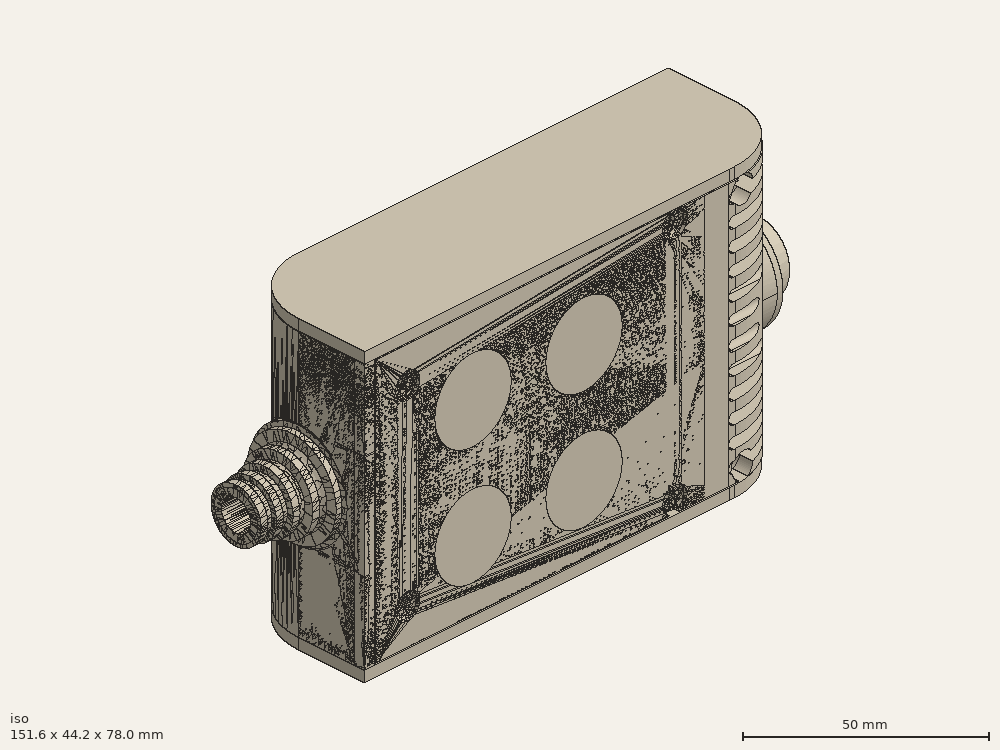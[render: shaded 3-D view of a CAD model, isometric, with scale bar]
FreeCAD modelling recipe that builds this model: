
FCSTD DOCUMENT  (FreeCAD 0.19R0.19.2)
Label: enclosure_175FCStd
License: All rights reserved
LicenseURL: http://en.wikipedia.org/wiki/All_rights_reserved
objects: Part::Revolution×152, Part::MultiFuse×146, Part::Feature×146, Sketcher::SketchObject×82, Part::Cut×70, Part::Cylinder×70, Part::Extrusion×67, Part::Fillet×58, Part::Box×36, App::MeasureDistance×4
note: 827 computed .brp shape members not serialized (recipe doc carries the construction recipe); baked Part::Feature solids carry a one-line shape summary decoded from their .brp

FEATURE [Sketcher::SketchObject] Sketch  label="topSketch"
  FullyConstrained = true
  sketch-geometry (20):
    g0: LineSegment StartX=5.21097e-06 StartY=3 StartZ=0 EndX=5.21097e-06 EndY=19 EndZ=0
    g1: ArcOfCircle CenterX=19 CenterY=19 CenterZ=0 NormalX=0 NormalY=0 NormalZ=1 AngleXU=0 Radius=19 StartAngle=1.5708 EndAngle=3.14159
    g2: ArcOfCircle CenterX=19 CenterY=19 CenterZ=0 NormalX=0 NormalY=0 NormalZ=1 AngleXU=0 Radius=16 StartAngle=1.5708 EndAngle=3.14159
    g3: LineSegment StartX=114 StartY=35 StartZ=0 EndX=19 EndY=35 EndZ=0
    g4: LineSegment StartX=5.21097e-06 StartY=3 StartZ=0 EndX=5.21097e-06 EndY=0 EndZ=0
    g5: LineSegment StartX=3 StartY=0 StartZ=0 EndX=5.21097e-06 EndY=0 EndZ=0
    g6: LineSegment StartX=3 StartY=19 StartZ=0 EndX=3 EndY=0 EndZ=0
    g7: LineSegment StartX=19 StartY=38 StartZ=0 EndX=124 EndY=38 EndZ=0
    g8: Circle CenterX=119 CenterY=35 CenterZ=0 NormalX=0 NormalY=0 NormalZ=1 AngleXU=0 Radius=1
    g9: Circle CenterX=121 CenterY=35 CenterZ=0 NormalX=0 NormalY=0 NormalZ=1 AngleXU=0 Radius=1
    g10: Circle CenterX=121 CenterY=33 CenterZ=0 NormalX=0 NormalY=0 NormalZ=1 AngleXU=0 Radius=1
    g11: BSplineCurve PolesCount=3 KnotsCount=2 Degree=2 IsPeriodic=0
    g12: GeomPoint X=119 Y=35 Z=0
    g13: GeomPoint X=121 Y=33 Z=0
    g14: LineSegment StartX=119 StartY=35 StartZ=0 EndX=114 EndY=35 EndZ=0
    g15: ArcOfCircle CenterX=105 CenterY=19 CenterZ=0 NormalX=0 NormalY=0 NormalZ=1 AngleXU=0 Radius=19 StartAngle=5.7297 EndAngle=6.28319
    g16: ArcOfCircle CenterX=105 CenterY=19 CenterZ=0 NormalX=0 NormalY=0 NormalZ=1 AngleXU=0 Radius=16 StartAngle=5.60905 EndAngle=6.28319
    g17: LineSegment StartX=121 StartY=33 StartZ=0 EndX=121 EndY=19 EndZ=0
    g18: LineSegment StartX=124 StartY=38 StartZ=0 EndX=124 EndY=19 EndZ=0
    g19: LineSegment StartX=117.5 StartY=9.01251 StartZ=0 EndX=121.163 EndY=9.0125 EndZ=0
  constraints (46):
    c: Vertical(g0)
    c: Block(g0)
    c: Coincident(g1,g0)
    c: Block(g1)
    c: Coincident(g2,g1)
    c: Block(g2)
    c: Coincident(g3,g2)
    c: Horizontal(g3)
    c: Tangent(g3,g2)
    c: Coincident(g4,g0)
    c: Distance(g4) = 3
    c: Vertical(g4)
    c: Coincident(g5,g4)
    c: Horizontal(g5)
    c: Coincident(g6,g2)
    c: Coincident(g6,g5)
    c: Vertical(g6)
    c: Horizontal(g7)
    c: Distance(g7) = 105
    c: Coincident(g7,g1)
    c: Block(g3)
    c: Weight(g8) = 1
    c: Equal(g8,g9)
    c: Equal(g8,g10)
    c: InternalAlignment(g8,g11)
    c: InternalAlignment(g9,g11)
    c: InternalAlignment(g10,g11)
    c: InternalAlignment(g12,g11)
    c: InternalAlignment(g13,g11)
    c: Block(g11)
    c: Coincident(g14,g11)
    c: Coincident(g14,g3)
    c: Horizontal(g14)
    c: Block(g15)
    c: Coincident(g16,g15)
    c: Block(g16)
    c: Coincident(g17,g11)
    c: Coincident(g17,g16)
    c: Vertical(g17)
    c: Distance(g17) = 14
    c: Coincident(g18,g7)
    c: Coincident(g18,g15)
    c: Vertical(g18)
    c: Distance(g18) = 19
    c: Coincident(g19,g16)
    c: Coincident(g19,g15)
FEATURE [Sketcher::SketchObject] Sketch001  label="bottomSketch"
  FullyConstrained = true
  sketch-geometry (32):
    g0: LineSegment StartX=3.3 StartY=-6.03275e-07 StartZ=0 EndX=98 EndY=-6.03275e-07 EndZ=0
    g1: ArcOfCircle CenterX=98 CenterY=19 CenterZ=0 NormalX=0 NormalY=0 NormalZ=1 AngleXU=0 Radius=19 StartAngle=4.71239 EndAngle=5.71103
    g2: LineSegment StartX=6.3 StartY=8 StartZ=0 EndX=3.3 EndY=8 EndZ=0
    g3: LineSegment StartX=3.3 StartY=8 StartZ=0 EndX=3.3 EndY=-6.03275e-07 EndZ=0
    g4: ArcOfCircle CenterX=8.3 CenterY=5 CenterZ=0 NormalX=0 NormalY=0 NormalZ=1 AngleXU=0 Radius=2 StartAngle=3.14159 EndAngle=4.71239
    g5: LineSegment StartX=6.3 StartY=8 StartZ=0 EndX=6.3 EndY=5 EndZ=0
    g6: ArcOfCircle CenterX=98 CenterY=19 CenterZ=0 NormalX=0 NormalY=0 NormalZ=1 AngleXU=0 Radius=12.7 StartAngle=4.71239 EndAngle=6.28319
    g7: LineSegment StartX=94.7 StartY=3 StartZ=0 EndX=8.3 EndY=3 EndZ=0
    g8-g12: Circle x5 (B-spline internal-alignment scaffolding for g13; pole/knot coordinates omitted)
    g13: BSplineCurve PolesCount=5 KnotsCount=3 Degree=3 IsPeriodic=0
    g14: GeomPoint X=98 Y=6.3 Z=0
    g15: GeomPoint X=96.3938 Y=4.71946 Z=0
    g16: GeomPoint X=94.7 Y=3 Z=0
    g17-g23: Circle x7 (B-spline internal-alignment scaffolding for g24; pole/knot coordinates omitted)
    g24: BSplineCurve PolesCount=7 KnotsCount=5 Degree=3 IsPeriodic=0
    g25-g29: GeomPoint x5 (B-spline internal-alignment scaffolding for g24; pole/knot coordinates omitted)
    g30: ArcOfCircle CenterX=98 CenterY=19 CenterZ=0 NormalX=0 NormalY=0 NormalZ=1 AngleXU=0 Radius=15.7 StartAngle=5.81226 EndAngle=6.28319
    g31: LineSegment StartX=110.7 StartY=19 StartZ=0 EndX=113.7 EndY=19 EndZ=0
  constraints (41):
    c: Horizontal(g0)
    c: Coincident(g1,g0)
    c: Block(g1)
    c: Horizontal(g2)
    c: Distance(g2) = 3
    c: Coincident(g3,g2)
    c: Vertical(g3)
    c: Coincident(g3,g0)
    c: Block(g4)
    c: Block(g2)
    c: Coincident(g5,g2)
    c: Coincident(g5,g4)
    c: Vertical(g5)
    c: Coincident(g6,g1)
    c: Block(g6)
    c: Coincident(g7,g4)
    c: Horizontal(g7)
    c: Block(g0)
    c: Block(g7)
    c: Block(g3)
    c: Coincident(g13,g6)
    c: Weight(g8) = 1
    c: Equal(g8, g9-g12) x4
    c: Coincident(g13,g7)
    c: InternalAlignment(g8-g12 -> g13) x5
    c: InternalAlignment(g14,g13)
    c: InternalAlignment(g15,g13)
    c: InternalAlignment(g16,g13)
    c: Block(g13)
    c: Weight(g17) = 1
    c: Equal(g17, g18-g23) x6
    c: Coincident(g24,g1)
    c: InternalAlignment(g17-g23 -> g24) x7
    c: InternalAlignment(g25-g29 -> g24) x5
    c: Block(g24)
    c: Coincident(g30,g24)
    c: Coincident(g31,g6)
    c: Coincident(g31,g30)
    c: Horizontal(g31)
    c: Block(g31)
    c: Block(g30)
FEATURE [Part::Extrusion] Extrude  label="top"
  Base = -> Sketch
  Dir = (0,0,1)
  DirMode = 2
  FaceMakerClass = Part::FaceMakerBullseye
  LengthFwd = 72
  LengthRev = 0
  Solid = true
  Symmetric = false
FEATURE [Part::Extrusion] Extrude001  label="bottom"
  Base = -> Sketch001
  Dir = (0,0,1)
  DirMode = 2
  FaceMakerClass = Part::FaceMakerBullseye
  LengthFwd = 71.4
  LengthRev = 0
  Placement = pos=(0,0,0.3) rot=(0,0,1;0rad)
  Solid = true
  Symmetric = false
FEATURE [Sketcher::SketchObject] Sketch002  label="topSketch001"
  FullyConstrained = true
  sketch-geometry (8):
    g0: ArcOfCircle CenterX=19 CenterY=19.0975 CenterZ=0 NormalX=0 NormalY=0 NormalZ=1 AngleXU=0 Radius=18.9025 StartAngle=1.5708 EndAngle=3.14674
    g1: LineSegment StartX=0.0977805 StartY=19.0003 StartZ=0 EndX=0.0977805 EndY=0.000251602 EndZ=0
    g2: LineSegment StartX=19 StartY=38 StartZ=0 EndX=124 EndY=38 EndZ=0
    g3: LineSegment StartX=0.0977805 StartY=0.000251602 StartZ=0 EndX=105.098 EndY=0.000251602 EndZ=0
    g4: LineSegment StartX=124 StartY=38 StartZ=0 EndX=125.616 EndY=38 EndZ=0
    g5: LineSegment StartX=105.098 StartY=0.000251602 StartZ=0 EndX=106.713 EndY=0.000251602 EndZ=0
    g6: ArcOfCircle CenterX=106.616 CenterY=19 CenterZ=0 NormalX=0 NormalY=0 NormalZ=1 AngleXU=0 Radius=19 StartAngle=4.71754 EndAngle=6.28319
    g7: LineSegment StartX=125.616 StartY=38 StartZ=0 EndX=125.616 EndY=19 EndZ=0
  constraints (21):
    c: Block(g0)
    c: Coincident(g1,g0)
    c: Vertical(g1)
    c: Horizontal(g2)
    c: Distance(g2) = 105
    c: Coincident(g2,g0)
    c: Distance(g1) = 19
    c: Coincident(g3,g1)
    c: Horizontal(g3)
    c: Distance(g3) = 105
    c: Coincident(g4,g2)
    c: Horizontal(g4)
    c: Distance(g4) = 1.61553
    c: Horizontal(g5)
    c: Equal(g4,g5) = 1.61553
    c: Coincident(g5,g3)
    c: Block(g6)
    c: Coincident(g6,g5)
    c: Coincident(g7,g4)
    c: Coincident(g7,g6)
    c: Vertical(g7)
FEATURE [Part::Extrusion] Extrude002  label="sideA"
  Base = -> Sketch002
  Dir = (0,0,1)
  DirMode = 2
  FaceMakerClass = Part::FaceMakerBullseye
  LengthFwd = 3
  LengthRev = 0
  Placement = pos=(0,0,-3) rot=(0,0,1;0rad)
  Solid = true
  Symmetric = false
FEATURE [Sketcher::SketchObject] Sketch003  label="topSketch002"
  FullyConstrained = true
  sketch-geometry (6):
    g0: LineSegment StartX=19 StartY=38 StartZ=0 EndX=117 EndY=38 EndZ=0
    g1: ArcOfCircle CenterX=19 CenterY=19 CenterZ=0 NormalX=0 NormalY=0 NormalZ=1 AngleXU=0 Radius=19 StartAngle=1.5708 EndAngle=3.14159
    g2: LineSegment StartX=117 StartY=38 StartZ=0 EndX=117 EndY=19 EndZ=0
    g3: LineSegment StartX=98 StartY=1.0161e-12 StartZ=0 EndX=5.22862e-06 EndY=1.0161e-12 EndZ=0
    g4: LineSegment StartX=5.22862e-06 StartY=19 StartZ=0 EndX=5.22862e-06 EndY=1.0161e-12 EndZ=0
    g5: ArcOfCircle CenterX=98 CenterY=19 CenterZ=0 NormalX=0 NormalY=0 NormalZ=1 AngleXU=0 Radius=19 StartAngle=4.71239 EndAngle=6.28319
  constraints (16):
    c: Horizontal(g0)
    c: Distance(g0) = 98
    c: Coincident(g1,g0)
    c: Block(g1)
    c: Coincident(g2,g0)
    c: Vertical(g2)
    c: Distance(g2) = 19
    c: Horizontal(g3)
    c: Coincident(g4,g1)
    c: Vertical(g4)
    c: Coincident(g3,g4)
    c: Block(g3)
    c: Coincident(g5,g2)
    c: Coincident(g5,g3)
    c: Block(g0)
    c: Block(g5)
FEATURE [Sketcher::SketchObject] Sketch004
  FullyConstrained = true
  MapMode = 3
  Placement = pos=(0,0,0) rot=(1,0,0;1.5708rad)
  Support = -> [Extrude]
  sketch-geometry (8):
    g0: Circle CenterX=80.351 CenterY=-67.6202 CenterZ=0 NormalX=0 NormalY=0 NormalZ=1 AngleXU=0 Radius=2
    g1: Circle CenterX=80.351 CenterY=-67.6202 CenterZ=0 NormalX=0 NormalY=0 NormalZ=1 AngleXU=0 Radius=3
    g2: Circle CenterX=80.351 CenterY=-4.92017 CenterZ=0 NormalX=0 NormalY=0 NormalZ=1 AngleXU=0 Radius=2
    g3: Circle CenterX=80.351 CenterY=-4.92017 CenterZ=0 NormalX=0 NormalY=0 NormalZ=1 AngleXU=0 Radius=3
    g4: Circle CenterX=23.851 CenterY=-4.92017 CenterZ=0 NormalX=0 NormalY=0 NormalZ=1 AngleXU=0 Radius=2
    g5: Circle CenterX=23.851 CenterY=-4.92017 CenterZ=0 NormalX=0 NormalY=0 NormalZ=1 AngleXU=0 Radius=3
    g6: Circle CenterX=23.851 CenterY=-67.6202 CenterZ=0 NormalX=0 NormalY=0 NormalZ=1 AngleXU=0 Radius=2
    g7: Circle CenterX=23.851 CenterY=-67.6202 CenterZ=0 NormalX=0 NormalY=0 NormalZ=1 AngleXU=0 Radius=3
  constraints (8):
    c: Block(g3)
    c: Block(g2)
    c: Block(g1)
    c: Block(g0)
    c: Block(g6)
    c: Block(g7)
    c: Block(g4)
    c: Block(g5)
FEATURE [Part::Extrusion] Extrude004
  Base = -> Sketch004
  Dir = (0,-1,2e-16)
  DirMode = 2
  FaceMakerClass = Part::FaceMakerBullseye
  LengthFwd = 6
  LengthRev = 0
  Placement = pos=(0,9,0) rot=(0,0,1;0rad)
  Solid = true
  Symmetric = false
FEATURE [Sketcher::SketchObject] Sketch005
  FullyConstrained = true
  MapMode = 3
  Placement = pos=(0,0,0) rot=(1,0,0;1.5708rad)
  Support = -> [Extrude]
  sketch-geometry (8):
    g0: Circle CenterX=80.351 CenterY=-67.6202 CenterZ=0 NormalX=0 NormalY=0 NormalZ=1 AngleXU=0 Radius=3
    g1: Circle CenterX=80.351 CenterY=-4.92017 CenterZ=0 NormalX=0 NormalY=0 NormalZ=1 AngleXU=0 Radius=3
    g2: Circle CenterX=23.851 CenterY=-4.92017 CenterZ=0 NormalX=0 NormalY=0 NormalZ=1 AngleXU=0 Radius=3
    g3: Circle CenterX=23.851 CenterY=-67.6202 CenterZ=0 NormalX=0 NormalY=0 NormalZ=1 AngleXU=0 Radius=3
    g4: Circle CenterX=23.851 CenterY=-67.6202 CenterZ=0 NormalX=0 NormalY=0 NormalZ=1 AngleXU=0 Radius=5
    g5: Circle CenterX=80.351 CenterY=-67.6202 CenterZ=0 NormalX=0 NormalY=0 NormalZ=1 AngleXU=0 Radius=5
    g6: Circle CenterX=23.851 CenterY=-4.92017 CenterZ=0 NormalX=0 NormalY=0 NormalZ=1 AngleXU=0 Radius=5
    g7: Circle CenterX=80.351 CenterY=-4.92017 CenterZ=0 NormalX=0 NormalY=0 NormalZ=1 AngleXU=0 Radius=5
  constraints (8):
    c: Block(g1)
    c: Block(g0)
    c: Block(g3)
    c: Block(g2)
    c: Block(g5)
    c: Block(g4)
    c: Block(g6)
    c: Block(g7)
FEATURE [Part::Extrusion] Extrude005
  Base = -> Sketch005
  Dir = (0,-1,2e-16)
  DirMode = 2
  FaceMakerClass = Part::FaceMakerBullseye
  LengthFwd = 2
  LengthRev = 0
  Solid = true
  Symmetric = false
FEATURE [Sketcher::SketchObject] Sketch006
  FullyConstrained = true
  MapMode = 3
  Placement = pos=(0,0,0) rot=(1,0,0;1.5708rad)
  sketch-geometry (8):
    g0: Circle CenterX=80.351 CenterY=-67.6202 CenterZ=0 NormalX=0 NormalY=0 NormalZ=1 AngleXU=0 Radius=3
    g1: Circle CenterX=80.351 CenterY=-4.92017 CenterZ=0 NormalX=0 NormalY=0 NormalZ=1 AngleXU=0 Radius=3
    g2: Circle CenterX=23.851 CenterY=-4.92017 CenterZ=0 NormalX=0 NormalY=0 NormalZ=1 AngleXU=0 Radius=3
    g3: Circle CenterX=23.851 CenterY=-67.6202 CenterZ=0 NormalX=0 NormalY=0 NormalZ=1 AngleXU=0 Radius=3
    g4: Circle CenterX=23.851 CenterY=-67.6202 CenterZ=0 NormalX=0 NormalY=0 NormalZ=1 AngleXU=0 Radius=5
    g5: Circle CenterX=80.351 CenterY=-67.6202 CenterZ=0 NormalX=0 NormalY=0 NormalZ=1 AngleXU=0 Radius=5
    g6: Circle CenterX=23.851 CenterY=-4.92017 CenterZ=0 NormalX=0 NormalY=0 NormalZ=1 AngleXU=0 Radius=5
    g7: Circle CenterX=80.351 CenterY=-4.92017 CenterZ=0 NormalX=0 NormalY=0 NormalZ=1 AngleXU=0 Radius=5
  constraints (8):
    c: Block(g1)
    c: Block(g0)
    c: Block(g3)
    c: Block(g2)
    c: Block(g5)
    c: Block(g4)
    c: Block(g6)
    c: Block(g7)
FEATURE [Part::Extrusion] Extrude007
  Base = -> Sketch006
  Dir = (0,-1,2e-16)
  DirMode = 2
  FaceMakerClass = Part::FaceMakerBullseye
  LengthFwd = 2
  LengthRev = 0
  Solid = true
  Symmetric = false
FEATURE [Part::Fillet] Fillet
  Base = -> Extrude007
  Edges = 4 edges r=1.99: [Edge6,Edge12,Edge18,Edge24]
FEATURE [Part::Cut] Cut
  Base = -> Extrude005
  Placement = pos=(0,5,0) rot=(0,0,1;0rad)
  Tool = -> Fillet
FEATURE [Part::MultiFuse] Fusion  label="pCBScrews"
  Placement = pos=(-2.5,0,72.3) rot=(0,0,1;0rad)
  Shapes = -> [Extrude004,Cut]
FEATURE [App::MeasureDistance] Distance  label="Distance: 0.69 mm"
  Distance = 0.685967
  P1 = (24.0138,2.9647,0.3)
  P2 = (23.8901,3,-0.373787)
FEATURE [App::MeasureDistance] Distance001  label="Distance: 0.53 mm"
  Distance = 0.533607
  P1 = (80.2939,3,72.2334)
  P2 = (80.281,2.99661,71.7)
FEATURE [Part::Fillet] Fillet001
  Base = -> Extrude001
  Edges = 1 edges r=2.4: [Edge17]
FEATURE [Part::Fillet] Fillet002  label="bottom001"
  Base = -> Fillet001
  Edges = 1 edges r=2.4: [Edge36]
FEATURE [Part::Fillet] Fillet003  label="top001"
  Base = -> Extrude
  Edges = 1 edges r=2: [Edge1]
FEATURE [Sketcher::SketchObject] Sketch007
  FullyConstrained = true
  sketch-geometry (16):
    g0: LineSegment StartX=4 StartY=0 StartZ=0 EndX=4 EndY=2.4 EndZ=0
    g1: LineSegment StartX=4 StartY=2.4 StartZ=0 EndX=7 EndY=2.4 EndZ=0
    g2: LineSegment StartX=4 StartY=0 StartZ=0 EndX=5.7 EndY=0 EndZ=0
    g3: LineSegment StartX=5.7 StartY=0 StartZ=0 EndX=5.7 EndY=-5.6 EndZ=0
    g4-g8: Circle x5 (B-spline internal-alignment scaffolding for g9; pole/knot coordinates omitted)
    g9: BSplineCurve PolesCount=5 KnotsCount=3 Degree=3 IsPeriodic=0
    g10: GeomPoint X=7 Y=2.4 Z=0
    g11: GeomPoint X=10.4582 Y=-1.55472 Z=0
    g12: GeomPoint X=14 Y=-5.6 Z=0
    g13: LineSegment StartX=14 StartY=-5.6 StartZ=0 EndX=14 EndY=-14.1 EndZ=0
    g14: LineSegment StartX=14 StartY=-14.1 StartZ=0 EndX=6.5 EndY=-14.1 EndZ=0
    g15: LineSegment StartX=5.7 StartY=-5.6 StartZ=0 EndX=6.5 EndY=-14.1 EndZ=0
  constraints (28):
    c: Distance(g0) = 2.4
    c: Vertical(g0)
    c: Block(g0)
    c: Coincident(g1,g0)
    c: Horizontal(g1)
    c: Distance(g1) = 3
    c: Coincident(g2,g0)
    c: Horizontal(g2)
    c: Distance(g2) = 1.7
    c: Coincident(g3,g2)
    c: Vertical(g3)
    c: Distance(g3) = 5.6
    c: Coincident(g9,g1)
    c: Weight(g4) = 1
    c: Equal(g4, g5-g8) x4
    c: InternalAlignment(g4-g8 -> g9) x5
    c: InternalAlignment(g10,g9)
    c: InternalAlignment(g11,g9)
    c: InternalAlignment(g12,g9)
    c: Block(g9)
    c: Coincident(g13,g9)
    c: Vertical(g13)
    c: Distance(g13) = 8.5
    c: Coincident(g14,g13)
    c: Horizontal(g14)
    c: Distance(g14) = 7.5
    c: Coincident(g15,g3)
    c: Coincident(g15,g14)
FEATURE [Part::Feature] Face
  shape: bbox 10 x 16.5 x 2e-07 mm, 1 faces, 0 solids (baked)
FEATURE [Part::Revolution] Revolve  label="plugHousing"
  Angle = 360
  Axis = (0,1,0)
  Base = (0,0,0)
  FaceMakerClass = Part::FaceMakerBullseye
  Placement = pos=(0,0,36.15) rot=(0,0,1;0rad)
  Solid = false
  Source = -> Face
  Symmetric = false
FEATURE [Part::Feature] Face001
  shape: bbox 10 x 16.5 x 2e-07 mm, 1 faces, 0 solids (baked)
FEATURE [Part::Revolution] Revolve001  label="plugHousing001"
  Angle = 360
  Axis = (0,1,0)
  Base = (0,0,0)
  FaceMakerClass = Part::FaceMakerBullseye
  Placement = pos=(0,0,36.15) rot=(0,0,1;0rad)
  Solid = false
  Source = -> Face001
  Symmetric = false
FEATURE [Part::MultiFuse] Fusion001  label="plugHousing002"
  Placement = pos=(0,0,0) rot=(0,0,1;1.5708rad)
  Shapes = -> [Revolve001,Revolve]
FEATURE [Part::Feature] Face002
  shape: bbox 10 x 16.5 x 2e-07 mm, 1 faces, 0 solids (baked)
FEATURE [Part::Revolution] Revolve003  label="plugHousing005"
  Angle = 360
  Axis = (0,1,0)
  Base = (0,0,0)
  FaceMakerClass = Part::FaceMakerBullseye
  Placement = pos=(0,0,36.15) rot=(0,0,1;0rad)
  Solid = false
  Source = -> Face002
  Symmetric = false
FEATURE [Part::Feature] Face003
  shape: bbox 10 x 16.5 x 2e-07 mm, 1 faces, 0 solids (baked)
FEATURE [Part::Revolution] Revolve002  label="plugHousing003"
  Angle = 360
  Axis = (0,1,0)
  Base = (0,0,0)
  FaceMakerClass = Part::FaceMakerBullseye
  Placement = pos=(0,0,36.15) rot=(0,0,1;0rad)
  Solid = false
  Source = -> Face003
  Symmetric = false
FEATURE [Part::MultiFuse] Fusion002  label="plugHousing004"
  Placement = pos=(0,0,0) rot=(0,0,1;1.5708rad)
  Shapes = -> [Revolve002,Revolve003]
FEATURE [Part::MultiFuse] Fusion003  label="plugHousing006"
  Placement = pos=(0,19,0) rot=(0,0,1;3.14159rad)
  Shapes = -> [Fusion002,Fusion001]
FEATURE [Part::Feature] Face004
  shape: bbox 10 x 16.5 x 2e-07 mm, 1 faces, 0 solids (baked)
FEATURE [Part::Revolution] Revolve006  label="plugHousing010"
  Angle = 360
  Axis = (0,1,0)
  Base = (0,0,0)
  FaceMakerClass = Part::FaceMakerBullseye
  Placement = pos=(0,0,36.15) rot=(0,0,1;0rad)
  Solid = false
  Source = -> Face004
  Symmetric = false
FEATURE [Part::Feature] Face005
  shape: bbox 10 x 16.5 x 2e-07 mm, 1 faces, 0 solids (baked)
FEATURE [Part::Revolution] Revolve007  label="plugHousing011"
  Angle = 360
  Axis = (0,1,0)
  Base = (0,0,0)
  FaceMakerClass = Part::FaceMakerBullseye
  Placement = pos=(0,0,36.15) rot=(0,0,1;0rad)
  Solid = false
  Source = -> Face005
  Symmetric = false
FEATURE [Part::Feature] Face006
  shape: bbox 10 x 16.5 x 2e-07 mm, 1 faces, 0 solids (baked)
FEATURE [Part::Revolution] Revolve004  label="plugHousing007"
  Angle = 360
  Axis = (0,1,0)
  Base = (0,0,0)
  FaceMakerClass = Part::FaceMakerBullseye
  Placement = pos=(0,0,36.15) rot=(0,0,1;0rad)
  Solid = false
  Source = -> Face006
  Symmetric = false
FEATURE [Part::MultiFuse] Fusion004  label="plugHousing009"
  Placement = pos=(0,0,0) rot=(0,0,1;1.5708rad)
  Shapes = -> [Revolve004,Revolve007]
FEATURE [Part::Feature] Face007
  shape: bbox 10 x 16.5 x 2e-07 mm, 1 faces, 0 solids (baked)
FEATURE [Part::Revolution] Revolve005  label="plugHousing008"
  Angle = 360
  Axis = (0,1,0)
  Base = (0,0,0)
  FaceMakerClass = Part::FaceMakerBullseye
  Placement = pos=(0,0,36.15) rot=(0,0,1;0rad)
  Solid = false
  Source = -> Face007
  Symmetric = false
FEATURE [Part::MultiFuse] Fusion005  label="plugHousing012"
  Placement = pos=(0,0,0) rot=(0,0,1;1.5708rad)
  Shapes = -> [Revolve006,Revolve005]
FEATURE [Part::MultiFuse] Fusion006  label="plugHousing013"
  Placement = pos=(0,19,0) rot=(0,0,1;3.14159rad)
  Shapes = -> [Fusion005,Fusion004]
FEATURE [Part::MultiFuse] Fusion007  label="plugHousing014"
  Placement = pos=(122.621,0,-0.15) rot=(0,0,1;0rad)
  Shapes = -> [Fusion003,Fusion006]
FEATURE [Part::Cylinder] Cylinder002
  Angle = 360
  AttacherType = Attacher::AttachEngine3D
  Height = 20
  Placement = pos=(0,0,36.15) rot=(0,0,1;0rad)
  Radius = 4
FEATURE [Part::Cylinder] Cylinder003
  Angle = 360
  AttacherType = Attacher::AttachEngine3D
  Height = 10
  Placement = pos=(0,0,36.15) rot=(0,0,1;0rad)
  Radius = 4
FEATURE [Part::MultiFuse] Fusion009  label="removeToCreateHoleForPlugHousing"
  Placement = pos=(70,19,36.15) rot=(0,1,0;1.5708rad)
  Shapes = -> [Cylinder002,Cylinder003]
FEATURE [Part::Cylinder] Cylinder004
  Angle = 360
  AttacherType = Attacher::AttachEngine3D
  Height = 20
  Placement = pos=(0,0,36.15) rot=(0,0,1;0rad)
  Radius = 4
FEATURE [Part::Cylinder] Cylinder005
  Angle = 360
  AttacherType = Attacher::AttachEngine3D
  Height = 10
  Placement = pos=(0,0,36.15) rot=(0,0,1;0rad)
  Radius = 4
FEATURE [Part::MultiFuse] Fusion010  label="removeToCreateHoleForPlugHousing001"
  Placement = pos=(70,19,36.15) rot=(0,1,0;1.5708rad)
  Shapes = -> [Cylinder004,Cylinder005]
FEATURE [Part::Cut] Cut001
  Base = -> Fillet003
  Tool = -> Fusion010
FEATURE [Part::Cut] Cut002  label="Bottom"
  Base = -> Fillet002
  Tool = -> Fusion009
FEATURE [Part::Feature] Face008
  shape: bbox 10 x 16.5 x 2e-07 mm, 1 faces, 0 solids (baked)
FEATURE [Part::Revolution] Revolve011  label="plugHousing021"
  Angle = 360
  Axis = (0,1,0)
  Base = (0,0,0)
  FaceMakerClass = Part::FaceMakerBullseye
  Placement = pos=(0,0,36.15) rot=(0,0,1;0rad)
  Solid = false
  Source = -> Face008
  Symmetric = false
FEATURE [Part::Feature] Face009
  shape: bbox 10 x 16.5 x 2e-07 mm, 1 faces, 0 solids (baked)
FEATURE [Part::Revolution] Revolve012  label="plugHousing022"
  Angle = 360
  Axis = (0,1,0)
  Base = (0,0,0)
  FaceMakerClass = Part::FaceMakerBullseye
  Placement = pos=(0,0,36.15) rot=(0,0,1;0rad)
  Solid = false
  Source = -> Face009
  Symmetric = false
FEATURE [Part::Feature] Face010 .. Face013  x4 (patterned run collapsed; names and placements below)
  shape: bbox 10 x 16.5 x 2e-07 mm, 1 faces, 0 solids (baked)
FEATURE [Part::Revolution] Revolve015  label="plugHousing027"
  Angle = 360
  Axis = (0,1,0)
  Base = (0,0,0)
  FaceMakerClass = Part::FaceMakerBullseye
  Placement = pos=(0,0,36.15) rot=(0,0,1;0rad)
  Solid = false
  Source = -> Face013
  Symmetric = false
FEATURE [Part::Feature] Face014
  shape: bbox 10 x 16.5 x 2e-07 mm, 1 faces, 0 solids (baked)
FEATURE [Part::Feature] Face015
  shape: bbox 10 x 16.5 x 2e-07 mm, 1 faces, 0 solids (baked)
FEATURE [Part::Feature] Face016
  shape: bbox 10 x 16.5 x 2e-07 mm, 1 faces, 0 solids (baked)
FEATURE [Part::Revolution] Revolve019  label="plugHousing033"
  Angle = 360
  Axis = (0,1,0)
  Base = (0,0,0)
  FaceMakerClass = Part::FaceMakerBullseye
  Placement = pos=(0,0,36.15) rot=(0,0,1;0rad)
  Solid = false
  Source = -> Face016
  Symmetric = false
FEATURE [Part::Feature] Face017
  shape: bbox 10 x 16.5 x 2e-07 mm, 1 faces, 0 solids (baked)
FEATURE [Part::Revolution] Revolve020  label="plugHousing034"
  Angle = 360
  Axis = (0,1,0)
  Base = (0,0,0)
  FaceMakerClass = Part::FaceMakerBullseye
  Placement = pos=(0,0,36.15) rot=(0,0,1;0rad)
  Solid = false
  Source = -> Face017
  Symmetric = false
FEATURE [Part::Feature] Face018
  shape: bbox 10 x 16.5 x 2e-07 mm, 1 faces, 0 solids (baked)
FEATURE [Part::Revolution] Revolve016  label="plugHousing030"
  Angle = 360
  Axis = (0,1,0)
  Base = (0,0,0)
  FaceMakerClass = Part::FaceMakerBullseye
  Placement = pos=(0,0,36.15) rot=(0,0,1;0rad)
  Solid = false
  Source = -> Face018
  Symmetric = false
FEATURE [Part::MultiFuse] Fusion020  label="plugHousing038"
  Placement = pos=(0,0,0) rot=(0,0,1;1.5708rad)
  Shapes = -> [Revolve016,Revolve020]
FEATURE [Part::Feature] Face019
  shape: bbox 10 x 16.5 x 2e-07 mm, 1 faces, 0 solids (baked)
FEATURE [Part::Feature] Face020
  shape: bbox 10 x 16.5 x 2e-07 mm, 1 faces, 0 solids (baked)
FEATURE [Part::Revolution] Revolve017  label="plugHousing031"
  Angle = 360
  Axis = (0,1,0)
  Base = (0,0,0)
  FaceMakerClass = Part::FaceMakerBullseye
  Placement = pos=(0,0,36.15) rot=(0,0,1;0rad)
  Solid = false
  Source = -> Face020
  Symmetric = false
FEATURE [Part::MultiFuse] Fusion021  label="plugHousing039"
  Placement = pos=(0,0,0) rot=(0,0,1;1.5708rad)
  Shapes = -> [Revolve019,Revolve017]
FEATURE [Part::MultiFuse] Fusion023  label="plugHousing041"
  Placement = pos=(0,19,0) rot=(0,0,1;3.14159rad)
  Shapes = -> [Fusion021,Fusion020]
FEATURE [Part::Revolution] Revolve022  label="plugHousing043"
  Angle = 360
  Axis = (0,1,0)
  Base = (0,0,0)
  FaceMakerClass = Part::FaceMakerBullseye
  Placement = pos=(0,0,36.15) rot=(0,0,1;0rad)
  Solid = false
  Source = -> Face019
  Symmetric = false
FEATURE [Part::Feature] Face021
  shape: bbox 10 x 16.5 x 2e-07 mm, 1 faces, 0 solids (baked)
FEATURE [Part::Revolution] Revolve023  label="plugHousing044"
  Angle = 360
  Axis = (0,1,0)
  Base = (0,0,0)
  FaceMakerClass = Part::FaceMakerBullseye
  Placement = pos=(0,0,36.15) rot=(0,0,1;0rad)
  Solid = false
  Source = -> Face021
  Symmetric = false
FEATURE [Part::Feature] Face022
  shape: bbox 10 x 16.5 x 2e-07 mm, 1 faces, 0 solids (baked)
FEATURE [Part::Revolution] Revolve018  label="plugHousing032"
  Angle = 360
  Axis = (0,1,0)
  Base = (0,0,0)
  FaceMakerClass = Part::FaceMakerBullseye
  Placement = pos=(0,0,36.15) rot=(0,0,1;0rad)
  Solid = false
  Source = -> Face022
  Symmetric = false
FEATURE [Part::MultiFuse] Fusion022  label="plugHousing040"
  Placement = pos=(0,0,0) rot=(0,0,1;1.5708rad)
  Shapes = -> [Revolve018,Revolve023]
FEATURE [Part::Feature] Face023
  shape: bbox 10 x 16.5 x 2e-07 mm, 1 faces, 0 solids (baked)
FEATURE [Part::Revolution] Revolve021  label="plugHousing035"
  Angle = 360
  Axis = (0,1,0)
  Base = (0,0,0)
  FaceMakerClass = Part::FaceMakerBullseye
  Placement = pos=(0,0,36.15) rot=(0,0,1;0rad)
  Solid = false
  Source = -> Face023
  Symmetric = false
FEATURE [Part::MultiFuse] Fusion018  label="plugHousing036"
  Placement = pos=(0,0,0) rot=(0,0,1;1.5708rad)
  Shapes = -> [Revolve022,Revolve021]
FEATURE [Part::MultiFuse] Fusion019  label="plugHousing037"
  Placement = pos=(0,19,0) rot=(0,0,1;3.14159rad)
  Shapes = -> [Fusion018,Fusion022]
FEATURE [Part::MultiFuse] Fusion024  label="plugHousing042"
  Placement = pos=(122.621,0,-0.15) rot=(0,0,1;0rad)
  Shapes = -> [Fusion023,Fusion019]
FEATURE [Part::Cylinder] Cylinder006
  Angle = 360
  AttacherType = Attacher::AttachEngine3D
  Height = 20
  Placement = pos=(0,0,36.15) rot=(0,0,1;0rad)
  Radius = 14.3
FEATURE [Part::Cylinder] Cylinder007
  Angle = 360
  AttacherType = Attacher::AttachEngine3D
  Height = 10
  Placement = pos=(0,0,36.15) rot=(0,0,1;0rad)
  Radius = 4
FEATURE [Part::MultiFuse] Fusion026  label="removeToCreteHoleForPlugHousing"
  Placement = pos=(70,19,36) rot=(0,1,0;1.5708rad)
  Shapes = -> [Cylinder006,Cylinder007]
FEATURE [Part::Box] Box001  label="Cube001"
  AttacherType = Attacher::AttachEngine3D
  Height = 28
  Length = 3
  Placement = pos=(110.7,19,22) rot=(0,0,1;0rad)
  Width = 15.7
FEATURE [Part::Cut] Cut003  label="top002"
  Base = -> Cut001
  Tool = -> Fusion007
FEATURE [Part::Revolution] Revolve008  label="plugHousing015"
  Angle = 360
  Axis = (0,1,0)
  Base = (0,0,0)
  FaceMakerClass = Part::FaceMakerBullseye
  Placement = pos=(0,0,36.15) rot=(0,0,1;0rad)
  Solid = false
  Source = -> Face010
  Symmetric = false
FEATURE [Part::MultiFuse] Fusion013  label="plugHousing020"
  Placement = pos=(0,0,0) rot=(0,0,1;1.5708rad)
  Shapes = -> [Revolve008,Revolve012]
FEATURE [Part::Cut] Cut004  label="top003"
  Base = -> Cut003
  Placement = pos=(1,0,0) rot=(0,0,1;0rad)
  Tool = -> Fusion026
FEATURE [Part::Cylinder] Cylinder008
  Angle = 360
  AttacherType = Attacher::AttachEngine3D
  Height = 20
  Placement = pos=(0,0,36.15) rot=(0,0,1;0rad)
  Radius = 10.3
FEATURE [Part::Cylinder] Cylinder009
  Angle = 360
  AttacherType = Attacher::AttachEngine3D
  Height = 10
  Placement = pos=(0,0,36.15) rot=(0,0,1;0rad)
  Radius = 4
FEATURE [Part::MultiFuse] Fusion027  label="removeToCreteHoleForPlugHousing001"
  Placement = pos=(70,19,36) rot=(0,1,0;1.5708rad)
  Shapes = -> [Cylinder008,Cylinder009]
FEATURE [Part::Cut] Cut005  label="plugHousingTab"
  Base = -> Box001
  Tool = -> Fusion027
FEATURE [Part::MultiFuse] Fusion028  label="plugHousing045"
  Shapes = -> [Fusion024,Cut005]
FEATURE [Part::Box] Box002  label="Cube002"
  AttacherType = Attacher::AttachEngine3D
  Height = 28.8
  Length = 3
  Placement = pos=(107.3,28,21.6) rot=(0,0,1;0rad)
  Width = 7
FEATURE [Part::Box] Box003  label="Cube003"
  AttacherType = Attacher::AttachEngine3D
  Height = 3
  Length = 6.4
  Placement = pos=(107.3,28,18.6) rot=(0,0,1;0rad)
  Width = 7
FEATURE [Part::Box] Box004  label="Cube004"
  AttacherType = Attacher::AttachEngine3D
  Height = 3
  Length = 6.4
  Placement = pos=(107.3,28,50.4) rot=(0,0,1;0rad)
  Width = 7
FEATURE [Part::MultiFuse] Fusion029  label="plugHousingBracketHolder"
  Shapes = -> [Box004,Box002,Box003]
FEATURE [Part::Cylinder] Cylinder010
  Angle = 360
  AttacherType = Attacher::AttachEngine3D
  Height = 20
  Placement = pos=(0,0,36.15) rot=(0,0,1;0rad)
  Radius = 14.3
FEATURE [Part::Cylinder] Cylinder011
  Angle = 360
  AttacherType = Attacher::AttachEngine3D
  Height = 10
  Placement = pos=(0,0,36.15) rot=(0,0,1;0rad)
  Radius = 4
FEATURE [Part::MultiFuse] Fusion030  label="removeToCreteHoleForPlugHousing002"
  Placement = pos=(70,19,36) rot=(0,1,0;1.5708rad)
  Shapes = -> [Cylinder010,Cylinder011]
FEATURE [Part::Cut] Cut006  label="plugHousingBracketHolder001"
  Base = -> Fusion029
  Tool = -> Fusion030
FEATURE [Part::Cylinder] Cylinder012
  Angle = 360
  AttacherType = Attacher::AttachEngine3D
  Height = 20
  Placement = pos=(0,0,36.15) rot=(0,0,1;0rad)
  Radius = 7
FEATURE [Part::Cylinder] Cylinder013
  Angle = 360
  AttacherType = Attacher::AttachEngine3D
  Height = 10
  Placement = pos=(0,0,36.15) rot=(0,0,1;0rad)
  Radius = 4
FEATURE [Part::MultiFuse] Fusion032  label="removeToCreteHoleForPlugHousing003"
  Placement = pos=(70,19,36) rot=(0,1,0;1.5708rad)
  Shapes = -> [Cylinder012,Cylinder013]
FEATURE [Part::Cut] Cut007  label="bottom002"
  Base = -> Cut002
  Tool = -> Fusion032
FEATURE [Sketcher::SketchObject] Sketch008
  FullyConstrained = true
  sketch-geometry (54):
    g0: LineSegment StartX=-4.2 StartY=0 StartZ=0 EndX=-6.2 EndY=0 EndZ=0
    g1: LineSegment StartX=-14 StartY=-18 StartZ=0 EndX=-14 EndY=-26.5 EndZ=0
    g2: LineSegment StartX=-4.2 StartY=0 StartZ=0 EndX=-4.2 EndY=-13.4877 EndZ=0
    g3: Circle CenterX=-4.2 CenterY=-13.4877 CenterZ=0 NormalX=0 NormalY=0 NormalZ=1 AngleXU=0 Radius=1
    g4: Circle CenterX=-4.2 CenterY=-26.5 CenterZ=0 NormalX=0 NormalY=0 NormalZ=1 AngleXU=0 Radius=1
    g5: Circle CenterX=-8.2 CenterY=-26.5 CenterZ=0 NormalX=0 NormalY=0 NormalZ=1 AngleXU=0 Radius=1
    g6: BSplineCurve PolesCount=3 KnotsCount=2 Degree=2 IsPeriodic=0
    g7: GeomPoint X=-4.2 Y=-13.4877 Z=0
    g8: GeomPoint X=-8.2 Y=-26.5 Z=0
    g9: LineSegment StartX=-14 StartY=-26.5 StartZ=0 EndX=-8.2 EndY=-26.5 EndZ=0
    g10: LineSegment StartX=-10.15 StartY=-12 StartZ=0 EndX=-10.15 EndY=-14 EndZ=0
    g11: LineSegment StartX=-12.8401 StartY=-16 StartZ=0 EndX=-10.1571 EndY=-16 EndZ=0
    g12: LineSegment StartX=-10.15 StartY=-14 StartZ=0 EndX=-8.70761 EndY=-14 EndZ=0
    g13: LineSegment StartX=-12.8401 StartY=-16 StartZ=0 EndX=-12.8401 EndY=-17.6958 EndZ=0
    g14: LineSegment StartX=-10.15 StartY=-12 StartZ=0 EndX=-7.79258 EndY=-12 EndZ=0
    g15: Circle CenterX=-6.2215 CenterY=-2 CenterZ=0 NormalX=0 NormalY=0 NormalZ=1 AngleXU=0 Radius=1
    g16: Circle CenterX=-6.22762 CenterY=-2.58724 CenterZ=0 NormalX=0 NormalY=0 NormalZ=1 AngleXU=0 Radius=1
    g17: Circle CenterX=-6.32538 CenterY=-4 CenterZ=0 NormalX=0 NormalY=0 NormalZ=1 AngleXU=0 Radius=1
    g18: BSplineCurve PolesCount=3 KnotsCount=2 Degree=2 IsPeriodic=0
    g19: GeomPoint X=-6.2215 Y=-2 Z=0
    g20: GeomPoint X=-6.32538 Y=-4 Z=0
    g21: Circle CenterX=-6.48644 CenterY=-5.99526 CenterZ=0 NormalX=0 NormalY=0 NormalZ=1 AngleXU=0 Radius=1
    g22: Circle CenterX=-6.58486 CenterY=-6.99526 CenterZ=0 NormalX=0 NormalY=0 NormalZ=1 AngleXU=0 Radius=1
    g23: Circle CenterX=-6.77343 CenterY=-8 CenterZ=0 NormalX=0 NormalY=0 NormalZ=1 AngleXU=0 Radius=1
    g24: BSplineCurve PolesCount=3 KnotsCount=2 Degree=2 IsPeriodic=0
    g25: GeomPoint X=-6.48644 Y=-5.99526 Z=0
    g26: GeomPoint X=-6.77343 Y=-8 Z=0
    g27: Circle CenterX=-7.19003 CenterY=-10 CenterZ=0 NormalX=0 NormalY=0 NormalZ=1 AngleXU=0 Radius=1
    g28: Circle CenterX=-7.44407 CenterY=-11.0915 CenterZ=0 NormalX=0 NormalY=0 NormalZ=1 AngleXU=0 Radius=1
    g29: Circle CenterX=-7.79258 CenterY=-12 CenterZ=0 NormalX=0 NormalY=0 NormalZ=1 AngleXU=0 Radius=1
    g30: BSplineCurve PolesCount=3 KnotsCount=2 Degree=2 IsPeriodic=0
    g31: GeomPoint X=-7.19003 Y=-10 Z=0
    g32: GeomPoint X=-7.79258 Y=-12 Z=0
    g33: Circle CenterX=-8.70761 CenterY=-14 CenterZ=0 NormalX=0 NormalY=0 NormalZ=1 AngleXU=0 Radius=1
    g34: Circle CenterX=-9.33087 CenterY=-15.1837 CenterZ=0 NormalX=0 NormalY=0 NormalZ=1 AngleXU=0 Radius=1
    g35: Circle CenterX=-10.1571 CenterY=-16 CenterZ=0 NormalX=0 NormalY=0 NormalZ=1 AngleXU=0 Radius=1
    g36: BSplineCurve PolesCount=3 KnotsCount=2 Degree=2 IsPeriodic=0
    g37: GeomPoint X=-8.70761 Y=-14 Z=0
    g38: GeomPoint X=-10.1571 Y=-16 Z=0
    g39: Circle CenterX=-12.8401 CenterY=-17.6958 CenterZ=0 NormalX=0 NormalY=0 NormalZ=1 AngleXU=0 Radius=1
    g40: Circle CenterX=-13.3521 CenterY=-17.9027 CenterZ=0 NormalX=0 NormalY=0 NormalZ=1 AngleXU=0 Radius=1
    g41: Circle CenterX=-14 CenterY=-18 CenterZ=0 NormalX=0 NormalY=0 NormalZ=1 AngleXU=0 Radius=1
    g42: BSplineCurve PolesCount=3 KnotsCount=2 Degree=2 IsPeriodic=0
    g43: GeomPoint X=-12.8401 Y=-17.6958 Z=0
    g44: GeomPoint X=-14 Y=-18 Z=0
    g45: LineSegment StartX=-6.2 StartY=0 StartZ=0 EndX=-7.2 EndY=0 EndZ=0
    g46: LineSegment StartX=-7.2 StartY=0 StartZ=0 EndX=-7.2 EndY=-2 EndZ=0
    g47: LineSegment StartX=-7.2 StartY=-2 StartZ=0 EndX=-6.2215 EndY=-2 EndZ=0
    g48: LineSegment StartX=-6.32538 StartY=-4 StartZ=0 EndX=-7.65538 EndY=-4 EndZ=0
    g49: LineSegment StartX=-7.65538 StartY=-4 StartZ=0 EndX=-7.65538 EndY=-5.99526 EndZ=0
    g50: LineSegment StartX=-7.65538 StartY=-5.99526 StartZ=0 EndX=-6.48644 EndY=-5.99526 EndZ=0
    g51: LineSegment StartX=-6.77343 StartY=-8 StartZ=0 EndX=-8.43343 EndY=-8 EndZ=0
    g52: LineSegment StartX=-8.43343 StartY=-8 StartZ=0 EndX=-8.43343 EndY=-10 EndZ=0
    g53: LineSegment StartX=-8.43343 StartY=-10 StartZ=0 EndX=-7.19003 EndY=-10 EndZ=0
  constraints (112):
    c: Horizontal(g0)
    c: Distance(g0) = 2
    c: Block(g0)
    c: Vertical(g1)
    c: Coincident(g2,g0)
    c: Vertical(g2)
    c: Block(g2)
    c: Coincident(g6,g2)
    c: Weight(g3) = 1
    c: Equal(g3,g4)
    c: Equal(g3,g5)
    c: InternalAlignment(g3,g6)
    c: InternalAlignment(g4,g6)
    c: InternalAlignment(g5,g6)
    c: InternalAlignment(g7,g6)
    c: InternalAlignment(g8,g6)
    c: Block(g6)
    c: Coincident(g9,g1)
    c: Coincident(g9,g6)
    c: Horizontal(g9)
    c: Vertical(g10)
    c: Block(g10)
    c: Horizontal(g11)
    c: Block(g11)
    c: Coincident(g12,g10)
    c: Horizontal(g12)
    c: Block(g12)
    c: Coincident(g13,g11)
    c: Vertical(g13)
    c: Block(g13)
    c: Coincident(g14,g10)
    c: Horizontal(g14)
    c: Block(g14)
    c: Block(g9)
    c: Block(g1)
    c: Weight(g15) = 1
    c: Equal(g15,g16)
    c: Equal(g15,g17)
    c: InternalAlignment(g15,g18)
    c: InternalAlignment(g16,g18)
    c: InternalAlignment(g17,g18)
    c: InternalAlignment(g19,g18)
    c: InternalAlignment(g20,g18)
    c: Weight(g21) = 1
    c: Equal(g21,g22)
    c: Equal(g21,g23)
    c: InternalAlignment(g21,g24)
    c: InternalAlignment(g22,g24)
    c: InternalAlignment(g23,g24)
    c: InternalAlignment(g25,g24)
    c: InternalAlignment(g26,g24)
    c: Weight(g27) = 1
    c: Equal(g27,g28)
    c: Equal(g27,g29)
    c: Coincident(g30,g14)
    c: InternalAlignment(g27,g30)
    c: InternalAlignment(g28,g30)
    c: InternalAlignment(g29,g30)
    c: InternalAlignment(g31,g30)
    c: InternalAlignment(g32,g30)
    c: Coincident(g36,g12)
    c: Weight(g33) = 1
    c: Equal(g33,g34)
    c: Equal(g33,g35)
    c: Coincident(g36,g11)
    c: InternalAlignment(g33,g36)
    c: InternalAlignment(g34,g36)
    c: InternalAlignment(g35,g36)
    c: InternalAlignment(g37,g36)
    c: InternalAlignment(g38,g36)
    c: Coincident(g42,g13)
    c: Weight(g39) = 1
    c: Equal(g39,g40)
    c: Equal(g39,g41)
    c: Coincident(g42,g1)
    c: InternalAlignment(g39,g42)
    c: InternalAlignment(g40,g42)
    c: InternalAlignment(g41,g42)
    c: InternalAlignment(g43,g42)
    c: InternalAlignment(g44,g42)
    c: Block(g18)
    c: Block(g24)
    c: Block(g30)
    c: Block(g36)
    c: Block(g42)
    c: Horizontal(g45)
    c: Coincident(g45,g0)
    c: Vertical(g46)
    c: Coincident(g46,g45)
    c: Coincident(g47,g46)
    c: Coincident(g47,g18)
    c: Horizontal(g47)
    c: Block(g46)
    c: Coincident(g48,g18)
    c: Horizontal(g48)
    c: Distance(g48) = 1.33
    c: Vertical(g49)
    c: Coincident(g49,g48)
    c: Coincident(g50,g49)
    c: Coincident(g50,g24)
    c: Horizontal(g50)
    c: Tangent(g50,g22)
    c: Horizontal(g51)
    c: Coincident(g51,g24)
    c: Block(g51)
    c: Vertical(g52)
    c: Block(g52)
    c: Coincident(g52,g51)
    c: Coincident(g53,g52)
    c: Coincident(g53,g30)
    c: Horizontal(g53)
    c: Distance(g1) = 8.5
FEATURE [Part::Feature] Face024
  shape: bbox 9.8 x 26.5 x 2e-07 mm, 1 faces, 0 solids (baked)
FEATURE [Part::Revolution] Revolve024
  Angle = 360
  Axis = (0,1,0)
  Base = (0,0,0)
  FaceMakerClass = Part::FaceMakerBullseye
  Placement = pos=(0,0,0) rot=(0,0,1;1.5708rad)
  Solid = false
  Source = -> Face024
  Symmetric = false
FEATURE [Part::Feature] Face025
  shape: bbox 9.8 x 26.5 x 2e-07 mm, 1 faces, 0 solids (baked)
FEATURE [Part::Revolution] Revolve025
  Angle = 360
  Axis = (0,1,0)
  Base = (0,0,0)
  FaceMakerClass = Part::FaceMakerBullseye
  Placement = pos=(0,0,0) rot=(0,0,1;1.5708rad)
  Solid = false
  Source = -> Face025
  Symmetric = false
FEATURE [Part::MultiFuse] Fusion033
  Placement = pos=(-18,19,36) rot=(0,0,1;0rad)
  Shapes = -> [Revolve025,Revolve024]
FEATURE [Part::Cylinder] Cylinder014
  Angle = 360
  AttacherType = Attacher::AttachEngine3D
  Height = 20
  Placement = pos=(0,0,36.15) rot=(0,0,1;0rad)
  Radius = 14.3
FEATURE [Part::Cylinder] Cylinder015
  Angle = 360
  AttacherType = Attacher::AttachEngine3D
  Height = 10
  Placement = pos=(0,0,36.15) rot=(0,0,1;0rad)
  Radius = 4
FEATURE [Part::MultiFuse] Fusion034  label="removeToCreteHoleForPlugHousing004"
  Placement = pos=(-42,19,36) rot=(0,1,0;1.5708rad)
  Shapes = -> [Cylinder014,Cylinder015]
FEATURE [Part::Cut] Cut008  label="top004"
  Base = -> Cut004
  Placement = pos=(-1,0,0) rot=(0,0,1;0rad)
  Tool = -> Fusion034
FEATURE [Part::Box] Box005  label="Cube005"
  AttacherType = Attacher::AttachEngine3D
  Height = 28
  Length = 3
  Placement = pos=(110.7,19,22) rot=(0,0,1;0rad)
  Width = 15.7
FEATURE [Part::Cylinder] Cylinder016
  Angle = 360
  AttacherType = Attacher::AttachEngine3D
  Height = 10
  Placement = pos=(0,0,36.15) rot=(0,0,1;0rad)
  Radius = 4
FEATURE [Part::Cylinder] Cylinder017
  Angle = 360
  AttacherType = Attacher::AttachEngine3D
  Height = 20
  Placement = pos=(0,0,36.15) rot=(0,0,1;0rad)
  Radius = 10.3
FEATURE [Part::MultiFuse] Fusion035  label="removeToCreteHoleForPlugHousing005"
  Placement = pos=(70,19,36) rot=(0,1,0;1.5708rad)
  Shapes = -> [Cylinder017,Cylinder016]
FEATURE [Part::Cut] Cut009  label="plugHousingTab001"
  Base = -> Box005
  Placement = pos=(-107.4,-14,0) rot=(0,0,1;0rad)
  Tool = -> Fusion035
FEATURE [Part::Box] Box006  label="Cube006"
  AttacherType = Attacher::AttachEngine3D
  Height = 28
  Length = 3
  Placement = pos=(110.7,19,22) rot=(0,0,1;0rad)
  Width = 15.7
FEATURE [Part::Cylinder] Cylinder018
  Angle = 360
  AttacherType = Attacher::AttachEngine3D
  Height = 10
  Placement = pos=(0,0,36.15) rot=(0,0,1;0rad)
  Radius = 4
FEATURE [Part::Cylinder] Cylinder019
  Angle = 360
  AttacherType = Attacher::AttachEngine3D
  Height = 20
  Placement = pos=(0,0,36.15) rot=(0,0,1;0rad)
  Radius = 10.3
FEATURE [Part::MultiFuse] Fusion036  label="removeToCreteHoleForPlugHousing006"
  Placement = pos=(70,19,36) rot=(0,1,0;1.5708rad)
  Shapes = -> [Cylinder019,Cylinder018]
FEATURE [Part::Cut] Cut010  label="plugHousingTab002"
  Base = -> Box006
  Placement = pos=(-107.4,-14,0) rot=(0,0,1;0rad)
  Tool = -> Fusion036
FEATURE [Part::MultiFuse] Fusion037
  Placement = pos=(9.6,23,0) rot=(0,0,1;3.14159rad)
  Shapes = -> [Cut009,Cut010]
FEATURE [Part::Box] Box  label="Cube"
  AttacherType = Attacher::AttachEngine3D
  Height = 10
  Length = 3
  Placement = pos=(3.3,4,12) rot=(0,0,1;0rad)
  Width = 10
FEATURE [Part::Fillet] Fillet004
  Base = -> Fusion028
  Edges = 1 edges r=2: [Edge25]
FEATURE [Part::Fillet] Fillet005  label="plugHousing046"
  Base = -> Fillet004
  Edges = 1 edges r=2: [Edge8]
FEATURE [Part::Fillet] Fillet006
  Base = -> Box
  Edges = 1 edges r=2: [Edge11]
FEATURE [Part::Box] Box007  label="Cube007"
  AttacherType = Attacher::AttachEngine3D
  Height = 10
  Length = 3
  Placement = pos=(3.3,4,50) rot=(0,0,1;0rad)
  Width = 10
FEATURE [Part::Fillet] Fillet007
  Base = -> Box007
  Edges = 1 edges r=2: [Edge12]
FEATURE [Part::Box] Box008  label="Cube008"
  AttacherType = Attacher::AttachEngine3D
  Height = 28
  Length = 4
  Placement = pos=(5,0,22) rot=(0,0,1;0rad)
  Width = 10
FEATURE [Part::Fillet] Fillet008
  Base = -> Box008
  Edges = 1 edges r=1: [Edge7]
FEATURE [Part::Fillet] Fillet009
  Base = -> Fillet008
  Edges = 1 edges r=2: [Edge5]
FEATURE [Part::Fillet] Fillet010
  Base = -> Fillet009
  Edges = 1 edges r=2: [Edge2]
FEATURE [Sketcher::SketchObject] Sketch009  label="topSketch003"
  FullyConstrained = true
  sketch-geometry (4):
    g0: LineSegment StartX=16.8446 StartY=31.512 StartZ=0 EndX=16.3251 EndY=34.4666 EndZ=0
    g1: ArcOfCircle CenterX=19 CenterY=19.2524 CenterZ=0 NormalX=0 NormalY=0 NormalZ=1 AngleXU=0 Radius=15.4476 StartAngle=1.74483 EndAngle=2.72717
    g2: ArcOfCircle CenterX=19 CenterY=19.2524 CenterZ=0 NormalX=0 NormalY=0 NormalZ=1 AngleXU=0 Radius=12.4476 StartAngle=1.74483 EndAngle=2.73189
    g3: LineSegment StartX=4.86004 StartY=25.4725 StartZ=0 EndX=7.58253 EndY=24.2107 EndZ=0
  constraints (7):
    c: Block(g0)
    c: Coincident(g1,g0)
    c: Coincident(g2,g0)
    c: Coincident(g3,g1)
    c: Coincident(g3,g2)
    c: Block(g1)
    c: Block(g2)
FEATURE [Part::Extrusion] Extrude008
  Base = -> Sketch009
  Dir = (0,0,1)
  DirMode = 2
  FaceMakerClass = Part::FaceMakerBullseye
  LengthFwd = 10
  LengthRev = 0
  Placement = pos=(0,0,31) rot=(0,0,1;0rad)
  Solid = true
  Symmetric = false
FEATURE [Part::Cylinder] Cylinder020
  Angle = 360
  AttacherType = Attacher::AttachEngine3D
  Height = 20
  Placement = pos=(0,0,36.15) rot=(0,0,1;0rad)
  Radius = 8.2
FEATURE [Part::Cylinder] Cylinder021
  Angle = 360
  AttacherType = Attacher::AttachEngine3D
  Height = 10
  Placement = pos=(0,0,36.15) rot=(0,0,1;0rad)
  Radius = 4
FEATURE [Part::MultiFuse] Fusion038  label="removeToCreteHoleForPlugHousing007"
  Placement = pos=(-42,19,36) rot=(0,1,0;1.5708rad)
  Shapes = -> [Cylinder020,Cylinder021]
FEATURE [Part::Cut] Cut011
  Base = -> Extrude008
  Tool = -> Fusion038
FEATURE [Part::Fillet] Fillet011
  Base = -> Cut011
  Edges = 1 edges r=2: [Edge1]
FEATURE [Part::Fillet] Fillet012
  Base = -> Fillet011
  Edges = 1 edges r=2.5: [Edge1]
FEATURE [Part::Fillet] Fillet013
  Base = -> Fillet012
  Edges = 1 edges r=2.5: [Edge2]
FEATURE [Part::Box] Box010  label="Cube010"
  AttacherType = Attacher::AttachEngine3D
  Height = 16
  Length = 8
  Placement = pos=(12.7,31.52,28) rot=(0,0,1;0rad)
  Width = 4
FEATURE [Sketcher::SketchObject] Sketch010  label="topSketch004"
  FullyConstrained = true
  sketch-geometry (4):
    g0: LineSegment StartX=16.8446 StartY=31.512 StartZ=0 EndX=16.3251 EndY=34.4666 EndZ=0
    g1: ArcOfCircle CenterX=19 CenterY=19.2524 CenterZ=0 NormalX=0 NormalY=0 NormalZ=1 AngleXU=0 Radius=15.4476 StartAngle=1.74483 EndAngle=2.72717
    g2: ArcOfCircle CenterX=19 CenterY=19.2524 CenterZ=0 NormalX=0 NormalY=0 NormalZ=1 AngleXU=0 Radius=12.4476 StartAngle=1.74483 EndAngle=2.73189
    g3: LineSegment StartX=4.86004 StartY=25.4725 StartZ=0 EndX=7.58253 EndY=24.2107 EndZ=0
  constraints (7):
    c: Block(g0)
    c: Coincident(g1,g0)
    c: Coincident(g2,g0)
    c: Coincident(g3,g1)
    c: Coincident(g3,g2)
    c: Block(g1)
    c: Block(g2)
FEATURE [Part::Cylinder] Cylinder022
  Angle = 360
  AttacherType = Attacher::AttachEngine3D
  Height = 10
  Placement = pos=(0,0,36.15) rot=(0,0,1;0rad)
  Radius = 4
FEATURE [Sketcher::SketchObject] Sketch011  label="topSketch005"
  FullyConstrained = true
  sketch-geometry (4):
    g0: LineSegment StartX=16.8446 StartY=31.512 StartZ=0 EndX=16.3251 EndY=34.4666 EndZ=0
    g1: ArcOfCircle CenterX=19 CenterY=19.2524 CenterZ=0 NormalX=0 NormalY=0 NormalZ=1 AngleXU=0 Radius=15.4476 StartAngle=1.74483 EndAngle=2.72717
    g2: ArcOfCircle CenterX=19 CenterY=19.2524 CenterZ=0 NormalX=0 NormalY=0 NormalZ=1 AngleXU=0 Radius=12.4476 StartAngle=1.74483 EndAngle=2.73189
    g3: LineSegment StartX=4.86004 StartY=25.4725 StartZ=0 EndX=7.58253 EndY=24.2107 EndZ=0
  constraints (7):
    c: Block(g0)
    c: Coincident(g1,g0)
    c: Coincident(g2,g0)
    c: Coincident(g3,g1)
    c: Coincident(g3,g2)
    c: Block(g1)
    c: Block(g2)
FEATURE [Part::Extrusion] Extrude010
  Base = -> Sketch011
  Dir = (0,0,1)
  DirMode = 2
  FaceMakerClass = Part::FaceMakerBullseye
  LengthFwd = 10.6
  LengthRev = 0
  Placement = pos=(0,0,31) rot=(0,0,1;0rad)
  Solid = true
  Symmetric = false
FEATURE [Part::Cylinder] Cylinder023
  Angle = 360
  AttacherType = Attacher::AttachEngine3D
  Height = 20
  Placement = pos=(0,0,36.15) rot=(0,0,1;0rad)
  Radius = 8.2
FEATURE [Part::MultiFuse] Fusion039  label="removeToCreteHoleForPlugHousing008"
  Placement = pos=(-42,19,36) rot=(0,1,0;1.5708rad)
  Shapes = -> [Cylinder023,Cylinder022]
FEATURE [Part::Cut] Cut012
  Base = -> Extrude010
  Placement = pos=(0,0,-0.3) rot=(0,0,1;0rad)
  Tool = -> Fusion039
FEATURE [Part::Cut] Cut013
  Base = -> Box010
  Tool = -> Cut012
FEATURE [Part::Fillet] Fillet014
  Base = -> Cut013
  Edges = 1 edges r=0.7: [Edge13]
FEATURE [Part::Fillet] Fillet015
  Base = -> Fillet014
  Edges = 1 edges r=0.7: [Edge13]
FEATURE [Part::Fillet] Fillet016
  Base = -> Fillet015
  Edges = 1 edges r=0.7: [Edge16]
FEATURE [Part::Fillet] Fillet017
  Base = -> Fillet016
  Edges = 1 edges r=0.7: [Edge11]
FEATURE [Part::Fillet] Fillet018
  Base = -> Fillet017
  Edges = 1 edges r=0.7: [Edge10]
FEATURE [Part::Fillet] Fillet019
  Base = -> Fillet018
  Edges = 1 edges r=1.2: [Edge5]
FEATURE [Part::Fillet] Fillet020
  Base = -> Fillet019
  Edges = 1 edges r=1.2: [Edge12]
FEATURE [Part::Fillet] Fillet021
  Base = -> Fillet020
  Edges = 1 edges r=2: [Edge1]
  Placement = pos=(0.3,0,0) rot=(0,0,1;0rad)
FEATURE [Part::MultiFuse] Fusion040  label="top005"
  Shapes = -> [Cut008,Fillet021]
FEATURE [Part::MultiFuse] Fusion041  label="wireHolder"
  Shapes = -> [Fusion033,Fillet013]
FEATURE [Part::MultiFuse] Fusion042
  Shapes = -> [Fillet007,Fusion041]
FEATURE [Part::MultiFuse] Fusion043  label="wireHolder001"
  Shapes = -> [Fusion042,Fillet010]
FEATURE [Part::MultiFuse] Fusion044  label="wireHolder002"
  Shapes = -> [Fillet006,Fusion037,Fusion043]
FEATURE [Part::Feature] Face026
  shape: bbox 11 x 6 x 2e-07 mm, 1 faces, 0 solids (baked)
FEATURE [Part::Revolution] Revolve026
  Angle = 360
  Axis = (0,1,0)
  Base = (0,0,0)
  FaceMakerClass = Part::FaceMakerBullseye
  Placement = pos=(30.3,-1,19.7) rot=(0,0,1;0rad)
  Solid = false
  Source = -> Face026
  Symmetric = false
FEATURE [Sketcher::SketchObject] Sketch013  label="topSketch006"
  FullyConstrained = true
  sketch-geometry (13):
    g0: LineSegment StartX=117 StartY=19 StartZ=0 EndX=117 EndY=38 EndZ=0
    g1: ArcOfCircle CenterX=98 CenterY=19 CenterZ=0 NormalX=0 NormalY=0 NormalZ=1 AngleXU=0 Radius=19 StartAngle=5.7297 EndAngle=6.28319
    g2: LineSegment StartX=0 StartY=3 StartZ=0 EndX=0 EndY=19 EndZ=0
    g3: LineSegment StartX=19 StartY=38 StartZ=0 EndX=117 EndY=38 EndZ=0
    g4: ArcOfCircle CenterX=19 CenterY=19 CenterZ=0 NormalX=0 NormalY=0 NormalZ=1 AngleXU=0 Radius=19 StartAngle=1.5708 EndAngle=3.14159
    g5: ArcOfCircle CenterX=19 CenterY=19 CenterZ=0 NormalX=0 NormalY=0 NormalZ=1 AngleXU=0 Radius=16 StartAngle=1.5708 EndAngle=3.14159
    g6: ArcOfCircle CenterX=98 CenterY=19 CenterZ=0 NormalX=0 NormalY=0 NormalZ=1 AngleXU=0 Radius=16 StartAngle=5.60905 EndAngle=6.28319
    g7: LineSegment StartX=114 StartY=19 StartZ=0 EndX=114 EndY=35 EndZ=0
    g8: LineSegment StartX=110.5 StartY=9.01251 StartZ=0 EndX=114.163 EndY=9.01251 EndZ=0
    g9: LineSegment StartX=114 StartY=35 StartZ=0 EndX=19 EndY=35 EndZ=0
    g10: LineSegment StartX=0 StartY=3 StartZ=0 EndX=0 EndY=0 EndZ=0
    g11: LineSegment StartX=3 StartY=0 StartZ=0 EndX=0 EndY=0 EndZ=0
    g12: LineSegment StartX=3 StartY=19 StartZ=0 EndX=3 EndY=0 EndZ=0
  constraints (33):
    c: Vertical(g0)
    c: Distance(g0) = 19
    c: Block(g0)
    c: Coincident(g1,g0)
    c: Block(g1)
    c: Vertical(g2)
    c: Block(g2)
    c: Coincident(g3,g0)
    c: Horizontal(g3)
    c: Distance(g3) = 98
    c: Coincident(g4,g3)
    c: Coincident(g4,g2)
    c: Block(g4)
    c: Coincident(g5,g4)
    c: Coincident(g6,g1)
    c: Block(g6)
    c: Block(g5)
    c: Coincident(g7,g6)
    c: Vertical(g7)
    c: Coincident(g8,g6)
    c: Coincident(g8,g1)
    c: Coincident(g9,g7)
    c: Coincident(g9,g5)
    c: Horizontal(g9)
    c: Tangent(g9,g5)
    c: Coincident(g10,g2)
    c: Distance(g10) = 3
    c: Vertical(g10)
    c: Coincident(g11,g10)
    c: Horizontal(g11)
    c: Coincident(g12,g5)
    c: Coincident(g12,g11)
    c: Vertical(g12)
FEATURE [Part::Extrusion] Extrude011  label="top006"
  Base = -> Sketch013
  Dir = (0,0,1)
  DirMode = 2
  FaceMakerClass = Part::FaceMakerBullseye
  LengthFwd = 72
  LengthRev = 0
  Solid = true
  Symmetric = false
FEATURE [Sketcher::SketchObject] Sketch014
  FullyConstrained = true
  MapMode = 3
  Placement = pos=(0,0,0) rot=(1,0,0;1.5708rad)
  Support = -> [Extrude011]
  sketch-geometry (8):
    g0: Circle CenterX=80.351 CenterY=-67.6202 CenterZ=0 NormalX=0 NormalY=0 NormalZ=1 AngleXU=0 Radius=2
    g1: Circle CenterX=80.351 CenterY=-67.6202 CenterZ=0 NormalX=0 NormalY=0 NormalZ=1 AngleXU=0 Radius=3
    g2: Circle CenterX=80.351 CenterY=-4.92017 CenterZ=0 NormalX=0 NormalY=0 NormalZ=1 AngleXU=0 Radius=2
    g3: Circle CenterX=80.351 CenterY=-4.92017 CenterZ=0 NormalX=0 NormalY=0 NormalZ=1 AngleXU=0 Radius=3
    g4: Circle CenterX=23.851 CenterY=-4.92017 CenterZ=0 NormalX=0 NormalY=0 NormalZ=1 AngleXU=0 Radius=2
    g5: Circle CenterX=23.851 CenterY=-4.92017 CenterZ=0 NormalX=0 NormalY=0 NormalZ=1 AngleXU=0 Radius=3
    g6: Circle CenterX=23.851 CenterY=-67.6202 CenterZ=0 NormalX=0 NormalY=0 NormalZ=1 AngleXU=0 Radius=2
    g7: Circle CenterX=23.851 CenterY=-67.6202 CenterZ=0 NormalX=0 NormalY=0 NormalZ=1 AngleXU=0 Radius=3
  constraints (8):
    c: Block(g3)
    c: Block(g2)
    c: Block(g1)
    c: Block(g0)
    c: Block(g6)
    c: Block(g7)
    c: Block(g4)
    c: Block(g5)
FEATURE [Part::Feature] Face027
  shape: bbox 11 x 6 x 2e-07 mm, 1 faces, 0 solids (baked)
FEATURE [Part::Revolution] Revolve027
  Angle = 360
  Axis = (0,1,0)
  Base = (0,0,0)
  FaceMakerClass = Part::FaceMakerBullseye
  Placement = pos=(30.3,-1,51.7) rot=(0,0,1;0rad)
  Solid = false
  Source = -> Face027
  Symmetric = false
FEATURE [Part::Feature] Face028
  shape: bbox 11 x 6 x 2e-07 mm, 1 faces, 0 solids (baked)
FEATURE [Part::Revolution] Revolve028
  Angle = 360
  Axis = (0,1,0)
  Base = (0,0,0)
  FaceMakerClass = Part::FaceMakerBullseye
  Placement = pos=(62.3,-1,19.7) rot=(0,0,1;0rad)
  Solid = false
  Source = -> Face028
  Symmetric = false
FEATURE [Part::Feature] Face029
  shape: bbox 11 x 6 x 2e-07 mm, 1 faces, 0 solids (baked)
FEATURE [Part::Revolution] Revolve029
  Angle = 360
  Axis = (0,1,0)
  Base = (0,0,0)
  FaceMakerClass = Part::FaceMakerBullseye
  Placement = pos=(62.3,-1,51.7) rot=(0,0,1;0rad)
  Solid = false
  Source = -> Face029
  Symmetric = false
FEATURE [Part::Feature] Wire
  shape: bbox 11 x 5.2 x 2e-07 mm, 0 faces, 0 solids (baked)
FEATURE [Part::Revolution] Revolve030
  Angle = 360
  Axis = (0,1,0)
  Base = (0,0,0)
  FaceMakerClass = Part::FaceMakerBullseye
  Placement = pos=(30.3,38,19.7) rot=(0,0,1;0rad)
  Solid = true
  Source = -> Wire
  Symmetric = false
FEATURE [Part::Feature] Wire001
  shape: bbox 11 x 5.2 x 2e-07 mm, 0 faces, 0 solids (baked)
FEATURE [Part::Revolution] Revolve031
  Angle = 360
  Axis = (0,1,0)
  Base = (0,0,0)
  FaceMakerClass = Part::FaceMakerBullseye
  Placement = pos=(30.3,38,51.7) rot=(0,0,1;0rad)
  Solid = true
  Source = -> Wire001
  Symmetric = false
FEATURE [Part::Feature] Wire002
  shape: bbox 11 x 5.2 x 2e-07 mm, 0 faces, 0 solids (baked)
FEATURE [Part::Revolution] Revolve032
  Angle = 360
  Axis = (0,1,0)
  Base = (0,0,0)
  FaceMakerClass = Part::FaceMakerBullseye
  Placement = pos=(62.3,38,51.7) rot=(0,0,1;0rad)
  Solid = true
  Source = -> Wire002
  Symmetric = false
FEATURE [Part::Feature] Wire003
  shape: bbox 11 x 5.2 x 2e-07 mm, 0 faces, 0 solids (baked)
FEATURE [Part::Revolution] Revolve033
  Angle = 360
  Axis = (0,1,0)
  Base = (0,0,0)
  FaceMakerClass = Part::FaceMakerBullseye
  Placement = pos=(62.3,38,19.7) rot=(0,0,1;0rad)
  Solid = true
  Source = -> Wire003
  Symmetric = false
FEATURE [Part::MultiFuse] Fusion045  label="altRandScrewHousing"
  Shapes = -> [Revolve029,Revolve027,Revolve028,Revolve026]
FEATURE [Part::MultiFuse] Fusion046  label="fanScrewHousing"
  Shapes = -> [Revolve033,Revolve032,Revolve031,Revolve030]
FEATURE [Sketcher::SketchObject] Sketch015
  FullyConstrained = true
  sketch-geometry (17):
    g0: Circle CenterX=-3.5 CenterY=23.5 CenterZ=0 NormalX=0 NormalY=0 NormalZ=1 AngleXU=0 Radius=1
    g1: Circle CenterX=-1 CenterY=15.25 CenterZ=0 NormalX=0 NormalY=0 NormalZ=1 AngleXU=0 Radius=1
    g2: Circle CenterX=-3.5 CenterY=7 CenterZ=0 NormalX=0 NormalY=0 NormalZ=1 AngleXU=0 Radius=1
    g3: BSplineCurve PolesCount=3 KnotsCount=2 Degree=2 IsPeriodic=0
    g4: GeomPoint X=-3.5 Y=23.5 Z=0
    g5: GeomPoint X=-3.5 Y=7 Z=0
    g6: Circle CenterX=-4.8 CenterY=30.5 CenterZ=0 NormalX=0 NormalY=0 NormalZ=1 AngleXU=0 Radius=1
    g7: Circle CenterX=-3.5 CenterY=30.5 CenterZ=0 NormalX=0 NormalY=0 NormalZ=1 AngleXU=0 Radius=1
    g8: Circle CenterX=-3.5 CenterY=29.2 CenterZ=0 NormalX=0 NormalY=0 NormalZ=1 AngleXU=0 Radius=1
    g9: BSplineCurve PolesCount=3 KnotsCount=2 Degree=2 IsPeriodic=0
    g10: GeomPoint X=-4.8 Y=30.5 Z=0
    g11: GeomPoint X=-3.5 Y=29.2 Z=0
    g12: LineSegment StartX=-3.5 StartY=29.2 StartZ=0 EndX=-3.5 EndY=23.5 EndZ=0
    g13: LineSegment StartX=-4.8 StartY=30.5 StartZ=0 EndX=0 EndY=30.5 EndZ=0
    g14: LineSegment StartX=-3.5 StartY=0.3 StartZ=0 EndX=0 EndY=0.3 EndZ=0
    g15: LineSegment StartX=-3.5 StartY=0.3 StartZ=0 EndX=-3.5 EndY=7 EndZ=0
    g16: LineSegment StartX=0 StartY=0.3 StartZ=0 EndX=0 EndY=30.5 EndZ=0
  constraints (33):
    c: Weight(g0) = 1
    c: Equal(g0,g1)
    c: Equal(g0,g2)
    c: InternalAlignment(g0,g3)
    c: InternalAlignment(g1,g3)
    c: InternalAlignment(g2,g3)
    c: InternalAlignment(g4,g3)
    c: InternalAlignment(g5,g3)
    c: Block(g3)
    c: Weight(g6) = 1
    c: Equal(g6,g7)
    c: Equal(g6,g8)
    c: InternalAlignment(g6,g9)
    c: InternalAlignment(g7,g9)
    c: InternalAlignment(g8,g9)
    c: InternalAlignment(g10,g9)
    c: InternalAlignment(g11,g9)
    c: Block(g9)
    c: Coincident(g12,g9)
    c: Coincident(g12,g3)
    c: Vertical(g12)
    c: Coincident(g13,g9)
    c: Horizontal(g13)
    c: Distance(g13) = 4.8
    c: Horizontal(g14)
    c: Block(g14)
    c: Coincident(g15,g14)
    c: Coincident(g15,g3)
    c: Vertical(g15)
    c: Coincident(g16,g14)
    c: Coincident(g16,g13)
    c: Vertical(g16)
    c: Tangent(g16,g1)
FEATURE [Sketcher::SketchObject] Sketch016
  FullyConstrained = true
  sketch-geometry (16):
    g0: Circle CenterX=-3.5 CenterY=23.5 CenterZ=0 NormalX=0 NormalY=0 NormalZ=1 AngleXU=0 Radius=1
    g1: Circle CenterX=-1 CenterY=15.25 CenterZ=0 NormalX=0 NormalY=0 NormalZ=1 AngleXU=0 Radius=1
    g2: Circle CenterX=-3.5 CenterY=7 CenterZ=0 NormalX=0 NormalY=0 NormalZ=1 AngleXU=0 Radius=1
    g3: BSplineCurve PolesCount=3 KnotsCount=2 Degree=2 IsPeriodic=0
    g4: GeomPoint X=-3.5 Y=23.5 Z=0
    g5: GeomPoint X=-3.5 Y=7 Z=0
    g6: LineSegment StartX=-3.5 StartY=28.2 StartZ=0 EndX=-3.5 EndY=23.5 EndZ=0
    g7: LineSegment StartX=0 StartY=29.5 StartZ=0 EndX=0 EndY=30 EndZ=0
    g8: LineSegment StartX=-3.5 StartY=28.2 StartZ=0 EndX=-3.5 EndY=30 EndZ=0
    g9: LineSegment StartX=0 StartY=30 StartZ=0 EndX=0 EndY=30.5 EndZ=0
    g10: LineSegment StartX=0 StartY=30.5 StartZ=0 EndX=-3.5 EndY=30.5 EndZ=0
    g11: LineSegment StartX=-3.5 StartY=30.5 StartZ=0 EndX=-3.5 EndY=30 EndZ=0
    g12: LineSegment StartX=0 StartY=29.5 StartZ=0 EndX=0 EndY=5 EndZ=0
    g13: LineSegment StartX=-3.5 StartY=0.3 StartZ=0 EndX=-3.5 EndY=7 EndZ=0
    g14: LineSegment StartX=-3.5 StartY=0.3 StartZ=0 EndX=0 EndY=0.3 EndZ=0
    g15: LineSegment StartX=0 StartY=5 StartZ=0 EndX=0 EndY=0.3 EndZ=0
  constraints (39):
    c: Weight(g0) = 1
    c: Equal(g0,g1)
    c: Equal(g0,g2)
    c: InternalAlignment(g0,g3)
    c: InternalAlignment(g1,g3)
    c: InternalAlignment(g2,g3)
    c: InternalAlignment(g4,g3)
    c: InternalAlignment(g5,g3)
    c: Block(g3)
    c: Coincident(g6,g3)
    c: Vertical(g6)
    c: Vertical(g7)
    c: Distance(g7) = 0.5
    c: Coincident(g8,g6)
    c: Vertical(g8)
    c: Block(g6)
    c: Block(g7)
    c: Vertical(g9)
    c: Equal(g7,g9) = 0.5
    c: Block(g9)
    c: Coincident(g9,g7)
    c: Horizontal(g10)
    c: Coincident(g10,g9)
    c: Coincident(g11,g10)
    c: Coincident(g11,g8)
    c: Vertical(g11)
    c: Block(g11)
    c: Coincident(g12,g7)
    c: Vertical(g12)
    c: Coincident(g13,g3)
    c: Vertical(g13)
    c: Distance(g13) = 6.7
    c: Coincident(g14,g13)
    c: Horizontal(g14)
    c: Block(g14)
    c: Coincident(g15,g12)
    c: Coincident(g15,g14)
    c: Vertical(g15)
    c: Block(g15)
FEATURE [Sketcher::SketchObject] Sketch017
  FullyConstrained = true
  sketch-geometry (11):
    g0: LineSegment StartX=-3.5 StartY=1e-16 StartZ=0 EndX=-1.6 EndY=1e-16 EndZ=0
    g1: LineSegment StartX=-1.6 StartY=1e-16 StartZ=0 EndX=-1.6 EndY=1.5 EndZ=0
    g2: LineSegment StartX=-3.5 StartY=1.5 StartZ=0 EndX=-1.6 EndY=1.5 EndZ=0
    g3: LineSegment StartX=-3.5 StartY=1e-16 StartZ=0 EndX=-4.8 EndY=1e-16 EndZ=0
    g4: Circle CenterX=-3.5 CenterY=1.3 CenterZ=0 NormalX=0 NormalY=0 NormalZ=1 AngleXU=0 Radius=1
    g5: Circle CenterX=-3.5 CenterY=1e-16 CenterZ=0 NormalX=0 NormalY=0 NormalZ=1 AngleXU=0 Radius=1
    g6: Circle CenterX=-4.8 CenterY=1e-16 CenterZ=0 NormalX=0 NormalY=0 NormalZ=1 AngleXU=0 Radius=1
    g7: BSplineCurve PolesCount=3 KnotsCount=2 Degree=2 IsPeriodic=0
    g8: GeomPoint X=-3.5 Y=1.3 Z=0
    g9: GeomPoint X=-4.8 Y=1e-16 Z=0
    g10: LineSegment StartX=-3.5 StartY=1.3 StartZ=0 EndX=-3.5 EndY=1.5 EndZ=0
  constraints (24):
    c: Horizontal(g0)
    c: Distance(g0) = 1.9
    c: Block(g0)
    c: Coincident(g1,g0)
    c: Vertical(g1)
    c: Coincident(g2,g1)
    c: Horizontal(g2)
    c: Coincident(g3,g0)
    c: Horizontal(g3)
    c: Distance(g3) = 1.3
    c: Weight(g4) = 1
    c: Equal(g4,g5)
    c: Coincident(g5,g0)
    c: Equal(g4,g6)
    c: Coincident(g7,g3)
    c: InternalAlignment(g4,g7)
    c: InternalAlignment(g5,g7)
    c: InternalAlignment(g6,g7)
    c: InternalAlignment(g8,g7)
    c: InternalAlignment(g9,g7)
    c: Coincident(g10,g7)
    c: Coincident(g10,g2)
    c: Vertical(g10)
    c: Block(g10)
FEATURE [Part::Feature] Face035
  shape: bbox 3.2 x 1.5 x 2e-07 mm, 1 faces, 0 solids (baked)
FEATURE [Part::Revolution] Revolve039  label="backCaseScrewRetainer"
  Angle = 360
  Axis = (0,1,0)
  Base = (0,0,0)
  FaceMakerClass = Part::FaceMakerBullseye
  Placement = pos=(12.5,3,62) rot=(0,0,1;0rad)
  Solid = false
  Source = -> Face035
  Symmetric = false
FEATURE [Part::Feature] Face036
  shape: bbox 3.2 x 1.5 x 2e-07 mm, 1 faces, 0 solids (baked)
FEATURE [Part::Feature] Face039
  shape: bbox 4.8 x 30.2 x 2e-07 mm, 1 faces, 0 solids (baked)
FEATURE [Part::Revolution] Revolve043  label="frontCaseScrewPost002"
  Angle = 360
  Axis = (0,1,0)
  Base = (0,0,0)
  FaceMakerClass = Part::FaceMakerBullseye
  Placement = pos=(89.5,4.5,3.5) rot=(0,0,1;0rad)
  Solid = false
  Source = -> Face039
  Symmetric = false
FEATURE [Part::Feature] Face042
  shape: bbox 4.8 x 30.2 x 2e-07 mm, 1 faces, 0 solids (baked)
FEATURE [Part::Revolution] Revolve046  label="frontCaseScrewPost003"
  Angle = 360
  Axis = (0,1,0)
  Base = (0,0,0)
  FaceMakerClass = Part::FaceMakerBullseye
  Placement = pos=(89.5,4.5,68.5) rot=(0,0,1;0rad)
  Solid = false
  Source = -> Face042
  Symmetric = false
FEATURE [Part::Feature] Face043
  shape: bbox 3.2 x 1.5 x 2e-07 mm, 1 faces, 0 solids (baked)
FEATURE [Part::Revolution] Revolve047  label="frontCaseScrewRetainer002"
  Angle = 360
  Axis = (0,1,0)
  Base = (0,0,0)
  FaceMakerClass = Part::FaceMakerBullseye
  Placement = pos=(89.5,3,68.5) rot=(0,0,1;0rad)
  Solid = false
  Source = -> Face043
  Symmetric = false
FEATURE [Part::Feature] Face044
  shape: bbox 3.2 x 1.5 x 2e-07 mm, 1 faces, 0 solids (baked)
FEATURE [Part::Revolution] Revolve048  label="frontCaseScrewRetainer003"
  Angle = 360
  Axis = (0,1,0)
  Base = (0,0,0)
  FaceMakerClass = Part::FaceMakerBullseye
  Placement = pos=(89.5,3,3.5) rot=(0,0,1;0rad)
  Solid = false
  Source = -> Face044
  Symmetric = false
FEATURE [App::MeasureDistance] Distance002  label="Distance: 1.67 mm"
  Distance = 1.66921
  P1 = (99.2361,4.7524,71.7)
  P2 = (99.2347,6.42161,71.7)
FEATURE [Sketcher::SketchObject] Sketch018
  FullyConstrained = true
  sketch-geometry (7):
    g0: LineSegment StartX=0 StartY=0 StartZ=0 EndX=0 EndY=6 EndZ=0
    g1: Circle CenterX=0 CenterY=0 CenterZ=0 NormalX=0 NormalY=0 NormalZ=1 AngleXU=0 Radius=1
    g2: Circle CenterX=8 CenterY=6 CenterZ=0 NormalX=0 NormalY=0 NormalZ=1 AngleXU=0 Radius=1
    g3: BSplineCurve PolesCount=3 KnotsCount=2 Degree=2 IsPeriodic=0
    g4: GeomPoint X=0 Y=0 Z=0
    g5: GeomPoint X=8 Y=6 Z=0
    g6: LineSegment StartX=0 StartY=6 StartZ=0 EndX=8 EndY=6 EndZ=0
  constraints (14):
    c: Coincident(g0,g-1)
    c: Distance(g0) = 6
    c: Vertical(g0)
    c: Coincident(g3,g0)
    c: Weight(g1) = 1
    c: Equal(g1,g2)
    c: InternalAlignment(g1,g3)
    c: InternalAlignment(g2,g3)
    c: InternalAlignment(g4,g3)
    c: InternalAlignment(g5,g3)
    c: Block(g3)
    c: Coincident(g6,g0)
    c: Coincident(g6,g3)
    c: Horizontal(g6)
FEATURE [Part::Extrusion] Extrude012  label="caseScrewPillarBracket"
  Base = -> Sketch018
  Dir = (0,0,1)
  DirMode = 2
  FaceMakerClass = Part::FaceMakerBullseye
  LengthFwd = 2.4
  LengthRev = 0
  Placement = pos=(15.76,29,8.8) rot=(0,1,0;0rad)
  Solid = true
  Symmetric = false
FEATURE [Sketcher::SketchObject] Sketch019
  FullyConstrained = true
  sketch-geometry (7):
    g0: LineSegment StartX=0 StartY=0 StartZ=0 EndX=0 EndY=6 EndZ=0
    g1: Circle CenterX=0 CenterY=0 CenterZ=0 NormalX=0 NormalY=0 NormalZ=1 AngleXU=0 Radius=1
    g2: Circle CenterX=8 CenterY=6 CenterZ=0 NormalX=0 NormalY=0 NormalZ=1 AngleXU=0 Radius=1
    g3: BSplineCurve PolesCount=3 KnotsCount=2 Degree=2 IsPeriodic=0
    g4: GeomPoint X=0 Y=0 Z=0
    g5: GeomPoint X=8 Y=6 Z=0
    g6: LineSegment StartX=0 StartY=6 StartZ=0 EndX=8 EndY=6 EndZ=0
  constraints (14):
    c: Coincident(g0,g-1)
    c: Distance(g0) = 6
    c: Vertical(g0)
    c: Coincident(g3,g0)
    c: Weight(g1) = 1
    c: Equal(g1,g2)
    c: InternalAlignment(g1,g3)
    c: InternalAlignment(g2,g3)
    c: InternalAlignment(g4,g3)
    c: InternalAlignment(g5,g3)
    c: Block(g3)
    c: Coincident(g6,g0)
    c: Coincident(g6,g3)
    c: Horizontal(g6)
FEATURE [Part::Extrusion] Extrude013  label="caseScrewPillarBracket001"
  Base = -> Sketch019
  Dir = (0,0,1)
  DirMode = 2
  FaceMakerClass = Part::FaceMakerBullseye
  LengthFwd = 2.4
  LengthRev = 0
  Placement = pos=(15.76,29,60.8) rot=(0,0,1;0rad)
  Solid = true
  Symmetric = false
FEATURE [Sketcher::SketchObject] Sketch020
  FullyConstrained = true
  sketch-geometry (7):
    g0: LineSegment StartX=0 StartY=0 StartZ=0 EndX=0 EndY=6 EndZ=0
    g1: Circle CenterX=0 CenterY=0 CenterZ=0 NormalX=0 NormalY=0 NormalZ=1 AngleXU=0 Radius=1
    g2: Circle CenterX=8 CenterY=6 CenterZ=0 NormalX=0 NormalY=0 NormalZ=1 AngleXU=0 Radius=1
    g3: BSplineCurve PolesCount=3 KnotsCount=2 Degree=2 IsPeriodic=0
    g4: GeomPoint X=0 Y=0 Z=0
    g5: GeomPoint X=8 Y=6 Z=0
    g6: LineSegment StartX=0 StartY=6 StartZ=0 EndX=8 EndY=6 EndZ=0
  constraints (14):
    c: Coincident(g0,g-1)
    c: Distance(g0) = 6
    c: Vertical(g0)
    c: Coincident(g3,g0)
    c: Weight(g1) = 1
    c: Equal(g1,g2)
    c: InternalAlignment(g1,g3)
    c: InternalAlignment(g2,g3)
    c: InternalAlignment(g4,g3)
    c: InternalAlignment(g5,g3)
    c: Block(g3)
    c: Coincident(g6,g0)
    c: Coincident(g6,g3)
    c: Horizontal(g6)
FEATURE [Part::Extrusion] Extrude014  label="caseScrewPillarBracket002"
  Base = -> Sketch020
  Dir = (0,0,1)
  DirMode = 2
  FaceMakerClass = Part::FaceMakerBullseye
  LengthFwd = 2.4
  LengthRev = 0
  Placement = pos=(13.7,29,13.26) rot=(0,-1,0;1.5708rad)
  Solid = true
  Symmetric = false
FEATURE [Sketcher::SketchObject] Sketch021
  FullyConstrained = true
  sketch-geometry (7):
    g0: LineSegment StartX=0 StartY=0 StartZ=0 EndX=0 EndY=6 EndZ=0
    g1: Circle CenterX=0 CenterY=0 CenterZ=0 NormalX=0 NormalY=0 NormalZ=1 AngleXU=0 Radius=1
    g2: Circle CenterX=8 CenterY=6 CenterZ=0 NormalX=0 NormalY=0 NormalZ=1 AngleXU=0 Radius=1
    g3: BSplineCurve PolesCount=3 KnotsCount=2 Degree=2 IsPeriodic=0
    g4: GeomPoint X=0 Y=0 Z=0
    g5: GeomPoint X=8 Y=6 Z=0
    g6: LineSegment StartX=0 StartY=6 StartZ=0 EndX=8 EndY=6 EndZ=0
  constraints (14):
    c: Coincident(g0,g-1)
    c: Distance(g0) = 6
    c: Vertical(g0)
    c: Coincident(g3,g0)
    c: Weight(g1) = 1
    c: Equal(g1,g2)
    c: InternalAlignment(g1,g3)
    c: InternalAlignment(g2,g3)
    c: InternalAlignment(g4,g3)
    c: InternalAlignment(g5,g3)
    c: Block(g3)
    c: Coincident(g6,g0)
    c: Coincident(g6,g3)
    c: Horizontal(g6)
FEATURE [Part::Extrusion] Extrude015  label="caseScrewPillarBracket003"
  Base = -> Sketch021
  Dir = (0,0,1)
  DirMode = 2
  FaceMakerClass = Part::FaceMakerBullseye
  LengthFwd = 2.4
  LengthRev = 0
  Placement = pos=(11.3,29,58.74) rot=(0,1,0;1.5708rad)
  Solid = true
  Symmetric = false
FEATURE [Sketcher::SketchObject] Sketch022
  FullyConstrained = true
  sketch-geometry (7):
    g0: LineSegment StartX=0 StartY=0 StartZ=0 EndX=0 EndY=6 EndZ=0
    g1: Circle CenterX=0 CenterY=0 CenterZ=0 NormalX=0 NormalY=0 NormalZ=1 AngleXU=0 Radius=1
    g2: Circle CenterX=8 CenterY=6 CenterZ=0 NormalX=0 NormalY=0 NormalZ=1 AngleXU=0 Radius=1
    g3: BSplineCurve PolesCount=3 KnotsCount=2 Degree=2 IsPeriodic=0
    g4: GeomPoint X=0 Y=0 Z=0
    g5: GeomPoint X=8 Y=6 Z=0
    g6: LineSegment StartX=0 StartY=6 StartZ=0 EndX=8 EndY=6 EndZ=0
  constraints (14):
    c: Coincident(g0,g-1)
    c: Distance(g0) = 6
    c: Vertical(g0)
    c: Coincident(g3,g0)
    c: Weight(g1) = 1
    c: Equal(g1,g2)
    c: InternalAlignment(g1,g3)
    c: InternalAlignment(g2,g3)
    c: InternalAlignment(g4,g3)
    c: InternalAlignment(g5,g3)
    c: Block(g3)
    c: Coincident(g6,g0)
    c: Coincident(g6,g3)
    c: Horizontal(g6)
FEATURE [Part::Extrusion] Extrude016  label="caseScrewPillarBracket004"
  Base = -> Sketch022
  Dir = (0,0,1)
  DirMode = 2
  FaceMakerClass = Part::FaceMakerBullseye
  LengthFwd = 2.4
  LengthRev = 0
  Placement = pos=(88.3,29,65.23) rot=(0,1,0;1.5708rad)
  Solid = true
  Symmetric = false
FEATURE [Sketcher::SketchObject] Sketch023
  FullyConstrained = true
  sketch-geometry (7):
    g0: LineSegment StartX=0 StartY=0 StartZ=0 EndX=0 EndY=6 EndZ=0
    g1: Circle CenterX=0 CenterY=0 CenterZ=0 NormalX=0 NormalY=0 NormalZ=1 AngleXU=0 Radius=1
    g2: Circle CenterX=8 CenterY=6 CenterZ=0 NormalX=0 NormalY=0 NormalZ=1 AngleXU=0 Radius=1
    g3: BSplineCurve PolesCount=3 KnotsCount=2 Degree=2 IsPeriodic=0
    g4: GeomPoint X=0 Y=0 Z=0
    g5: GeomPoint X=8 Y=6 Z=0
    g6: LineSegment StartX=0 StartY=6 StartZ=0 EndX=8 EndY=6 EndZ=0
  constraints (14):
    c: Coincident(g0,g-1)
    c: Distance(g0) = 6
    c: Vertical(g0)
    c: Coincident(g3,g0)
    c: Weight(g1) = 1
    c: Equal(g1,g2)
    c: InternalAlignment(g1,g3)
    c: InternalAlignment(g2,g3)
    c: InternalAlignment(g4,g3)
    c: InternalAlignment(g5,g3)
    c: Block(g3)
    c: Coincident(g6,g0)
    c: Coincident(g6,g3)
    c: Horizontal(g6)
FEATURE [Part::Extrusion] Extrude017  label="caseScrewPillarBracket005"
  Base = -> Sketch023
  Dir = (0,0,1)
  DirMode = 2
  FaceMakerClass = Part::FaceMakerBullseye
  LengthFwd = 2.4
  LengthRev = 0
  Placement = pos=(90.7,29,6.77) rot=(0,-1,0;1.5708rad)
  Solid = true
  Symmetric = false
FEATURE [Sketcher::SketchObject] Sketch024
  FullyConstrained = true
  sketch-geometry (7):
    g0: LineSegment StartX=0 StartY=0 StartZ=0 EndX=0 EndY=6 EndZ=0
    g1: Circle CenterX=0 CenterY=0 CenterZ=0 NormalX=0 NormalY=0 NormalZ=1 AngleXU=0 Radius=1
    g2: Circle CenterX=8 CenterY=6 CenterZ=0 NormalX=0 NormalY=0 NormalZ=1 AngleXU=0 Radius=1
    g3: BSplineCurve PolesCount=3 KnotsCount=2 Degree=2 IsPeriodic=0
    g4: GeomPoint X=0 Y=0 Z=0
    g5: GeomPoint X=8 Y=6 Z=0
    g6: LineSegment StartX=0 StartY=6 StartZ=0 EndX=8 EndY=6 EndZ=0
  constraints (14):
    c: Coincident(g0,g-1)
    c: Distance(g0) = 6
    c: Vertical(g0)
    c: Coincident(g3,g0)
    c: Weight(g1) = 1
    c: Equal(g1,g2)
    c: InternalAlignment(g1,g3)
    c: InternalAlignment(g2,g3)
    c: InternalAlignment(g4,g3)
    c: InternalAlignment(g5,g3)
    c: Block(g3)
    c: Coincident(g6,g0)
    c: Coincident(g6,g3)
    c: Horizontal(g6)
FEATURE [Part::Extrusion] Extrude018  label="caseScrewPillarBracket006"
  Base = -> Sketch024
  Dir = (0,0,1)
  DirMode = 2
  FaceMakerClass = Part::FaceMakerBullseye
  LengthFwd = 2.4
  LengthRev = 0
  Placement = pos=(103.7,29,6.77) rot=(0,-1,0;1.5708rad)
  Solid = true
  Symmetric = false
FEATURE [Sketcher::SketchObject] Sketch025
  FullyConstrained = true
  sketch-geometry (7):
    g0: LineSegment StartX=0 StartY=0 StartZ=0 EndX=0 EndY=6 EndZ=0
    g1: Circle CenterX=0 CenterY=0 CenterZ=0 NormalX=0 NormalY=0 NormalZ=1 AngleXU=0 Radius=1
    g2: Circle CenterX=8 CenterY=6 CenterZ=0 NormalX=0 NormalY=0 NormalZ=1 AngleXU=0 Radius=1
    g3: BSplineCurve PolesCount=3 KnotsCount=2 Degree=2 IsPeriodic=0
    g4: GeomPoint X=0 Y=0 Z=0
    g5: GeomPoint X=8 Y=6 Z=0
    g6: LineSegment StartX=0 StartY=6 StartZ=0 EndX=8 EndY=6 EndZ=0
  constraints (14):
    c: Coincident(g0,g-1)
    c: Distance(g0) = 6
    c: Vertical(g0)
    c: Coincident(g3,g0)
    c: Weight(g1) = 1
    c: Equal(g1,g2)
    c: InternalAlignment(g1,g3)
    c: InternalAlignment(g2,g3)
    c: InternalAlignment(g4,g3)
    c: InternalAlignment(g5,g3)
    c: Block(g3)
    c: Coincident(g6,g0)
    c: Coincident(g6,g3)
    c: Horizontal(g6)
FEATURE [Part::Extrusion] Extrude019  label="caseScrewPillarBracket007"
  Base = -> Sketch025
  Dir = (0,0,1)
  DirMode = 2
  FaceMakerClass = Part::FaceMakerBullseye
  LengthFwd = 2.4
  LengthRev = 0
  Placement = pos=(101.3,29,65.23) rot=(0,1,0;1.5708rad)
  Solid = true
  Symmetric = false
FEATURE [Part::Box] Box011  label="frontCaseScrewPillarBracket"
  AttacherType = Attacher::AttachEngine3D
  Height = 2.4
  Length = 16
  Placement = pos=(87,28,2.3) rot=(0,0,1;0rad)
  Width = 7
FEATURE [Part::Box] Box012  label="frontCaseScrewPillarBracket001"
  AttacherType = Attacher::AttachEngine3D
  Height = 2.4
  Length = 16
  Placement = pos=(87,28,67.3) rot=(0,0,1;0rad)
  Width = 7
FEATURE [Sketcher::SketchObject] Sketch026
  FullyConstrained = true
  sketch-geometry (17):
    g0: Circle CenterX=-3.5 CenterY=23.5 CenterZ=0 NormalX=0 NormalY=0 NormalZ=1 AngleXU=0 Radius=1
    g1: Circle CenterX=-1 CenterY=15.25 CenterZ=0 NormalX=0 NormalY=0 NormalZ=1 AngleXU=0 Radius=1
    g2: Circle CenterX=-3.5 CenterY=7 CenterZ=0 NormalX=0 NormalY=0 NormalZ=1 AngleXU=0 Radius=1
    g3: BSplineCurve PolesCount=3 KnotsCount=2 Degree=2 IsPeriodic=0
    g4: GeomPoint X=-3.5 Y=23.5 Z=0
    g5: GeomPoint X=-3.5 Y=7 Z=0
    g6: Circle CenterX=-4.8 CenterY=30.5 CenterZ=0 NormalX=0 NormalY=0 NormalZ=1 AngleXU=0 Radius=1
    g7: Circle CenterX=-3.5 CenterY=30.5 CenterZ=0 NormalX=0 NormalY=0 NormalZ=1 AngleXU=0 Radius=1
    g8: Circle CenterX=-3.5 CenterY=29.2 CenterZ=0 NormalX=0 NormalY=0 NormalZ=1 AngleXU=0 Radius=1
    g9: BSplineCurve PolesCount=3 KnotsCount=2 Degree=2 IsPeriodic=0
    g10: GeomPoint X=-4.8 Y=30.5 Z=0
    g11: GeomPoint X=-3.5 Y=29.2 Z=0
    g12: LineSegment StartX=-3.5 StartY=29.2 StartZ=0 EndX=-3.5 EndY=23.5 EndZ=0
    g13: LineSegment StartX=-4.8 StartY=30.5 StartZ=0 EndX=0 EndY=30.5 EndZ=0
    g14: LineSegment StartX=-3.5 StartY=5 StartZ=0 EndX=-3.5 EndY=7 EndZ=0
    g15: LineSegment StartX=0 StartY=5 StartZ=0 EndX=0 EndY=30.5 EndZ=0
    g16: LineSegment StartX=-3.5 StartY=5 StartZ=0 EndX=0 EndY=5 EndZ=0
  constraints (33):
    c: Weight(g0) = 1
    c: Equal(g0,g1)
    c: Equal(g0,g2)
    c: InternalAlignment(g0,g3)
    c: InternalAlignment(g1,g3)
    c: InternalAlignment(g2,g3)
    c: InternalAlignment(g4,g3)
    c: InternalAlignment(g5,g3)
    c: Block(g3)
    c: Weight(g6) = 1
    c: Equal(g6,g7)
    c: Equal(g6,g8)
    c: InternalAlignment(g6,g9)
    c: InternalAlignment(g7,g9)
    c: InternalAlignment(g8,g9)
    c: InternalAlignment(g10,g9)
    c: InternalAlignment(g11,g9)
    c: Block(g9)
    c: Coincident(g12,g9)
    c: Coincident(g12,g3)
    c: Vertical(g12)
    c: Coincident(g13,g9)
    c: Horizontal(g13)
    c: Distance(g13) = 4.8
    c: Coincident(g14,g3)
    c: Vertical(g14)
    c: Coincident(g15,g13)
    c: Vertical(g15)
    c: Tangent(g15,g1)
    c: Distance(g14) = 2
    c: Coincident(g16,g14)
    c: Horizontal(g16)
    c: Coincident(g15,g16)
FEATURE [Part::Feature] Face050
  shape: bbox 4.8 x 25.5 x 2e-07 mm, 1 faces, 0 solids (baked)
FEATURE [Part::Revolution] Revolve054  label="moreFrontCaseScrewPost001"
  Angle = 360
  Axis = (0,1,0)
  Base = (0,0,0)
  FaceMakerClass = Part::FaceMakerBullseye
  Placement = pos=(102.5,4.5,3.5) rot=(0,0,1;0rad)
  Solid = false
  Source = -> Face050
  Symmetric = false
FEATURE [Part::Feature] Face051
  shape: bbox 4.8 x 25.5 x 2e-07 mm, 1 faces, 0 solids (baked)
FEATURE [Part::Revolution] Revolve055  label="moreFrontCaseScrewPost002"
  Angle = 360
  Axis = (0,1,0)
  Base = (0,0,0)
  FaceMakerClass = Part::FaceMakerBullseye
  Placement = pos=(102.5,4.5,68.5) rot=(0,0,1;0rad)
  Solid = false
  Source = -> Face051
  Symmetric = false
FEATURE [Sketcher::SketchObject] Sketch027
  FullyConstrained = true
  sketch-geometry (10):
    g0: LineSegment StartX=-1.6 StartY=4.7 StartZ=0 EndX=-1.6 EndY=1.7 EndZ=0
    g1: LineSegment StartX=-3.5 StartY=4.7 StartZ=0 EndX=-1.6 EndY=4.7 EndZ=0
    g2: LineSegment StartX=-1.6 StartY=1.7 StartZ=0 EndX=-1.6 EndY=1.5 EndZ=0
    g3: LineSegment StartX=-1.6 StartY=1.5 StartZ=0 EndX=-5.2 EndY=1.5 EndZ=0
    g4: Circle CenterX=-3.5 CenterY=4.7 CenterZ=0 NormalX=0 NormalY=0 NormalZ=1 AngleXU=0 Radius=1
    g5: Circle CenterX=-3.59627 CenterY=2.99743 CenterZ=0 NormalX=0 NormalY=0 NormalZ=1 AngleXU=0 Radius=1
    g6: Circle CenterX=-5.2 CenterY=1.5 CenterZ=0 NormalX=0 NormalY=0 NormalZ=1 AngleXU=0 Radius=1
    g7: BSplineCurve PolesCount=3 KnotsCount=2 Degree=2 IsPeriodic=0
    g8: GeomPoint X=-3.5 Y=4.7 Z=0
    g9: GeomPoint X=-5.2 Y=1.5 Z=0
  constraints (23):
    c: Vertical(g0)
    c: Distance(g0) = 3
    c: Coincident(g1,g0)
    c: Horizontal(g1)
    c: Block(g0)
    c: Block(g1)
    c: Coincident(g2,g0)
    c: Vertical(g2)
    c: Distance(g2) = 0.2
    c: Coincident(g3,g2)
    c: Horizontal(g3)
    c: Block(g3)
    c: Coincident(g7,g1)
    c: Weight(g4) = 1
    c: Equal(g4,g5)
    c: Equal(g4,g6)
    c: Coincident(g7,g3)
    c: InternalAlignment(g4,g7)
    c: InternalAlignment(g5,g7)
    c: InternalAlignment(g6,g7)
    c: InternalAlignment(g8,g7)
    c: InternalAlignment(g9,g7)
    c: Block(g7)
FEATURE [Sketcher::SketchObject] Sketch028
  FullyConstrained = true
  sketch-geometry (18):
    g0: LineSegment StartX=0 StartY=3e-16 StartZ=0 EndX=0 EndY=1.7 EndZ=0
    g1: LineSegment StartX=-3.5 StartY=0 StartZ=0 EndX=-3.5 EndY=0.9 EndZ=0
    g2: Circle CenterX=-2.7 CenterY=1.7 CenterZ=0 NormalX=0 NormalY=0 NormalZ=1 AngleXU=0 Radius=1
    g3: Circle CenterX=-3.5 CenterY=1.7 CenterZ=0 NormalX=0 NormalY=0 NormalZ=1 AngleXU=0 Radius=1
    g4: Circle CenterX=-3.5 CenterY=0.9 CenterZ=0 NormalX=0 NormalY=0 NormalZ=1 AngleXU=0 Radius=1
    g5: BSplineCurve PolesCount=3 KnotsCount=2 Degree=2 IsPeriodic=0
    g6: GeomPoint X=-2.7 Y=1.7 Z=0
    g7: GeomPoint X=-3.5 Y=0.9 Z=0
    g8: LineSegment StartX=-3.5 StartY=0 StartZ=0 EndX=-3.5 EndY=-7 EndZ=0
    g9: LineSegment StartX=0 StartY=3e-16 StartZ=0 EndX=0 EndY=-7 EndZ=0
    g10: LineSegment StartX=-3.5 StartY=-7 StartZ=0 EndX=0 EndY=-7 EndZ=0
    g11: LineSegment StartX=-2.7 StartY=1.7 StartZ=0 EndX=-1.6 EndY=1.7 EndZ=0
    g12: LineSegment StartX=0 StartY=1.7 StartZ=0 EndX=0 EndY=4.5 EndZ=0
    g13: LineSegment StartX=0 StartY=4.5 StartZ=0 EndX=0 EndY=10.8 EndZ=0
    g14: LineSegment StartX=0 StartY=10.8 StartZ=0 EndX=-2 EndY=10.8 EndZ=0
    g15: LineSegment StartX=-1.6 StartY=4.7 StartZ=0 EndX=-1.6 EndY=1.7 EndZ=0
    g16: LineSegment StartX=-1.6 StartY=4.7 StartZ=0 EndX=-2 EndY=4.7 EndZ=0
    g17: LineSegment StartX=-2 StartY=4.7 StartZ=0 EndX=-2 EndY=10.8 EndZ=0
  constraints (44):
    c: Vertical(g0)
    c: Vertical(g1)
    c: Distance(g1) = 0.9
    c: Block(g0)
    c: Distance(g0) = 1.7
    c: Weight(g2) = 1
    c: Equal(g2,g3)
    c: Equal(g2,g4)
    c: Coincident(g5,g1)
    c: InternalAlignment(g2,g5)
    c: InternalAlignment(g3,g5)
    c: InternalAlignment(g4,g5)
    c: InternalAlignment(g6,g5)
    c: InternalAlignment(g7,g5)
    c: Block(g5)
    c: Coincident(g8,g1)
    c: Vertical(g8)
    c: Distance(g8) = 7
    c: Vertical(g9)
    c: Equal(g8,g9) = 7
    c: Coincident(g9,g0)
    c: Coincident(g10,g8)
    c: Coincident(g10,g9)
    c: Horizontal(g10)
    c: Coincident(g11,g5)
    c: Horizontal(g11)
    c: Coincident(g12,g0)
    c: Vertical(g12)
    c: Distance(g12) = 2.8
    c: Coincident(g13,g12)
    c: Vertical(g13)
    c: Distance(g13) = 6.3
    c: Coincident(g14,g13)
    c: Horizontal(g14)
    c: Distance(g14) = 2
    c: Vertical(g15)
    c: Distance(g15) = 3
    c: Block(g11)
    c: Coincident(g15,g11)
    c: Coincident(g16,g15)
    c: Horizontal(g16)
    c: Coincident(g17,g16)
    c: Coincident(g17,g14)
    c: Vertical(g17)
FEATURE [Part::Revolution] Revolve040  label="backCaseScrewRetainer001"
  Angle = 360
  Axis = (0,1,0)
  Base = (0,0,0)
  FaceMakerClass = Part::FaceMakerBullseye
  Placement = pos=(12.5,3,10) rot=(0,0,1;0rad)
  Solid = false
  Source = -> Face036
  Symmetric = false
FEATURE [Part::Feature] Face055
  shape: bbox 3.5 x 30.2 x 2e-07 mm, 1 faces, 0 solids (baked)
FEATURE [Part::Revolution] Revolve059  label="backCaseScrewPost"
  Angle = 360
  Axis = (0,1,0)
  Base = (0,0,0)
  FaceMakerClass = Part::FaceMakerBullseye
  Placement = pos=(12.5,4.5,10) rot=(0,0,1;0rad)
  Solid = false
  Source = -> Face055
  Symmetric = false
FEATURE [Part::Feature] Face056
  shape: bbox 3.5 x 30.2 x 2e-07 mm, 1 faces, 0 solids (baked)
FEATURE [Part::Revolution] Revolve060  label="backCaseScrewPost001"
  Angle = 360
  Axis = (0,1,0)
  Base = (0,0,0)
  FaceMakerClass = Part::FaceMakerBullseye
  Placement = pos=(12.5,4.5,62) rot=(0,0,1;0rad)
  Solid = false
  Source = -> Face056
  Symmetric = false
FEATURE [Part::Feature] Face057
  shape: bbox 3.5 x 17.8 x 2e-07 mm, 1 faces, 0 solids (baked)
FEATURE [Part::Revolution] Revolve061  label="removeToCreateScrewAndThreadedInsertHole"
  Angle = 360
  Axis = (0,1,0)
  Base = (0,0,0)
  FaceMakerClass = Part::FaceMakerBullseye
  Placement = pos=(12.5,0,10) rot=(0,0,1;0rad)
  Solid = false
  Source = -> Face057
  Symmetric = false
FEATURE [Part::Feature] Face058
  shape: bbox 3.5 x 17.8 x 2e-07 mm, 1 faces, 0 solids (baked)
FEATURE [Part::Revolution] Revolve062  label="removeToCreateScrewAndThreadedInsertHole001"
  Angle = 360
  Axis = (0,1,0)
  Base = (0,0,0)
  FaceMakerClass = Part::FaceMakerBullseye
  Placement = pos=(12.5,0,62) rot=(0,0,1;0rad)
  Solid = false
  Source = -> Face058
  Symmetric = false
FEATURE [Part::Feature] Face059
  shape: bbox 3.5 x 17.8 x 2e-07 mm, 1 faces, 0 solids (baked)
FEATURE [Part::Revolution] Revolve063  label="removeToCreateScrewAndThreadedInsertHole002"
  Angle = 360
  Axis = (0,1,0)
  Base = (0,0,0)
  FaceMakerClass = Part::FaceMakerBullseye
  Placement = pos=(89.5,0,68.5) rot=(0,0,1;0rad)
  Solid = false
  Source = -> Face059
  Symmetric = false
FEATURE [Part::Feature] Face060
  shape: bbox 3.5 x 17.8 x 2e-07 mm, 1 faces, 0 solids (baked)
FEATURE [Part::Revolution] Revolve064  label="removeToCreateScrewAndThreadedInsertHole003"
  Angle = 360
  Axis = (0,1,0)
  Base = (0,0,0)
  FaceMakerClass = Part::FaceMakerBullseye
  Placement = pos=(89.5,0,3.5) rot=(0,0,1;0rad)
  Solid = false
  Source = -> Face060
  Symmetric = false
FEATURE [Part::Feature] Face061
  shape: bbox 3.5 x 17.8 x 2e-07 mm, 1 faces, 0 solids (baked)
FEATURE [Part::Revolution] Revolve065  label="removeToCreateScrewAndThreadedInsertHole004"
  Angle = 360
  Axis = (0,1,0)
  Base = (0,0,0)
  FaceMakerClass = Part::FaceMakerBullseye
  Placement = pos=(102.5,4.7,3.5) rot=(0,0,1;0rad)
  Solid = false
  Source = -> Face061
  Symmetric = false
FEATURE [Part::Feature] Face062
  shape: bbox 3.5 x 17.8 x 2e-07 mm, 1 faces, 0 solids (baked)
FEATURE [Part::Revolution] Revolve066  label="removeToCreateScrewAndThreadedInsertHole005"
  Angle = 360
  Axis = (0,1,0)
  Base = (0,0,0)
  FaceMakerClass = Part::FaceMakerBullseye
  Placement = pos=(102.5,4.7,68.5) rot=(0,0,1;0rad)
  Solid = false
  Source = -> Face062
  Symmetric = false
FEATURE [Part::MultiFuse] Fusion047  label="makeHoles"
  Shapes = -> [Revolve066,Revolve065,Revolve064,Revolve063,Revolve062,Revolve061]
FEATURE [Part::Feature] Face063
  shape: bbox 3.6 x 3.2 x 2e-07 mm, 1 faces, 0 solids (baked)
FEATURE [Part::Revolution] Revolve067  label="moreFrontCaseScrewRetainer002"
  Angle = 360
  Axis = (0,1,0)
  Base = (0,0,0)
  FaceMakerClass = Part::FaceMakerBullseye
  Placement = pos=(102.5,4.5,68.5) rot=(0,0,1;0rad)
  Solid = false
  Source = -> Face063
  Symmetric = false
FEATURE [Part::Feature] Face064
  shape: bbox 3.6 x 3.2 x 2e-07 mm, 1 faces, 0 solids (baked)
FEATURE [Part::Revolution] Revolve068  label="moreFrontCaseScrewRetainer003"
  Angle = 360
  Axis = (0,1,0)
  Base = (0,0,0)
  FaceMakerClass = Part::FaceMakerBullseye
  Placement = pos=(102.5,4.5,3.5) rot=(0,0,1;0rad)
  Solid = false
  Source = -> Face064
  Symmetric = false
FEATURE [Part::Feature] Face065
  shape: bbox 3.5 x 17.8 x 2e-07 mm, 1 faces, 0 solids (baked)
FEATURE [Part::Revolution] Revolve069  label="removeToCreateScrewAndThreadedInsertHole006"
  Angle = 360
  Axis = (0,1,0)
  Base = (0,0,0)
  FaceMakerClass = Part::FaceMakerBullseye
  Placement = pos=(12.5,0,10) rot=(0,0,1;0rad)
  Solid = false
  Source = -> Face065
  Symmetric = false
FEATURE [Part::Feature] Face066
  shape: bbox 3.5 x 17.8 x 2e-07 mm, 1 faces, 0 solids (baked)
FEATURE [Part::Revolution] Revolve070  label="removeToCreateScrewAndThreadedInsertHole007"
  Angle = 360
  Axis = (0,1,0)
  Base = (0,0,0)
  FaceMakerClass = Part::FaceMakerBullseye
  Placement = pos=(12.5,0,62) rot=(0,0,1;0rad)
  Solid = false
  Source = -> Face066
  Symmetric = false
FEATURE [Part::Feature] Face067
  shape: bbox 3.5 x 17.8 x 2e-07 mm, 1 faces, 0 solids (baked)
FEATURE [Part::Revolution] Revolve071  label="removeToCreateScrewAndThreadedInsertHole008"
  Angle = 360
  Axis = (0,1,0)
  Base = (0,0,0)
  FaceMakerClass = Part::FaceMakerBullseye
  Placement = pos=(89.5,0,68.5) rot=(0,0,1;0rad)
  Solid = false
  Source = -> Face067
  Symmetric = false
FEATURE [Part::Feature] Face068
  shape: bbox 3.5 x 17.8 x 2e-07 mm, 1 faces, 0 solids (baked)
FEATURE [Part::Revolution] Revolve072  label="removeToCreateScrewAndThreadedInsertHole009"
  Angle = 360
  Axis = (0,1,0)
  Base = (0,0,0)
  FaceMakerClass = Part::FaceMakerBullseye
  Placement = pos=(89.5,0,3.5) rot=(0,0,1;0rad)
  Solid = false
  Source = -> Face068
  Symmetric = false
FEATURE [Part::Feature] Face069
  shape: bbox 3.5 x 17.8 x 2e-07 mm, 1 faces, 0 solids (baked)
FEATURE [Part::Feature] Face070
  shape: bbox 3.5 x 17.8 x 2e-07 mm, 1 faces, 0 solids (baked)
FEATURE [Part::Revolution] Revolve073  label="removeToCreateScrewAndThreadedInsertHole010"
  Angle = 360
  Axis = (0,1,0)
  Base = (0,0,0)
  FaceMakerClass = Part::FaceMakerBullseye
  Placement = pos=(102.5,4.7,3.5) rot=(0,0,1;0rad)
  Solid = false
  Source = -> Face069
  Symmetric = false
FEATURE [Part::Revolution] Revolve074  label="removeToCreateScrewAndThreadedInsertHole011"
  Angle = 360
  Axis = (0,1,0)
  Base = (0,0,0)
  FaceMakerClass = Part::FaceMakerBullseye
  Placement = pos=(102.5,4.7,68.5) rot=(0,0,1;0rad)
  Solid = false
  Source = -> Face070
  Symmetric = false
FEATURE [Part::MultiFuse] Fusion048  label="makeHoles001"
  Shapes = -> [Revolve074,Revolve073,Revolve072,Revolve071,Revolve070,Revolve069]
FEATURE [Part::MultiFuse] Fusion049  label="caseScrewRetainers"
  Shapes = -> [Revolve067,Revolve068,Revolve048,Revolve047,Revolve039,Revolve040]
FEATURE [Part::Cut] Cut015  label="caseScrewRetainers001"
  Base = -> Fusion049
  Tool = -> Fusion048
FEATURE [Part::MultiFuse] Fusion050  label="casePillars"
  Shapes = -> [Revolve055,Revolve054,Revolve043,Revolve046,Revolve059,Revolve060]
FEATURE [Part::Feature] Face071 .. Face076  x6 (patterned run collapsed; names and placements below)
  shape: bbox 3.5 x 17.8 x 2e-07 mm, 1 faces, 0 solids (baked)
FEATURE [Part::Revolution] Revolve075  label="removeToCreateScrewAndThreadedInsertHole012"
  Angle = 360
  Axis = (0,1,0)
  Base = (0,0,0)
  FaceMakerClass = Part::FaceMakerBullseye
  Placement = pos=(12.5,0,10) rot=(0,0,1;0rad)
  Solid = false
  Source = -> Face071
  Symmetric = false
FEATURE [Part::Revolution] Revolve076  label="removeToCreateScrewAndThreadedInsertHole013"
  Angle = 360
  Axis = (0,1,0)
  Base = (0,0,0)
  FaceMakerClass = Part::FaceMakerBullseye
  Placement = pos=(12.5,0,62) rot=(0,0,1;0rad)
  Solid = false
  Source = -> Face072
  Symmetric = false
FEATURE [Part::Revolution] Revolve077  label="removeToCreateScrewAndThreadedInsertHole014"
  Angle = 360
  Axis = (0,1,0)
  Base = (0,0,0)
  FaceMakerClass = Part::FaceMakerBullseye
  Placement = pos=(89.5,0,68.5) rot=(0,0,1;0rad)
  Solid = false
  Source = -> Face073
  Symmetric = false
FEATURE [Part::Revolution] Revolve078  label="removeToCreateScrewAndThreadedInsertHole015"
  Angle = 360
  Axis = (0,1,0)
  Base = (0,0,0)
  FaceMakerClass = Part::FaceMakerBullseye
  Placement = pos=(89.5,0,3.5) rot=(0,0,1;0rad)
  Solid = false
  Source = -> Face074
  Symmetric = false
FEATURE [Part::Revolution] Revolve079  label="removeToCreateScrewAndThreadedInsertHole016"
  Angle = 360
  Axis = (0,1,0)
  Base = (0,0,0)
  FaceMakerClass = Part::FaceMakerBullseye
  Placement = pos=(102.5,4.7,3.5) rot=(0,0,1;0rad)
  Solid = false
  Source = -> Face075
  Symmetric = false
FEATURE [Part::Revolution] Revolve080  label="removeToCreateScrewAndThreadedInsertHole017"
  Angle = 360
  Axis = (0,1,0)
  Base = (0,0,0)
  FaceMakerClass = Part::FaceMakerBullseye
  Placement = pos=(102.5,4.7,68.5) rot=(0,0,1;0rad)
  Solid = false
  Source = -> Face076
  Symmetric = false
FEATURE [Part::MultiFuse] Fusion051  label="makeHoles002"
  Shapes = -> [Revolve080,Revolve079,Revolve078,Revolve077,Revolve076,Revolve075]
FEATURE [Part::Cut] Cut016  label="caesPillars"
  Base = -> Fusion050
  Tool = -> Fusion051
FEATURE [Part::Revolution] Revolve009  label="plugHousing016"
  Angle = 360
  Axis = (0,1,0)
  Base = (0,0,0)
  FaceMakerClass = Part::FaceMakerBullseye
  Placement = pos=(0,0,36.15) rot=(0,0,1;0rad)
  Solid = false
  Source = -> Face012
  Symmetric = false
FEATURE [Part::MultiFuse] Fusion014  label="plugHousing023"
  Placement = pos=(0,0,0) rot=(0,0,1;1.5708rad)
  Shapes = -> [Revolve011,Revolve009]
FEATURE [Part::Revolution] Revolve010  label="plugHousing017"
  Angle = 360
  Axis = (0,1,0)
  Base = (0,0,0)
  FaceMakerClass = Part::FaceMakerBullseye
  Placement = pos=(0,0,36.15) rot=(0,0,1;0rad)
  Solid = false
  Source = -> Face014
  Symmetric = false
FEATURE [Part::MultiFuse] Fusion015  label="plugHousing024"
  Placement = pos=(0,0,0) rot=(0,0,1;1.5708rad)
  Shapes = -> [Revolve010,Revolve015]
FEATURE [Part::Revolution] Revolve014  label="plugHousing026"
  Angle = 360
  Axis = (0,1,0)
  Base = (0,0,0)
  FaceMakerClass = Part::FaceMakerBullseye
  Placement = pos=(0,0,36.15) rot=(0,0,1;0rad)
  Solid = false
  Source = -> Face011
  Symmetric = false
FEATURE [Part::Revolution] Revolve013  label="plugHousing025"
  Angle = 360
  Axis = (0,1,0)
  Base = (0,0,0)
  FaceMakerClass = Part::FaceMakerBullseye
  Placement = pos=(0,0,36.15) rot=(0,0,1;0rad)
  Solid = false
  Source = -> Face015
  Symmetric = false
FEATURE [Part::MultiFuse] Fusion016  label="plugHousing028"
  Placement = pos=(0,19,0) rot=(0,0,1;3.14159rad)
  Shapes = -> [Fusion014,Fusion013]
FEATURE [Part::MultiFuse] Fusion011  label="plugHousing018"
  Placement = pos=(0,0,0) rot=(0,0,1;1.5708rad)
  Shapes = -> [Revolve014,Revolve013]
FEATURE [Part::MultiFuse] Fusion012  label="plugHousing019"
  Placement = pos=(0,19,0) rot=(0,0,1;3.14159rad)
  Shapes = -> [Fusion011,Fusion015]
FEATURE [Part::MultiFuse] Fusion017  label="plugHousing029"
  Placement = pos=(122.621,0,-0.15) rot=(0,0,1;0rad)
  Shapes = -> [Fusion016,Fusion012]
FEATURE [Part::MultiFuse] Fusion052  label="casePillarRetainers"
  Shapes = -> [Extrude012,Extrude013,Extrude014,Extrude015,Extrude016,Extrude017,Extrude018,Extrude019,Box011,Box012]
FEATURE [Part::Feature] Face077
  shape: bbox 3.5 x 17.8 x 2e-07 mm, 1 faces, 0 solids (baked)
FEATURE [Part::Revolution] Revolve081  label="removeToCreateScrewAndThreadedInsertHole018"
  Angle = 360
  Axis = (0,1,0)
  Base = (0,0,0)
  FaceMakerClass = Part::FaceMakerBullseye
  Placement = pos=(62.3,30.3,19.7) rot=(0,0,1;0rad)
  Solid = false
  Source = -> Face077
  Symmetric = false
FEATURE [Part::Feature] Face078
  shape: bbox 3.5 x 17.8 x 2e-07 mm, 1 faces, 0 solids (baked)
FEATURE [Part::Revolution] Revolve082  label="removeToCreateScrewAndThreadedInsertHole019"
  Angle = 360
  Axis = (0,1,0)
  Base = (0,0,0)
  FaceMakerClass = Part::FaceMakerBullseye
  Placement = pos=(62.3,30.3,51.7) rot=(0,0,1;0rad)
  Solid = false
  Source = -> Face078
  Symmetric = false
FEATURE [Part::Feature] Face079
  shape: bbox 3.5 x 17.8 x 2e-07 mm, 1 faces, 0 solids (baked)
FEATURE [Part::Revolution] Revolve083  label="removeToCreateScrewAndThreadedInsertHole020"
  Angle = 360
  Axis = (0,1,0)
  Base = (0,0,0)
  FaceMakerClass = Part::FaceMakerBullseye
  Placement = pos=(30.3,30.3,19.7) rot=(0,0,1;0rad)
  Solid = false
  Source = -> Face079
  Symmetric = false
FEATURE [Part::Feature] Face080
  shape: bbox 3.5 x 17.8 x 2e-07 mm, 1 faces, 0 solids (baked)
FEATURE [Part::Revolution] Revolve084  label="removeToCreateScrewAndThreadedInsertHole021"
  Angle = 360
  Axis = (0,1,0)
  Base = (0,0,0)
  FaceMakerClass = Part::FaceMakerBullseye
  Placement = pos=(30.3,30.3,51.7) rot=(0,0,1;0rad)
  Solid = false
  Source = -> Face080
  Symmetric = false
FEATURE [Part::MultiFuse] Fusion053  label="createThreadedInsertHolesForFan"
  Shapes = -> [Revolve081,Revolve082,Revolve083,Revolve084]
FEATURE [Part::Cut] Cut017  label="fanScrewHousing001"
  Base = -> Fusion046
  Tool = -> Fusion053
FEATURE [Part::Feature] Face081
  shape: bbox 3.5 x 17.8 x 2e-07 mm, 1 faces, 0 solids (baked)
FEATURE [Part::Revolution] Revolve085  label="removeToCreateScrewAndThreadedInsertHole022"
  Angle = 360
  Axis = (0,1,0)
  Base = (0,0,0)
  FaceMakerClass = Part::FaceMakerBullseye
  Placement = pos=(62.3,30.3,19.7) rot=(0,0,1;0rad)
  Solid = false
  Source = -> Face081
  Symmetric = false
FEATURE [Part::Feature] Face082
  shape: bbox 3.5 x 17.8 x 2e-07 mm, 1 faces, 0 solids (baked)
FEATURE [Part::Revolution] Revolve086  label="removeToCreateScrewAndThreadedInsertHole023"
  Angle = 360
  Axis = (0,1,0)
  Base = (0,0,0)
  FaceMakerClass = Part::FaceMakerBullseye
  Placement = pos=(62.3,30.3,51.7) rot=(0,0,1;0rad)
  Solid = false
  Source = -> Face082
  Symmetric = false
FEATURE [Part::Feature] Face083
  shape: bbox 3.5 x 17.8 x 2e-07 mm, 1 faces, 0 solids (baked)
FEATURE [Part::Revolution] Revolve087  label="removeToCreateScrewAndThreadedInsertHole024"
  Angle = 360
  Axis = (0,1,0)
  Base = (0,0,0)
  FaceMakerClass = Part::FaceMakerBullseye
  Placement = pos=(30.3,30.3,19.7) rot=(0,0,1;0rad)
  Solid = false
  Source = -> Face083
  Symmetric = false
FEATURE [Part::Feature] Face084
  shape: bbox 3.5 x 17.8 x 2e-07 mm, 1 faces, 0 solids (baked)
FEATURE [Part::Revolution] Revolve088  label="removeToCreateScrewAndThreadedInsertHole025"
  Angle = 360
  Axis = (0,1,0)
  Base = (0,0,0)
  FaceMakerClass = Part::FaceMakerBullseye
  Placement = pos=(30.3,30.3,51.7) rot=(0,0,1;0rad)
  Solid = false
  Source = -> Face084
  Symmetric = false
FEATURE [Part::MultiFuse] Fusion054  label="createThreadedInsertHolesForFan001"
  Shapes = -> [Revolve085,Revolve086,Revolve087,Revolve088]
FEATURE [Part::Cut] Cut018  label="top007"
  Base = -> Fusion040
  Tool = -> Fusion054
FEATURE [Sketcher::SketchObject] Sketch029
  FullyConstrained = false
  Placement = pos=(0,0,0) rot=(1,0,0;1.5708rad)
  sketch-geometry (24):
    g0: ArcOfCircle CenterX=-4 CenterY=-10.5 CenterZ=0 NormalX=0 NormalY=0 NormalZ=1 AngleXU=0 Radius=1.5 StartAngle=6e-16 EndAngle=3.14159
    g1: ArcOfCircle CenterX=-34.2 CenterY=-10.5 CenterZ=0 NormalX=0 NormalY=0 NormalZ=1 AngleXU=0 Radius=1.5 StartAngle=0 EndAngle=3.14159
    g2: ArcOfCircle CenterX=-34.2 CenterY=-27.7 CenterZ=0 NormalX=0 NormalY=0 NormalZ=1 AngleXU=0 Radius=1.5 StartAngle=3.14159 EndAngle=6.28319
    g3: ArcOfCircle CenterX=-4 CenterY=-27.7 CenterZ=0 NormalX=0 NormalY=0 NormalZ=1 AngleXU=0 Radius=1.5 StartAngle=3.1416 EndAngle=6.28319
    g4: ArcOfCircle CenterX=-10 CenterY=-4.3 CenterZ=0 NormalX=0 NormalY=0 NormalZ=1 AngleXU=0 Radius=1.5 StartAngle=2e-16 EndAngle=3.14159
    g5: ArcOfCircle CenterX=-16.1 CenterY=-1.8 CenterZ=0 NormalX=0 NormalY=0 NormalZ=1 AngleXU=0 Radius=1.5 StartAngle=5e-16 EndAngle=3.14159
    g6: ArcOfCircle CenterX=-22.1 CenterY=-1.8 CenterZ=0 NormalX=0 NormalY=0 NormalZ=1 AngleXU=0 Radius=1.5 StartAngle=5e-16 EndAngle=3.14159
    g7: ArcOfCircle CenterX=-28.2 CenterY=-4.3 CenterZ=0 NormalX=0 NormalY=0 NormalZ=1 AngleXU=0 Radius=1.5 StartAngle=2e-16 EndAngle=3.14159
    g8: ArcOfCircle CenterX=-10 CenterY=-33.9 CenterZ=0 NormalX=0 NormalY=0 NormalZ=1 AngleXU=0 Radius=1.5 StartAngle=3.14159 EndAngle=6.28319
    g9: ArcOfCircle CenterX=-16.1 CenterY=-36.4 CenterZ=0 NormalX=0 NormalY=0 NormalZ=1 AngleXU=0 Radius=1.5 StartAngle=3.14159 EndAngle=6.28319
    g10: ArcOfCircle CenterX=-22.1 CenterY=-36.4 CenterZ=0 NormalX=0 NormalY=0 NormalZ=1 AngleXU=0 Radius=1.5 StartAngle=3.14159 EndAngle=6.28319
    g11: ArcOfCircle CenterX=-28.2 CenterY=-33.9 CenterZ=0 NormalX=0 NormalY=0 NormalZ=1 AngleXU=0 Radius=1.5 StartAngle=3.14159 EndAngle=6.28319
    g12: LineSegment StartX=-35.7 StartY=-10.5 StartZ=0 EndX=-35.7 EndY=-27.7 EndZ=0
    g13: LineSegment StartX=-32.7 StartY=-10.5 StartZ=0 EndX=-32.7 EndY=-27.7 EndZ=0
    g14: LineSegment StartX=-29.7 StartY=-33.9 StartZ=0 EndX=-29.7 EndY=-4.3 EndZ=0
    g15: LineSegment StartX=-26.7 StartY=-33.9 StartZ=0 EndX=-26.7 EndY=-4.3 EndZ=0
    g16: LineSegment StartX=-2.5 StartY=-10.5 StartZ=0 EndX=-2.5 EndY=-27.7 EndZ=0
    g17: LineSegment StartX=-8.5 StartY=-4.3 StartZ=0 EndX=-8.5 EndY=-33.9 EndZ=0
    g18: LineSegment StartX=-5.5 StartY=-10.5 StartZ=0 EndX=-5.5 EndY=-27.7 EndZ=0
    g19: LineSegment StartX=-11.5 StartY=-4.3 StartZ=0 EndX=-11.5 EndY=-33.9 EndZ=0
    g20: LineSegment StartX=-14.6 StartY=-1.8 StartZ=0 EndX=-14.6 EndY=-36.4 EndZ=0
    g21: LineSegment StartX=-17.6 StartY=-1.8 StartZ=0 EndX=-17.6 EndY=-36.4 EndZ=0
    g22: LineSegment StartX=-20.6 StartY=-36.4 StartZ=0 EndX=-20.6 EndY=-1.8 EndZ=0
    g23: LineSegment StartX=-23.6 StartY=-1.8 StartZ=0 EndX=-23.6 EndY=-36.4 EndZ=0
  constraints (48):
    c: Block(g0)
    c: Block(g1)
    c: Block(g2)
    c: Block(g3)
    c: Block(g4)
    c: Block(g5)
    c: Block(g6)
    c: Block(g7)
    c: Block(g8)
    c: Block(g9)
    c: Block(g10)
    c: Block(g11)
    c: Coincident(g12,g1)
    c: Coincident(g12,g2)
    c: Vertical(g12)
    c: Coincident(g13,g1)
    c: Coincident(g13,g2)
    c: Vertical(g13)
    c: Coincident(g14,g11)
    c: Coincident(g14,g7)
    c: Vertical(g14)
    c: Coincident(g15,g11)
    c: Coincident(g15,g7)
    c: Vertical(g15)
    c: Coincident(g16,g0)
    c: Coincident(g16,g3)
    c: Vertical(g16)
    c: Coincident(g17,g4)
    c: Coincident(g17,g8)
    c: Vertical(g17)
    c: Coincident(g18,g0)
    c: Coincident(g18,g3)
    c: Vertical(g18)
    c: Coincident(g19,g4)
    c: Coincident(g19,g8)
    c: Vertical(g19)
    c: Coincident(g20,g5)
    c: Coincident(g20,g9)
    c: Vertical(g20)
    c: Coincident(g21,g5)
    c: Coincident(g21,g9)
    c: Vertical(g21)
    c: Coincident(g22,g10)
    c: Coincident(g22,g6)
    c: Vertical(g22)
    c: Coincident(g23,g6)
    c: Coincident(g23,g10)
    c: Vertical(g23)
FEATURE [Part::Extrusion] Extrude020  label="removeToCreateFanGrillHoles"
  Base = -> Sketch029
  Dir = (0,-1,6e-16)
  DirMode = 2
  FaceMakerClass = Part::FaceMakerBullseye
  LengthFwd = 10
  LengthRev = 0
  Placement = pos=(65.4,44,54.82) rot=(0,0,1;0rad)
  Solid = true
  Symmetric = false
FEATURE [Part::MultiFuse] Fusion055  label="top008"
  Shapes = -> [Cut017,Cut018]
FEATURE [Part::Cut] Cut019  label="top009"
  Base = -> Fusion055
  Tool = -> Extrude020
FEATURE [App::MeasureDistance] Distance003  label="Distance: 71.95 mm"
  Distance = 71.9513
  P1 = (117,38,72)
  P2 = (117,38,0.0487319)
FEATURE [Sketcher::SketchObject] Sketch030
  FullyConstrained = true
  Placement = pos=(117,19,0) rot=(0.57735,0.57735,0.57735;2.0944rad)
  sketch-geometry (48):
    g0: LineSegment StartX=-49.19 StartY=69.25 StartZ=0 EndX=-49.19 EndY=66.25 EndZ=0
    g1: LineSegment StartX=-49.19 StartY=63.5 StartZ=0 EndX=-49.19 EndY=60.5 EndZ=0
    g2: LineSegment StartX=-49.19 StartY=57.75 StartZ=0 EndX=-49.19 EndY=54.75 EndZ=0
    g3: LineSegment StartX=-49.19 StartY=52 StartZ=0 EndX=-49.19 EndY=49 EndZ=0
    g4: LineSegment StartX=-49.19 StartY=46.25 StartZ=0 EndX=-49.19 EndY=43.25 EndZ=0
    g5: LineSegment StartX=-49.19 StartY=40.5 StartZ=0 EndX=-49.19 EndY=37.5 EndZ=0
    g6: LineSegment StartX=-49.19 StartY=34.5 StartZ=0 EndX=-49.19 EndY=31.5 EndZ=0
    g7: LineSegment StartX=-49.19 StartY=28.75 StartZ=0 EndX=-49.19 EndY=25.75 EndZ=0
    g8: LineSegment StartX=-49.19 StartY=23 StartZ=0 EndX=-49.19 EndY=20 EndZ=0
    g9: LineSegment StartX=-49.19 StartY=17.25 StartZ=0 EndX=-49.19 EndY=14.25 EndZ=0
    g10: LineSegment StartX=-49.19 StartY=11.5 StartZ=0 EndX=-49.19 EndY=8.5 EndZ=0
    g11: LineSegment StartX=-49.19 StartY=5.75 StartZ=0 EndX=-49.19 EndY=2.75 EndZ=0
    g12: ArcOfCircle CenterX=-1.5 CenterY=67.75 CenterZ=0 NormalX=0 NormalY=0 NormalZ=1 AngleXU=0 Radius=1.5 StartAngle=4.71239 EndAngle=7.85398
    g13: ArcOfCircle CenterX=-1.5 CenterY=62 CenterZ=0 NormalX=0 NormalY=0 NormalZ=1 AngleXU=0 Radius=1.5 StartAngle=4.71239 EndAngle=7.85398
    g14: ArcOfCircle CenterX=-1.5 CenterY=56.25 CenterZ=0 NormalX=0 NormalY=0 NormalZ=1 AngleXU=0 Radius=1.5 StartAngle=4.71239 EndAngle=7.85398
    g15: ArcOfCircle CenterX=-11.49 CenterY=50.5 CenterZ=0 NormalX=0 NormalY=0 NormalZ=1 AngleXU=0 Radius=1.5 StartAngle=4.71239 EndAngle=7.85398
    g16: ArcOfCircle CenterX=-16.28 CenterY=44.75 CenterZ=0 NormalX=0 NormalY=0 NormalZ=1 AngleXU=0 Radius=1.5 StartAngle=4.71239 EndAngle=7.85398
    g17: ArcOfCircle CenterX=-18.2337 CenterY=39 CenterZ=0 NormalX=0 NormalY=0 NormalZ=1 AngleXU=0 Radius=1.5 StartAngle=4.71485 EndAngle=7.85398
    g18: ArcOfCircle CenterX=-16.2837 CenterY=27.25 CenterZ=0 NormalX=0 NormalY=0 NormalZ=1 AngleXU=0 Radius=1.5 StartAngle=4.71485 EndAngle=7.85398
    g19: ArcOfCircle CenterX=-18.2337 CenterY=33 CenterZ=0 NormalX=0 NormalY=0 NormalZ=1 AngleXU=0 Radius=1.5 StartAngle=4.71485 EndAngle=7.85398
    g20: ArcOfCircle CenterX=-11.49 CenterY=21.5 CenterZ=0 NormalX=0 NormalY=0 NormalZ=1 AngleXU=0 Radius=1.5 StartAngle=4.71239 EndAngle=7.85398
    g21: ArcOfCircle CenterX=-1.5 CenterY=4.25 CenterZ=0 NormalX=0 NormalY=0 NormalZ=1 AngleXU=0 Radius=1.5 StartAngle=4.71239 EndAngle=7.85398
    g22: ArcOfCircle CenterX=-1.5 CenterY=10 CenterZ=0 NormalX=0 NormalY=0 NormalZ=1 AngleXU=0 Radius=1.5 StartAngle=4.71239 EndAngle=7.85398
    g23: ArcOfCircle CenterX=-1.5 CenterY=15.75 CenterZ=0 NormalX=0 NormalY=0 NormalZ=1 AngleXU=0 Radius=1.5 StartAngle=4.71239 EndAngle=7.85398
    g24: LineSegment StartX=-49.19 StartY=69.25 StartZ=0 EndX=-1.5 EndY=69.25 EndZ=0
    g25: LineSegment StartX=-49.19 StartY=66.25 StartZ=0 EndX=-1.5 EndY=66.25 EndZ=0
    g26: LineSegment StartX=-49.19 StartY=63.5 StartZ=0 EndX=-1.5 EndY=63.5 EndZ=0
    g27: LineSegment StartX=-49.19 StartY=60.5 StartZ=0 EndX=-1.5 EndY=60.5 EndZ=0
    g28: LineSegment StartX=-49.19 StartY=57.75 StartZ=0 EndX=-1.5 EndY=57.75 EndZ=0
    g29: LineSegment StartX=-49.19 StartY=54.75 StartZ=0 EndX=-1.5 EndY=54.75 EndZ=0
    g30: LineSegment StartX=-49.19 StartY=52 StartZ=0 EndX=-11.49 EndY=52 EndZ=0
    g31: LineSegment StartX=-49.19 StartY=49 StartZ=0 EndX=-11.49 EndY=49 EndZ=0
    g32: LineSegment StartX=-49.19 StartY=46.25 StartZ=0 EndX=-16.28 EndY=46.25 EndZ=0
    g33: LineSegment StartX=-49.19 StartY=43.25 StartZ=0 EndX=-16.28 EndY=43.25 EndZ=0
    g34: LineSegment StartX=-49.19 StartY=40.5 StartZ=0 EndX=-18.2337 EndY=40.5 EndZ=0
    g35: LineSegment StartX=-49.19 StartY=37.5 StartZ=0 EndX=-18.23 EndY=37.5 EndZ=0
    g36: LineSegment StartX=-49.19 StartY=34.5 StartZ=0 EndX=-18.2337 EndY=34.5 EndZ=0
    g37: LineSegment StartX=-49.19 StartY=31.5 StartZ=0 EndX=-18.23 EndY=31.5 EndZ=0
    g38: LineSegment StartX=-49.19 StartY=28.75 StartZ=0 EndX=-16.2837 EndY=28.75 EndZ=0
    g39: LineSegment StartX=-49.19 StartY=25.75 StartZ=0 EndX=-16.28 EndY=25.75 EndZ=0
    g40: LineSegment StartX=-49.19 StartY=23 StartZ=0 EndX=-11.49 EndY=23 EndZ=0
    g41: LineSegment StartX=-49.19 StartY=20 StartZ=0 EndX=-11.49 EndY=20 EndZ=0
    g42: LineSegment StartX=-49.19 StartY=17.25 StartZ=0 EndX=-1.5 EndY=17.25 EndZ=0
    g43: LineSegment StartX=-49.19 StartY=14.25 StartZ=0 EndX=-1.5 EndY=14.25 EndZ=0
    g44: LineSegment StartX=-49.19 StartY=11.5 StartZ=0 EndX=-1.5 EndY=11.5 EndZ=0
    g45: LineSegment StartX=-49.19 StartY=8.5 StartZ=0 EndX=-1.5 EndY=8.5 EndZ=0
    g46: LineSegment StartX=-49.19 StartY=5.75 StartZ=0 EndX=-1.5 EndY=5.75 EndZ=0
    g47: LineSegment StartX=-49.19 StartY=2.75 StartZ=0 EndX=-1.5 EndY=2.75 EndZ=0
  constraints (120):
    c: Vertical(g0)
    c: Distance(g0) = 3
    c: Block(g0)
    c: Vertical(g1)
    c: Distance(g1) = 3
    c: Vertical(g2)
    c: Equal(g0,g2) = 3
    c: Block(g2)
    c: Vertical(g3)
    c: Equal(g1,g3) = 3
    c: Vertical(g4)
    c: Equal(g0,g4) = 3
    c: Block(g4)
    c: Vertical(g5)
    c: Equal(g1,g5) = 3
    c: Vertical(g6)
    c: Equal(g0,g6) = 3
    c: Block(g6)
    c: Vertical(g7)
    c: Equal(g1,g7) = 3
    c: Vertical(g8)
    c: Equal(g0,g8) = 3
    c: Block(g8)
    c: Vertical(g9)
    c: Equal(g1,g9) = 3
    c: Vertical(g10)
    c: Equal(g0,g10) = 3
    c: Block(g10)
    c: Vertical(g11)
    c: Equal(g1,g11) = 3
    c: Block(g12)
    c: Block(g13)
    c: Block(g14)
    c: Block(g15)
    c: Block(g16)
    c: Block(g17)
    c: Block(g18)
    c: Block(g19)
    c: Block(g20)
    c: Block(g21)
    c: Block(g22)
    c: Block(g23)
    c: Block(g11)
    c: Block(g9)
    c: Block(g7)
    c: Block(g5)
    c: Block(g3)
    c: Block(g1)
    c: Coincident(g24,g0)
    c: Coincident(g24,g12)
    c: Horizontal(g24)
    c: Coincident(g25,g0)
    c: Coincident(g25,g12)
    c: Horizontal(g25)
    c: Coincident(g26,g1)
    c: Coincident(g26,g13)
    c: Horizontal(g26)
    c: Coincident(g27,g1)
    c: Coincident(g27,g13)
    c: Horizontal(g27)
    c: Coincident(g28,g2)
    c: Coincident(g28,g14)
    c: Horizontal(g28)
    c: Coincident(g29,g2)
    c: Coincident(g29,g14)
    c: Horizontal(g29)
    c: Coincident(g30,g3)
    c: Coincident(g30,g15)
    c: Horizontal(g30)
    c: Coincident(g31,g3)
    c: Coincident(g31,g15)
    c: Horizontal(g31)
    c: Coincident(g32,g4)
    c: Coincident(g32,g16)
    c: Horizontal(g32)
    c: Coincident(g33,g4)
    c: Coincident(g33,g16)
    c: Horizontal(g33)
    c: Coincident(g34,g5)
    c: Coincident(g34,g17)
    c: Horizontal(g34)
    c: Coincident(g35,g5)
    c: Coincident(g35,g17)
    c: Horizontal(g35)
    c: Coincident(g36,g6)
    c: Coincident(g36,g19)
    c: Horizontal(g36)
    c: Coincident(g37,g6)
    c: Coincident(g37,g19)
    c: Horizontal(g37)
    c: Coincident(g38,g7)
    c: Coincident(g38,g18)
    c: Horizontal(g38)
    c: Coincident(g39,g7)
    c: Coincident(g39,g18)
    c: Horizontal(g39)
    c: Coincident(g40,g8)
    c: Coincident(g40,g20)
    c: Horizontal(g40)
    c: Coincident(g41,g8)
    c: Coincident(g41,g20)
    c: Horizontal(g41)
    c: Coincident(g42,g9)
    c: Coincident(g42,g23)
    c: Horizontal(g42)
    c: Coincident(g43,g9)
    c: Coincident(g43,g23)
    c: Horizontal(g43)
    c: Coincident(g44,g10)
    c: Coincident(g44,g22)
    c: Horizontal(g44)
    c: Coincident(g45,g10)
    c: Coincident(g45,g22)
    c: Horizontal(g45)
    c: Coincident(g46,g11)
    c: Coincident(g46,g21)
    c: Horizontal(g46)
    c: Coincident(g47,g11)
    c: Coincident(g47,g21)
    c: Horizontal(g47)
FEATURE [Sketcher::SketchObject] Sketch031
  FullyConstrained = true
  Placement = pos=(117,19,0) rot=(0.57735,0.57735,0.57735;2.0944rad)
  sketch-geometry (24):
    g0: ArcOfCircle CenterX=-49.19 CenterY=67.75 CenterZ=0 NormalX=0 NormalY=0 NormalZ=1 AngleXU=0 Radius=1.5 StartAngle=1.5708 EndAngle=4.71239
    g1: ArcOfCircle CenterX=-49.19 CenterY=62 CenterZ=0 NormalX=0 NormalY=0 NormalZ=1 AngleXU=0 Radius=1.5 StartAngle=1.5708 EndAngle=4.71239
    g2: ArcOfCircle CenterX=-49.19 CenterY=56.25 CenterZ=0 NormalX=0 NormalY=0 NormalZ=1 AngleXU=0 Radius=1.5 StartAngle=1.5708 EndAngle=4.71239
    g3: ArcOfCircle CenterX=-49.19 CenterY=50.5 CenterZ=0 NormalX=0 NormalY=0 NormalZ=1 AngleXU=0 Radius=1.5 StartAngle=1.5708 EndAngle=4.71239
    g4: ArcOfCircle CenterX=-49.19 CenterY=44.75 CenterZ=0 NormalX=0 NormalY=0 NormalZ=1 AngleXU=0 Radius=1.5 StartAngle=1.5708 EndAngle=4.71239
    g5: ArcOfCircle CenterX=-49.19 CenterY=39 CenterZ=0 NormalX=0 NormalY=0 NormalZ=1 AngleXU=0 Radius=1.5 StartAngle=1.5708 EndAngle=4.71239
    g6: ArcOfCircle CenterX=-49.19 CenterY=33 CenterZ=0 NormalX=0 NormalY=0 NormalZ=1 AngleXU=0 Radius=1.5 StartAngle=1.5708 EndAngle=4.71239
    g7: ArcOfCircle CenterX=-49.19 CenterY=27.25 CenterZ=0 NormalX=0 NormalY=0 NormalZ=1 AngleXU=0 Radius=1.5 StartAngle=1.5708 EndAngle=4.71239
    g8: ArcOfCircle CenterX=-49.19 CenterY=21.5 CenterZ=0 NormalX=0 NormalY=0 NormalZ=1 AngleXU=0 Radius=1.5 StartAngle=1.5708 EndAngle=4.71239
    g9: ArcOfCircle CenterX=-49.19 CenterY=15.75 CenterZ=0 NormalX=0 NormalY=0 NormalZ=1 AngleXU=0 Radius=1.5 StartAngle=1.5708 EndAngle=4.71239
    g10: ArcOfCircle CenterX=-49.19 CenterY=10 CenterZ=0 NormalX=0 NormalY=0 NormalZ=1 AngleXU=0 Radius=1.5 StartAngle=1.5708 EndAngle=4.71239
    g11: ArcOfCircle CenterX=-49.19 CenterY=4.25 CenterZ=0 NormalX=0 NormalY=0 NormalZ=1 AngleXU=0 Radius=1.5 StartAngle=1.5708 EndAngle=4.71239
    g12: LineSegment StartX=-49.19 StartY=69.25 StartZ=0 EndX=-49.19 EndY=66.25 EndZ=0
    g13: LineSegment StartX=-49.19 StartY=63.5 StartZ=0 EndX=-49.19 EndY=60.5 EndZ=0
    g14: LineSegment StartX=-49.19 StartY=57.75 StartZ=0 EndX=-49.19 EndY=54.75 EndZ=0
    g15: LineSegment StartX=-49.19 StartY=52 StartZ=0 EndX=-49.19 EndY=49 EndZ=0
    g16: LineSegment StartX=-49.19 StartY=46.25 StartZ=0 EndX=-49.19 EndY=43.25 EndZ=0
    g17: LineSegment StartX=-49.19 StartY=40.5 StartZ=0 EndX=-49.19 EndY=37.5 EndZ=0
    g18: LineSegment StartX=-49.19 StartY=34.5 StartZ=0 EndX=-49.19 EndY=31.5 EndZ=0
    g19: LineSegment StartX=-49.19 StartY=28.75 StartZ=0 EndX=-49.19 EndY=25.75 EndZ=0
    g20: LineSegment StartX=-49.19 StartY=23 StartZ=0 EndX=-49.19 EndY=20 EndZ=0
    g21: LineSegment StartX=-49.19 StartY=17.25 StartZ=0 EndX=-49.19 EndY=14.25 EndZ=0
    g22: LineSegment StartX=-49.19 StartY=11.5 StartZ=0 EndX=-49.19 EndY=8.5 EndZ=0
    g23: LineSegment StartX=-49.19 StartY=5.75 StartZ=0 EndX=-49.19 EndY=2.75 EndZ=0
  constraints (48):
    c: Block(g0)
    c: Block(g1)
    c: Block(g2)
    c: Block(g3)
    c: Block(g4)
    c: Block(g5)
    c: Block(g6)
    c: Block(g7)
    c: Block(g8)
    c: Block(g9)
    c: Block(g10)
    c: Block(g11)
    c: Coincident(g12,g0)
    c: Coincident(g12,g0)
    c: Vertical(g12)
    c: Vertical(g13)
    c: Coincident(g13,g1)
    c: Vertical(g14)
    c: Coincident(g14,g2)
    c: Vertical(g15)
    c: Coincident(g15,g3)
    c: Vertical(g16)
    c: Coincident(g16,g4)
    c: Vertical(g17)
    c: Coincident(g17,g5)
    c: Vertical(g18)
    c: Coincident(g18,g6)
    c: Vertical(g19)
    c: Coincident(g19,g7)
    c: Vertical(g20)
    c: Coincident(g20,g8)
    c: Vertical(g21)
    c: Coincident(g21,g9)
    c: Vertical(g22)
    c: Coincident(g22,g10)
    c: Vertical(g23)
    c: Coincident(g23,g11)
    c: Block(g23)
    c: Block(g22)
    c: Block(g21)
    c: Block(g20)
    c: Block(g13)
    c: Block(g14)
    c: Block(g15)
    c: Block(g16)
    c: Block(g17)
    c: Block(g18)
    c: Block(g19)
FEATURE [Part::Extrusion] Extrude022
  Base = -> Sketch030
  Dir = (1,-2e-16,2e-16)
  DirMode = 2
  FaceMakerClass = Part::FaceMakerBullseye
  LengthFwd = 19
  LengthRev = 0
  Placement = pos=(-19,0,0) rot=(0,0,1;0rad)
  Solid = true
  Symmetric = false
FEATURE [Part::Fillet] Fillet022
  Base = -> Extrude022
  Edges = 24 edges r=1.49: [Edge6,Edge11,Edge18,Edge23,Edge30,Edge35,Edge42,Edge47,Edge54,Edge59,Edge66,Edge71,Edge78,Edge83,Edge90,Edge95,Edge102,Edge107,Edge114,Edge119,Edge126,Edge131,Edge138,Edge143]
FEATURE [Part::Cut] Cut020  label="top010"
  Base = -> Cut019
  Tool = -> Fillet022
FEATURE [Sketcher::SketchObject] Sketch032
  FullyConstrained = true
  Placement = pos=(117,19,0) rot=(0.57735,0.57735,0.57735;2.0944rad)
  sketch-geometry (48):
    g0: LineSegment StartX=-49.19 StartY=69.25 StartZ=0 EndX=-49.19 EndY=66.25 EndZ=0
    g1: LineSegment StartX=-49.19 StartY=63.5 StartZ=0 EndX=-49.19 EndY=60.5 EndZ=0
    g2: LineSegment StartX=-49.19 StartY=57.75 StartZ=0 EndX=-49.19 EndY=54.75 EndZ=0
    g3: LineSegment StartX=-49.19 StartY=52 StartZ=0 EndX=-49.19 EndY=49 EndZ=0
    g4: LineSegment StartX=-49.19 StartY=46.25 StartZ=0 EndX=-49.19 EndY=43.25 EndZ=0
    g5: LineSegment StartX=-49.19 StartY=40.5 StartZ=0 EndX=-49.19 EndY=37.5 EndZ=0
    g6: LineSegment StartX=-49.19 StartY=34.5 StartZ=0 EndX=-49.19 EndY=31.5 EndZ=0
    g7: LineSegment StartX=-49.19 StartY=28.75 StartZ=0 EndX=-49.19 EndY=25.75 EndZ=0
    g8: LineSegment StartX=-49.19 StartY=23 StartZ=0 EndX=-49.19 EndY=20 EndZ=0
    g9: LineSegment StartX=-49.19 StartY=17.25 StartZ=0 EndX=-49.19 EndY=14.25 EndZ=0
    g10: LineSegment StartX=-49.19 StartY=11.5 StartZ=0 EndX=-49.19 EndY=8.5 EndZ=0
    g11: LineSegment StartX=-49.19 StartY=5.75 StartZ=0 EndX=-49.19 EndY=2.75 EndZ=0
    g12: ArcOfCircle CenterX=-1.5 CenterY=67.75 CenterZ=0 NormalX=0 NormalY=0 NormalZ=1 AngleXU=0 Radius=1.5 StartAngle=4.71239 EndAngle=7.85398
    g13: ArcOfCircle CenterX=-1.5 CenterY=62 CenterZ=0 NormalX=0 NormalY=0 NormalZ=1 AngleXU=0 Radius=1.5 StartAngle=4.71239 EndAngle=7.85398
    g14: ArcOfCircle CenterX=-1.5 CenterY=56.25 CenterZ=0 NormalX=0 NormalY=0 NormalZ=1 AngleXU=0 Radius=1.5 StartAngle=4.71239 EndAngle=7.85398
    g15: ArcOfCircle CenterX=-11.49 CenterY=50.5 CenterZ=0 NormalX=0 NormalY=0 NormalZ=1 AngleXU=0 Radius=1.5 StartAngle=4.71239 EndAngle=7.85398
    g16: ArcOfCircle CenterX=-16.28 CenterY=44.75 CenterZ=0 NormalX=0 NormalY=0 NormalZ=1 AngleXU=0 Radius=1.5 StartAngle=4.71239 EndAngle=7.85398
    g17: ArcOfCircle CenterX=-18.2337 CenterY=39 CenterZ=0 NormalX=0 NormalY=0 NormalZ=1 AngleXU=0 Radius=1.5 StartAngle=4.71485 EndAngle=7.85398
    g18: ArcOfCircle CenterX=-16.2837 CenterY=27.25 CenterZ=0 NormalX=0 NormalY=0 NormalZ=1 AngleXU=0 Radius=1.5 StartAngle=4.71485 EndAngle=7.85398
    g19: ArcOfCircle CenterX=-18.2337 CenterY=33 CenterZ=0 NormalX=0 NormalY=0 NormalZ=1 AngleXU=0 Radius=1.5 StartAngle=4.71485 EndAngle=7.85398
    g20: ArcOfCircle CenterX=-11.49 CenterY=21.5 CenterZ=0 NormalX=0 NormalY=0 NormalZ=1 AngleXU=0 Radius=1.5 StartAngle=4.71239 EndAngle=7.85398
    g21: ArcOfCircle CenterX=-1.5 CenterY=4.25 CenterZ=0 NormalX=0 NormalY=0 NormalZ=1 AngleXU=0 Radius=1.5 StartAngle=4.71239 EndAngle=7.85398
    g22: ArcOfCircle CenterX=-1.5 CenterY=10 CenterZ=0 NormalX=0 NormalY=0 NormalZ=1 AngleXU=0 Radius=1.5 StartAngle=4.71239 EndAngle=7.85398
    g23: ArcOfCircle CenterX=-1.5 CenterY=15.75 CenterZ=0 NormalX=0 NormalY=0 NormalZ=1 AngleXU=0 Radius=1.5 StartAngle=4.71239 EndAngle=7.85398
    g24: LineSegment StartX=-49.19 StartY=69.25 StartZ=0 EndX=-1.5 EndY=69.25 EndZ=0
    g25: LineSegment StartX=-49.19 StartY=66.25 StartZ=0 EndX=-1.5 EndY=66.25 EndZ=0
    g26: LineSegment StartX=-49.19 StartY=63.5 StartZ=0 EndX=-1.5 EndY=63.5 EndZ=0
    g27: LineSegment StartX=-49.19 StartY=60.5 StartZ=0 EndX=-1.5 EndY=60.5 EndZ=0
    g28: LineSegment StartX=-49.19 StartY=57.75 StartZ=0 EndX=-1.5 EndY=57.75 EndZ=0
    g29: LineSegment StartX=-49.19 StartY=54.75 StartZ=0 EndX=-1.5 EndY=54.75 EndZ=0
    g30: LineSegment StartX=-49.19 StartY=52 StartZ=0 EndX=-11.49 EndY=52 EndZ=0
    g31: LineSegment StartX=-49.19 StartY=49 StartZ=0 EndX=-11.49 EndY=49 EndZ=0
    g32: LineSegment StartX=-49.19 StartY=46.25 StartZ=0 EndX=-16.28 EndY=46.25 EndZ=0
    g33: LineSegment StartX=-49.19 StartY=43.25 StartZ=0 EndX=-16.28 EndY=43.25 EndZ=0
    g34: LineSegment StartX=-49.19 StartY=40.5 StartZ=0 EndX=-18.2337 EndY=40.5 EndZ=0
    g35: LineSegment StartX=-49.19 StartY=37.5 StartZ=0 EndX=-18.23 EndY=37.5 EndZ=0
    g36: LineSegment StartX=-49.19 StartY=34.5 StartZ=0 EndX=-18.2337 EndY=34.5 EndZ=0
    g37: LineSegment StartX=-49.19 StartY=31.5 StartZ=0 EndX=-18.23 EndY=31.5 EndZ=0
    g38: LineSegment StartX=-49.19 StartY=28.75 StartZ=0 EndX=-16.2837 EndY=28.75 EndZ=0
    g39: LineSegment StartX=-49.19 StartY=25.75 StartZ=0 EndX=-16.28 EndY=25.75 EndZ=0
    g40: LineSegment StartX=-49.19 StartY=23 StartZ=0 EndX=-11.49 EndY=23 EndZ=0
    g41: LineSegment StartX=-49.19 StartY=20 StartZ=0 EndX=-11.49 EndY=20 EndZ=0
    g42: LineSegment StartX=-49.19 StartY=17.25 StartZ=0 EndX=-1.5 EndY=17.25 EndZ=0
    g43: LineSegment StartX=-49.19 StartY=14.25 StartZ=0 EndX=-1.5 EndY=14.25 EndZ=0
    g44: LineSegment StartX=-49.19 StartY=11.5 StartZ=0 EndX=-1.5 EndY=11.5 EndZ=0
    g45: LineSegment StartX=-49.19 StartY=8.5 StartZ=0 EndX=-1.5 EndY=8.5 EndZ=0
    g46: LineSegment StartX=-49.19 StartY=5.75 StartZ=0 EndX=-1.5 EndY=5.75 EndZ=0
    g47: LineSegment StartX=-49.19 StartY=2.75 StartZ=0 EndX=-1.5 EndY=2.75 EndZ=0
  constraints (120):
    c: Vertical(g0)
    c: Distance(g0) = 3
    c: Block(g0)
    c: Vertical(g1)
    c: Distance(g1) = 3
    c: Vertical(g2)
    c: Equal(g0,g2) = 3
    c: Block(g2)
    c: Vertical(g3)
    c: Equal(g1,g3) = 3
    c: Vertical(g4)
    c: Equal(g0,g4) = 3
    c: Block(g4)
    c: Vertical(g5)
    c: Equal(g1,g5) = 3
    c: Vertical(g6)
    c: Equal(g0,g6) = 3
    c: Block(g6)
    c: Vertical(g7)
    c: Equal(g1,g7) = 3
    c: Vertical(g8)
    c: Equal(g0,g8) = 3
    c: Block(g8)
    c: Vertical(g9)
    c: Equal(g1,g9) = 3
    c: Vertical(g10)
    c: Equal(g0,g10) = 3
    c: Block(g10)
    c: Vertical(g11)
    c: Equal(g1,g11) = 3
    c: Block(g12)
    c: Block(g13)
    c: Block(g14)
    c: Block(g15)
    c: Block(g16)
    c: Block(g17)
    c: Block(g18)
    c: Block(g19)
    c: Block(g20)
    c: Block(g21)
    c: Block(g22)
    c: Block(g23)
    c: Block(g11)
    c: Block(g9)
    c: Block(g7)
    c: Block(g5)
    c: Block(g3)
    c: Block(g1)
    c: Coincident(g24,g0)
    c: Coincident(g24,g12)
    c: Horizontal(g24)
    c: Coincident(g25,g0)
    c: Coincident(g25,g12)
    c: Horizontal(g25)
    c: Coincident(g26,g1)
    c: Coincident(g26,g13)
    c: Horizontal(g26)
    c: Coincident(g27,g1)
    c: Coincident(g27,g13)
    c: Horizontal(g27)
    c: Coincident(g28,g2)
    c: Coincident(g28,g14)
    c: Horizontal(g28)
    c: Coincident(g29,g2)
    c: Coincident(g29,g14)
    c: Horizontal(g29)
    c: Coincident(g30,g3)
    c: Coincident(g30,g15)
    c: Horizontal(g30)
    c: Coincident(g31,g3)
    c: Coincident(g31,g15)
    c: Horizontal(g31)
    c: Coincident(g32,g4)
    c: Coincident(g32,g16)
    c: Horizontal(g32)
    c: Coincident(g33,g4)
    c: Coincident(g33,g16)
    c: Horizontal(g33)
    c: Coincident(g34,g5)
    c: Coincident(g34,g17)
    c: Horizontal(g34)
    c: Coincident(g35,g5)
    c: Coincident(g35,g17)
    c: Horizontal(g35)
    c: Coincident(g36,g6)
    c: Coincident(g36,g19)
    c: Horizontal(g36)
    c: Coincident(g37,g6)
    c: Coincident(g37,g19)
    c: Horizontal(g37)
    c: Coincident(g38,g7)
    c: Coincident(g38,g18)
    c: Horizontal(g38)
    c: Coincident(g39,g7)
    c: Coincident(g39,g18)
    c: Horizontal(g39)
    c: Coincident(g40,g8)
    c: Coincident(g40,g20)
    c: Horizontal(g40)
    c: Coincident(g41,g8)
    c: Coincident(g41,g20)
    c: Horizontal(g41)
    c: Coincident(g42,g9)
    c: Coincident(g42,g23)
    c: Horizontal(g42)
    c: Coincident(g43,g9)
    c: Coincident(g43,g23)
    c: Horizontal(g43)
    c: Coincident(g44,g10)
    c: Coincident(g44,g22)
    c: Horizontal(g44)
    c: Coincident(g45,g10)
    c: Coincident(g45,g22)
    c: Horizontal(g45)
    c: Coincident(g46,g11)
    c: Coincident(g46,g21)
    c: Horizontal(g46)
    c: Coincident(g47,g11)
    c: Coincident(g47,g21)
    c: Horizontal(g47)
FEATURE [Part::Extrusion] Extrude023
  Base = -> Sketch032
  Dir = (1,-2e-16,2e-16)
  DirMode = 2
  FaceMakerClass = Part::FaceMakerBullseye
  LengthFwd = 19
  LengthRev = 0
  Placement = pos=(-19,0,0) rot=(0,0,1;0rad)
  Solid = true
  Symmetric = false
FEATURE [Part::Fillet] Fillet023
  Base = -> Extrude023
  Edges = <same value as first occurrence — deduplicated (x6 in doc)>
  Placement = pos=(0,0.05,0) rot=(0,0,1;0rad)
FEATURE [Part::Cut] Cut014  label="bottom003"
  Base = -> Cut007
  Tool = -> Fusion047
FEATURE [Part::Cut] Cut021  label="bottom004"
  Base = -> Cut014
  Tool = -> Fillet023
FEATURE [Sketcher::SketchObject] Sketch033
  FullyConstrained = true
  Placement = pos=(117,19,0) rot=(0.57735,0.57735,0.57735;2.0944rad)
  sketch-geometry (8):
    g0: LineSegment StartX=-49.19 StartY=69.25 StartZ=0 EndX=-49.19 EndY=66.25 EndZ=0
    g1: LineSegment StartX=-49.19 StartY=5.75 StartZ=0 EndX=-49.19 EndY=2.75 EndZ=0
    g2: ArcOfCircle CenterX=-1.5 CenterY=67.75 CenterZ=0 NormalX=0 NormalY=0 NormalZ=1 AngleXU=0 Radius=1.5 StartAngle=4.71239 EndAngle=7.85398
    g3: ArcOfCircle CenterX=-1.5 CenterY=4.25 CenterZ=0 NormalX=0 NormalY=0 NormalZ=1 AngleXU=0 Radius=1.5 StartAngle=4.71239 EndAngle=7.85398
    g4: LineSegment StartX=-49.19 StartY=69.25 StartZ=0 EndX=-1.5 EndY=69.25 EndZ=0
    g5: LineSegment StartX=-49.19 StartY=66.25 StartZ=0 EndX=-1.5 EndY=66.25 EndZ=0
    g6: LineSegment StartX=-49.19 StartY=5.75 StartZ=0 EndX=-1.5 EndY=5.75 EndZ=0
    g7: LineSegment StartX=-49.19 StartY=2.75 StartZ=0 EndX=-1.5 EndY=2.75 EndZ=0
  constraints (19):
    c: Vertical(g0)
    c: Distance(g0) = 3
    c: Block(g0)
    c: Vertical(g1)
    c: Block(g2)
    c: Block(g3)
    c: Block(g1)
    c: Coincident(g4,g0)
    c: Coincident(g4,g2)
    c: Horizontal(g4)
    c: Coincident(g5,g0)
    c: Coincident(g5,g2)
    c: Horizontal(g5)
    c: Coincident(g6,g1)
    c: Coincident(g6,g3)
    c: Horizontal(g6)
    c: Coincident(g7,g1)
    c: Coincident(g7,g3)
    c: Horizontal(g7)
FEATURE [Sketcher::SketchObject] Sketch034
  FullyConstrained = true
  Placement = pos=(117,19,0) rot=(0.57735,0.57735,0.57735;2.0944rad)
  sketch-geometry (8):
    g0: LineSegment StartX=-49.19 StartY=63.5 StartZ=0 EndX=-49.19 EndY=60.5 EndZ=0
    g1: LineSegment StartX=-49.19 StartY=11.5 StartZ=0 EndX=-49.19 EndY=8.5 EndZ=0
    g2: ArcOfCircle CenterX=-1.5 CenterY=62 CenterZ=0 NormalX=0 NormalY=0 NormalZ=1 AngleXU=0 Radius=1.5 StartAngle=4.71239 EndAngle=7.85398
    g3: ArcOfCircle CenterX=-1.5 CenterY=10 CenterZ=0 NormalX=0 NormalY=0 NormalZ=1 AngleXU=0 Radius=1.5 StartAngle=4.71239 EndAngle=7.85398
    g4: LineSegment StartX=-49.19 StartY=63.5 StartZ=0 EndX=-1.5 EndY=63.5 EndZ=0
    g5: LineSegment StartX=-49.19 StartY=60.5 StartZ=0 EndX=-1.5 EndY=60.5 EndZ=0
    g6: LineSegment StartX=-49.19 StartY=11.5 StartZ=0 EndX=-1.5 EndY=11.5 EndZ=0
    g7: LineSegment StartX=-49.19 StartY=8.5 StartZ=0 EndX=-1.5 EndY=8.5 EndZ=0
  constraints (19):
    c: Vertical(g0)
    c: Distance(g0) = 3
    c: Vertical(g1)
    c: Block(g1)
    c: Block(g2)
    c: Block(g3)
    c: Block(g0)
    c: Coincident(g4,g0)
    c: Coincident(g4,g2)
    c: Horizontal(g4)
    c: Coincident(g5,g0)
    c: Coincident(g5,g2)
    c: Horizontal(g5)
    c: Coincident(g6,g1)
    c: Coincident(g6,g3)
    c: Horizontal(g6)
    c: Coincident(g7,g1)
    c: Coincident(g7,g3)
    c: Horizontal(g7)
FEATURE [Part::Extrusion] Extrude024
  Base = -> Sketch033
  Dir = (1,0,0)
  DirMode = 2
  FaceMakerClass = Part::FaceMakerBullseye
  LengthFwd = 10
  LengthRev = 0
  Solid = true
  Symmetric = false
FEATURE [Part::Extrusion] Extrude025
  Base = -> Sketch034
  Dir = (1,0,0)
  DirMode = 2
  FaceMakerClass = Part::FaceMakerBullseye
  LengthFwd = 10
  LengthRev = 0
  Solid = true
  Symmetric = false
FEATURE [Part::Fillet] Fillet024  label="removeFromtMoreFrontCaseScrewRetainers"
  Base = -> Extrude024
  Edges = 4 edges r=1.49: [Edge6,Edge11,Edge18,Edge23]
  Placement = pos=(-11,0,0) rot=(0,0,1;0rad)
FEATURE [Part::Fillet] Fillet025  label="removeFromtMoreFrontCaseScrewRetainers001"
  Base = -> Extrude025
  Edges = 4 edges r=1.49: [Edge6,Edge11,Edge18,Edge23]
  Placement = pos=(-19,0,0) rot=(0,0,1;0rad)
FEATURE [Part::Cut] Cut022
  Base = -> Cut015
  Tool = -> Fillet025
FEATURE [Part::Cut] Cut023  label="screwRetainers"
  Base = -> Cut022
  Tool = -> Fillet024
FEATURE [Part::MultiFuse] Fusion056  label="bottom005"
  Shapes = -> [Fusion044,Cut021]
FEATURE [Part::MultiFuse] Fusion057  label="casePillars001"
  Shapes = -> [Cut016,Fusion052]
FEATURE [Part::MultiFuse] Fusion058  label="bottom006"
  Shapes = -> [Fusion056,Cut023]
FEATURE [Part::MultiFuse] Fusion059  label="bottom007"
  Shapes = -> [Fusion058,Fillet005]
FEATURE [Part::MultiFuse] Fusion060  label="bottom008"
  Shapes = -> [Fusion059,Fusion]
FEATURE [Part::MultiFuse] Fusion061  label="top011"
  Shapes = -> [Cut006,Cut020]
FEATURE [Part::MultiFuse] Fusion062  label="top012"
  Shapes = -> [Fusion057,Fusion061]
FEATURE [Sketcher::SketchObject] Sketch035  label="topSketch007"
  FullyConstrained = true
  sketch-geometry (6):
    g0: LineSegment StartX=19 StartY=38 StartZ=0 EndX=117 EndY=38 EndZ=0
    g1: ArcOfCircle CenterX=19 CenterY=19 CenterZ=0 NormalX=0 NormalY=0 NormalZ=1 AngleXU=0 Radius=19 StartAngle=1.5708 EndAngle=3.14159
    g2: LineSegment StartX=117 StartY=38 StartZ=0 EndX=117 EndY=19 EndZ=0
    g3: LineSegment StartX=98 StartY=1.0161e-12 StartZ=0 EndX=5.22862e-06 EndY=1.0161e-12 EndZ=0
    g4: LineSegment StartX=5.22862e-06 StartY=19 StartZ=0 EndX=5.22862e-06 EndY=1.0161e-12 EndZ=0
    g5: ArcOfCircle CenterX=98 CenterY=19 CenterZ=0 NormalX=0 NormalY=0 NormalZ=1 AngleXU=0 Radius=19 StartAngle=4.71239 EndAngle=6.28319
  constraints (16):
    c: Horizontal(g0)
    c: Distance(g0) = 98
    c: Coincident(g1,g0)
    c: Block(g1)
    c: Coincident(g2,g0)
    c: Vertical(g2)
    c: Distance(g2) = 19
    c: Horizontal(g3)
    c: Coincident(g4,g1)
    c: Vertical(g4)
    c: Coincident(g3,g4)
    c: Block(g3)
    c: Coincident(g5,g2)
    c: Coincident(g5,g3)
    c: Block(g0)
    c: Block(g5)
FEATURE [Part::Extrusion] Extrude026  label="sideA001"
  Base = -> Sketch035
  Dir = (0,0,1)
  DirMode = 2
  FaceMakerClass = Part::FaceMakerBullseye
  LengthFwd = 3
  LengthRev = 0
  Placement = pos=(0,0,-2.7) rot=(0,0,1;0rad)
  Solid = true
  Symmetric = false
FEATURE [Sketcher::SketchObject] Sketch036  label="topSketch008"
  FullyConstrained = true
  sketch-geometry (6):
    g0: LineSegment StartX=19 StartY=38 StartZ=0 EndX=117 EndY=38 EndZ=0
    g1: ArcOfCircle CenterX=19 CenterY=19 CenterZ=0 NormalX=0 NormalY=0 NormalZ=1 AngleXU=0 Radius=19 StartAngle=1.5708 EndAngle=3.14159
    g2: LineSegment StartX=117 StartY=38 StartZ=0 EndX=117 EndY=19 EndZ=0
    g3: LineSegment StartX=98 StartY=1.0161e-12 StartZ=0 EndX=5.22862e-06 EndY=1.0161e-12 EndZ=0
    g4: LineSegment StartX=5.22862e-06 StartY=19 StartZ=0 EndX=5.22862e-06 EndY=1.0161e-12 EndZ=0
    g5: ArcOfCircle CenterX=98 CenterY=19 CenterZ=0 NormalX=0 NormalY=0 NormalZ=1 AngleXU=0 Radius=19 StartAngle=4.71239 EndAngle=6.28319
  constraints (16):
    c: Horizontal(g0)
    c: Distance(g0) = 98
    c: Coincident(g1,g0)
    c: Block(g1)
    c: Coincident(g2,g0)
    c: Vertical(g2)
    c: Distance(g2) = 19
    c: Horizontal(g3)
    c: Coincident(g4,g1)
    c: Vertical(g4)
    c: Coincident(g3,g4)
    c: Block(g3)
    c: Coincident(g5,g2)
    c: Coincident(g5,g3)
    c: Block(g0)
    c: Block(g5)
FEATURE [Part::Extrusion] Extrude027  label="sideB001"
  Base = -> Sketch036
  Dir = (0,0,1)
  DirMode = 2
  FaceMakerClass = Part::FaceMakerBullseye
  LengthFwd = 3
  LengthRev = 0
  Placement = pos=(0,0,71.7) rot=(0,0,1;0rad)
  Solid = true
  Symmetric = false
FEATURE [Part::MultiFuse] Fusion064  label="removeFromBottom"
  Shapes = -> [Extrude026,Extrude027]
FEATURE [Part::Cut] Cut024  label="bottom009"
  Base = -> Fusion060
  Tool = -> Fusion064
FEATURE [Sketcher::SketchObject] Sketch037  label="topSketch009"
  FullyConstrained = true
  sketch-geometry (8):
    g0: ArcOfCircle CenterX=19 CenterY=19.1201 CenterZ=0 NormalX=0 NormalY=0 NormalZ=1 AngleXU=0 Radius=18.8799 StartAngle=1.5708 EndAngle=3.14793
    g1: LineSegment StartX=0.120501 StartY=19.0004 StartZ=0 EndX=0.120501 EndY=0.000382114 EndZ=0
    g2: LineSegment StartX=19 StartY=38 StartZ=0 EndX=124 EndY=38 EndZ=0
    g3: LineSegment StartX=0.120501 StartY=0.000382114 StartZ=0 EndX=105.121 EndY=0.000382114 EndZ=0
    g4: LineSegment StartX=124 StartY=38 StartZ=0 EndX=125.616 EndY=38 EndZ=0
    g5: LineSegment StartX=105.121 StartY=0.000382114 StartZ=0 EndX=106.736 EndY=0.000382114 EndZ=0
    g6: ArcOfCircle CenterX=106.616 CenterY=19 CenterZ=0 NormalX=0 NormalY=0 NormalZ=1 AngleXU=0 Radius=19 StartAngle=4.71873 EndAngle=6.28319
    g7: LineSegment StartX=125.616 StartY=38 StartZ=0 EndX=125.616 EndY=19 EndZ=0
  constraints (21):
    c: Block(g0)
    c: Coincident(g1,g0)
    c: Vertical(g1)
    c: Horizontal(g2)
    c: Distance(g2) = 105
    c: Coincident(g2,g0)
    c: Distance(g1) = 19
    c: Coincident(g3,g1)
    c: Horizontal(g3)
    c: Distance(g3) = 105
    c: Coincident(g4,g2)
    c: Horizontal(g4)
    c: Distance(g4) = 1.61553
    c: Horizontal(g5)
    c: Equal(g4,g5) = 1.61553
    c: Coincident(g5,g3)
    c: Block(g6)
    c: Coincident(g6,g5)
    c: Coincident(g7,g4)
    c: Coincident(g7,g6)
    c: Vertical(g7)
FEATURE [Part::Extrusion] Extrude028  label="sideB"
  Base = -> Sketch037
  Dir = (0,0,1)
  DirMode = 2
  FaceMakerClass = Part::FaceMakerBullseye
  LengthFwd = 3
  LengthRev = 0
  Placement = pos=(0,0,72) rot=(0,0,1;0rad)
  Solid = true
  Symmetric = false
FEATURE [Sketcher::SketchObject] Sketch038  label="topSketch010"
  FullyConstrained = true
  sketch-geometry (22):
    g0: LineSegment StartX=5.21097e-06 StartY=3 StartZ=0 EndX=5.21097e-06 EndY=19 EndZ=0
    g1: ArcOfCircle CenterX=19 CenterY=19 CenterZ=0 NormalX=0 NormalY=0 NormalZ=1 AngleXU=0 Radius=19 StartAngle=1.5708 EndAngle=3.14159
    g2: ArcOfCircle CenterX=19 CenterY=19 CenterZ=0 NormalX=0 NormalY=0 NormalZ=1 AngleXU=0 Radius=16 StartAngle=1.5708 EndAngle=3.14159
    g3: LineSegment StartX=114 StartY=35 StartZ=0 EndX=19 EndY=35 EndZ=0
    g4: LineSegment StartX=5.21097e-06 StartY=3 StartZ=0 EndX=5.21097e-06 EndY=0 EndZ=0
    g5: LineSegment StartX=3 StartY=0 StartZ=0 EndX=5.21097e-06 EndY=0 EndZ=0
    g6: LineSegment StartX=3 StartY=19 StartZ=0 EndX=3 EndY=0 EndZ=0
    g7: LineSegment StartX=19 StartY=38 StartZ=0 EndX=124 EndY=38 EndZ=0
    g8: Circle CenterX=119 CenterY=35 CenterZ=0 NormalX=0 NormalY=0 NormalZ=1 AngleXU=0 Radius=1
    g9: Circle CenterX=121 CenterY=35 CenterZ=0 NormalX=0 NormalY=0 NormalZ=1 AngleXU=0 Radius=1
    g10: Circle CenterX=121 CenterY=33 CenterZ=0 NormalX=0 NormalY=0 NormalZ=1 AngleXU=0 Radius=1
    g11: BSplineCurve PolesCount=3 KnotsCount=2 Degree=2 IsPeriodic=0
    g12: GeomPoint X=119 Y=35 Z=0
    g13: GeomPoint X=121 Y=33 Z=0
    g14: LineSegment StartX=119 StartY=35 StartZ=0 EndX=114 EndY=35 EndZ=0
    g15: ArcOfCircle CenterX=105 CenterY=19 CenterZ=0 NormalX=0 NormalY=0 NormalZ=1 AngleXU=0 Radius=16 StartAngle=5.60905 EndAngle=6.28319
    g16: LineSegment StartX=121 StartY=33 StartZ=0 EndX=121 EndY=19 EndZ=0
    g17: LineSegment StartX=117.5 StartY=9.01251 StartZ=0 EndX=121.163 EndY=9.0125 EndZ=0
    g18: ArcOfCircle CenterX=105 CenterY=19 CenterZ=0 NormalX=0 NormalY=0 NormalZ=1 AngleXU=0 Radius=20.6155 StartAngle=5.7297 EndAngle=6.28319
    g19: LineSegment StartX=121.163 StartY=9.0125 StartZ=0 EndX=122.538 EndY=8.16329 EndZ=0
    g20: LineSegment StartX=124 StartY=38 StartZ=0 EndX=125.616 EndY=38 EndZ=0
    g21: LineSegment StartX=125.616 StartY=19 StartZ=0 EndX=125.616 EndY=38 EndZ=0
  constraints (49):
    c: Vertical(g0)
    c: Block(g0)
    c: Coincident(g1,g0)
    c: Block(g1)
    c: Coincident(g2,g1)
    c: Block(g2)
    c: Coincident(g3,g2)
    c: Horizontal(g3)
    c: Tangent(g3,g2)
    c: Coincident(g4,g0)
    c: Distance(g4) = 3
    c: Vertical(g4)
    c: Coincident(g5,g4)
    c: Horizontal(g5)
    c: Coincident(g6,g2)
    c: Coincident(g6,g5)
    c: Vertical(g6)
    c: Horizontal(g7)
    c: Distance(g7) = 105
    c: Coincident(g7,g1)
    c: Block(g3)
    c: Weight(g8) = 1
    c: Equal(g8,g9)
    c: Equal(g8,g10)
    c: InternalAlignment(g8,g11)
    c: InternalAlignment(g9,g11)
    c: InternalAlignment(g10,g11)
    c: InternalAlignment(g12,g11)
    c: InternalAlignment(g13,g11)
    c: Block(g11)
    c: Coincident(g14,g11)
    c: Coincident(g14,g3)
    c: Horizontal(g14)
    c: Block(g15)
    c: Coincident(g16,g11)
    c: Coincident(g16,g15)
    c: Vertical(g16)
    c: Distance(g16) = 14
    c: Coincident(g17,g15)
    c: Block(g18)
    c: Coincident(g19,g18)
    c: Coincident(g20,g7)
    c: Horizontal(g20)
    c: Vertical(g21)
    c: Coincident(g20,g21)
    c: Block(g20)
    c: Block(g21)
    c: Block(g19)
    c: Block(g17)
FEATURE [Part::Extrusion] Extrude029
  Base = -> Sketch038
  Dir = (0,0,1)
  DirMode = 2
  FaceMakerClass = Part::FaceMakerBullseye
  LengthFwd = 72
  LengthRev = 0
  Solid = true
  Symmetric = false
FEATURE [Part::Feature] Face085
  shape: bbox 4.8 x 25.5 x 2e-07 mm, 1 faces, 0 solids (baked)
FEATURE [Part::Revolution] Revolve089  label="moreFrontCaseScrewPost003"
  Angle = 360
  Axis = (0,1,0)
  Base = (0,0,0)
  FaceMakerClass = Part::FaceMakerBullseye
  Placement = pos=(109.5,4.5,3.5) rot=(0,0,1;0rad)
  Solid = false
  Source = -> Face085
  Symmetric = false
FEATURE [Part::Feature] Face086
  shape: bbox 4.8 x 25.5 x 2e-07 mm, 1 faces, 0 solids (baked)
FEATURE [Part::Revolution] Revolve090  label="moreFrontCaseScrewPost004"
  Angle = 360
  Axis = (0,1,0)
  Base = (0,0,0)
  FaceMakerClass = Part::FaceMakerBullseye
  Placement = pos=(109.5,4.5,68.5) rot=(0,0,1;0rad)
  Solid = false
  Source = -> Face086
  Symmetric = false
FEATURE [Part::Fillet] Fillet026  label="top013"
  Base = -> Extrude029
  Edges = 1 edges r=2: [Edge35]
FEATURE [Sketcher::SketchObject] Sketch039
  FullyConstrained = true
  sketch-geometry (7):
    g0: LineSegment StartX=0 StartY=0 StartZ=0 EndX=0 EndY=6 EndZ=0
    g1: Circle CenterX=0 CenterY=0 CenterZ=0 NormalX=0 NormalY=0 NormalZ=1 AngleXU=0 Radius=1
    g2: Circle CenterX=8 CenterY=6 CenterZ=0 NormalX=0 NormalY=0 NormalZ=1 AngleXU=0 Radius=1
    g3: BSplineCurve PolesCount=3 KnotsCount=2 Degree=2 IsPeriodic=0
    g4: GeomPoint X=0 Y=0 Z=0
    g5: GeomPoint X=8 Y=6 Z=0
    g6: LineSegment StartX=0 StartY=6 StartZ=0 EndX=8 EndY=6 EndZ=0
  constraints (14):
    c: Coincident(g0,g-1)
    c: Distance(g0) = 6
    c: Vertical(g0)
    c: Coincident(g3,g0)
    c: Weight(g1) = 1
    c: Equal(g1,g2)
    c: InternalAlignment(g1,g3)
    c: InternalAlignment(g2,g3)
    c: InternalAlignment(g4,g3)
    c: InternalAlignment(g5,g3)
    c: Block(g3)
    c: Coincident(g6,g0)
    c: Coincident(g6,g3)
    c: Horizontal(g6)
FEATURE [Sketcher::SketchObject] Sketch040
  FullyConstrained = true
  sketch-geometry (7):
    g0: LineSegment StartX=0 StartY=0 StartZ=0 EndX=0 EndY=6 EndZ=0
    g1: Circle CenterX=0 CenterY=0 CenterZ=0 NormalX=0 NormalY=0 NormalZ=1 AngleXU=0 Radius=1
    g2: Circle CenterX=8 CenterY=6 CenterZ=0 NormalX=0 NormalY=0 NormalZ=1 AngleXU=0 Radius=1
    g3: BSplineCurve PolesCount=3 KnotsCount=2 Degree=2 IsPeriodic=0
    g4: GeomPoint X=0 Y=0 Z=0
    g5: GeomPoint X=8 Y=6 Z=0
    g6: LineSegment StartX=0 StartY=6 StartZ=0 EndX=8 EndY=6 EndZ=0
  constraints (14):
    c: Coincident(g0,g-1)
    c: Distance(g0) = 6
    c: Vertical(g0)
    c: Coincident(g3,g0)
    c: Weight(g1) = 1
    c: Equal(g1,g2)
    c: InternalAlignment(g1,g3)
    c: InternalAlignment(g2,g3)
    c: InternalAlignment(g4,g3)
    c: InternalAlignment(g5,g3)
    c: Block(g3)
    c: Coincident(g6,g0)
    c: Coincident(g6,g3)
    c: Horizontal(g6)
FEATURE [Sketcher::SketchObject] Sketch041
  FullyConstrained = true
  sketch-geometry (7):
    g0: LineSegment StartX=0 StartY=0 StartZ=0 EndX=0 EndY=6 EndZ=0
    g1: Circle CenterX=0 CenterY=0 CenterZ=0 NormalX=0 NormalY=0 NormalZ=1 AngleXU=0 Radius=1
    g2: Circle CenterX=8 CenterY=6 CenterZ=0 NormalX=0 NormalY=0 NormalZ=1 AngleXU=0 Radius=1
    g3: BSplineCurve PolesCount=3 KnotsCount=2 Degree=2 IsPeriodic=0
    g4: GeomPoint X=0 Y=0 Z=0
    g5: GeomPoint X=8 Y=6 Z=0
    g6: LineSegment StartX=0 StartY=6 StartZ=0 EndX=8 EndY=6 EndZ=0
  constraints (14):
    c: Coincident(g0,g-1)
    c: Distance(g0) = 6
    c: Vertical(g0)
    c: Coincident(g3,g0)
    c: Weight(g1) = 1
    c: Equal(g1,g2)
    c: InternalAlignment(g1,g3)
    c: InternalAlignment(g2,g3)
    c: InternalAlignment(g4,g3)
    c: InternalAlignment(g5,g3)
    c: Block(g3)
    c: Coincident(g6,g0)
    c: Coincident(g6,g3)
    c: Horizontal(g6)
FEATURE [Sketcher::SketchObject] Sketch042
  FullyConstrained = true
  sketch-geometry (7):
    g0: LineSegment StartX=0 StartY=0 StartZ=0 EndX=0 EndY=6 EndZ=0
    g1: Circle CenterX=0 CenterY=0 CenterZ=0 NormalX=0 NormalY=0 NormalZ=1 AngleXU=0 Radius=1
    g2: Circle CenterX=8 CenterY=6 CenterZ=0 NormalX=0 NormalY=0 NormalZ=1 AngleXU=0 Radius=1
    g3: BSplineCurve PolesCount=3 KnotsCount=2 Degree=2 IsPeriodic=0
    g4: GeomPoint X=0 Y=0 Z=0
    g5: GeomPoint X=8 Y=6 Z=0
    g6: LineSegment StartX=0 StartY=6 StartZ=0 EndX=8 EndY=6 EndZ=0
  constraints (14):
    c: Coincident(g0,g-1)
    c: Distance(g0) = 6
    c: Vertical(g0)
    c: Coincident(g3,g0)
    c: Weight(g1) = 1
    c: Equal(g1,g2)
    c: InternalAlignment(g1,g3)
    c: InternalAlignment(g2,g3)
    c: InternalAlignment(g4,g3)
    c: InternalAlignment(g5,g3)
    c: Block(g3)
    c: Coincident(g6,g0)
    c: Coincident(g6,g3)
    c: Horizontal(g6)
FEATURE [Part::Extrusion] Extrude030  label="caseScrewPillarBracket008"
  Base = -> Sketch039
  Dir = (0,0,1)
  DirMode = 2
  FaceMakerClass = Part::FaceMakerBullseye
  LengthFwd = 2.4
  LengthRev = 0
  Placement = pos=(15.76,29,8.8) rot=(0,1,0;0rad)
  Solid = true
  Symmetric = false
FEATURE [Part::Extrusion] Extrude031  label="caseScrewPillarBracket009"
  Base = -> Sketch040
  Dir = (0,0,1)
  DirMode = 2
  FaceMakerClass = Part::FaceMakerBullseye
  LengthFwd = 2.4
  LengthRev = 0
  Placement = pos=(15.76,29,60.8) rot=(0,0,1;0rad)
  Solid = true
  Symmetric = false
FEATURE [Part::Extrusion] Extrude032  label="caseScrewPillarBracket010"
  Base = -> Sketch041
  Dir = (0,0,1)
  DirMode = 2
  FaceMakerClass = Part::FaceMakerBullseye
  LengthFwd = 2.4
  LengthRev = 0
  Placement = pos=(13.7,29,13.26) rot=(0,-1,0;1.5708rad)
  Solid = true
  Symmetric = false
FEATURE [Part::Extrusion] Extrude033  label="caseScrewPillarBracket011"
  Base = -> Sketch042
  Dir = (0,0,1)
  DirMode = 2
  FaceMakerClass = Part::FaceMakerBullseye
  LengthFwd = 2.4
  LengthRev = 0
  Placement = pos=(11.3,29,58.74) rot=(0,1,0;1.5708rad)
  Solid = true
  Symmetric = false
FEATURE [Sketcher::SketchObject] Sketch043
  FullyConstrained = true
  sketch-geometry (7):
    g0: LineSegment StartX=0 StartY=0 StartZ=0 EndX=0 EndY=6 EndZ=0
    g1: Circle CenterX=0 CenterY=0 CenterZ=0 NormalX=0 NormalY=0 NormalZ=1 AngleXU=0 Radius=1
    g2: Circle CenterX=8 CenterY=6 CenterZ=0 NormalX=0 NormalY=0 NormalZ=1 AngleXU=0 Radius=1
    g3: BSplineCurve PolesCount=3 KnotsCount=2 Degree=2 IsPeriodic=0
    g4: GeomPoint X=0 Y=0 Z=0
    g5: GeomPoint X=8 Y=6 Z=0
    g6: LineSegment StartX=0 StartY=6 StartZ=0 EndX=8 EndY=6 EndZ=0
  constraints (14):
    c: Coincident(g0,g-1)
    c: Distance(g0) = 6
    c: Vertical(g0)
    c: Coincident(g3,g0)
    c: Weight(g1) = 1
    c: Equal(g1,g2)
    c: InternalAlignment(g1,g3)
    c: InternalAlignment(g2,g3)
    c: InternalAlignment(g4,g3)
    c: InternalAlignment(g5,g3)
    c: Block(g3)
    c: Coincident(g6,g0)
    c: Coincident(g6,g3)
    c: Horizontal(g6)
FEATURE [Part::Extrusion] Extrude034  label="caseScrewPillarBracket012"
  Base = -> Sketch043
  Dir = (0,0,1)
  DirMode = 2
  FaceMakerClass = Part::FaceMakerBullseye
  LengthFwd = 2.4
  LengthRev = 0
  Placement = pos=(88.3,29,65.23) rot=(0,1,0;1.5708rad)
  Solid = true
  Symmetric = false
FEATURE [Sketcher::SketchObject] Sketch044
  FullyConstrained = true
  sketch-geometry (7):
    g0: LineSegment StartX=0 StartY=0 StartZ=0 EndX=0 EndY=6 EndZ=0
    g1: Circle CenterX=0 CenterY=0 CenterZ=0 NormalX=0 NormalY=0 NormalZ=1 AngleXU=0 Radius=1
    g2: Circle CenterX=8 CenterY=6 CenterZ=0 NormalX=0 NormalY=0 NormalZ=1 AngleXU=0 Radius=1
    g3: BSplineCurve PolesCount=3 KnotsCount=2 Degree=2 IsPeriodic=0
    g4: GeomPoint X=0 Y=0 Z=0
    g5: GeomPoint X=8 Y=6 Z=0
    g6: LineSegment StartX=0 StartY=6 StartZ=0 EndX=8 EndY=6 EndZ=0
  constraints (14):
    c: Coincident(g0,g-1)
    c: Distance(g0) = 6
    c: Vertical(g0)
    c: Coincident(g3,g0)
    c: Weight(g1) = 1
    c: Equal(g1,g2)
    c: InternalAlignment(g1,g3)
    c: InternalAlignment(g2,g3)
    c: InternalAlignment(g4,g3)
    c: InternalAlignment(g5,g3)
    c: Block(g3)
    c: Coincident(g6,g0)
    c: Coincident(g6,g3)
    c: Horizontal(g6)
FEATURE [Part::Extrusion] Extrude035  label="caseScrewPillarBracket013"
  Base = -> Sketch044
  Dir = (0,0,1)
  DirMode = 2
  FaceMakerClass = Part::FaceMakerBullseye
  LengthFwd = 2.4
  LengthRev = 0
  Placement = pos=(90.7,29,6.77) rot=(0,-1,0;1.5708rad)
  Solid = true
  Symmetric = false
FEATURE [Sketcher::SketchObject] Sketch045
  FullyConstrained = true
  sketch-geometry (7):
    g0: LineSegment StartX=0 StartY=0 StartZ=0 EndX=0 EndY=6 EndZ=0
    g1: Circle CenterX=0 CenterY=0 CenterZ=0 NormalX=0 NormalY=0 NormalZ=1 AngleXU=0 Radius=1
    g2: Circle CenterX=8 CenterY=6 CenterZ=0 NormalX=0 NormalY=0 NormalZ=1 AngleXU=0 Radius=1
    g3: BSplineCurve PolesCount=3 KnotsCount=2 Degree=2 IsPeriodic=0
    g4: GeomPoint X=0 Y=0 Z=0
    g5: GeomPoint X=8 Y=6 Z=0
    g6: LineSegment StartX=0 StartY=6 StartZ=0 EndX=8 EndY=6 EndZ=0
  constraints (14):
    c: Coincident(g0,g-1)
    c: Distance(g0) = 6
    c: Vertical(g0)
    c: Coincident(g3,g0)
    c: Weight(g1) = 1
    c: Equal(g1,g2)
    c: InternalAlignment(g1,g3)
    c: InternalAlignment(g2,g3)
    c: InternalAlignment(g4,g3)
    c: InternalAlignment(g5,g3)
    c: Block(g3)
    c: Coincident(g6,g0)
    c: Coincident(g6,g3)
    c: Horizontal(g6)
FEATURE [Sketcher::SketchObject] Sketch046
  FullyConstrained = true
  sketch-geometry (7):
    g0: LineSegment StartX=0 StartY=0 StartZ=0 EndX=0 EndY=6 EndZ=0
    g1: Circle CenterX=0 CenterY=0 CenterZ=0 NormalX=0 NormalY=0 NormalZ=1 AngleXU=0 Radius=1
    g2: Circle CenterX=8 CenterY=6 CenterZ=0 NormalX=0 NormalY=0 NormalZ=1 AngleXU=0 Radius=1
    g3: BSplineCurve PolesCount=3 KnotsCount=2 Degree=2 IsPeriodic=0
    g4: GeomPoint X=0 Y=0 Z=0
    g5: GeomPoint X=8 Y=6 Z=0
    g6: LineSegment StartX=0 StartY=6 StartZ=0 EndX=8 EndY=6 EndZ=0
  constraints (14):
    c: Coincident(g0,g-1)
    c: Distance(g0) = 6
    c: Vertical(g0)
    c: Coincident(g3,g0)
    c: Weight(g1) = 1
    c: Equal(g1,g2)
    c: InternalAlignment(g1,g3)
    c: InternalAlignment(g2,g3)
    c: InternalAlignment(g4,g3)
    c: InternalAlignment(g5,g3)
    c: Block(g3)
    c: Coincident(g6,g0)
    c: Coincident(g6,g3)
    c: Horizontal(g6)
FEATURE [Part::Extrusion] Extrude036  label="caseScrewPillarBracket014"
  Base = -> Sketch045
  Dir = (0,0,1)
  DirMode = 2
  FaceMakerClass = Part::FaceMakerBullseye
  LengthFwd = 2.4
  LengthRev = 0
  Placement = pos=(110.7,29,6.77) rot=(0,-1,0;1.5708rad)
  Solid = true
  Symmetric = false
FEATURE [Part::Extrusion] Extrude037  label="caseScrewPillarBracket015"
  Base = -> Sketch046
  Dir = (0,0,1)
  DirMode = 2
  FaceMakerClass = Part::FaceMakerBullseye
  LengthFwd = 2.4
  LengthRev = 0
  Placement = pos=(108.3,29,65.23) rot=(0,1,0;1.5708rad)
  Solid = true
  Symmetric = false
FEATURE [Part::Box] Box013  label="frontCaseScrewPillarBracket002"
  AttacherType = Attacher::AttachEngine3D
  Height = 2.4
  Length = 22
  Placement = pos=(87,28,2.3) rot=(0,0,1;0rad)
  Width = 7
FEATURE [Part::Box] Box014  label="frontCaseScrewPillarBracket003"
  AttacherType = Attacher::AttachEngine3D
  Height = 2.4
  Length = 22
  Placement = pos=(87,28,67.3) rot=(0,0,1;0rad)
  Width = 7
FEATURE [Part::Feature] Face087
  shape: bbox 4.8 x 30.2 x 2e-07 mm, 1 faces, 0 solids (baked)
FEATURE [Part::Revolution] Revolve091  label="frontCaseScrewPost004"
  Angle = 360
  Axis = (0,1,0)
  Base = (0,0,0)
  FaceMakerClass = Part::FaceMakerBullseye
  Placement = pos=(89.5,4.5,3.5) rot=(0,0,1;0rad)
  Solid = false
  Source = -> Face087
  Symmetric = false
FEATURE [Part::Feature] Face088
  shape: bbox 4.8 x 30.2 x 2e-07 mm, 1 faces, 0 solids (baked)
FEATURE [Part::Revolution] Revolve092  label="frontCaseScrewPost005"
  Angle = 360
  Axis = (0,1,0)
  Base = (0,0,0)
  FaceMakerClass = Part::FaceMakerBullseye
  Placement = pos=(89.5,4.5,68.5) rot=(0,0,1;0rad)
  Solid = false
  Source = -> Face088
  Symmetric = false
FEATURE [Part::Feature] Face089
  shape: bbox 3.5 x 30.2 x 2e-07 mm, 1 faces, 0 solids (baked)
FEATURE [Part::Revolution] Revolve093  label="backCaseScrewPost002"
  Angle = 360
  Axis = (0,1,0)
  Base = (0,0,0)
  FaceMakerClass = Part::FaceMakerBullseye
  Placement = pos=(12.5,4.5,10) rot=(0,0,1;0rad)
  Solid = false
  Source = -> Face089
  Symmetric = false
FEATURE [Part::Feature] Face090
  shape: bbox 3.5 x 30.2 x 2e-07 mm, 1 faces, 0 solids (baked)
FEATURE [Part::Revolution] Revolve094  label="backCaseScrewPost003"
  Angle = 360
  Axis = (0,1,0)
  Base = (0,0,0)
  FaceMakerClass = Part::FaceMakerBullseye
  Placement = pos=(12.5,4.5,62) rot=(0,0,1;0rad)
  Solid = false
  Source = -> Face090
  Symmetric = false
FEATURE [Part::Box] Box015  label="Cube011"
  AttacherType = Attacher::AttachEngine3D
  Height = 28.8
  Length = 3
  Placement = pos=(107.3,28,21.6) rot=(0,0,1;0rad)
  Width = 7
FEATURE [Part::Box] Box016  label="Cube012"
  AttacherType = Attacher::AttachEngine3D
  Height = 3
  Length = 7.4
  Placement = pos=(107.3,28,18.6) rot=(0,0,1;0rad)
  Width = 7
FEATURE [Part::Box] Box017  label="Cube013"
  AttacherType = Attacher::AttachEngine3D
  Height = 3
  Length = 7.4
  Placement = pos=(107.3,28,50.4) rot=(0,0,1;0rad)
  Width = 7
FEATURE [Part::Cylinder] Cylinder024
  Angle = 360
  AttacherType = Attacher::AttachEngine3D
  Height = 20
  Placement = pos=(0,0,36.15) rot=(0,0,1;0rad)
  Radius = 14.3
FEATURE [Part::Cylinder] Cylinder025
  Angle = 360
  AttacherType = Attacher::AttachEngine3D
  Height = 10
  Placement = pos=(0,0,36.15) rot=(0,0,1;0rad)
  Radius = 4
FEATURE [Part::MultiFuse] Fusion066  label="removeToCreteHoleForPlugHousing009"
  Placement = pos=(70,19,36) rot=(0,1,0;1.5708rad)
  Shapes = -> [Cylinder024,Cylinder025]
FEATURE [Part::MultiFuse] Fusion065  label="plugHousingBracketHolder002"
  Shapes = -> [Box017,Box015,Box016]
FEATURE [Part::Cut] Cut025  label="plugHousingBracketHolder003"
  Base = -> Fusion065
  Placement = pos=(7,0,0) rot=(0,0,1;0rad)
  Tool = -> Fusion066
FEATURE [Sketcher::SketchObject] Sketch047
  FullyConstrained = false
  Placement = pos=(0,0,0) rot=(1,0,0;1.5708rad)
  sketch-geometry (24):
    g0: ArcOfCircle CenterX=-4 CenterY=-10.5 CenterZ=0 NormalX=0 NormalY=0 NormalZ=1 AngleXU=0 Radius=1.5 StartAngle=6e-16 EndAngle=3.14159
    g1: ArcOfCircle CenterX=-34.2 CenterY=-10.5 CenterZ=0 NormalX=0 NormalY=0 NormalZ=1 AngleXU=0 Radius=1.5 StartAngle=0 EndAngle=3.14159
    g2: ArcOfCircle CenterX=-34.2 CenterY=-27.7 CenterZ=0 NormalX=0 NormalY=0 NormalZ=1 AngleXU=0 Radius=1.5 StartAngle=3.14159 EndAngle=6.28319
    g3: ArcOfCircle CenterX=-4 CenterY=-27.7 CenterZ=0 NormalX=0 NormalY=0 NormalZ=1 AngleXU=0 Radius=1.5 StartAngle=3.1416 EndAngle=6.28319
    g4: ArcOfCircle CenterX=-10 CenterY=-4.3 CenterZ=0 NormalX=0 NormalY=0 NormalZ=1 AngleXU=0 Radius=1.5 StartAngle=2e-16 EndAngle=3.14159
    g5: ArcOfCircle CenterX=-16.1 CenterY=-1.8 CenterZ=0 NormalX=0 NormalY=0 NormalZ=1 AngleXU=0 Radius=1.5 StartAngle=5e-16 EndAngle=3.14159
    g6: ArcOfCircle CenterX=-22.1 CenterY=-1.8 CenterZ=0 NormalX=0 NormalY=0 NormalZ=1 AngleXU=0 Radius=1.5 StartAngle=5e-16 EndAngle=3.14159
    g7: ArcOfCircle CenterX=-28.2 CenterY=-4.3 CenterZ=0 NormalX=0 NormalY=0 NormalZ=1 AngleXU=0 Radius=1.5 StartAngle=2e-16 EndAngle=3.14159
    g8: ArcOfCircle CenterX=-10 CenterY=-33.9 CenterZ=0 NormalX=0 NormalY=0 NormalZ=1 AngleXU=0 Radius=1.5 StartAngle=3.14159 EndAngle=6.28319
    g9: ArcOfCircle CenterX=-16.1 CenterY=-36.4 CenterZ=0 NormalX=0 NormalY=0 NormalZ=1 AngleXU=0 Radius=1.5 StartAngle=3.14159 EndAngle=6.28319
    g10: ArcOfCircle CenterX=-22.1 CenterY=-36.4 CenterZ=0 NormalX=0 NormalY=0 NormalZ=1 AngleXU=0 Radius=1.5 StartAngle=3.14159 EndAngle=6.28319
    g11: ArcOfCircle CenterX=-28.2 CenterY=-33.9 CenterZ=0 NormalX=0 NormalY=0 NormalZ=1 AngleXU=0 Radius=1.5 StartAngle=3.14159 EndAngle=6.28319
    g12: LineSegment StartX=-35.7 StartY=-10.5 StartZ=0 EndX=-35.7 EndY=-27.7 EndZ=0
    g13: LineSegment StartX=-32.7 StartY=-10.5 StartZ=0 EndX=-32.7 EndY=-27.7 EndZ=0
    g14: LineSegment StartX=-29.7 StartY=-33.9 StartZ=0 EndX=-29.7 EndY=-4.3 EndZ=0
    g15: LineSegment StartX=-26.7 StartY=-33.9 StartZ=0 EndX=-26.7 EndY=-4.3 EndZ=0
    g16: LineSegment StartX=-2.5 StartY=-10.5 StartZ=0 EndX=-2.5 EndY=-27.7 EndZ=0
    g17: LineSegment StartX=-8.5 StartY=-4.3 StartZ=0 EndX=-8.5 EndY=-33.9 EndZ=0
    g18: LineSegment StartX=-5.5 StartY=-10.5 StartZ=0 EndX=-5.5 EndY=-27.7 EndZ=0
    g19: LineSegment StartX=-11.5 StartY=-4.3 StartZ=0 EndX=-11.5 EndY=-33.9 EndZ=0
    g20: LineSegment StartX=-14.6 StartY=-1.8 StartZ=0 EndX=-14.6 EndY=-36.4 EndZ=0
    g21: LineSegment StartX=-17.6 StartY=-1.8 StartZ=0 EndX=-17.6 EndY=-36.4 EndZ=0
    g22: LineSegment StartX=-20.6 StartY=-36.4 StartZ=0 EndX=-20.6 EndY=-1.8 EndZ=0
    g23: LineSegment StartX=-23.6 StartY=-1.8 StartZ=0 EndX=-23.6 EndY=-36.4 EndZ=0
  constraints (48):
    c: Block(g0)
    c: Block(g1)
    c: Block(g2)
    c: Block(g3)
    c: Block(g4)
    c: Block(g5)
    c: Block(g6)
    c: Block(g7)
    c: Block(g8)
    c: Block(g9)
    c: Block(g10)
    c: Block(g11)
    c: Coincident(g12,g1)
    c: Coincident(g12,g2)
    c: Vertical(g12)
    c: Coincident(g13,g1)
    c: Coincident(g13,g2)
    c: Vertical(g13)
    c: Coincident(g14,g11)
    c: Coincident(g14,g7)
    c: Vertical(g14)
    c: Coincident(g15,g11)
    c: Coincident(g15,g7)
    c: Vertical(g15)
    c: Coincident(g16,g0)
    c: Coincident(g16,g3)
    c: Vertical(g16)
    c: Coincident(g17,g4)
    c: Coincident(g17,g8)
    c: Vertical(g17)
    c: Coincident(g18,g0)
    c: Coincident(g18,g3)
    c: Vertical(g18)
    c: Coincident(g19,g4)
    c: Coincident(g19,g8)
    c: Vertical(g19)
    c: Coincident(g20,g5)
    c: Coincident(g20,g9)
    c: Vertical(g20)
    c: Coincident(g21,g5)
    c: Coincident(g21,g9)
    c: Vertical(g21)
    c: Coincident(g22,g10)
    c: Coincident(g22,g6)
    c: Vertical(g22)
    c: Coincident(g23,g6)
    c: Coincident(g23,g10)
    c: Vertical(g23)
FEATURE [Part::Extrusion] Extrude038  label="removeToCreateFanGrillHoles001"
  Base = -> Sketch047
  Dir = (0,-1,6e-16)
  DirMode = 2
  FaceMakerClass = Part::FaceMakerBullseye
  LengthFwd = 10
  LengthRev = 0
  Placement = pos=(65.4,44,54.82) rot=(0,0,1;0rad)
  Solid = true
  Symmetric = false
FEATURE [Part::Feature] Wire004
  shape: bbox 11 x 5.2 x 2e-07 mm, 0 faces, 0 solids (baked)
FEATURE [Part::Revolution] Revolve095
  Angle = 360
  Axis = (0,1,0)
  Base = (0,0,0)
  FaceMakerClass = Part::FaceMakerBullseye
  Placement = pos=(30.3,38,19.7) rot=(0,0,1;0rad)
  Solid = true
  Source = -> Wire004
  Symmetric = false
FEATURE [Part::Feature] Wire005
  shape: bbox 11 x 5.2 x 2e-07 mm, 0 faces, 0 solids (baked)
FEATURE [Part::Revolution] Revolve096
  Angle = 360
  Axis = (0,1,0)
  Base = (0,0,0)
  FaceMakerClass = Part::FaceMakerBullseye
  Placement = pos=(30.3,38,51.7) rot=(0,0,1;0rad)
  Solid = true
  Source = -> Wire005
  Symmetric = false
FEATURE [Part::Feature] Wire006
  shape: bbox 11 x 5.2 x 2e-07 mm, 0 faces, 0 solids (baked)
FEATURE [Part::Revolution] Revolve097
  Angle = 360
  Axis = (0,1,0)
  Base = (0,0,0)
  FaceMakerClass = Part::FaceMakerBullseye
  Placement = pos=(62.3,38,51.7) rot=(0,0,1;0rad)
  Solid = true
  Source = -> Wire006
  Symmetric = false
FEATURE [Part::Feature] Wire007
  shape: bbox 11 x 5.2 x 2e-07 mm, 0 faces, 0 solids (baked)
FEATURE [Part::Revolution] Revolve098
  Angle = 360
  Axis = (0,1,0)
  Base = (0,0,0)
  FaceMakerClass = Part::FaceMakerBullseye
  Placement = pos=(62.3,38,19.7) rot=(0,0,1;0rad)
  Solid = true
  Source = -> Wire007
  Symmetric = false
FEATURE [Part::MultiFuse] Fusion067  label="fanScrewHousing002"
  Shapes = -> [Revolve098,Revolve097,Revolve096,Revolve095]
FEATURE [Part::Feature] Face091 .. Face094  x4 (patterned run collapsed; names and placements below)
  shape: bbox 3.5 x 17.8 x 2e-07 mm, 1 faces, 0 solids (baked)
FEATURE [Part::Revolution] Revolve099  label="removeToCreateScrewAndThreadedInsertHole026"
  Angle = 360
  Axis = (0,1,0)
  Base = (0,0,0)
  FaceMakerClass = Part::FaceMakerBullseye
  Placement = pos=(62.3,30.3,19.7) rot=(0,0,1;0rad)
  Solid = false
  Source = -> Face091
  Symmetric = false
FEATURE [Part::Revolution] Revolve100  label="removeToCreateScrewAndThreadedInsertHole027"
  Angle = 360
  Axis = (0,1,0)
  Base = (0,0,0)
  FaceMakerClass = Part::FaceMakerBullseye
  Placement = pos=(62.3,30.3,51.7) rot=(0,0,1;0rad)
  Solid = false
  Source = -> Face092
  Symmetric = false
FEATURE [Part::Revolution] Revolve101  label="removeToCreateScrewAndThreadedInsertHole028"
  Angle = 360
  Axis = (0,1,0)
  Base = (0,0,0)
  FaceMakerClass = Part::FaceMakerBullseye
  Placement = pos=(30.3,30.3,19.7) rot=(0,0,1;0rad)
  Solid = false
  Source = -> Face093
  Symmetric = false
FEATURE [Part::Revolution] Revolve102  label="removeToCreateScrewAndThreadedInsertHole029"
  Angle = 360
  Axis = (0,1,0)
  Base = (0,0,0)
  FaceMakerClass = Part::FaceMakerBullseye
  Placement = pos=(30.3,30.3,51.7) rot=(0,0,1;0rad)
  Solid = false
  Source = -> Face094
  Symmetric = false
FEATURE [Part::MultiFuse] Fusion068  label="createThreadedInsertHolesForFan002"
  Shapes = -> [Revolve099,Revolve100,Revolve101,Revolve102]
FEATURE [Part::Cut] Cut026  label="fanScrewHousing003"
  Base = -> Fusion067
  Tool = -> Fusion068
FEATURE [Sketcher::SketchObject] Sketch048
  FullyConstrained = false
  Placement = pos=(0,0,0) rot=(1,0,0;1.5708rad)
  sketch-geometry (24):
    g0: ArcOfCircle CenterX=-4 CenterY=-10.5 CenterZ=0 NormalX=0 NormalY=0 NormalZ=1 AngleXU=0 Radius=1.5 StartAngle=6e-16 EndAngle=3.14159
    g1: ArcOfCircle CenterX=-34.2 CenterY=-10.5 CenterZ=0 NormalX=0 NormalY=0 NormalZ=1 AngleXU=0 Radius=1.5 StartAngle=0 EndAngle=3.14159
    g2: ArcOfCircle CenterX=-34.2 CenterY=-27.7 CenterZ=0 NormalX=0 NormalY=0 NormalZ=1 AngleXU=0 Radius=1.5 StartAngle=3.14159 EndAngle=6.28319
    g3: ArcOfCircle CenterX=-4 CenterY=-27.7 CenterZ=0 NormalX=0 NormalY=0 NormalZ=1 AngleXU=0 Radius=1.5 StartAngle=3.1416 EndAngle=6.28319
    g4: ArcOfCircle CenterX=-10 CenterY=-4.3 CenterZ=0 NormalX=0 NormalY=0 NormalZ=1 AngleXU=0 Radius=1.5 StartAngle=2e-16 EndAngle=3.14159
    g5: ArcOfCircle CenterX=-16.1 CenterY=-1.8 CenterZ=0 NormalX=0 NormalY=0 NormalZ=1 AngleXU=0 Radius=1.5 StartAngle=5e-16 EndAngle=3.14159
    g6: ArcOfCircle CenterX=-22.1 CenterY=-1.8 CenterZ=0 NormalX=0 NormalY=0 NormalZ=1 AngleXU=0 Radius=1.5 StartAngle=5e-16 EndAngle=3.14159
    g7: ArcOfCircle CenterX=-28.2 CenterY=-4.3 CenterZ=0 NormalX=0 NormalY=0 NormalZ=1 AngleXU=0 Radius=1.5 StartAngle=2e-16 EndAngle=3.14159
    g8: ArcOfCircle CenterX=-10 CenterY=-33.9 CenterZ=0 NormalX=0 NormalY=0 NormalZ=1 AngleXU=0 Radius=1.5 StartAngle=3.14159 EndAngle=6.28319
    g9: ArcOfCircle CenterX=-16.1 CenterY=-36.4 CenterZ=0 NormalX=0 NormalY=0 NormalZ=1 AngleXU=0 Radius=1.5 StartAngle=3.14159 EndAngle=6.28319
    g10: ArcOfCircle CenterX=-22.1 CenterY=-36.4 CenterZ=0 NormalX=0 NormalY=0 NormalZ=1 AngleXU=0 Radius=1.5 StartAngle=3.14159 EndAngle=6.28319
    g11: ArcOfCircle CenterX=-28.2 CenterY=-33.9 CenterZ=0 NormalX=0 NormalY=0 NormalZ=1 AngleXU=0 Radius=1.5 StartAngle=3.14159 EndAngle=6.28319
    g12: LineSegment StartX=-35.7 StartY=-10.5 StartZ=0 EndX=-35.7 EndY=-27.7 EndZ=0
    g13: LineSegment StartX=-32.7 StartY=-10.5 StartZ=0 EndX=-32.7 EndY=-27.7 EndZ=0
    g14: LineSegment StartX=-29.7 StartY=-33.9 StartZ=0 EndX=-29.7 EndY=-4.3 EndZ=0
    g15: LineSegment StartX=-26.7 StartY=-33.9 StartZ=0 EndX=-26.7 EndY=-4.3 EndZ=0
    g16: LineSegment StartX=-2.5 StartY=-10.5 StartZ=0 EndX=-2.5 EndY=-27.7 EndZ=0
    g17: LineSegment StartX=-8.5 StartY=-4.3 StartZ=0 EndX=-8.5 EndY=-33.9 EndZ=0
    g18: LineSegment StartX=-5.5 StartY=-10.5 StartZ=0 EndX=-5.5 EndY=-27.7 EndZ=0
    g19: LineSegment StartX=-11.5 StartY=-4.3 StartZ=0 EndX=-11.5 EndY=-33.9 EndZ=0
    g20: LineSegment StartX=-14.6 StartY=-1.8 StartZ=0 EndX=-14.6 EndY=-36.4 EndZ=0
    g21: LineSegment StartX=-17.6 StartY=-1.8 StartZ=0 EndX=-17.6 EndY=-36.4 EndZ=0
    g22: LineSegment StartX=-20.6 StartY=-36.4 StartZ=0 EndX=-20.6 EndY=-1.8 EndZ=0
    g23: LineSegment StartX=-23.6 StartY=-1.8 StartZ=0 EndX=-23.6 EndY=-36.4 EndZ=0
  constraints (48):
    c: Block(g0)
    c: Block(g1)
    c: Block(g2)
    c: Block(g3)
    c: Block(g4)
    c: Block(g5)
    c: Block(g6)
    c: Block(g7)
    c: Block(g8)
    c: Block(g9)
    c: Block(g10)
    c: Block(g11)
    c: Coincident(g12,g1)
    c: Coincident(g12,g2)
    c: Vertical(g12)
    c: Coincident(g13,g1)
    c: Coincident(g13,g2)
    c: Vertical(g13)
    c: Coincident(g14,g11)
    c: Coincident(g14,g7)
    c: Vertical(g14)
    c: Coincident(g15,g11)
    c: Coincident(g15,g7)
    c: Vertical(g15)
    c: Coincident(g16,g0)
    c: Coincident(g16,g3)
    c: Vertical(g16)
    c: Coincident(g17,g4)
    c: Coincident(g17,g8)
    c: Vertical(g17)
    c: Coincident(g18,g0)
    c: Coincident(g18,g3)
    c: Vertical(g18)
    c: Coincident(g19,g4)
    c: Coincident(g19,g8)
    c: Vertical(g19)
    c: Coincident(g20,g5)
    c: Coincident(g20,g9)
    c: Vertical(g20)
    c: Coincident(g21,g5)
    c: Coincident(g21,g9)
    c: Vertical(g21)
    c: Coincident(g22,g10)
    c: Coincident(g22,g6)
    c: Vertical(g22)
    c: Coincident(g23,g6)
    c: Coincident(g23,g10)
    c: Vertical(g23)
FEATURE [Part::Extrusion] Extrude039  label="removeToCreateFanGrillHoles002"
  Base = -> Sketch048
  Dir = (0,-1,6e-16)
  DirMode = 2
  FaceMakerClass = Part::FaceMakerBullseye
  LengthFwd = 10
  LengthRev = 0
  Placement = pos=(65.4,44,54.82) rot=(0,0,1;0rad)
  Solid = true
  Symmetric = false
FEATURE [Part::Cut] Cut027  label="fanScrewHousing004"
  Base = -> Cut026
  Tool = -> Extrude038
FEATURE [Part::Cut] Cut028  label="top014"
  Base = -> Fillet026
  Tool = -> Extrude039
FEATURE [Part::Feature] Face095 .. Face098  x4 (patterned run collapsed; names and placements below)
  shape: bbox 3.5 x 17.8 x 2e-07 mm, 1 faces, 0 solids (baked)
FEATURE [Part::Revolution] Revolve103  label="removeToCreateScrewAndThreadedInsertHole030"
  Angle = 360
  Axis = (0,1,0)
  Base = (0,0,0)
  FaceMakerClass = Part::FaceMakerBullseye
  Placement = pos=(62.3,30.3,19.7) rot=(0,0,1;0rad)
  Solid = false
  Source = -> Face095
  Symmetric = false
FEATURE [Part::Revolution] Revolve104  label="removeToCreateScrewAndThreadedInsertHole031"
  Angle = 360
  Axis = (0,1,0)
  Base = (0,0,0)
  FaceMakerClass = Part::FaceMakerBullseye
  Placement = pos=(62.3,30.3,51.7) rot=(0,0,1;0rad)
  Solid = false
  Source = -> Face096
  Symmetric = false
FEATURE [Part::Revolution] Revolve105  label="removeToCreateScrewAndThreadedInsertHole032"
  Angle = 360
  Axis = (0,1,0)
  Base = (0,0,0)
  FaceMakerClass = Part::FaceMakerBullseye
  Placement = pos=(30.3,30.3,19.7) rot=(0,0,1;0rad)
  Solid = false
  Source = -> Face097
  Symmetric = false
FEATURE [Part::Revolution] Revolve106  label="removeToCreateScrewAndThreadedInsertHole033"
  Angle = 360
  Axis = (0,1,0)
  Base = (0,0,0)
  FaceMakerClass = Part::FaceMakerBullseye
  Placement = pos=(30.3,30.3,51.7) rot=(0,0,1;0rad)
  Solid = false
  Source = -> Face098
  Symmetric = false
FEATURE [Part::MultiFuse] Fusion069  label="createThreadedInsertHolesForFan003"
  Shapes = -> [Revolve103,Revolve104,Revolve105,Revolve106]
FEATURE [Part::Cut] Cut029  label="top015"
  Base = -> Cut028
  Tool = -> Fusion054
FEATURE [Part::Cut] Cut030  label="fanScrewHousing005"
  Base = -> Cut027
  Tool = -> Fusion069
FEATURE [Part::Cylinder] Cylinder026  label="removeToCreteHoleForPlugHousing010"
  Angle = 360
  AttacherType = Attacher::AttachEngine3D
  Height = 20
  Placement = pos=(-2,19,36) rot=(0,1,0;1.5708rad)
  Radius = 14.3
FEATURE [Part::Box] Box018  label="removeToCreteHoleForPlugHousing011"
  AttacherType = Attacher::AttachEngine3D
  Height = 28.6
  Length = 10
  Placement = pos=(-2,0,21.7) rot=(0,0,1;0rad)
  Width = 19
FEATURE [Part::Box] Box019  label="wireHolderBottomCaseBit"
  AttacherType = Attacher::AttachEngine3D
  Height = 28
  Length = 3
  Placement = pos=(0,0,22) rot=(0,0,1;0rad)
  Width = 21
FEATURE [Part::Cylinder] Cylinder027  label="removeToCreteHoleForPlugHousing012"
  Angle = 360
  AttacherType = Attacher::AttachEngine3D
  Height = 20
  Placement = pos=(-2,19,36) rot=(0,1,0;1.5708rad)
  Radius = 14.3
FEATURE [Part::Cut] Cut031  label="wireHolderBottomCaseBit001"
  Base = -> Box019
  Tool = -> Cylinder027
FEATURE [Part::MultiFuse] Fusion070  label="removeToCreteHoleForPlugHousing013"
  Shapes = -> [Box018,Cylinder026]
FEATURE [Part::Cut] Cut032  label="top016"
  Base = -> Cut029
  Tool = -> Fusion070
FEATURE [Part::Cylinder] Cylinder028
  Angle = 360
  AttacherType = Attacher::AttachEngine3D
  Height = 20
  Placement = pos=(0,0,36.15) rot=(0,0,1;0rad)
  Radius = 14.3
FEATURE [Part::Cylinder] Cylinder029
  Angle = 360
  AttacherType = Attacher::AttachEngine3D
  Height = 10
  Placement = pos=(0,0,36.15) rot=(0,0,1;0rad)
  Radius = 4
FEATURE [Part::MultiFuse] Fusion071  label="removeToCreteHoleForPlugHousing014"
  Placement = pos=(70,19,36) rot=(0,1,0;1.5708rad)
  Shapes = -> [Cylinder028,Cylinder029]
FEATURE [Sketcher::SketchObject] Sketch049  label="topSketch011"
  FullyConstrained = true
  sketch-geometry (4):
    g0: ArcOfCircle CenterX=105 CenterY=19 CenterZ=0 NormalX=0 NormalY=0 NormalZ=1 AngleXU=0 Radius=20.6155 StartAngle=5.54125 EndAngle=6.28319
    g1: ArcOfCircle CenterX=105 CenterY=19 CenterZ=0 NormalX=0 NormalY=0 NormalZ=1 AngleXU=0 Radius=13 StartAngle=5.54125 EndAngle=6.28319
    g2: LineSegment StartX=118 StartY=19 StartZ=0 EndX=125.616 EndY=19 EndZ=0
    g3: LineSegment StartX=114.583 StartY=10.2157 StartZ=0 EndX=120.197 EndY=5.06982 EndZ=0
  constraints (7):
    c: Block(g0)
    c: Block(g1)
    c: Coincident(g2,g1)
    c: Coincident(g2,g0)
    c: Horizontal(g2)
    c: Coincident(g3,g1)
    c: Coincident(g3,g0)
FEATURE [Part::Box] Box020  label="removeToCreteHoleForPlugHousing015"
  AttacherType = Attacher::AttachEngine3D
  Height = 28.6
  Length = 20
  Placement = pos=(106.15,0,21.7) rot=(0,0,1;0rad)
  Width = 19
FEATURE [Part::MultiFuse] Fusion072  label="removeToCreteHoleForPlugHousing016"
  Shapes = -> [Box020,Fusion071]
FEATURE [Part::Cut] Cut033  label="removeToCreteHoleForPlugHousing017"
  Base = -> Cut032
  Tool = -> Fusion072
FEATURE [Part::Cylinder] Cylinder030
  Angle = 360
  AttacherType = Attacher::AttachEngine3D
  Height = 20
  Placement = pos=(0,0,36.15) rot=(0,0,1;0rad)
  Radius = 14.3
FEATURE [Part::Cylinder] Cylinder031
  Angle = 360
  AttacherType = Attacher::AttachEngine3D
  Height = 10
  Placement = pos=(0,0,36.15) rot=(0,0,1;0rad)
  Radius = 4
FEATURE [Part::Box] Box021  label="removeToCreteHoleForPlugHousing019"
  AttacherType = Attacher::AttachEngine3D
  Height = 28.6
  Length = 20
  Placement = pos=(106.15,0,21.7) rot=(0,0,1;0rad)
  Width = 19
FEATURE [Part::MultiFuse] Fusion074  label="removeToCreteHoleForPlugHousing020"
  Placement = pos=(70,19,36) rot=(0,1,0;1.5708rad)
  Shapes = -> [Cylinder030,Cylinder031]
FEATURE [Part::MultiFuse] Fusion073  label="removeToCreteHoleForPlugHousing018"
  Placement = pos=(0,0,28.3) rot=(0,0,1;0rad)
  Shapes = -> [Box021,Fusion074]
FEATURE [Part::Cylinder] Cylinder032
  Angle = 360
  AttacherType = Attacher::AttachEngine3D
  Height = 20
  Placement = pos=(0,0,36.15) rot=(0,0,1;0rad)
  Radius = 14.3
FEATURE [Part::Cylinder] Cylinder033
  Angle = 360
  AttacherType = Attacher::AttachEngine3D
  Height = 10
  Placement = pos=(0,0,36.15) rot=(0,0,1;0rad)
  Radius = 4
FEATURE [Part::Box] Box022  label="removeToCreteHoleForPlugHousing021"
  AttacherType = Attacher::AttachEngine3D
  Height = 28.6
  Length = 20
  Placement = pos=(106.15,0,21.7) rot=(0,0,1;0rad)
  Width = 19
FEATURE [Part::MultiFuse] Fusion076  label="removeToCreteHoleForPlugHousing023"
  Placement = pos=(70,19,36) rot=(0,1,0;1.5708rad)
  Shapes = -> [Cylinder032,Cylinder033]
FEATURE [Part::MultiFuse] Fusion075  label="removeToCreteHoleForPlugHousing022"
  Placement = pos=(0,0,-28.3) rot=(0,0,1;0rad)
  Shapes = -> [Box022,Fusion076]
FEATURE [Part::MultiFuse] Fusion077  label="removeToCreatePlugHousingBottomBit"
  Shapes = -> [Fusion075,Fusion073]
FEATURE [Part::Cylinder] Cylinder034
  Angle = 360
  AttacherType = Attacher::AttachEngine3D
  Height = 20
  Placement = pos=(0,0,36.15) rot=(0,0,1;0rad)
  Radius = 14
FEATURE [Part::Cylinder] Cylinder035
  Angle = 360
  AttacherType = Attacher::AttachEngine3D
  Height = 10
  Placement = pos=(0,0,36.15) rot=(0,0,1;0rad)
  Radius = 4
FEATURE [Part::MultiFuse] Fusion078  label="removeToCreteHoleForPlugHousing024"
  Placement = pos=(70,19,36) rot=(0,1,0;1.5708rad)
  Shapes = -> [Cylinder034,Cylinder035]
FEATURE [Part::MultiFuse] Fusion079  label="removeToCreatePlugHousingBottomBit001"
  Shapes = -> [Fusion078,Fusion077]
FEATURE [Part::Extrusion] Extrude040  label="bottomPlugHousingBit"
  Base = -> Sketch049
  Dir = (0,0,1)
  DirMode = 2
  FaceMakerClass = Part::FaceMakerBullseye
  LengthFwd = 72
  LengthRev = 0
  Solid = true
  Symmetric = false
FEATURE [Part::Cut] Cut034  label="bottomPlugHousingBit001"
  Base = -> Extrude040
  Placement = pos=(-0.09,0,0) rot=(0,0,1;0rad)
  Tool = -> Fusion079
FEATURE [Part::Box] Box023  label="Cube014"
  AttacherType = Attacher::AttachEngine3D
  Height = 16
  Length = 8
  Placement = pos=(12.7,31.52,28) rot=(0,0,1;0rad)
  Width = 4
FEATURE [Part::Cylinder] Cylinder036
  Angle = 360
  AttacherType = Attacher::AttachEngine3D
  Height = 10
  Placement = pos=(0,0,36.15) rot=(0,0,1;0rad)
  Radius = 4
FEATURE [Part::Cylinder] Cylinder037
  Angle = 360
  AttacherType = Attacher::AttachEngine3D
  Height = 20
  Placement = pos=(0,0,36.15) rot=(0,0,1;0rad)
  Radius = 8.2
FEATURE [Part::MultiFuse] Fusion080  label="removeToCreteHoleForPlugHousing025"
  Placement = pos=(-42,19,36) rot=(0,1,0;1.5708rad)
  Shapes = -> [Cylinder037,Cylinder036]
FEATURE [Sketcher::SketchObject] Sketch050  label="topSketch012"
  FullyConstrained = true
  sketch-geometry (4):
    g0: LineSegment StartX=16.8446 StartY=31.512 StartZ=0 EndX=16.3251 EndY=34.4666 EndZ=0
    g1: ArcOfCircle CenterX=19 CenterY=19.2524 CenterZ=0 NormalX=0 NormalY=0 NormalZ=1 AngleXU=0 Radius=15.4476 StartAngle=1.74483 EndAngle=2.72717
    g2: ArcOfCircle CenterX=19 CenterY=19.2524 CenterZ=0 NormalX=0 NormalY=0 NormalZ=1 AngleXU=0 Radius=12.4476 StartAngle=1.74483 EndAngle=2.73189
    g3: LineSegment StartX=4.86004 StartY=25.4725 StartZ=0 EndX=7.58253 EndY=24.2107 EndZ=0
  constraints (7):
    c: Block(g0)
    c: Coincident(g1,g0)
    c: Coincident(g2,g0)
    c: Coincident(g3,g1)
    c: Coincident(g3,g2)
    c: Block(g1)
    c: Block(g2)
FEATURE [Part::Extrusion] Extrude041
  Base = -> Sketch050
  Dir = (0,0,1)
  DirMode = 2
  FaceMakerClass = Part::FaceMakerBullseye
  LengthFwd = 10.6
  LengthRev = 0
  Placement = pos=(0,0,31) rot=(0,0,1;0rad)
  Solid = true
  Symmetric = false
FEATURE [Part::Cut] Cut035
  Base = -> Extrude041
  Placement = pos=(0,0,-0.3) rot=(0,0,1;0rad)
  Tool = -> Fusion080
FEATURE [Part::Cut] Cut036
  Base = -> Box023
  Tool = -> Cut035
FEATURE [Part::Fillet] Fillet027
  Base = -> Cut036
  Edges = 1 edges r=0.7: [Edge13]
FEATURE [Part::Fillet] Fillet028
  Base = -> Fillet027
  Edges = 1 edges r=0.7: [Edge13]
FEATURE [Part::Fillet] Fillet029
  Base = -> Fillet028
  Edges = 1 edges r=0.7: [Edge16]
FEATURE [Part::Fillet] Fillet030
  Base = -> Fillet029
  Edges = 1 edges r=0.7: [Edge11]
FEATURE [Part::Fillet] Fillet031
  Base = -> Fillet030
  Edges = 1 edges r=0.7: [Edge10]
FEATURE [Part::Fillet] Fillet032
  Base = -> Fillet031
  Edges = 1 edges r=1.2: [Edge5]
FEATURE [Part::Fillet] Fillet033
  Base = -> Fillet032
  Edges = 1 edges r=1.2: [Edge12]
FEATURE [Part::Fillet] Fillet034  label="wireHousingRetainer"
  Base = -> Fillet033
  Edges = 1 edges r=2: [Edge1]
  Placement = pos=(0.3,0,0) rot=(0,0,1;0rad)
FEATURE [Part::Feature] Face099
  shape: bbox 3.5 x 17.8 x 2e-07 mm, 1 faces, 0 solids (baked)
FEATURE [Part::Revolution] Revolve107  label="removeToCreateScrewAndThreadedInsertHole034"
  Angle = 360
  Axis = (0,1,0)
  Base = (0,0,0)
  FaceMakerClass = Part::FaceMakerBullseye
  Placement = pos=(12.5,0,10) rot=(0,0,1;0rad)
  Solid = false
  Source = -> Face099
  Symmetric = false
FEATURE [Part::Feature] Face100
  shape: bbox 3.5 x 17.8 x 2e-07 mm, 1 faces, 0 solids (baked)
FEATURE [Part::Revolution] Revolve108  label="removeToCreateScrewAndThreadedInsertHole035"
  Angle = 360
  Axis = (0,1,0)
  Base = (0,0,0)
  FaceMakerClass = Part::FaceMakerBullseye
  Placement = pos=(12.5,0,62) rot=(0,0,1;0rad)
  Solid = false
  Source = -> Face100
  Symmetric = false
FEATURE [Part::Feature] Face101
  shape: bbox 3.5 x 17.8 x 2e-07 mm, 1 faces, 0 solids (baked)
FEATURE [Part::Revolution] Revolve109  label="removeToCreateScrewAndThreadedInsertHole036"
  Angle = 360
  Axis = (0,1,0)
  Base = (0,0,0)
  FaceMakerClass = Part::FaceMakerBullseye
  Placement = pos=(89.5,0,68.5) rot=(0,0,1;0rad)
  Solid = false
  Source = -> Face101
  Symmetric = false
FEATURE [Part::Feature] Face102
  shape: bbox 3.5 x 17.8 x 2e-07 mm, 1 faces, 0 solids (baked)
FEATURE [Part::Revolution] Revolve110  label="removeToCreateScrewAndThreadedInsertHole037"
  Angle = 360
  Axis = (0,1,0)
  Base = (0,0,0)
  FaceMakerClass = Part::FaceMakerBullseye
  Placement = pos=(89.5,0,3.5) rot=(0,0,1;0rad)
  Solid = false
  Source = -> Face102
  Symmetric = false
FEATURE [Part::Feature] Face103
  shape: bbox 3.5 x 17.8 x 2e-07 mm, 1 faces, 0 solids (baked)
FEATURE [Part::Revolution] Revolve111  label="removeToCreateScrewAndThreadedInsertHole038"
  Angle = 360
  Axis = (0,1,0)
  Base = (0,0,0)
  FaceMakerClass = Part::FaceMakerBullseye
  Placement = pos=(109.5,4.7,3.5) rot=(0,0,1;0rad)
  Solid = false
  Source = -> Face103
  Symmetric = false
FEATURE [Part::Feature] Face104
  shape: bbox 3.5 x 17.8 x 2e-07 mm, 1 faces, 0 solids (baked)
FEATURE [Part::Revolution] Revolve112  label="removeToCreateScrewAndThreadedInsertHole039"
  Angle = 360
  Axis = (0,1,0)
  Base = (0,0,0)
  FaceMakerClass = Part::FaceMakerBullseye
  Placement = pos=(109.5,4.7,68.5) rot=(0,0,1;0rad)
  Solid = false
  Source = -> Face104
  Symmetric = false
FEATURE [Part::MultiFuse] Fusion081  label="removeToCreateScrewAndThreadedInsertHole040"
  Shapes = -> [Revolve107,Revolve108,Revolve109,Revolve110,Revolve111,Revolve112]
FEATURE [Part::MultiFuse] Fusion082  label="casePillars002"
  Shapes = -> [Revolve094,Revolve092,Revolve090,Revolve089,Revolve091,Revolve093]
FEATURE [Part::Cut] Cut037  label="casePillars003"
  Base = -> Fusion082
  Tool = -> Fusion081
FEATURE [Sketcher::SketchObject] Sketch051
  FullyConstrained = true
  Placement = pos=(117,19,0) rot=(0.57735,0.57735,0.57735;2.0944rad)
  sketch-geometry (48):
    g0: LineSegment StartX=-49.19 StartY=69.25 StartZ=0 EndX=-49.19 EndY=66.25 EndZ=0
    g1: LineSegment StartX=-49.19 StartY=63.5 StartZ=0 EndX=-49.19 EndY=60.5 EndZ=0
    g2: LineSegment StartX=-49.19 StartY=57.75 StartZ=0 EndX=-49.19 EndY=54.75 EndZ=0
    g3: LineSegment StartX=-49.19 StartY=52 StartZ=0 EndX=-49.19 EndY=49 EndZ=0
    g4: LineSegment StartX=-49.19 StartY=46.25 StartZ=0 EndX=-49.19 EndY=43.25 EndZ=0
    g5: LineSegment StartX=-49.19 StartY=40.5 StartZ=0 EndX=-49.19 EndY=37.5 EndZ=0
    g6: LineSegment StartX=-49.19 StartY=34.5 StartZ=0 EndX=-49.19 EndY=31.5 EndZ=0
    g7: LineSegment StartX=-49.19 StartY=28.75 StartZ=0 EndX=-49.19 EndY=25.75 EndZ=0
    g8: LineSegment StartX=-49.19 StartY=23 StartZ=0 EndX=-49.19 EndY=20 EndZ=0
    g9: LineSegment StartX=-49.19 StartY=17.25 StartZ=0 EndX=-49.19 EndY=14.25 EndZ=0
    g10: LineSegment StartX=-49.19 StartY=11.5 StartZ=0 EndX=-49.19 EndY=8.5 EndZ=0
    g11: LineSegment StartX=-49.19 StartY=5.75 StartZ=0 EndX=-49.19 EndY=2.75 EndZ=0
    g12: ArcOfCircle CenterX=-1.5 CenterY=67.75 CenterZ=0 NormalX=0 NormalY=0 NormalZ=1 AngleXU=0 Radius=1.5 StartAngle=4.71239 EndAngle=7.85398
    g13: ArcOfCircle CenterX=-1.5 CenterY=62 CenterZ=0 NormalX=0 NormalY=0 NormalZ=1 AngleXU=0 Radius=1.5 StartAngle=4.71239 EndAngle=7.85398
    g14: ArcOfCircle CenterX=-1.5 CenterY=56.25 CenterZ=0 NormalX=0 NormalY=0 NormalZ=1 AngleXU=0 Radius=1.5 StartAngle=4.71239 EndAngle=7.85398
    g15: ArcOfCircle CenterX=-11.49 CenterY=50.5 CenterZ=0 NormalX=0 NormalY=0 NormalZ=1 AngleXU=0 Radius=1.5 StartAngle=4.71239 EndAngle=7.85398
    g16: ArcOfCircle CenterX=-16.28 CenterY=44.75 CenterZ=0 NormalX=0 NormalY=0 NormalZ=1 AngleXU=0 Radius=1.5 StartAngle=4.71239 EndAngle=7.85398
    g17: ArcOfCircle CenterX=-18.2337 CenterY=39 CenterZ=0 NormalX=0 NormalY=0 NormalZ=1 AngleXU=0 Radius=1.5 StartAngle=4.71485 EndAngle=7.85398
    g18: ArcOfCircle CenterX=-16.2837 CenterY=27.25 CenterZ=0 NormalX=0 NormalY=0 NormalZ=1 AngleXU=0 Radius=1.5 StartAngle=4.71485 EndAngle=7.85398
    g19: ArcOfCircle CenterX=-18.2337 CenterY=33 CenterZ=0 NormalX=0 NormalY=0 NormalZ=1 AngleXU=0 Radius=1.5 StartAngle=4.71485 EndAngle=7.85398
    g20: ArcOfCircle CenterX=-11.49 CenterY=21.5 CenterZ=0 NormalX=0 NormalY=0 NormalZ=1 AngleXU=0 Radius=1.5 StartAngle=4.71239 EndAngle=7.85398
    g21: ArcOfCircle CenterX=-1.5 CenterY=4.25 CenterZ=0 NormalX=0 NormalY=0 NormalZ=1 AngleXU=0 Radius=1.5 StartAngle=4.71239 EndAngle=7.85398
    g22: ArcOfCircle CenterX=-1.5 CenterY=10 CenterZ=0 NormalX=0 NormalY=0 NormalZ=1 AngleXU=0 Radius=1.5 StartAngle=4.71239 EndAngle=7.85398
    g23: ArcOfCircle CenterX=-1.5 CenterY=15.75 CenterZ=0 NormalX=0 NormalY=0 NormalZ=1 AngleXU=0 Radius=1.5 StartAngle=4.71239 EndAngle=7.85398
    g24: LineSegment StartX=-49.19 StartY=69.25 StartZ=0 EndX=-1.5 EndY=69.25 EndZ=0
    g25: LineSegment StartX=-49.19 StartY=66.25 StartZ=0 EndX=-1.5 EndY=66.25 EndZ=0
    g26: LineSegment StartX=-49.19 StartY=63.5 StartZ=0 EndX=-1.5 EndY=63.5 EndZ=0
    g27: LineSegment StartX=-49.19 StartY=60.5 StartZ=0 EndX=-1.5 EndY=60.5 EndZ=0
    g28: LineSegment StartX=-49.19 StartY=57.75 StartZ=0 EndX=-1.5 EndY=57.75 EndZ=0
    g29: LineSegment StartX=-49.19 StartY=54.75 StartZ=0 EndX=-1.5 EndY=54.75 EndZ=0
    g30: LineSegment StartX=-49.19 StartY=52 StartZ=0 EndX=-11.49 EndY=52 EndZ=0
    g31: LineSegment StartX=-49.19 StartY=49 StartZ=0 EndX=-11.49 EndY=49 EndZ=0
    g32: LineSegment StartX=-49.19 StartY=46.25 StartZ=0 EndX=-16.28 EndY=46.25 EndZ=0
    g33: LineSegment StartX=-49.19 StartY=43.25 StartZ=0 EndX=-16.28 EndY=43.25 EndZ=0
    g34: LineSegment StartX=-49.19 StartY=40.5 StartZ=0 EndX=-18.2337 EndY=40.5 EndZ=0
    g35: LineSegment StartX=-49.19 StartY=37.5 StartZ=0 EndX=-18.23 EndY=37.5 EndZ=0
    g36: LineSegment StartX=-49.19 StartY=34.5 StartZ=0 EndX=-18.2337 EndY=34.5 EndZ=0
    g37: LineSegment StartX=-49.19 StartY=31.5 StartZ=0 EndX=-18.23 EndY=31.5 EndZ=0
    g38: LineSegment StartX=-49.19 StartY=28.75 StartZ=0 EndX=-16.2837 EndY=28.75 EndZ=0
    g39: LineSegment StartX=-49.19 StartY=25.75 StartZ=0 EndX=-16.28 EndY=25.75 EndZ=0
    g40: LineSegment StartX=-49.19 StartY=23 StartZ=0 EndX=-11.49 EndY=23 EndZ=0
    g41: LineSegment StartX=-49.19 StartY=20 StartZ=0 EndX=-11.49 EndY=20 EndZ=0
    g42: LineSegment StartX=-49.19 StartY=17.25 StartZ=0 EndX=-1.5 EndY=17.25 EndZ=0
    g43: LineSegment StartX=-49.19 StartY=14.25 StartZ=0 EndX=-1.5 EndY=14.25 EndZ=0
    g44: LineSegment StartX=-49.19 StartY=11.5 StartZ=0 EndX=-1.5 EndY=11.5 EndZ=0
    g45: LineSegment StartX=-49.19 StartY=8.5 StartZ=0 EndX=-1.5 EndY=8.5 EndZ=0
    g46: LineSegment StartX=-49.19 StartY=5.75 StartZ=0 EndX=-1.5 EndY=5.75 EndZ=0
    g47: LineSegment StartX=-49.19 StartY=2.75 StartZ=0 EndX=-1.5 EndY=2.75 EndZ=0
  constraints (120):
    c: Vertical(g0)
    c: Distance(g0) = 3
    c: Block(g0)
    c: Vertical(g1)
    c: Distance(g1) = 3
    c: Vertical(g2)
    c: Equal(g0,g2) = 3
    c: Block(g2)
    c: Vertical(g3)
    c: Equal(g1,g3) = 3
    c: Vertical(g4)
    c: Equal(g0,g4) = 3
    c: Block(g4)
    c: Vertical(g5)
    c: Equal(g1,g5) = 3
    c: Vertical(g6)
    c: Equal(g0,g6) = 3
    c: Block(g6)
    c: Vertical(g7)
    c: Equal(g1,g7) = 3
    c: Vertical(g8)
    c: Equal(g0,g8) = 3
    c: Block(g8)
    c: Vertical(g9)
    c: Equal(g1,g9) = 3
    c: Vertical(g10)
    c: Equal(g0,g10) = 3
    c: Block(g10)
    c: Vertical(g11)
    c: Equal(g1,g11) = 3
    c: Block(g12)
    c: Block(g13)
    c: Block(g14)
    c: Block(g15)
    c: Block(g16)
    c: Block(g17)
    c: Block(g18)
    c: Block(g19)
    c: Block(g20)
    c: Block(g21)
    c: Block(g22)
    c: Block(g23)
    c: Block(g11)
    c: Block(g9)
    c: Block(g7)
    c: Block(g5)
    c: Block(g3)
    c: Block(g1)
    c: Coincident(g24,g0)
    c: Coincident(g24,g12)
    c: Horizontal(g24)
    c: Coincident(g25,g0)
    c: Coincident(g25,g12)
    c: Horizontal(g25)
    c: Coincident(g26,g1)
    c: Coincident(g26,g13)
    c: Horizontal(g26)
    c: Coincident(g27,g1)
    c: Coincident(g27,g13)
    c: Horizontal(g27)
    c: Coincident(g28,g2)
    c: Coincident(g28,g14)
    c: Horizontal(g28)
    c: Coincident(g29,g2)
    c: Coincident(g29,g14)
    c: Horizontal(g29)
    c: Coincident(g30,g3)
    c: Coincident(g30,g15)
    c: Horizontal(g30)
    c: Coincident(g31,g3)
    c: Coincident(g31,g15)
    c: Horizontal(g31)
    c: Coincident(g32,g4)
    c: Coincident(g32,g16)
    c: Horizontal(g32)
    c: Coincident(g33,g4)
    c: Coincident(g33,g16)
    c: Horizontal(g33)
    c: Coincident(g34,g5)
    c: Coincident(g34,g17)
    c: Horizontal(g34)
    c: Coincident(g35,g5)
    c: Coincident(g35,g17)
    c: Horizontal(g35)
    c: Coincident(g36,g6)
    c: Coincident(g36,g19)
    c: Horizontal(g36)
    c: Coincident(g37,g6)
    c: Coincident(g37,g19)
    c: Horizontal(g37)
    c: Coincident(g38,g7)
    c: Coincident(g38,g18)
    c: Horizontal(g38)
    c: Coincident(g39,g7)
    c: Coincident(g39,g18)
    c: Horizontal(g39)
    c: Coincident(g40,g8)
    c: Coincident(g40,g20)
    c: Horizontal(g40)
    c: Coincident(g41,g8)
    c: Coincident(g41,g20)
    c: Horizontal(g41)
    c: Coincident(g42,g9)
    c: Coincident(g42,g23)
    c: Horizontal(g42)
    c: Coincident(g43,g9)
    c: Coincident(g43,g23)
    c: Horizontal(g43)
    c: Coincident(g44,g10)
    c: Coincident(g44,g22)
    c: Horizontal(g44)
    c: Coincident(g45,g10)
    c: Coincident(g45,g22)
    c: Horizontal(g45)
    c: Coincident(g46,g11)
    c: Coincident(g46,g21)
    c: Horizontal(g46)
    c: Coincident(g47,g11)
    c: Coincident(g47,g21)
    c: Horizontal(g47)
FEATURE [Part::Extrusion] Extrude042
  Base = -> Sketch051
  Dir = (1,-2e-16,2e-16)
  DirMode = 2
  FaceMakerClass = Part::FaceMakerBullseye
  LengthFwd = 19
  LengthRev = 0
  Placement = pos=(-19,0,0) rot=(0,0,1;0rad)
  Solid = true
  Symmetric = false
FEATURE [Part::Fillet] Fillet035  label="removeToCreateVentalationHoles"
  Base = -> Extrude042
  Edges = <same value as first occurrence — deduplicated (x6 in doc)>
  Placement = pos=(7,0,0) rot=(0,0,1;0rad)
FEATURE [Part::Cut] Cut038  label="top017"
  Base = -> Cut033
  Tool = -> Fillet035
FEATURE [Sketcher::SketchObject] Sketch052  label="bottomSketch001"
  FullyConstrained = true
  sketch-geometry (45):
    g0: LineSegment StartX=6.29999 StartY=8 StartZ=0 EndX=3.29999 EndY=8 EndZ=0
    g1: LineSegment StartX=3.29999 StartY=8 StartZ=0 EndX=3.29999 EndY=-6.03275e-07 EndZ=0
    g2: ArcOfCircle CenterX=8.29999 CenterY=5 CenterZ=0 NormalX=0 NormalY=0 NormalZ=1 AngleXU=0 Radius=2 StartAngle=3.14159 EndAngle=4.71239
    g3: LineSegment StartX=6.29999 StartY=8 StartZ=0 EndX=6.29999 EndY=5 EndZ=0
    g4: ArcOfCircle CenterX=105 CenterY=19 CenterZ=0 NormalX=0 NormalY=0 NormalZ=1 AngleXU=0 Radius=12.7 StartAngle=4.71239 EndAngle=5.94289
    g5-g11: Circle x7 (B-spline internal-alignment scaffolding for g12; pole/knot coordinates omitted)
    g12: BSplineCurve PolesCount=7 KnotsCount=5 Degree=3 IsPeriodic=0
    g13-g17: GeomPoint x5 (B-spline internal-alignment scaffolding for g12; pole/knot coordinates omitted)
    g18: ArcOfCircle CenterX=105 CenterY=19 CenterZ=0 NormalX=0 NormalY=0 NormalZ=1 AngleXU=0 Radius=15.7 StartAngle=5.81226 EndAngle=6.28319
    g19: BSplineCurve PolesCount=5 KnotsCount=3 Degree=3 IsPeriodic=0
    g20: LineSegment StartX=8.29999 StartY=3 StartZ=0 EndX=101.7 EndY=3 EndZ=0
    g21: LineSegment StartX=3.29999 StartY=-6.03275e-07 StartZ=0 EndX=105 EndY=-6.03275e-07 EndZ=0
    g22: LineSegment StartX=120.974 StartY=8.71251 StartZ=0 EndX=122.332 EndY=7.83778 EndZ=0
    g23: LineSegment StartX=105 StartY=-6.03274e-07 StartZ=0 EndX=113 EndY=-6.03274e-07 EndZ=0
    g24: ArcOfCircle CenterX=105 CenterY=19 CenterZ=0 NormalX=0 NormalY=0 NormalZ=1 AngleXU=0 Radius=20.6155 StartAngle=5.11091 EndAngle=5.71103
    g25: ArcOfCircle CenterX=117.7 CenterY=19 CenterZ=0 NormalX=0 NormalY=0 NormalZ=1 AngleXU=0 Radius=3 StartAngle=1.2e-15 EndAngle=2.10468
    g26: Circle CenterX=116.345 CenterY=16.3232 CenterZ=0 NormalX=0 NormalY=0 NormalZ=1 AngleXU=0 Radius=1
    g27: Circle CenterX=117.24 CenterY=15.7584 CenterZ=0 NormalX=0 NormalY=0 NormalZ=1 AngleXU=0 Radius=1
    g28: Circle CenterX=116.972 CenterY=14.7612 CenterZ=0 NormalX=0 NormalY=0 NormalZ=1 AngleXU=0 Radius=1
    g29: BSplineCurve PolesCount=3 KnotsCount=2 Degree=2 IsPeriodic=0
    g30: GeomPoint X=116.345 Y=16.3232 Z=0
    g31: GeomPoint X=116.972 Y=14.7612 Z=0
    g32: Circle CenterX=115.828 CenterY=17.157 CenterZ=0 NormalX=0 NormalY=0 NormalZ=1 AngleXU=0 Radius=1
    g33: Circle CenterX=115.841 CenterY=16.639 CenterZ=0 NormalX=0 NormalY=0 NormalZ=1 AngleXU=0 Radius=1
    g34: Circle CenterX=116.345 CenterY=16.3232 CenterZ=0 NormalX=0 NormalY=0 NormalZ=1 AngleXU=0 Radius=1
    g35: BSplineCurve PolesCount=3 KnotsCount=2 Degree=2 IsPeriodic=0
    g36: GeomPoint X=115.828 Y=17.157 Z=0
    g37: GeomPoint X=116.345 Y=16.3232 Z=0
    g38: LineSegment StartX=115.828 StartY=17.157 StartZ=0 EndX=115.828 EndY=20.8307 EndZ=0
    g39: Circle CenterX=115.828 CenterY=20.8307 CenterZ=0 NormalX=0 NormalY=0 NormalZ=1 AngleXU=0 Radius=1
    g40: Circle CenterX=115.831 CenterY=21.3396 CenterZ=0 NormalX=0 NormalY=0 NormalZ=1 AngleXU=0 Radius=1
    g41: Circle CenterX=116.173 CenterY=21.5825 CenterZ=0 NormalX=0 NormalY=0 NormalZ=1 AngleXU=0 Radius=1
    g42: BSplineCurve PolesCount=3 KnotsCount=2 Degree=2 IsPeriodic=0
    g43: GeomPoint X=115.828 Y=20.8307 Z=0
    g44: GeomPoint X=116.173 Y=21.5825 Z=0
  constraints (70):
    c: Horizontal(g0)
    c: Distance(g0) = 3
    c: Coincident(g1,g0)
    c: Vertical(g1)
    c: Block(g2)
    c: Block(g0)
    c: Coincident(g3,g0)
    c: Coincident(g3,g2)
    c: Vertical(g3)
    c: Block(g1)
    c: Block(g4)
    c: Coincident(g19,g4)
    c: Block(g19)
    c: Equal(g5, g6-g11) x6
    c: InternalAlignment(g5-g11 -> g12) x7
    c: InternalAlignment(g13-g17 -> g12) x5
    c: Block(g12)
    c: Coincident(g18,g12)
    c: Block(g18)
    c: Coincident(g20,g2)
    c: Coincident(g20,g19)
    c: Horizontal(g20)
    c: Distance(g20) = 93.4
    c: Coincident(g21,g1)
    c: Horizontal(g21)
    c: Distance(g21) = 101.7
    c: Horizontal(g23)
    c: Distance(g23) = 8
    c: Coincident(g24,g23)
    c: Block(g23)
    c: Coincident(g22,g24)
    c: Block(g24)
    c: Block(g22)
    c: Distance(g22) = 1.61553
    c: Coincident(g25,g18)
    c: Block(g25)
    c: Weight(g26) = 1
    c: Equal(g26,g27)
    c: Equal(g26,g28)
    c: Coincident(g29,g4)
    c: InternalAlignment(g26,g29)
    c: InternalAlignment(g27,g29)
    c: InternalAlignment(g28,g29)
    c: InternalAlignment(g30,g29)
    c: InternalAlignment(g31,g29)
    c: Block(g29)
    c: Weight(g32) = 1
    c: Equal(g32,g33)
    c: Equal(g32,g34)
    c: Coincident(g35,g29)
    c: InternalAlignment(g32,g35)
    c: InternalAlignment(g33,g35)
    c: InternalAlignment(g34,g35)
    c: InternalAlignment(g36,g35)
    c: InternalAlignment(g37,g35)
    c: Block(g35)
    c: Coincident(g38,g35)
    c: Vertical(g38)
    c: Block(g38)
    c: Coincident(g42,g38)
    c: Weight(g39) = 1
    c: Equal(g39,g40)
    c: Equal(g39,g41)
    c: Coincident(g42,g25)
    c: InternalAlignment(g39,g42)
    c: InternalAlignment(g40,g42)
    c: InternalAlignment(g41,g42)
    c: InternalAlignment(g43,g42)
    c: InternalAlignment(g44,g42)
    c: Block(g42)
FEATURE [Part::Extrusion] Extrude043  label="bottom010"
  Base = -> Sketch052
  Dir = (0,0,1)
  DirMode = 2
  FaceMakerClass = Part::FaceMakerBullseye
  LengthFwd = 71.4
  LengthRev = 0
  Placement = pos=(0,0,0.3) rot=(0,0,1;0rad)
  Solid = true
  Symmetric = false
FEATURE [Sketcher::SketchObject] Sketch053  label="topSketch013"
  FullyConstrained = true
  sketch-geometry (22):
    g0: LineSegment StartX=5.21097e-06 StartY=3 StartZ=0 EndX=5.21097e-06 EndY=19 EndZ=0
    g1: ArcOfCircle CenterX=19 CenterY=19 CenterZ=0 NormalX=0 NormalY=0 NormalZ=1 AngleXU=0 Radius=19 StartAngle=1.5708 EndAngle=3.14159
    g2: ArcOfCircle CenterX=19 CenterY=19 CenterZ=0 NormalX=0 NormalY=0 NormalZ=1 AngleXU=0 Radius=16 StartAngle=1.5708 EndAngle=3.14159
    g3: LineSegment StartX=114 StartY=35 StartZ=0 EndX=19 EndY=35 EndZ=0
    g4: LineSegment StartX=5.21097e-06 StartY=3 StartZ=0 EndX=5.21097e-06 EndY=0 EndZ=0
    g5: LineSegment StartX=3 StartY=0 StartZ=0 EndX=5.21097e-06 EndY=0 EndZ=0
    g6: LineSegment StartX=3 StartY=19 StartZ=0 EndX=3 EndY=0 EndZ=0
    g7: LineSegment StartX=19 StartY=38 StartZ=0 EndX=124 EndY=38 EndZ=0
    g8: Circle CenterX=119 CenterY=35 CenterZ=0 NormalX=0 NormalY=0 NormalZ=1 AngleXU=0 Radius=1
    g9: Circle CenterX=121 CenterY=35 CenterZ=0 NormalX=0 NormalY=0 NormalZ=1 AngleXU=0 Radius=1
    g10: Circle CenterX=121 CenterY=33 CenterZ=0 NormalX=0 NormalY=0 NormalZ=1 AngleXU=0 Radius=1
    g11: BSplineCurve PolesCount=3 KnotsCount=2 Degree=2 IsPeriodic=0
    g12: GeomPoint X=119 Y=35 Z=0
    g13: GeomPoint X=121 Y=33 Z=0
    g14: LineSegment StartX=119 StartY=35 StartZ=0 EndX=114 EndY=35 EndZ=0
    g15: ArcOfCircle CenterX=105 CenterY=19 CenterZ=0 NormalX=0 NormalY=0 NormalZ=1 AngleXU=0 Radius=16 StartAngle=5.60905 EndAngle=6.28319
    g16: LineSegment StartX=121 StartY=33 StartZ=0 EndX=121 EndY=19 EndZ=0
    g17: LineSegment StartX=117.5 StartY=9.01251 StartZ=0 EndX=121.163 EndY=9.0125 EndZ=0
    g18: ArcOfCircle CenterX=105 CenterY=19 CenterZ=0 NormalX=0 NormalY=0 NormalZ=1 AngleXU=0 Radius=20.6155 StartAngle=5.7297 EndAngle=6.28319
    g19: LineSegment StartX=121.163 StartY=9.0125 StartZ=0 EndX=122.538 EndY=8.16329 EndZ=0
    g20: LineSegment StartX=124 StartY=38 StartZ=0 EndX=125.616 EndY=38 EndZ=0
    g21: LineSegment StartX=125.616 StartY=19 StartZ=0 EndX=125.616 EndY=38 EndZ=0
  constraints (50):
    c: Vertical(g0)
    c: Block(g0)
    c: Coincident(g1,g0)
    c: Block(g1)
    c: Coincident(g2,g1)
    c: Block(g2)
    c: Coincident(g3,g2)
    c: Horizontal(g3)
    c: Tangent(g3,g2)
    c: Coincident(g4,g0)
    c: Distance(g4) = 3
    c: Vertical(g4)
    c: Coincident(g5,g4)
    c: Horizontal(g5)
    c: Coincident(g6,g2)
    c: Coincident(g6,g5)
    c: Vertical(g6)
    c: Horizontal(g7)
    c: Distance(g7) = 105
    c: Coincident(g7,g1)
    c: Block(g3)
    c: Weight(g8) = 1
    c: Equal(g8,g9)
    c: Equal(g8,g10)
    c: InternalAlignment(g8,g11)
    c: InternalAlignment(g9,g11)
    c: InternalAlignment(g10,g11)
    c: InternalAlignment(g12,g11)
    c: InternalAlignment(g13,g11)
    c: Block(g11)
    c: Coincident(g14,g11)
    c: Coincident(g14,g3)
    c: Horizontal(g14)
    c: Block(g15)
    c: Coincident(g16,g11)
    c: Coincident(g16,g15)
    c: Vertical(g16)
    c: Distance(g16) = 14
    c: Coincident(g17,g15)
    c: Block(g18)
    c: Coincident(g19,g18)
    c: Coincident(g20,g7)
    c: Horizontal(g20)
    c: Vertical(g21)
    c: Coincident(g20,g21)
    c: Block(g20)
    c: Block(g21)
    c: Block(g19)
    c: Block(g17)
    c: Distance(g20) = 1.61553
FEATURE [Part::Extrusion] Extrude044
  Base = -> Sketch053
  Dir = (0,0,1)
  DirMode = 2
  FaceMakerClass = Part::FaceMakerBullseye
  LengthFwd = 72
  LengthRev = 0
  Solid = true
  Symmetric = false
FEATURE [Part::Fillet] Fillet036  label="top018"
  Base = -> Extrude044
  Edges = 1 edges r=2: [Edge41]
FEATURE [Sketcher::SketchObject] Sketch054
  FullyConstrained = false
  Placement = pos=(0,0,0) rot=(1,0,0;1.5708rad)
  sketch-geometry (24):
    g0: ArcOfCircle CenterX=-4 CenterY=-10.5 CenterZ=0 NormalX=0 NormalY=0 NormalZ=1 AngleXU=0 Radius=1.5 StartAngle=6e-16 EndAngle=3.14159
    g1: ArcOfCircle CenterX=-34.2 CenterY=-10.5 CenterZ=0 NormalX=0 NormalY=0 NormalZ=1 AngleXU=0 Radius=1.5 StartAngle=0 EndAngle=3.14159
    g2: ArcOfCircle CenterX=-34.2 CenterY=-27.7 CenterZ=0 NormalX=0 NormalY=0 NormalZ=1 AngleXU=0 Radius=1.5 StartAngle=3.14159 EndAngle=6.28319
    g3: ArcOfCircle CenterX=-4 CenterY=-27.7 CenterZ=0 NormalX=0 NormalY=0 NormalZ=1 AngleXU=0 Radius=1.5 StartAngle=3.1416 EndAngle=6.28319
    g4: ArcOfCircle CenterX=-10 CenterY=-4.3 CenterZ=0 NormalX=0 NormalY=0 NormalZ=1 AngleXU=0 Radius=1.5 StartAngle=2e-16 EndAngle=3.14159
    g5: ArcOfCircle CenterX=-16.1 CenterY=-1.8 CenterZ=0 NormalX=0 NormalY=0 NormalZ=1 AngleXU=0 Radius=1.5 StartAngle=5e-16 EndAngle=3.14159
    g6: ArcOfCircle CenterX=-22.1 CenterY=-1.8 CenterZ=0 NormalX=0 NormalY=0 NormalZ=1 AngleXU=0 Radius=1.5 StartAngle=5e-16 EndAngle=3.14159
    g7: ArcOfCircle CenterX=-28.2 CenterY=-4.3 CenterZ=0 NormalX=0 NormalY=0 NormalZ=1 AngleXU=0 Radius=1.5 StartAngle=2e-16 EndAngle=3.14159
    g8: ArcOfCircle CenterX=-10 CenterY=-33.9 CenterZ=0 NormalX=0 NormalY=0 NormalZ=1 AngleXU=0 Radius=1.5 StartAngle=3.14159 EndAngle=6.28319
    g9: ArcOfCircle CenterX=-16.1 CenterY=-36.4 CenterZ=0 NormalX=0 NormalY=0 NormalZ=1 AngleXU=0 Radius=1.5 StartAngle=3.14159 EndAngle=6.28319
    g10: ArcOfCircle CenterX=-22.1 CenterY=-36.4 CenterZ=0 NormalX=0 NormalY=0 NormalZ=1 AngleXU=0 Radius=1.5 StartAngle=3.14159 EndAngle=6.28319
    g11: ArcOfCircle CenterX=-28.2 CenterY=-33.9 CenterZ=0 NormalX=0 NormalY=0 NormalZ=1 AngleXU=0 Radius=1.5 StartAngle=3.14159 EndAngle=6.28319
    g12: LineSegment StartX=-35.7 StartY=-10.5 StartZ=0 EndX=-35.7 EndY=-27.7 EndZ=0
    g13: LineSegment StartX=-32.7 StartY=-10.5 StartZ=0 EndX=-32.7 EndY=-27.7 EndZ=0
    g14: LineSegment StartX=-29.7 StartY=-33.9 StartZ=0 EndX=-29.7 EndY=-4.3 EndZ=0
    g15: LineSegment StartX=-26.7 StartY=-33.9 StartZ=0 EndX=-26.7 EndY=-4.3 EndZ=0
    g16: LineSegment StartX=-2.5 StartY=-10.5 StartZ=0 EndX=-2.5 EndY=-27.7 EndZ=0
    g17: LineSegment StartX=-8.5 StartY=-4.3 StartZ=0 EndX=-8.5 EndY=-33.9 EndZ=0
    g18: LineSegment StartX=-5.5 StartY=-10.5 StartZ=0 EndX=-5.5 EndY=-27.7 EndZ=0
    g19: LineSegment StartX=-11.5 StartY=-4.3 StartZ=0 EndX=-11.5 EndY=-33.9 EndZ=0
    g20: LineSegment StartX=-14.6 StartY=-1.8 StartZ=0 EndX=-14.6 EndY=-36.4 EndZ=0
    g21: LineSegment StartX=-17.6 StartY=-1.8 StartZ=0 EndX=-17.6 EndY=-36.4 EndZ=0
    g22: LineSegment StartX=-20.6 StartY=-36.4 StartZ=0 EndX=-20.6 EndY=-1.8 EndZ=0
    g23: LineSegment StartX=-23.6 StartY=-1.8 StartZ=0 EndX=-23.6 EndY=-36.4 EndZ=0
  constraints (48):
    c: Block(g0)
    c: Block(g1)
    c: Block(g2)
    c: Block(g3)
    c: Block(g4)
    c: Block(g5)
    c: Block(g6)
    c: Block(g7)
    c: Block(g8)
    c: Block(g9)
    c: Block(g10)
    c: Block(g11)
    c: Coincident(g12,g1)
    c: Coincident(g12,g2)
    c: Vertical(g12)
    c: Coincident(g13,g1)
    c: Coincident(g13,g2)
    c: Vertical(g13)
    c: Coincident(g14,g11)
    c: Coincident(g14,g7)
    c: Vertical(g14)
    c: Coincident(g15,g11)
    c: Coincident(g15,g7)
    c: Vertical(g15)
    c: Coincident(g16,g0)
    c: Coincident(g16,g3)
    c: Vertical(g16)
    c: Coincident(g17,g4)
    c: Coincident(g17,g8)
    c: Vertical(g17)
    c: Coincident(g18,g0)
    c: Coincident(g18,g3)
    c: Vertical(g18)
    c: Coincident(g19,g4)
    c: Coincident(g19,g8)
    c: Vertical(g19)
    c: Coincident(g20,g5)
    c: Coincident(g20,g9)
    c: Vertical(g20)
    c: Coincident(g21,g5)
    c: Coincident(g21,g9)
    c: Vertical(g21)
    c: Coincident(g22,g10)
    c: Coincident(g22,g6)
    c: Vertical(g22)
    c: Coincident(g23,g6)
    c: Coincident(g23,g10)
    c: Vertical(g23)
FEATURE [Part::Extrusion] Extrude045  label="removeToCreateFanGrillHoles003"
  Base = -> Sketch054
  Dir = (0,-1,6e-16)
  DirMode = 2
  FaceMakerClass = Part::FaceMakerBullseye
  LengthFwd = 10
  LengthRev = 0
  Placement = pos=(65.4,44,54.82) rot=(0,0,1;0rad)
  Solid = true
  Symmetric = false
FEATURE [Part::Feature] Face105 .. Face108  x4 (patterned run collapsed; names and placements below)
  shape: bbox 3.5 x 17.8 x 2e-07 mm, 1 faces, 0 solids (baked)
FEATURE [Part::Revolution] Revolve113  label="removeToCreateScrewAndThreadedInsertHole041"
  Angle = 360
  Axis = (0,1,0)
  Base = (0,0,0)
  FaceMakerClass = Part::FaceMakerBullseye
  Placement = pos=(62.3,30.3,19.7) rot=(0,0,1;0rad)
  Solid = false
  Source = -> Face105
  Symmetric = false
FEATURE [Part::Revolution] Revolve114  label="removeToCreateScrewAndThreadedInsertHole042"
  Angle = 360
  Axis = (0,1,0)
  Base = (0,0,0)
  FaceMakerClass = Part::FaceMakerBullseye
  Placement = pos=(62.3,30.3,51.7) rot=(0,0,1;0rad)
  Solid = false
  Source = -> Face106
  Symmetric = false
FEATURE [Part::Revolution] Revolve115  label="removeToCreateScrewAndThreadedInsertHole043"
  Angle = 360
  Axis = (0,1,0)
  Base = (0,0,0)
  FaceMakerClass = Part::FaceMakerBullseye
  Placement = pos=(30.3,30.3,19.7) rot=(0,0,1;0rad)
  Solid = false
  Source = -> Face107
  Symmetric = false
FEATURE [Part::Revolution] Revolve116  label="removeToCreateScrewAndThreadedInsertHole044"
  Angle = 360
  Axis = (0,1,0)
  Base = (0,0,0)
  FaceMakerClass = Part::FaceMakerBullseye
  Placement = pos=(30.3,30.3,51.7) rot=(0,0,1;0rad)
  Solid = false
  Source = -> Face108
  Symmetric = false
FEATURE [Part::MultiFuse] Fusion083  label="createThreadedInsertHolesForFan004"
  Shapes = -> [Revolve113,Revolve114,Revolve115,Revolve116]
FEATURE [Part::Box] Box024  label="removeToCreteHoleForPlugHousing026"
  AttacherType = Attacher::AttachEngine3D
  Height = 28.6
  Length = 10
  Placement = pos=(-2,0,21.7) rot=(0,0,1;0rad)
  Width = 19
FEATURE [Part::Cylinder] Cylinder038  label="removeToCreteHoleForPlugHousing027"
  Angle = 360
  AttacherType = Attacher::AttachEngine3D
  Height = 20
  Placement = pos=(-2,19,36) rot=(0,1,0;1.5708rad)
  Radius = 14.3
FEATURE [Part::MultiFuse] Fusion084  label="removeToCreteHoleForPlugHousing028"
  Shapes = -> [Box024,Cylinder038]
FEATURE [Part::Cylinder] Cylinder039
  Angle = 360
  AttacherType = Attacher::AttachEngine3D
  Height = 20
  Placement = pos=(0,0,36.15) rot=(0,0,1;0rad)
  Radius = 14.3
FEATURE [Part::Cylinder] Cylinder040
  Angle = 360
  AttacherType = Attacher::AttachEngine3D
  Height = 10
  Placement = pos=(0,0,36.15) rot=(0,0,1;0rad)
  Radius = 4
FEATURE [Part::Box] Box025  label="removeToCreteHoleForPlugHousing030"
  AttacherType = Attacher::AttachEngine3D
  Height = 28.6
  Length = 20
  Placement = pos=(106.15,0,21.7) rot=(0,0,1;0rad)
  Width = 19
FEATURE [Part::MultiFuse] Fusion086  label="removeToCreteHoleForPlugHousing031"
  Placement = pos=(70,19,36) rot=(0,1,0;1.5708rad)
  Shapes = -> [Cylinder039,Cylinder040]
FEATURE [Part::MultiFuse] Fusion085  label="removeToCreteHoleForPlugHousing029"
  Shapes = -> [Box025,Fusion086]
FEATURE [Sketcher::SketchObject] Sketch055
  FullyConstrained = true
  Placement = pos=(117,19,0) rot=(0.57735,0.57735,0.57735;2.0944rad)
  sketch-geometry (48):
    g0: LineSegment StartX=-49.19 StartY=69.25 StartZ=0 EndX=-49.19 EndY=66.25 EndZ=0
    g1: LineSegment StartX=-49.19 StartY=63.5 StartZ=0 EndX=-49.19 EndY=60.5 EndZ=0
    g2: LineSegment StartX=-49.19 StartY=57.75 StartZ=0 EndX=-49.19 EndY=54.75 EndZ=0
    g3: LineSegment StartX=-49.19 StartY=52 StartZ=0 EndX=-49.19 EndY=49 EndZ=0
    g4: LineSegment StartX=-49.19 StartY=46.25 StartZ=0 EndX=-49.19 EndY=43.25 EndZ=0
    g5: LineSegment StartX=-49.19 StartY=40.5 StartZ=0 EndX=-49.19 EndY=37.5 EndZ=0
    g6: LineSegment StartX=-49.19 StartY=34.5 StartZ=0 EndX=-49.19 EndY=31.5 EndZ=0
    g7: LineSegment StartX=-49.19 StartY=28.75 StartZ=0 EndX=-49.19 EndY=25.75 EndZ=0
    g8: LineSegment StartX=-49.19 StartY=23 StartZ=0 EndX=-49.19 EndY=20 EndZ=0
    g9: LineSegment StartX=-49.19 StartY=17.25 StartZ=0 EndX=-49.19 EndY=14.25 EndZ=0
    g10: LineSegment StartX=-49.19 StartY=11.5 StartZ=0 EndX=-49.19 EndY=8.5 EndZ=0
    g11: LineSegment StartX=-49.19 StartY=5.75 StartZ=0 EndX=-49.19 EndY=2.75 EndZ=0
    g12: ArcOfCircle CenterX=-1.5 CenterY=67.75 CenterZ=0 NormalX=0 NormalY=0 NormalZ=1 AngleXU=0 Radius=1.5 StartAngle=4.71239 EndAngle=7.85398
    g13: ArcOfCircle CenterX=-1.5 CenterY=62 CenterZ=0 NormalX=0 NormalY=0 NormalZ=1 AngleXU=0 Radius=1.5 StartAngle=4.71239 EndAngle=7.85398
    g14: ArcOfCircle CenterX=-1.5 CenterY=56.25 CenterZ=0 NormalX=0 NormalY=0 NormalZ=1 AngleXU=0 Radius=1.5 StartAngle=4.71239 EndAngle=7.85398
    g15: ArcOfCircle CenterX=-11.49 CenterY=50.5 CenterZ=0 NormalX=0 NormalY=0 NormalZ=1 AngleXU=0 Radius=1.5 StartAngle=4.71239 EndAngle=7.85398
    g16: ArcOfCircle CenterX=-16.28 CenterY=44.75 CenterZ=0 NormalX=0 NormalY=0 NormalZ=1 AngleXU=0 Radius=1.5 StartAngle=4.71239 EndAngle=7.85398
    g17: ArcOfCircle CenterX=-18.2337 CenterY=39 CenterZ=0 NormalX=0 NormalY=0 NormalZ=1 AngleXU=0 Radius=1.5 StartAngle=4.71485 EndAngle=7.85398
    g18: ArcOfCircle CenterX=-16.2837 CenterY=27.25 CenterZ=0 NormalX=0 NormalY=0 NormalZ=1 AngleXU=0 Radius=1.5 StartAngle=4.71485 EndAngle=7.85398
    g19: ArcOfCircle CenterX=-18.2337 CenterY=33 CenterZ=0 NormalX=0 NormalY=0 NormalZ=1 AngleXU=0 Radius=1.5 StartAngle=4.71485 EndAngle=7.85398
    g20: ArcOfCircle CenterX=-11.49 CenterY=21.5 CenterZ=0 NormalX=0 NormalY=0 NormalZ=1 AngleXU=0 Radius=1.5 StartAngle=4.71239 EndAngle=7.85398
    g21: ArcOfCircle CenterX=-1.5 CenterY=4.25 CenterZ=0 NormalX=0 NormalY=0 NormalZ=1 AngleXU=0 Radius=1.5 StartAngle=4.71239 EndAngle=7.85398
    g22: ArcOfCircle CenterX=-1.5 CenterY=10 CenterZ=0 NormalX=0 NormalY=0 NormalZ=1 AngleXU=0 Radius=1.5 StartAngle=4.71239 EndAngle=7.85398
    g23: ArcOfCircle CenterX=-1.5 CenterY=15.75 CenterZ=0 NormalX=0 NormalY=0 NormalZ=1 AngleXU=0 Radius=1.5 StartAngle=4.71239 EndAngle=7.85398
    g24: LineSegment StartX=-49.19 StartY=69.25 StartZ=0 EndX=-1.5 EndY=69.25 EndZ=0
    g25: LineSegment StartX=-49.19 StartY=66.25 StartZ=0 EndX=-1.5 EndY=66.25 EndZ=0
    g26: LineSegment StartX=-49.19 StartY=63.5 StartZ=0 EndX=-1.5 EndY=63.5 EndZ=0
    g27: LineSegment StartX=-49.19 StartY=60.5 StartZ=0 EndX=-1.5 EndY=60.5 EndZ=0
    g28: LineSegment StartX=-49.19 StartY=57.75 StartZ=0 EndX=-1.5 EndY=57.75 EndZ=0
    g29: LineSegment StartX=-49.19 StartY=54.75 StartZ=0 EndX=-1.5 EndY=54.75 EndZ=0
    g30: LineSegment StartX=-49.19 StartY=52 StartZ=0 EndX=-11.49 EndY=52 EndZ=0
    g31: LineSegment StartX=-49.19 StartY=49 StartZ=0 EndX=-11.49 EndY=49 EndZ=0
    g32: LineSegment StartX=-49.19 StartY=46.25 StartZ=0 EndX=-16.28 EndY=46.25 EndZ=0
    g33: LineSegment StartX=-49.19 StartY=43.25 StartZ=0 EndX=-16.28 EndY=43.25 EndZ=0
    g34: LineSegment StartX=-49.19 StartY=40.5 StartZ=0 EndX=-18.2337 EndY=40.5 EndZ=0
    g35: LineSegment StartX=-49.19 StartY=37.5 StartZ=0 EndX=-18.23 EndY=37.5 EndZ=0
    g36: LineSegment StartX=-49.19 StartY=34.5 StartZ=0 EndX=-18.2337 EndY=34.5 EndZ=0
    g37: LineSegment StartX=-49.19 StartY=31.5 StartZ=0 EndX=-18.23 EndY=31.5 EndZ=0
    g38: LineSegment StartX=-49.19 StartY=28.75 StartZ=0 EndX=-16.2837 EndY=28.75 EndZ=0
    g39: LineSegment StartX=-49.19 StartY=25.75 StartZ=0 EndX=-16.28 EndY=25.75 EndZ=0
    g40: LineSegment StartX=-49.19 StartY=23 StartZ=0 EndX=-11.49 EndY=23 EndZ=0
    g41: LineSegment StartX=-49.19 StartY=20 StartZ=0 EndX=-11.49 EndY=20 EndZ=0
    g42: LineSegment StartX=-49.19 StartY=17.25 StartZ=0 EndX=-1.5 EndY=17.25 EndZ=0
    g43: LineSegment StartX=-49.19 StartY=14.25 StartZ=0 EndX=-1.5 EndY=14.25 EndZ=0
    g44: LineSegment StartX=-49.19 StartY=11.5 StartZ=0 EndX=-1.5 EndY=11.5 EndZ=0
    g45: LineSegment StartX=-49.19 StartY=8.5 StartZ=0 EndX=-1.5 EndY=8.5 EndZ=0
    g46: LineSegment StartX=-49.19 StartY=5.75 StartZ=0 EndX=-1.5 EndY=5.75 EndZ=0
    g47: LineSegment StartX=-49.19 StartY=2.75 StartZ=0 EndX=-1.5 EndY=2.75 EndZ=0
  constraints (120):
    c: Vertical(g0)
    c: Distance(g0) = 3
    c: Block(g0)
    c: Vertical(g1)
    c: Distance(g1) = 3
    c: Vertical(g2)
    c: Equal(g0,g2) = 3
    c: Block(g2)
    c: Vertical(g3)
    c: Equal(g1,g3) = 3
    c: Vertical(g4)
    c: Equal(g0,g4) = 3
    c: Block(g4)
    c: Vertical(g5)
    c: Equal(g1,g5) = 3
    c: Vertical(g6)
    c: Equal(g0,g6) = 3
    c: Block(g6)
    c: Vertical(g7)
    c: Equal(g1,g7) = 3
    c: Vertical(g8)
    c: Equal(g0,g8) = 3
    c: Block(g8)
    c: Vertical(g9)
    c: Equal(g1,g9) = 3
    c: Vertical(g10)
    c: Equal(g0,g10) = 3
    c: Block(g10)
    c: Vertical(g11)
    c: Equal(g1,g11) = 3
    c: Block(g12)
    c: Block(g13)
    c: Block(g14)
    c: Block(g15)
    c: Block(g16)
    c: Block(g17)
    c: Block(g18)
    c: Block(g19)
    c: Block(g20)
    c: Block(g21)
    c: Block(g22)
    c: Block(g23)
    c: Block(g11)
    c: Block(g9)
    c: Block(g7)
    c: Block(g5)
    c: Block(g3)
    c: Block(g1)
    c: Coincident(g24,g0)
    c: Coincident(g24,g12)
    c: Horizontal(g24)
    c: Coincident(g25,g0)
    c: Coincident(g25,g12)
    c: Horizontal(g25)
    c: Coincident(g26,g1)
    c: Coincident(g26,g13)
    c: Horizontal(g26)
    c: Coincident(g27,g1)
    c: Coincident(g27,g13)
    c: Horizontal(g27)
    c: Coincident(g28,g2)
    c: Coincident(g28,g14)
    c: Horizontal(g28)
    c: Coincident(g29,g2)
    c: Coincident(g29,g14)
    c: Horizontal(g29)
    c: Coincident(g30,g3)
    c: Coincident(g30,g15)
    c: Horizontal(g30)
    c: Coincident(g31,g3)
    c: Coincident(g31,g15)
    c: Horizontal(g31)
    c: Coincident(g32,g4)
    c: Coincident(g32,g16)
    c: Horizontal(g32)
    c: Coincident(g33,g4)
    c: Coincident(g33,g16)
    c: Horizontal(g33)
    c: Coincident(g34,g5)
    c: Coincident(g34,g17)
    c: Horizontal(g34)
    c: Coincident(g35,g5)
    c: Coincident(g35,g17)
    c: Horizontal(g35)
    c: Coincident(g36,g6)
    c: Coincident(g36,g19)
    c: Horizontal(g36)
    c: Coincident(g37,g6)
    c: Coincident(g37,g19)
    c: Horizontal(g37)
    c: Coincident(g38,g7)
    c: Coincident(g38,g18)
    c: Horizontal(g38)
    c: Coincident(g39,g7)
    c: Coincident(g39,g18)
    c: Horizontal(g39)
    c: Coincident(g40,g8)
    c: Coincident(g40,g20)
    c: Horizontal(g40)
    c: Coincident(g41,g8)
    c: Coincident(g41,g20)
    c: Horizontal(g41)
    c: Coincident(g42,g9)
    c: Coincident(g42,g23)
    c: Horizontal(g42)
    c: Coincident(g43,g9)
    c: Coincident(g43,g23)
    c: Horizontal(g43)
    c: Coincident(g44,g10)
    c: Coincident(g44,g22)
    c: Horizontal(g44)
    c: Coincident(g45,g10)
    c: Coincident(g45,g22)
    c: Horizontal(g45)
    c: Coincident(g46,g11)
    c: Coincident(g46,g21)
    c: Horizontal(g46)
    c: Coincident(g47,g11)
    c: Coincident(g47,g21)
    c: Horizontal(g47)
FEATURE [Part::Extrusion] Extrude046
  Base = -> Sketch055
  Dir = (1,0,0)
  DirMode = 2
  FaceMakerClass = Part::FaceMakerBullseye
  LengthFwd = 23
  LengthRev = 0
  Placement = pos=(-19,0,0) rot=(0,0,1;0rad)
  Solid = true
  Symmetric = false
FEATURE [Part::Fillet] Fillet038  label="removeToCreateVentalationHoles001"
  Base = -> Extrude046
  Edges = <same value as first occurrence — deduplicated (x6 in doc)>
  Placement = pos=(7,0,0) rot=(0,0,1;0rad)
FEATURE [Sketcher::SketchObject] Sketch056  label="topSketch014"
  FullyConstrained = true
  sketch-geometry (22):
    g0: LineSegment StartX=5.21097e-06 StartY=3 StartZ=0 EndX=5.21097e-06 EndY=19 EndZ=0
    g1: ArcOfCircle CenterX=19 CenterY=19 CenterZ=0 NormalX=0 NormalY=0 NormalZ=1 AngleXU=0 Radius=19 StartAngle=1.5708 EndAngle=3.14159
    g2: ArcOfCircle CenterX=19 CenterY=19 CenterZ=0 NormalX=0 NormalY=0 NormalZ=1 AngleXU=0 Radius=16 StartAngle=1.5708 EndAngle=3.14159
    g3: LineSegment StartX=114 StartY=35 StartZ=0 EndX=19 EndY=35 EndZ=0
    g4: LineSegment StartX=5.21097e-06 StartY=3 StartZ=0 EndX=5.21097e-06 EndY=0 EndZ=0
    g5: LineSegment StartX=3 StartY=0 StartZ=0 EndX=5.21097e-06 EndY=0 EndZ=0
    g6: LineSegment StartX=3 StartY=19 StartZ=0 EndX=3 EndY=0 EndZ=0
    g7: LineSegment StartX=19 StartY=38 StartZ=0 EndX=124 EndY=38 EndZ=0
    g8: Circle CenterX=119 CenterY=35 CenterZ=0 NormalX=0 NormalY=0 NormalZ=1 AngleXU=0 Radius=1
    g9: Circle CenterX=121 CenterY=35 CenterZ=0 NormalX=0 NormalY=0 NormalZ=1 AngleXU=0 Radius=1
    g10: Circle CenterX=121 CenterY=33 CenterZ=0 NormalX=0 NormalY=0 NormalZ=1 AngleXU=0 Radius=1
    g11: BSplineCurve PolesCount=3 KnotsCount=2 Degree=2 IsPeriodic=0
    g12: GeomPoint X=119 Y=35 Z=0
    g13: GeomPoint X=121 Y=33 Z=0
    g14: LineSegment StartX=119 StartY=35 StartZ=0 EndX=114 EndY=35 EndZ=0
    g15: ArcOfCircle CenterX=105 CenterY=19 CenterZ=0 NormalX=0 NormalY=0 NormalZ=1 AngleXU=0 Radius=16 StartAngle=5.60905 EndAngle=6.28319
    g16: LineSegment StartX=121 StartY=33 StartZ=0 EndX=121 EndY=19 EndZ=0
    g17: LineSegment StartX=117.5 StartY=9.01251 StartZ=0 EndX=121.163 EndY=9.0125 EndZ=0
    g18: ArcOfCircle CenterX=105 CenterY=19 CenterZ=0 NormalX=0 NormalY=0 NormalZ=1 AngleXU=0 Radius=20.6155 StartAngle=5.7297 EndAngle=6.28319
    g19: LineSegment StartX=121.163 StartY=9.0125 StartZ=0 EndX=122.538 EndY=8.16329 EndZ=0
    g20: LineSegment StartX=124 StartY=38 StartZ=0 EndX=125.616 EndY=38 EndZ=0
    g21: LineSegment StartX=125.616 StartY=19 StartZ=0 EndX=125.616 EndY=38 EndZ=0
  constraints (49):
    c: Vertical(g0)
    c: Block(g0)
    c: Coincident(g1,g0)
    c: Block(g1)
    c: Coincident(g2,g1)
    c: Block(g2)
    c: Coincident(g3,g2)
    c: Horizontal(g3)
    c: Tangent(g3,g2)
    c: Coincident(g4,g0)
    c: Distance(g4) = 3
    c: Vertical(g4)
    c: Coincident(g5,g4)
    c: Horizontal(g5)
    c: Coincident(g6,g2)
    c: Coincident(g6,g5)
    c: Vertical(g6)
    c: Horizontal(g7)
    c: Distance(g7) = 105
    c: Coincident(g7,g1)
    c: Block(g3)
    c: Weight(g8) = 1
    c: Equal(g8,g9)
    c: Equal(g8,g10)
    c: InternalAlignment(g8,g11)
    c: InternalAlignment(g9,g11)
    c: InternalAlignment(g10,g11)
    c: InternalAlignment(g12,g11)
    c: InternalAlignment(g13,g11)
    c: Block(g11)
    c: Coincident(g14,g11)
    c: Coincident(g14,g3)
    c: Horizontal(g14)
    c: Block(g15)
    c: Coincident(g16,g11)
    c: Coincident(g16,g15)
    c: Vertical(g16)
    c: Distance(g16) = 14
    c: Coincident(g17,g15)
    c: Block(g18)
    c: Coincident(g19,g18)
    c: Coincident(g20,g7)
    c: Horizontal(g20)
    c: Vertical(g21)
    c: Coincident(g20,g21)
    c: Block(g20)
    c: Block(g21)
    c: Block(g19)
    c: Block(g17)
FEATURE [Part::Box] Box026  label="removeToCreteHoleForPlugHousing032"
  AttacherType = Attacher::AttachEngine3D
  Height = 28.6
  Length = 10
  Placement = pos=(-2,0,21.7) rot=(0,0,1;0rad)
  Width = 19
FEATURE [Part::Feature] Face109 .. Face112  x4 (patterned run collapsed; names and placements below)
  shape: bbox 3.5 x 17.8 x 2e-07 mm, 1 faces, 0 solids (baked)
FEATURE [Part::Revolution] Revolve117  label="removeToCreateScrewAndThreadedInsertHole045"
  Angle = 360
  Axis = (0,1,0)
  Base = (0,0,0)
  FaceMakerClass = Part::FaceMakerBullseye
  Placement = pos=(62.3,30.3,19.7) rot=(0,0,1;0rad)
  Solid = false
  Source = -> Face109
  Symmetric = false
FEATURE [Part::Revolution] Revolve118  label="removeToCreateScrewAndThreadedInsertHole046"
  Angle = 360
  Axis = (0,1,0)
  Base = (0,0,0)
  FaceMakerClass = Part::FaceMakerBullseye
  Placement = pos=(62.3,30.3,51.7) rot=(0,0,1;0rad)
  Solid = false
  Source = -> Face110
  Symmetric = false
FEATURE [Part::Revolution] Revolve119  label="removeToCreateScrewAndThreadedInsertHole047"
  Angle = 360
  Axis = (0,1,0)
  Base = (0,0,0)
  FaceMakerClass = Part::FaceMakerBullseye
  Placement = pos=(30.3,30.3,19.7) rot=(0,0,1;0rad)
  Solid = false
  Source = -> Face111
  Symmetric = false
FEATURE [Part::Revolution] Revolve120  label="removeToCreateScrewAndThreadedInsertHole048"
  Angle = 360
  Axis = (0,1,0)
  Base = (0,0,0)
  FaceMakerClass = Part::FaceMakerBullseye
  Placement = pos=(30.3,30.3,51.7) rot=(0,0,1;0rad)
  Solid = false
  Source = -> Face112
  Symmetric = false
FEATURE [Part::MultiFuse] Fusion087  label="createThreadedInsertHolesForFan005"
  Shapes = -> [Revolve117,Revolve118,Revolve119,Revolve120]
FEATURE [Part::Extrusion] Extrude047
  Base = -> Sketch056
  Dir = (0,0,1)
  DirMode = 2
  FaceMakerClass = Part::FaceMakerBullseye
  LengthFwd = 72
  LengthRev = 0
  Solid = true
  Symmetric = false
FEATURE [Part::Fillet] Fillet039  label="top019"
  Base = -> Extrude047
  Edges = 1 edges r=2: [Edge35]
FEATURE [Sketcher::SketchObject] Sketch057
  FullyConstrained = false
  Placement = pos=(0,0,0) rot=(1,0,0;1.5708rad)
  sketch-geometry (24):
    g0: ArcOfCircle CenterX=-4 CenterY=-10.5 CenterZ=0 NormalX=0 NormalY=0 NormalZ=1 AngleXU=0 Radius=1.5 StartAngle=6e-16 EndAngle=3.14159
    g1: ArcOfCircle CenterX=-34.2 CenterY=-10.5 CenterZ=0 NormalX=0 NormalY=0 NormalZ=1 AngleXU=0 Radius=1.5 StartAngle=0 EndAngle=3.14159
    g2: ArcOfCircle CenterX=-34.2 CenterY=-27.7 CenterZ=0 NormalX=0 NormalY=0 NormalZ=1 AngleXU=0 Radius=1.5 StartAngle=3.14159 EndAngle=6.28319
    g3: ArcOfCircle CenterX=-4 CenterY=-27.7 CenterZ=0 NormalX=0 NormalY=0 NormalZ=1 AngleXU=0 Radius=1.5 StartAngle=3.1416 EndAngle=6.28319
    g4: ArcOfCircle CenterX=-10 CenterY=-4.3 CenterZ=0 NormalX=0 NormalY=0 NormalZ=1 AngleXU=0 Radius=1.5 StartAngle=2e-16 EndAngle=3.14159
    g5: ArcOfCircle CenterX=-16.1 CenterY=-1.8 CenterZ=0 NormalX=0 NormalY=0 NormalZ=1 AngleXU=0 Radius=1.5 StartAngle=5e-16 EndAngle=3.14159
    g6: ArcOfCircle CenterX=-22.1 CenterY=-1.8 CenterZ=0 NormalX=0 NormalY=0 NormalZ=1 AngleXU=0 Radius=1.5 StartAngle=5e-16 EndAngle=3.14159
    g7: ArcOfCircle CenterX=-28.2 CenterY=-4.3 CenterZ=0 NormalX=0 NormalY=0 NormalZ=1 AngleXU=0 Radius=1.5 StartAngle=2e-16 EndAngle=3.14159
    g8: ArcOfCircle CenterX=-10 CenterY=-33.9 CenterZ=0 NormalX=0 NormalY=0 NormalZ=1 AngleXU=0 Radius=1.5 StartAngle=3.14159 EndAngle=6.28319
    g9: ArcOfCircle CenterX=-16.1 CenterY=-36.4 CenterZ=0 NormalX=0 NormalY=0 NormalZ=1 AngleXU=0 Radius=1.5 StartAngle=3.14159 EndAngle=6.28319
    g10: ArcOfCircle CenterX=-22.1 CenterY=-36.4 CenterZ=0 NormalX=0 NormalY=0 NormalZ=1 AngleXU=0 Radius=1.5 StartAngle=3.14159 EndAngle=6.28319
    g11: ArcOfCircle CenterX=-28.2 CenterY=-33.9 CenterZ=0 NormalX=0 NormalY=0 NormalZ=1 AngleXU=0 Radius=1.5 StartAngle=3.14159 EndAngle=6.28319
    g12: LineSegment StartX=-35.7 StartY=-10.5 StartZ=0 EndX=-35.7 EndY=-27.7 EndZ=0
    g13: LineSegment StartX=-32.7 StartY=-10.5 StartZ=0 EndX=-32.7 EndY=-27.7 EndZ=0
    g14: LineSegment StartX=-29.7 StartY=-33.9 StartZ=0 EndX=-29.7 EndY=-4.3 EndZ=0
    g15: LineSegment StartX=-26.7 StartY=-33.9 StartZ=0 EndX=-26.7 EndY=-4.3 EndZ=0
    g16: LineSegment StartX=-2.5 StartY=-10.5 StartZ=0 EndX=-2.5 EndY=-27.7 EndZ=0
    g17: LineSegment StartX=-8.5 StartY=-4.3 StartZ=0 EndX=-8.5 EndY=-33.9 EndZ=0
    g18: LineSegment StartX=-5.5 StartY=-10.5 StartZ=0 EndX=-5.5 EndY=-27.7 EndZ=0
    g19: LineSegment StartX=-11.5 StartY=-4.3 StartZ=0 EndX=-11.5 EndY=-33.9 EndZ=0
    g20: LineSegment StartX=-14.6 StartY=-1.8 StartZ=0 EndX=-14.6 EndY=-36.4 EndZ=0
    g21: LineSegment StartX=-17.6 StartY=-1.8 StartZ=0 EndX=-17.6 EndY=-36.4 EndZ=0
    g22: LineSegment StartX=-20.6 StartY=-36.4 StartZ=0 EndX=-20.6 EndY=-1.8 EndZ=0
    g23: LineSegment StartX=-23.6 StartY=-1.8 StartZ=0 EndX=-23.6 EndY=-36.4 EndZ=0
  constraints (48):
    c: Block(g0)
    c: Block(g1)
    c: Block(g2)
    c: Block(g3)
    c: Block(g4)
    c: Block(g5)
    c: Block(g6)
    c: Block(g7)
    c: Block(g8)
    c: Block(g9)
    c: Block(g10)
    c: Block(g11)
    c: Coincident(g12,g1)
    c: Coincident(g12,g2)
    c: Vertical(g12)
    c: Coincident(g13,g1)
    c: Coincident(g13,g2)
    c: Vertical(g13)
    c: Coincident(g14,g11)
    c: Coincident(g14,g7)
    c: Vertical(g14)
    c: Coincident(g15,g11)
    c: Coincident(g15,g7)
    c: Vertical(g15)
    c: Coincident(g16,g0)
    c: Coincident(g16,g3)
    c: Vertical(g16)
    c: Coincident(g17,g4)
    c: Coincident(g17,g8)
    c: Vertical(g17)
    c: Coincident(g18,g0)
    c: Coincident(g18,g3)
    c: Vertical(g18)
    c: Coincident(g19,g4)
    c: Coincident(g19,g8)
    c: Vertical(g19)
    c: Coincident(g20,g5)
    c: Coincident(g20,g9)
    c: Vertical(g20)
    c: Coincident(g21,g5)
    c: Coincident(g21,g9)
    c: Vertical(g21)
    c: Coincident(g22,g10)
    c: Coincident(g22,g6)
    c: Vertical(g22)
    c: Coincident(g23,g6)
    c: Coincident(g23,g10)
    c: Vertical(g23)
FEATURE [Part::Extrusion] Extrude048  label="removeToCreateFanGrillHoles004"
  Base = -> Sketch057
  Dir = (0,-1,6e-16)
  DirMode = 2
  FaceMakerClass = Part::FaceMakerBullseye
  LengthFwd = 10
  LengthRev = 0
  Placement = pos=(65.4,44,54.82) rot=(0,0,1;0rad)
  Solid = true
  Symmetric = false
FEATURE [Part::Cut] Cut040  label="top021"
  Base = -> Fillet039
  Tool = -> Extrude048
FEATURE [Part::Cylinder] Cylinder041  label="removeToCreteHoleForPlugHousing034"
  Angle = 360
  AttacherType = Attacher::AttachEngine3D
  Height = 20
  Placement = pos=(-2,19,36) rot=(0,1,0;1.5708rad)
  Radius = 14.3
FEATURE [Part::MultiFuse] Fusion089  label="removeToCreteHoleForPlugHousing035"
  Shapes = -> [Box026,Cylinder041]
FEATURE [Part::Cylinder] Cylinder042
  Angle = 360
  AttacherType = Attacher::AttachEngine3D
  Height = 20
  Placement = pos=(0,0,36.15) rot=(0,0,1;0rad)
  Radius = 14.3
FEATURE [Part::Cylinder] Cylinder043
  Angle = 360
  AttacherType = Attacher::AttachEngine3D
  Height = 10
  Placement = pos=(0,0,36.15) rot=(0,0,1;0rad)
  Radius = 4
FEATURE [Part::Box] Box027  label="removeToCreteHoleForPlugHousing036"
  AttacherType = Attacher::AttachEngine3D
  Height = 28.6
  Length = 20
  Placement = pos=(106.15,0,21.7) rot=(0,0,1;0rad)
  Width = 19
FEATURE [Part::Cut] Cut041  label="top022"
  Base = -> Cut040
  Tool = -> Fusion087
FEATURE [Part::Cut] Cut039  label="top020"
  Base = -> Cut041
  Tool = -> Fusion089
FEATURE [Part::MultiFuse] Fusion090  label="removeToCreteHoleForPlugHousing037"
  Placement = pos=(70,19,36) rot=(0,1,0;1.5708rad)
  Shapes = -> [Cylinder042,Cylinder043]
FEATURE [Part::MultiFuse] Fusion088  label="removeToCreteHoleForPlugHousing033"
  Shapes = -> [Box027,Fusion090]
FEATURE [Part::Cut] Cut042  label="removeToCreteHoleForPlugHousing038"
  Base = -> Cut039
  Tool = -> Fusion088
FEATURE [Part::MultiFuse] Fusion091  label="removeFromTop"
  Shapes = -> [Fillet038,Fusion085,Fusion084,Fusion083,Extrude045]
FEATURE [Part::Cut] Cut043  label="REAL TOP ====="
  Base = -> Fillet036
  Tool = -> Fusion091
FEATURE [Part::MultiFuse] Fusion092  label="caseScrewPillarBracket016"
  Shapes = -> [Extrude030,Extrude031,Extrude032,Extrude033,Extrude034,Extrude035,Extrude036,Extrude037,Box013,Box014]
FEATURE [Sketcher::SketchObject] Sketch058  label="topSketch015"
  FullyConstrained = true
  sketch-geometry (20):
    g0: LineSegment StartX=5.21097e-06 StartY=3 StartZ=0 EndX=5.21097e-06 EndY=19 EndZ=0
    g1: ArcOfCircle CenterX=19 CenterY=19 CenterZ=0 NormalX=0 NormalY=0 NormalZ=1 AngleXU=0 Radius=19 StartAngle=1.5708 EndAngle=3.14159
    g2: ArcOfCircle CenterX=19 CenterY=19 CenterZ=0 NormalX=0 NormalY=0 NormalZ=1 AngleXU=0 Radius=16 StartAngle=1.5708 EndAngle=3.14159
    g3: LineSegment StartX=114 StartY=35 StartZ=0 EndX=19 EndY=35 EndZ=0
    g4: LineSegment StartX=5.21097e-06 StartY=3 StartZ=0 EndX=5.21097e-06 EndY=0 EndZ=0
    g5: LineSegment StartX=3 StartY=0 StartZ=0 EndX=5.21097e-06 EndY=0 EndZ=0
    g6: LineSegment StartX=3 StartY=19 StartZ=0 EndX=3 EndY=0 EndZ=0
    g7: LineSegment StartX=19 StartY=38 StartZ=0 EndX=124 EndY=38 EndZ=0
    g8: Circle CenterX=119 CenterY=35 CenterZ=0 NormalX=0 NormalY=0 NormalZ=1 AngleXU=0 Radius=1
    g9: Circle CenterX=121 CenterY=35 CenterZ=0 NormalX=0 NormalY=0 NormalZ=1 AngleXU=0 Radius=1
    g10: Circle CenterX=121 CenterY=33 CenterZ=0 NormalX=0 NormalY=0 NormalZ=1 AngleXU=0 Radius=1
    g11: BSplineCurve PolesCount=3 KnotsCount=2 Degree=2 IsPeriodic=0
    g12: GeomPoint X=119 Y=35 Z=0
    g13: GeomPoint X=121 Y=33 Z=0
    g14: LineSegment StartX=119 StartY=35 StartZ=0 EndX=114 EndY=35 EndZ=0
    g15: ArcOfCircle CenterX=105 CenterY=19 CenterZ=0 NormalX=0 NormalY=0 NormalZ=1 AngleXU=0 Radius=19 StartAngle=5.7297 EndAngle=6.28319
    g16: ArcOfCircle CenterX=105 CenterY=19 CenterZ=0 NormalX=0 NormalY=0 NormalZ=1 AngleXU=0 Radius=16 StartAngle=5.60905 EndAngle=6.28319
    g17: LineSegment StartX=121 StartY=33 StartZ=0 EndX=121 EndY=19 EndZ=0
    g18: LineSegment StartX=124 StartY=38 StartZ=0 EndX=124 EndY=19 EndZ=0
    g19: LineSegment StartX=117.5 StartY=9.01251 StartZ=0 EndX=121.163 EndY=9.0125 EndZ=0
  constraints (46):
    c: Vertical(g0)
    c: Block(g0)
    c: Coincident(g1,g0)
    c: Block(g1)
    c: Coincident(g2,g1)
    c: Block(g2)
    c: Coincident(g3,g2)
    c: Horizontal(g3)
    c: Tangent(g3,g2)
    c: Coincident(g4,g0)
    c: Distance(g4) = 3
    c: Vertical(g4)
    c: Coincident(g5,g4)
    c: Horizontal(g5)
    c: Coincident(g6,g2)
    c: Coincident(g6,g5)
    c: Vertical(g6)
    c: Horizontal(g7)
    c: Distance(g7) = 105
    c: Coincident(g7,g1)
    c: Block(g3)
    c: Weight(g8) = 1
    c: Equal(g8,g9)
    c: Equal(g8,g10)
    c: InternalAlignment(g8,g11)
    c: InternalAlignment(g9,g11)
    c: InternalAlignment(g10,g11)
    c: InternalAlignment(g12,g11)
    c: InternalAlignment(g13,g11)
    c: Block(g11)
    c: Coincident(g14,g11)
    c: Coincident(g14,g3)
    c: Horizontal(g14)
    c: Block(g15)
    c: Coincident(g16,g15)
    c: Block(g16)
    c: Coincident(g17,g11)
    c: Coincident(g17,g16)
    c: Vertical(g17)
    c: Distance(g17) = 14
    c: Coincident(g18,g7)
    c: Coincident(g18,g15)
    c: Vertical(g18)
    c: Distance(g18) = 19
    c: Coincident(g19,g16)
    c: Coincident(g19,g15)
FEATURE [Part::Extrusion] Extrude049  label="top023"
  Base = -> Sketch058
  Dir = (0,0,1)
  DirMode = 2
  FaceMakerClass = Part::FaceMakerBullseye
  LengthFwd = 72
  LengthRev = 0
  Solid = true
  Symmetric = false
FEATURE [Sketcher::SketchObject] Sketch059
  FullyConstrained = true
  MapMode = 3
  Placement = pos=(0,0,0) rot=(1,0,0;1.5708rad)
  Support = -> [Extrude049]
  sketch-geometry (8):
    g0: Circle CenterX=80.351 CenterY=-67.6202 CenterZ=0 NormalX=0 NormalY=0 NormalZ=1 AngleXU=0 Radius=2
    g1: Circle CenterX=80.351 CenterY=-67.6202 CenterZ=0 NormalX=0 NormalY=0 NormalZ=1 AngleXU=0 Radius=3
    g2: Circle CenterX=80.351 CenterY=-4.92017 CenterZ=0 NormalX=0 NormalY=0 NormalZ=1 AngleXU=0 Radius=2
    g3: Circle CenterX=80.351 CenterY=-4.92017 CenterZ=0 NormalX=0 NormalY=0 NormalZ=1 AngleXU=0 Radius=3
    g4: Circle CenterX=23.851 CenterY=-4.92017 CenterZ=0 NormalX=0 NormalY=0 NormalZ=1 AngleXU=0 Radius=2
    g5: Circle CenterX=23.851 CenterY=-4.92017 CenterZ=0 NormalX=0 NormalY=0 NormalZ=1 AngleXU=0 Radius=3
    g6: Circle CenterX=23.851 CenterY=-67.6202 CenterZ=0 NormalX=0 NormalY=0 NormalZ=1 AngleXU=0 Radius=2
    g7: Circle CenterX=23.851 CenterY=-67.6202 CenterZ=0 NormalX=0 NormalY=0 NormalZ=1 AngleXU=0 Radius=3
  constraints (8):
    c: Block(g3)
    c: Block(g2)
    c: Block(g1)
    c: Block(g0)
    c: Block(g6)
    c: Block(g7)
    c: Block(g4)
    c: Block(g5)
FEATURE [Sketcher::SketchObject] Sketch060
  FullyConstrained = true
  MapMode = 3
  Placement = pos=(0,0,0) rot=(1,0,0;1.5708rad)
  Support = -> [Extrude049]
  sketch-geometry (8):
    g0: Circle CenterX=80.351 CenterY=-67.6202 CenterZ=0 NormalX=0 NormalY=0 NormalZ=1 AngleXU=0 Radius=3
    g1: Circle CenterX=80.351 CenterY=-4.92017 CenterZ=0 NormalX=0 NormalY=0 NormalZ=1 AngleXU=0 Radius=3
    g2: Circle CenterX=23.851 CenterY=-4.92017 CenterZ=0 NormalX=0 NormalY=0 NormalZ=1 AngleXU=0 Radius=3
    g3: Circle CenterX=23.851 CenterY=-67.6202 CenterZ=0 NormalX=0 NormalY=0 NormalZ=1 AngleXU=0 Radius=3
    g4: Circle CenterX=23.851 CenterY=-67.6202 CenterZ=0 NormalX=0 NormalY=0 NormalZ=1 AngleXU=0 Radius=5
    g5: Circle CenterX=80.351 CenterY=-67.6202 CenterZ=0 NormalX=0 NormalY=0 NormalZ=1 AngleXU=0 Radius=5
    g6: Circle CenterX=23.851 CenterY=-4.92017 CenterZ=0 NormalX=0 NormalY=0 NormalZ=1 AngleXU=0 Radius=5
    g7: Circle CenterX=80.351 CenterY=-4.92017 CenterZ=0 NormalX=0 NormalY=0 NormalZ=1 AngleXU=0 Radius=5
  constraints (8):
    c: Block(g1)
    c: Block(g0)
    c: Block(g3)
    c: Block(g2)
    c: Block(g5)
    c: Block(g4)
    c: Block(g6)
    c: Block(g7)
FEATURE [Sketcher::SketchObject] Sketch061
  FullyConstrained = true
  MapMode = 3
  Placement = pos=(0,0,0) rot=(1,0,0;1.5708rad)
  sketch-geometry (8):
    g0: Circle CenterX=80.351 CenterY=-67.6202 CenterZ=0 NormalX=0 NormalY=0 NormalZ=1 AngleXU=0 Radius=3
    g1: Circle CenterX=80.351 CenterY=-4.92017 CenterZ=0 NormalX=0 NormalY=0 NormalZ=1 AngleXU=0 Radius=3
    g2: Circle CenterX=23.851 CenterY=-4.92017 CenterZ=0 NormalX=0 NormalY=0 NormalZ=1 AngleXU=0 Radius=3
    g3: Circle CenterX=23.851 CenterY=-67.6202 CenterZ=0 NormalX=0 NormalY=0 NormalZ=1 AngleXU=0 Radius=3
    g4: Circle CenterX=23.851 CenterY=-67.6202 CenterZ=0 NormalX=0 NormalY=0 NormalZ=1 AngleXU=0 Radius=5
    g5: Circle CenterX=80.351 CenterY=-67.6202 CenterZ=0 NormalX=0 NormalY=0 NormalZ=1 AngleXU=0 Radius=5
    g6: Circle CenterX=23.851 CenterY=-4.92017 CenterZ=0 NormalX=0 NormalY=0 NormalZ=1 AngleXU=0 Radius=5
    g7: Circle CenterX=80.351 CenterY=-4.92017 CenterZ=0 NormalX=0 NormalY=0 NormalZ=1 AngleXU=0 Radius=5
  constraints (8):
    c: Block(g1)
    c: Block(g0)
    c: Block(g3)
    c: Block(g2)
    c: Block(g5)
    c: Block(g4)
    c: Block(g6)
    c: Block(g7)
FEATURE [Sketcher::SketchObject] Sketch062  label="topSketch016"
  FullyConstrained = true
  sketch-geometry (20):
    g0: LineSegment StartX=5.21097e-06 StartY=3 StartZ=0 EndX=5.21097e-06 EndY=19 EndZ=0
    g1: ArcOfCircle CenterX=19 CenterY=19 CenterZ=0 NormalX=0 NormalY=0 NormalZ=1 AngleXU=0 Radius=19 StartAngle=1.5708 EndAngle=3.14159
    g2: ArcOfCircle CenterX=19 CenterY=19 CenterZ=0 NormalX=0 NormalY=0 NormalZ=1 AngleXU=0 Radius=16 StartAngle=1.5708 EndAngle=3.14159
    g3: LineSegment StartX=114 StartY=35 StartZ=0 EndX=19 EndY=35 EndZ=0
    g4: LineSegment StartX=5.21097e-06 StartY=3 StartZ=0 EndX=5.21097e-06 EndY=0 EndZ=0
    g5: LineSegment StartX=3 StartY=0 StartZ=0 EndX=5.21097e-06 EndY=0 EndZ=0
    g6: LineSegment StartX=3 StartY=19 StartZ=0 EndX=3 EndY=0 EndZ=0
    g7: LineSegment StartX=19 StartY=38 StartZ=0 EndX=124 EndY=38 EndZ=0
    g8: Circle CenterX=119 CenterY=35 CenterZ=0 NormalX=0 NormalY=0 NormalZ=1 AngleXU=0 Radius=1
    g9: Circle CenterX=121 CenterY=35 CenterZ=0 NormalX=0 NormalY=0 NormalZ=1 AngleXU=0 Radius=1
    g10: Circle CenterX=121 CenterY=33 CenterZ=0 NormalX=0 NormalY=0 NormalZ=1 AngleXU=0 Radius=1
    g11: BSplineCurve PolesCount=3 KnotsCount=2 Degree=2 IsPeriodic=0
    g12: GeomPoint X=119 Y=35 Z=0
    g13: GeomPoint X=121 Y=33 Z=0
    g14: LineSegment StartX=119 StartY=35 StartZ=0 EndX=114 EndY=35 EndZ=0
    g15: ArcOfCircle CenterX=105 CenterY=19 CenterZ=0 NormalX=0 NormalY=0 NormalZ=1 AngleXU=0 Radius=19 StartAngle=5.7297 EndAngle=6.28319
    g16: ArcOfCircle CenterX=105 CenterY=19 CenterZ=0 NormalX=0 NormalY=0 NormalZ=1 AngleXU=0 Radius=16 StartAngle=5.60905 EndAngle=6.28319
    g17: LineSegment StartX=121 StartY=33 StartZ=0 EndX=121 EndY=19 EndZ=0
    g18: LineSegment StartX=124 StartY=38 StartZ=0 EndX=124 EndY=19 EndZ=0
    g19: LineSegment StartX=117.5 StartY=9.01251 StartZ=0 EndX=121.163 EndY=9.0125 EndZ=0
  constraints (46):
    c: Vertical(g0)
    c: Block(g0)
    c: Coincident(g1,g0)
    c: Block(g1)
    c: Coincident(g2,g1)
    c: Block(g2)
    c: Coincident(g3,g2)
    c: Horizontal(g3)
    c: Tangent(g3,g2)
    c: Coincident(g4,g0)
    c: Distance(g4) = 3
    c: Vertical(g4)
    c: Coincident(g5,g4)
    c: Horizontal(g5)
    c: Coincident(g6,g2)
    c: Coincident(g6,g5)
    c: Vertical(g6)
    c: Horizontal(g7)
    c: Distance(g7) = 105
    c: Coincident(g7,g1)
    c: Block(g3)
    c: Weight(g8) = 1
    c: Equal(g8,g9)
    c: Equal(g8,g10)
    c: InternalAlignment(g8,g11)
    c: InternalAlignment(g9,g11)
    c: InternalAlignment(g10,g11)
    c: InternalAlignment(g12,g11)
    c: InternalAlignment(g13,g11)
    c: Block(g11)
    c: Coincident(g14,g11)
    c: Coincident(g14,g3)
    c: Horizontal(g14)
    c: Block(g15)
    c: Coincident(g16,g15)
    c: Block(g16)
    c: Coincident(g17,g11)
    c: Coincident(g17,g16)
    c: Vertical(g17)
    c: Distance(g17) = 14
    c: Coincident(g18,g7)
    c: Coincident(g18,g15)
    c: Vertical(g18)
    c: Distance(g18) = 19
    c: Coincident(g19,g16)
    c: Coincident(g19,g15)
FEATURE [Part::Extrusion] Extrude053  label="top024"
  Base = -> Sketch062
  Dir = (0,0,1)
  DirMode = 2
  FaceMakerClass = Part::FaceMakerBullseye
  LengthFwd = 72
  LengthRev = 0
  Solid = true
  Symmetric = false
FEATURE [Sketcher::SketchObject] Sketch063
  FullyConstrained = true
  MapMode = 3
  Placement = pos=(0,0,0) rot=(1,0,0;1.5708rad)
  Support = -> [Extrude053]
  sketch-geometry (8):
    g0: Circle CenterX=80.351 CenterY=-67.6202 CenterZ=0 NormalX=0 NormalY=0 NormalZ=1 AngleXU=0 Radius=2
    g1: Circle CenterX=80.351 CenterY=-67.6202 CenterZ=0 NormalX=0 NormalY=0 NormalZ=1 AngleXU=0 Radius=3
    g2: Circle CenterX=80.351 CenterY=-4.92017 CenterZ=0 NormalX=0 NormalY=0 NormalZ=1 AngleXU=0 Radius=2
    g3: Circle CenterX=80.351 CenterY=-4.92017 CenterZ=0 NormalX=0 NormalY=0 NormalZ=1 AngleXU=0 Radius=3
    g4: Circle CenterX=23.851 CenterY=-4.92017 CenterZ=0 NormalX=0 NormalY=0 NormalZ=1 AngleXU=0 Radius=2
    g5: Circle CenterX=23.851 CenterY=-4.92017 CenterZ=0 NormalX=0 NormalY=0 NormalZ=1 AngleXU=0 Radius=3
    g6: Circle CenterX=23.851 CenterY=-67.6202 CenterZ=0 NormalX=0 NormalY=0 NormalZ=1 AngleXU=0 Radius=2
    g7: Circle CenterX=23.851 CenterY=-67.6202 CenterZ=0 NormalX=0 NormalY=0 NormalZ=1 AngleXU=0 Radius=3
  constraints (8):
    c: Block(g3)
    c: Block(g2)
    c: Block(g1)
    c: Block(g0)
    c: Block(g6)
    c: Block(g7)
    c: Block(g4)
    c: Block(g5)
FEATURE [Part::Extrusion] Extrude054
  Base = -> Sketch063
  Dir = (0,-1,2e-16)
  DirMode = 2
  FaceMakerClass = Part::FaceMakerBullseye
  LengthFwd = 6
  LengthRev = 0
  Placement = pos=(0,9,0) rot=(0,0,1;0rad)
  Solid = true
  Symmetric = false
FEATURE [Sketcher::SketchObject] Sketch064  label="topSketch017"
  FullyConstrained = true
  sketch-geometry (20):
    g0: LineSegment StartX=5.21097e-06 StartY=3 StartZ=0 EndX=5.21097e-06 EndY=19 EndZ=0
    g1: ArcOfCircle CenterX=19 CenterY=19 CenterZ=0 NormalX=0 NormalY=0 NormalZ=1 AngleXU=0 Radius=19 StartAngle=1.5708 EndAngle=3.14159
    g2: ArcOfCircle CenterX=19 CenterY=19 CenterZ=0 NormalX=0 NormalY=0 NormalZ=1 AngleXU=0 Radius=16 StartAngle=1.5708 EndAngle=3.14159
    g3: LineSegment StartX=114 StartY=35 StartZ=0 EndX=19 EndY=35 EndZ=0
    g4: LineSegment StartX=5.21097e-06 StartY=3 StartZ=0 EndX=5.21097e-06 EndY=0 EndZ=0
    g5: LineSegment StartX=3 StartY=0 StartZ=0 EndX=5.21097e-06 EndY=0 EndZ=0
    g6: LineSegment StartX=3 StartY=19 StartZ=0 EndX=3 EndY=0 EndZ=0
    g7: LineSegment StartX=19 StartY=38 StartZ=0 EndX=124 EndY=38 EndZ=0
    g8: Circle CenterX=119 CenterY=35 CenterZ=0 NormalX=0 NormalY=0 NormalZ=1 AngleXU=0 Radius=1
    g9: Circle CenterX=121 CenterY=35 CenterZ=0 NormalX=0 NormalY=0 NormalZ=1 AngleXU=0 Radius=1
    g10: Circle CenterX=121 CenterY=33 CenterZ=0 NormalX=0 NormalY=0 NormalZ=1 AngleXU=0 Radius=1
    g11: BSplineCurve PolesCount=3 KnotsCount=2 Degree=2 IsPeriodic=0
    g12: GeomPoint X=119 Y=35 Z=0
    g13: GeomPoint X=121 Y=33 Z=0
    g14: LineSegment StartX=119 StartY=35 StartZ=0 EndX=114 EndY=35 EndZ=0
    g15: ArcOfCircle CenterX=105 CenterY=19 CenterZ=0 NormalX=0 NormalY=0 NormalZ=1 AngleXU=0 Radius=19 StartAngle=5.7297 EndAngle=6.28319
    g16: ArcOfCircle CenterX=105 CenterY=19 CenterZ=0 NormalX=0 NormalY=0 NormalZ=1 AngleXU=0 Radius=16 StartAngle=5.60905 EndAngle=6.28319
    g17: LineSegment StartX=121 StartY=33 StartZ=0 EndX=121 EndY=19 EndZ=0
    g18: LineSegment StartX=124 StartY=38 StartZ=0 EndX=124 EndY=19 EndZ=0
    g19: LineSegment StartX=117.5 StartY=9.01251 StartZ=0 EndX=121.163 EndY=9.0125 EndZ=0
  constraints (46):
    c: Vertical(g0)
    c: Block(g0)
    c: Coincident(g1,g0)
    c: Block(g1)
    c: Coincident(g2,g1)
    c: Block(g2)
    c: Coincident(g3,g2)
    c: Horizontal(g3)
    c: Tangent(g3,g2)
    c: Coincident(g4,g0)
    c: Distance(g4) = 3
    c: Vertical(g4)
    c: Coincident(g5,g4)
    c: Horizontal(g5)
    c: Coincident(g6,g2)
    c: Coincident(g6,g5)
    c: Vertical(g6)
    c: Horizontal(g7)
    c: Distance(g7) = 105
    c: Coincident(g7,g1)
    c: Block(g3)
    c: Weight(g8) = 1
    c: Equal(g8,g9)
    c: Equal(g8,g10)
    c: InternalAlignment(g8,g11)
    c: InternalAlignment(g9,g11)
    c: InternalAlignment(g10,g11)
    c: InternalAlignment(g12,g11)
    c: InternalAlignment(g13,g11)
    c: Block(g11)
    c: Coincident(g14,g11)
    c: Coincident(g14,g3)
    c: Horizontal(g14)
    c: Block(g15)
    c: Coincident(g16,g15)
    c: Block(g16)
    c: Coincident(g17,g11)
    c: Coincident(g17,g16)
    c: Vertical(g17)
    c: Distance(g17) = 14
    c: Coincident(g18,g7)
    c: Coincident(g18,g15)
    c: Vertical(g18)
    c: Distance(g18) = 19
    c: Coincident(g19,g16)
    c: Coincident(g19,g15)
FEATURE [Sketcher::SketchObject] Sketch065
  FullyConstrained = true
  MapMode = 3
  Placement = pos=(0,0,0) rot=(1,0,0;1.5708rad)
  sketch-geometry (8):
    g0: Circle CenterX=80.351 CenterY=-67.6202 CenterZ=0 NormalX=0 NormalY=0 NormalZ=1 AngleXU=0 Radius=3
    g1: Circle CenterX=80.351 CenterY=-4.92017 CenterZ=0 NormalX=0 NormalY=0 NormalZ=1 AngleXU=0 Radius=3
    g2: Circle CenterX=23.851 CenterY=-4.92017 CenterZ=0 NormalX=0 NormalY=0 NormalZ=1 AngleXU=0 Radius=3
    g3: Circle CenterX=23.851 CenterY=-67.6202 CenterZ=0 NormalX=0 NormalY=0 NormalZ=1 AngleXU=0 Radius=3
    g4: Circle CenterX=23.851 CenterY=-67.6202 CenterZ=0 NormalX=0 NormalY=0 NormalZ=1 AngleXU=0 Radius=5
    g5: Circle CenterX=80.351 CenterY=-67.6202 CenterZ=0 NormalX=0 NormalY=0 NormalZ=1 AngleXU=0 Radius=5
    g6: Circle CenterX=23.851 CenterY=-4.92017 CenterZ=0 NormalX=0 NormalY=0 NormalZ=1 AngleXU=0 Radius=5
    g7: Circle CenterX=80.351 CenterY=-4.92017 CenterZ=0 NormalX=0 NormalY=0 NormalZ=1 AngleXU=0 Radius=5
  constraints (8):
    c: Block(g1)
    c: Block(g0)
    c: Block(g3)
    c: Block(g2)
    c: Block(g5)
    c: Block(g4)
    c: Block(g6)
    c: Block(g7)
FEATURE [Part::Extrusion] Extrude056
  Base = -> Sketch065
  Dir = (0,-1,2e-16)
  DirMode = 2
  FaceMakerClass = Part::FaceMakerBullseye
  LengthFwd = 2
  LengthRev = 0
  Solid = true
  Symmetric = false
FEATURE [Part::Extrusion] Extrude057  label="top025"
  Base = -> Sketch064
  Dir = (0,0,1)
  DirMode = 2
  FaceMakerClass = Part::FaceMakerBullseye
  LengthFwd = 72
  LengthRev = 0
  Solid = true
  Symmetric = false
FEATURE [Sketcher::SketchObject] Sketch066
  FullyConstrained = true
  MapMode = 3
  Placement = pos=(0,0,0) rot=(1,0,0;1.5708rad)
  Support = -> [Extrude057]
  sketch-geometry (8):
    g0: Circle CenterX=80.351 CenterY=-67.6202 CenterZ=0 NormalX=0 NormalY=0 NormalZ=1 AngleXU=0 Radius=3
    g1: Circle CenterX=80.351 CenterY=-4.92017 CenterZ=0 NormalX=0 NormalY=0 NormalZ=1 AngleXU=0 Radius=3
    g2: Circle CenterX=23.851 CenterY=-4.92017 CenterZ=0 NormalX=0 NormalY=0 NormalZ=1 AngleXU=0 Radius=3
    g3: Circle CenterX=23.851 CenterY=-67.6202 CenterZ=0 NormalX=0 NormalY=0 NormalZ=1 AngleXU=0 Radius=3
    g4: Circle CenterX=23.851 CenterY=-67.6202 CenterZ=0 NormalX=0 NormalY=0 NormalZ=1 AngleXU=0 Radius=5
    g5: Circle CenterX=80.351 CenterY=-67.6202 CenterZ=0 NormalX=0 NormalY=0 NormalZ=1 AngleXU=0 Radius=5
    g6: Circle CenterX=23.851 CenterY=-4.92017 CenterZ=0 NormalX=0 NormalY=0 NormalZ=1 AngleXU=0 Radius=5
    g7: Circle CenterX=80.351 CenterY=-4.92017 CenterZ=0 NormalX=0 NormalY=0 NormalZ=1 AngleXU=0 Radius=5
  constraints (8):
    c: Block(g1)
    c: Block(g0)
    c: Block(g3)
    c: Block(g2)
    c: Block(g5)
    c: Block(g4)
    c: Block(g6)
    c: Block(g7)
FEATURE [Part::Extrusion] Extrude055
  Base = -> Sketch066
  Dir = (0,-1,2e-16)
  DirMode = 2
  FaceMakerClass = Part::FaceMakerBullseye
  LengthFwd = 2
  LengthRev = 0
  Solid = true
  Symmetric = false
FEATURE [Part::Fillet] Fillet041
  Base = -> Extrude056
  Edges = 4 edges r=1.99: [Edge6,Edge12,Edge18,Edge24]
FEATURE [Part::Cut] Cut045
  Base = -> Extrude055
  Placement = pos=(0,6,0) rot=(0,0,1;0rad)
  Tool = -> Fillet041
FEATURE [Part::MultiFuse] Fusion095  label="pcbScrewPillars"
  Placement = pos=(-3.2,-1,72.3) rot=(0,0,1;0rad)
  Shapes = -> [Cut045,Extrude054]
FEATURE [Part::Feature] Face113
  shape: bbox 3.2 x 1.5 x 2e-07 mm, 1 faces, 0 solids (baked)
FEATURE [Part::Revolution] Revolve121  label="backCaseScrewRetainer002"
  Angle = 360
  Axis = (0,1,0)
  Base = (0,0,0)
  FaceMakerClass = Part::FaceMakerBullseye
  Placement = pos=(12.5,3,62) rot=(0,0,1;0rad)
  Solid = false
  Source = -> Face113
  Symmetric = false
FEATURE [Part::Feature] Face114
  shape: bbox 3.2 x 1.5 x 2e-07 mm, 1 faces, 0 solids (baked)
FEATURE [Part::Feature] Face115
  shape: bbox 3.2 x 1.5 x 2e-07 mm, 1 faces, 0 solids (baked)
FEATURE [Part::Feature] Face116
  shape: bbox 3.2 x 1.5 x 2e-07 mm, 1 faces, 0 solids (baked)
FEATURE [Part::Revolution] Revolve122  label="frontCaseScrewRetainer004"
  Angle = 360
  Axis = (0,1,0)
  Base = (0,0,0)
  FaceMakerClass = Part::FaceMakerBullseye
  Placement = pos=(89.5,3,68.5) rot=(0,0,1;0rad)
  Solid = false
  Source = -> Face115
  Symmetric = false
FEATURE [Part::Revolution] Revolve123  label="frontCaseScrewRetainer005"
  Angle = 360
  Axis = (0,1,0)
  Base = (0,0,0)
  FaceMakerClass = Part::FaceMakerBullseye
  Placement = pos=(89.5,3,3.5) rot=(0,0,1;0rad)
  Solid = false
  Source = -> Face116
  Symmetric = false
FEATURE [Part::Revolution] Revolve124  label="backCaseScrewRetainer003"
  Angle = 360
  Axis = (0,1,0)
  Base = (0,0,0)
  FaceMakerClass = Part::FaceMakerBullseye
  Placement = pos=(12.5,3,10) rot=(0,0,1;0rad)
  Solid = false
  Source = -> Face114
  Symmetric = false
FEATURE [Part::Feature] Face117
  shape: bbox 3.6 x 3.2 x 2e-07 mm, 1 faces, 0 solids (baked)
FEATURE [Part::Revolution] Revolve125  label="moreFrontCaseScrewRetainer004"
  Angle = 360
  Axis = (0,1,0)
  Base = (0,0,0)
  FaceMakerClass = Part::FaceMakerBullseye
  Placement = pos=(109.5,4.5,68.5) rot=(0,0,1;0rad)
  Solid = false
  Source = -> Face117
  Symmetric = false
FEATURE [Part::Feature] Face118
  shape: bbox 3.6 x 3.2 x 2e-07 mm, 1 faces, 0 solids (baked)
FEATURE [Part::Revolution] Revolve126  label="moreFrontCaseScrewRetainer005"
  Angle = 360
  Axis = (0,1,0)
  Base = (0,0,0)
  FaceMakerClass = Part::FaceMakerBullseye
  Placement = pos=(109.5,4.5,3.5) rot=(0,0,1;0rad)
  Solid = false
  Source = -> Face118
  Symmetric = false
FEATURE [Part::MultiFuse] Fusion096  label="screwRetainers001"
  Shapes = -> [Revolve126,Revolve125,Revolve124,Revolve123,Revolve122,Revolve121]
FEATURE [Part::Feature] Face119
  shape: bbox 10 x 16.5 x 2e-07 mm, 1 faces, 0 solids (baked)
FEATURE [Part::Revolution] Revolve130  label="plugHousing050"
  Angle = 360
  Axis = (0,1,0)
  Base = (0,0,0)
  FaceMakerClass = Part::FaceMakerBullseye
  Placement = pos=(0,0,36.15) rot=(0,0,1;0rad)
  Solid = false
  Source = -> Face119
  Symmetric = false
FEATURE [Part::Feature] Face120
  shape: bbox 10 x 16.5 x 2e-07 mm, 1 faces, 0 solids (baked)
FEATURE [Part::Feature] Face121
  shape: bbox 10 x 16.5 x 2e-07 mm, 1 faces, 0 solids (baked)
FEATURE [Part::Revolution] Revolve127  label="plugHousing047"
  Angle = 360
  Axis = (0,1,0)
  Base = (0,0,0)
  FaceMakerClass = Part::FaceMakerBullseye
  Placement = pos=(0,0,36.15) rot=(0,0,1;0rad)
  Solid = false
  Source = -> Face121
  Symmetric = false
FEATURE [Part::Feature] Face122
  shape: bbox 10 x 16.5 x 2e-07 mm, 1 faces, 0 solids (baked)
FEATURE [Part::Feature] Face123
  shape: bbox 10 x 16.5 x 2e-07 mm, 1 faces, 0 solids (baked)
FEATURE [Part::Revolution] Revolve128  label="plugHousing048"
  Angle = 360
  Axis = (0,1,0)
  Base = (0,0,0)
  FaceMakerClass = Part::FaceMakerBullseye
  Placement = pos=(0,0,36.15) rot=(0,0,1;0rad)
  Solid = false
  Source = -> Face123
  Symmetric = false
FEATURE [Part::MultiFuse] Fusion100  label="plugHousing054"
  Placement = pos=(0,0,0) rot=(0,0,1;1.5708rad)
  Shapes = -> [Revolve130,Revolve128]
FEATURE [Part::Feature] Face124
  shape: bbox 10 x 16.5 x 2e-07 mm, 1 faces, 0 solids (baked)
FEATURE [Part::Feature] Face125
  shape: bbox 10 x 16.5 x 2e-07 mm, 1 faces, 0 solids (baked)
FEATURE [Part::Revolution] Revolve129  label="plugHousing049"
  Angle = 360
  Axis = (0,1,0)
  Base = (0,0,0)
  FaceMakerClass = Part::FaceMakerBullseye
  Placement = pos=(0,0,36.15) rot=(0,0,1;0rad)
  Solid = false
  Source = -> Face125
  Symmetric = false
FEATURE [Part::Feature] Face126
  shape: bbox 10 x 16.5 x 2e-07 mm, 1 faces, 0 solids (baked)
FEATURE [Part::Revolution] Revolve131  label="plugHousing058"
  Angle = 360
  Axis = (0,1,0)
  Base = (0,0,0)
  FaceMakerClass = Part::FaceMakerBullseye
  Placement = pos=(0,0,36.15) rot=(0,0,1;0rad)
  Solid = false
  Source = -> Face120
  Symmetric = false
FEATURE [Part::MultiFuse] Fusion099  label="plugHousing053"
  Placement = pos=(0,0,0) rot=(0,0,1;1.5708rad)
  Shapes = -> [Revolve127,Revolve131]
FEATURE [Part::MultiFuse] Fusion102  label="plugHousing056"
  Placement = pos=(0,19,0) rot=(0,0,1;3.14159rad)
  Shapes = -> [Fusion100,Fusion099]
FEATURE [Part::Revolution] Revolve132  label="plugHousing059"
  Angle = 360
  Axis = (0,1,0)
  Base = (0,0,0)
  FaceMakerClass = Part::FaceMakerBullseye
  Placement = pos=(0,0,36.15) rot=(0,0,1;0rad)
  Solid = false
  Source = -> Face126
  Symmetric = false
FEATURE [Part::Revolution] Revolve133  label="plugHousing060"
  Angle = 360
  Axis = (0,1,0)
  Base = (0,0,0)
  FaceMakerClass = Part::FaceMakerBullseye
  Placement = pos=(0,0,36.15) rot=(0,0,1;0rad)
  Solid = false
  Source = -> Face122
  Symmetric = false
FEATURE [Part::MultiFuse] Fusion097  label="plugHousing051"
  Placement = pos=(0,0,0) rot=(0,0,1;1.5708rad)
  Shapes = -> [Revolve133,Revolve132]
FEATURE [Part::Revolution] Revolve134  label="plugHousing061"
  Angle = 360
  Axis = (0,1,0)
  Base = (0,0,0)
  FaceMakerClass = Part::FaceMakerBullseye
  Placement = pos=(0,0,36.15) rot=(0,0,1;0rad)
  Solid = false
  Source = -> Face124
  Symmetric = false
FEATURE [Part::MultiFuse] Fusion101  label="plugHousing055"
  Placement = pos=(0,0,0) rot=(0,0,1;1.5708rad)
  Shapes = -> [Revolve129,Revolve134]
FEATURE [Part::MultiFuse] Fusion098  label="plugHousing052"
  Placement = pos=(0,19,0) rot=(0,0,1;3.14159rad)
  Shapes = -> [Fusion097,Fusion101]
FEATURE [Part::MultiFuse] Fusion103  label="plugHousing057"
  Placement = pos=(122.621,0,-0.15) rot=(0,0,1;0rad)
  Shapes = -> [Fusion102,Fusion098]
FEATURE [Part::Box] Box028  label="Cube015"
  AttacherType = Attacher::AttachEngine3D
  Height = 28
  Length = 3
  Placement = pos=(110.7,19,22) rot=(0,0,1;0rad)
  Width = 15.7
FEATURE [Part::Cylinder] Cylinder044
  Angle = 360
  AttacherType = Attacher::AttachEngine3D
  Height = 20
  Placement = pos=(0,0,36.15) rot=(0,0,1;0rad)
  Radius = 10.3
FEATURE [Part::Cylinder] Cylinder045
  Angle = 360
  AttacherType = Attacher::AttachEngine3D
  Height = 10
  Placement = pos=(0,0,36.15) rot=(0,0,1;0rad)
  Radius = 4
FEATURE [Part::MultiFuse] Fusion104  label="removeToCreteHoleForPlugHousing040"
  Placement = pos=(70,19,36) rot=(0,1,0;1.5708rad)
  Shapes = -> [Cylinder044,Cylinder045]
FEATURE [Part::Cut] Cut046  label="plugHousingTab003"
  Base = -> Box028
  Tool = -> Fusion104
FEATURE [Part::MultiFuse] Fusion105  label="plugHousing062"
  Shapes = -> [Fusion103,Cut046]
FEATURE [Part::Fillet] Fillet042
  Base = -> Fusion105
  Edges = 1 edges r=2: [Edge25]
FEATURE [Part::Fillet] Fillet043  label="plugHousing063"
  Base = -> Fillet042
  Edges = 1 edges r=2: [Edge8]
  Placement = pos=(7,0,0) rot=(0,0,1;0rad)
FEATURE [Part::Feature] Face127
  shape: bbox 10 x 16.5 x 2e-07 mm, 1 faces, 0 solids (baked)
FEATURE [Part::Feature] Face128
  shape: bbox 10 x 16.5 x 2e-07 mm, 1 faces, 0 solids (baked)
FEATURE [Part::Revolution] Revolve137  label="plugHousing070"
  Angle = 360
  Axis = (0,1,0)
  Base = (0,0,0)
  FaceMakerClass = Part::FaceMakerBullseye
  Placement = pos=(0,0,36.15) rot=(0,0,1;0rad)
  Solid = false
  Source = -> Face127
  Symmetric = false
FEATURE [Part::Revolution] Revolve140  label="plugHousing073"
  Angle = 360
  Axis = (0,1,0)
  Base = (0,0,0)
  FaceMakerClass = Part::FaceMakerBullseye
  Placement = pos=(0,0,36.15) rot=(0,0,1;0rad)
  Solid = false
  Source = -> Face128
  Symmetric = false
FEATURE [Part::Feature] Face129
  shape: bbox 10 x 16.5 x 2e-07 mm, 1 faces, 0 solids (baked)
FEATURE [Part::Revolution] Revolve138  label="plugHousing071"
  Angle = 360
  Axis = (0,1,0)
  Base = (0,0,0)
  FaceMakerClass = Part::FaceMakerBullseye
  Placement = pos=(0,0,36.15) rot=(0,0,1;0rad)
  Solid = false
  Source = -> Face129
  Symmetric = false
FEATURE [Part::Feature] Face130
  shape: bbox 10 x 16.5 x 2e-07 mm, 1 faces, 0 solids (baked)
FEATURE [Part::Revolution] Revolve139  label="plugHousing072"
  Angle = 360
  Axis = (0,1,0)
  Base = (0,0,0)
  FaceMakerClass = Part::FaceMakerBullseye
  Placement = pos=(0,0,36.15) rot=(0,0,1;0rad)
  Solid = false
  Source = -> Face130
  Symmetric = false
FEATURE [Part::Feature] Face131
  shape: bbox 10 x 16.5 x 2e-07 mm, 1 faces, 0 solids (baked)
FEATURE [Part::Revolution] Revolve135  label="plugHousing068"
  Angle = 360
  Axis = (0,1,0)
  Base = (0,0,0)
  FaceMakerClass = Part::FaceMakerBullseye
  Placement = pos=(0,0,36.15) rot=(0,0,1;0rad)
  Solid = false
  Source = -> Face131
  Symmetric = false
FEATURE [Part::MultiFuse] Fusion112  label="plugHousing078"
  Placement = pos=(0,0,0) rot=(0,0,1;1.5708rad)
  Shapes = -> [Revolve135,Revolve139]
FEATURE [Part::Feature] Face132
  shape: bbox 10 x 16.5 x 2e-07 mm, 1 faces, 0 solids (baked)
FEATURE [Part::Revolution] Revolve141  label="plugHousing074"
  Angle = 360
  Axis = (0,1,0)
  Base = (0,0,0)
  FaceMakerClass = Part::FaceMakerBullseye
  Placement = pos=(0,0,36.15) rot=(0,0,1;0rad)
  Solid = false
  Source = -> Face132
  Symmetric = false
FEATURE [Part::MultiFuse] Fusion110  label="plugHousing076"
  Placement = pos=(0,0,0) rot=(0,0,1;1.5708rad)
  Shapes = -> [Revolve141,Revolve140]
FEATURE [Part::Feature] Face133
  shape: bbox 10 x 16.5 x 2e-07 mm, 1 faces, 0 solids (baked)
FEATURE [Part::Revolution] Revolve136  label="plugHousing069"
  Angle = 360
  Axis = (0,1,0)
  Base = (0,0,0)
  FaceMakerClass = Part::FaceMakerBullseye
  Placement = pos=(0,0,36.15) rot=(0,0,1;0rad)
  Solid = false
  Source = -> Face133
  Symmetric = false
FEATURE [Part::MultiFuse] Fusion106  label="plugHousing064"
  Placement = pos=(0,0,0) rot=(0,0,1;1.5708rad)
  Shapes = -> [Revolve138,Revolve136]
FEATURE [Part::MultiFuse] Fusion108  label="plugHousing066"
  Placement = pos=(0,19,0) rot=(0,0,1;3.14159rad)
  Shapes = -> [Fusion106,Fusion112]
FEATURE [Part::Feature] Face134
  shape: bbox 10 x 16.5 x 2e-07 mm, 1 faces, 0 solids (baked)
FEATURE [Part::Revolution] Revolve142  label="plugHousing075"
  Angle = 360
  Axis = (0,1,0)
  Base = (0,0,0)
  FaceMakerClass = Part::FaceMakerBullseye
  Placement = pos=(0,0,36.15) rot=(0,0,1;0rad)
  Solid = false
  Source = -> Face134
  Symmetric = false
FEATURE [Part::MultiFuse] Fusion107  label="plugHousing065"
  Placement = pos=(0,0,0) rot=(0,0,1;1.5708rad)
  Shapes = -> [Revolve137,Revolve142]
FEATURE [Part::MultiFuse] Fusion111  label="plugHousing077"
  Placement = pos=(0,19,0) rot=(0,0,1;3.14159rad)
  Shapes = -> [Fusion110,Fusion107]
FEATURE [Part::MultiFuse] Fusion109  label="plugHousing067"
  Placement = pos=(131.236,0,-0.15) rot=(0,0,1;0rad)
  Shapes = -> [Fusion108,Fusion111]
FEATURE [Part::MultiFuse] Fusion113  label="plugHousing079"
  Shapes = -> [Fillet043,Fusion109]
FEATURE [Part::Feature] Face135
  shape: bbox 3.5 x 17.8 x 2e-07 mm, 1 faces, 0 solids (baked)
FEATURE [Part::Revolution] Revolve143  label="removeToCreateScrewAndThreadedInsertHole049"
  Angle = 360
  Axis = (0,1,0)
  Base = (0,0,0)
  FaceMakerClass = Part::FaceMakerBullseye
  Placement = pos=(12.5,0,10) rot=(0,0,1;0rad)
  Solid = false
  Source = -> Face135
  Symmetric = false
FEATURE [Part::Feature] Face136
  shape: bbox 3.5 x 17.8 x 2e-07 mm, 1 faces, 0 solids (baked)
FEATURE [Part::Revolution] Revolve144  label="removeToCreateScrewAndThreadedInsertHole050"
  Angle = 360
  Axis = (0,1,0)
  Base = (0,0,0)
  FaceMakerClass = Part::FaceMakerBullseye
  Placement = pos=(12.5,0,62) rot=(0,0,1;0rad)
  Solid = false
  Source = -> Face136
  Symmetric = false
FEATURE [Part::Feature] Face137
  shape: bbox 3.5 x 17.8 x 2e-07 mm, 1 faces, 0 solids (baked)
FEATURE [Part::Revolution] Revolve145  label="removeToCreateScrewAndThreadedInsertHole051"
  Angle = 360
  Axis = (0,1,0)
  Base = (0,0,0)
  FaceMakerClass = Part::FaceMakerBullseye
  Placement = pos=(89.5,0,68.5) rot=(0,0,1;0rad)
  Solid = false
  Source = -> Face137
  Symmetric = false
FEATURE [Part::Feature] Face138
  shape: bbox 3.5 x 17.8 x 2e-07 mm, 1 faces, 0 solids (baked)
FEATURE [Part::Revolution] Revolve146  label="removeToCreateScrewAndThreadedInsertHole052"
  Angle = 360
  Axis = (0,1,0)
  Base = (0,0,0)
  FaceMakerClass = Part::FaceMakerBullseye
  Placement = pos=(89.5,0,3.5) rot=(0,0,1;0rad)
  Solid = false
  Source = -> Face138
  Symmetric = false
FEATURE [Part::Feature] Face139
  shape: bbox 3.5 x 17.8 x 2e-07 mm, 1 faces, 0 solids (baked)
FEATURE [Part::Revolution] Revolve147  label="removeToCreateScrewAndThreadedInsertHole053"
  Angle = 360
  Axis = (0,1,0)
  Base = (0,0,0)
  FaceMakerClass = Part::FaceMakerBullseye
  Placement = pos=(109.5,4.7,3.5) rot=(0,0,1;0rad)
  Solid = false
  Source = -> Face139
  Symmetric = false
FEATURE [Part::Feature] Face140
  shape: bbox 3.5 x 17.8 x 2e-07 mm, 1 faces, 0 solids (baked)
FEATURE [Part::Revolution] Revolve148  label="removeToCreateScrewAndThreadedInsertHole054"
  Angle = 360
  Axis = (0,1,0)
  Base = (0,0,0)
  FaceMakerClass = Part::FaceMakerBullseye
  Placement = pos=(109.5,4.7,68.5) rot=(0,0,1;0rad)
  Solid = false
  Source = -> Face140
  Symmetric = false
FEATURE [Part::MultiFuse] Fusion114  label="removeToCreateScrewAndThreadedInsertHole055"
  Shapes = -> [Revolve148,Revolve147,Revolve146,Revolve145,Revolve144,Revolve143]
FEATURE [Part::Cut] Cut047  label="casePillars004"
  Base = -> Cut037
  Tool = -> Fusion114
FEATURE [Part::Feature] Face141
  shape: bbox 3.5 x 17.8 x 2e-07 mm, 1 faces, 0 solids (baked)
FEATURE [Part::Feature] Face142
  shape: bbox 3.5 x 17.8 x 2e-07 mm, 1 faces, 0 solids (baked)
FEATURE [Part::Feature] Face143
  shape: bbox 3.5 x 17.8 x 2e-07 mm, 1 faces, 0 solids (baked)
FEATURE [Part::Revolution] Revolve149  label="removeToCreateScrewAndThreadedInsertHole057"
  Angle = 360
  Axis = (0,1,0)
  Base = (0,0,0)
  FaceMakerClass = Part::FaceMakerBullseye
  Placement = pos=(12.5,0,10) rot=(0,0,1;0rad)
  Solid = false
  Source = -> Face141
  Symmetric = false
FEATURE [Part::Feature] Face144
  shape: bbox 3.5 x 17.8 x 2e-07 mm, 1 faces, 0 solids (baked)
FEATURE [Part::Feature] Face145
  shape: bbox 3.5 x 17.8 x 2e-07 mm, 1 faces, 0 solids (baked)
FEATURE [Part::Feature] Face146
  shape: bbox 3.5 x 17.8 x 2e-07 mm, 1 faces, 0 solids (baked)
FEATURE [Part::Revolution] Revolve150  label="removeToCreateScrewAndThreadedInsertHole058"
  Angle = 360
  Axis = (0,1,0)
  Base = (0,0,0)
  FaceMakerClass = Part::FaceMakerBullseye
  Placement = pos=(12.5,0,62) rot=(0,0,1;0rad)
  Solid = false
  Source = -> Face146
  Symmetric = false
FEATURE [Part::Revolution] Revolve151  label="removeToCreateScrewAndThreadedInsertHole059"
  Angle = 360
  Axis = (0,1,0)
  Base = (0,0,0)
  FaceMakerClass = Part::FaceMakerBullseye
  Placement = pos=(89.5,0,68.5) rot=(0,0,1;0rad)
  Solid = false
  Source = -> Face143
  Symmetric = false
FEATURE [Part::Revolution] Revolve152  label="removeToCreateScrewAndThreadedInsertHole060"
  Angle = 360
  Axis = (0,1,0)
  Base = (0,0,0)
  FaceMakerClass = Part::FaceMakerBullseye
  Placement = pos=(89.5,0,3.5) rot=(0,0,1;0rad)
  Solid = false
  Source = -> Face142
  Symmetric = false
FEATURE [Part::Revolution] Revolve153  label="removeToCreateScrewAndThreadedInsertHole061"
  Angle = 360
  Axis = (0,1,0)
  Base = (0,0,0)
  FaceMakerClass = Part::FaceMakerBullseye
  Placement = pos=(109.5,4.7,3.5) rot=(0,0,1;0rad)
  Solid = false
  Source = -> Face145
  Symmetric = false
FEATURE [Part::Revolution] Revolve154  label="removeToCreateScrewAndThreadedInsertHole062"
  Angle = 360
  Axis = (0,1,0)
  Base = (0,0,0)
  FaceMakerClass = Part::FaceMakerBullseye
  Placement = pos=(109.5,4.7,68.5) rot=(0,0,1;0rad)
  Solid = false
  Source = -> Face144
  Symmetric = false
FEATURE [Part::MultiFuse] Fusion115  label="removeToCreateScrewAndThreadedInsertHole056"
  Shapes = -> [Revolve154,Revolve153,Revolve152,Revolve151,Revolve150,Revolve149]
FEATURE [Part::Feature] Face147
  shape: bbox 9.8 x 26.5 x 2e-07 mm, 1 faces, 0 solids (baked)
FEATURE [Part::Revolution] Revolve155
  Angle = 360
  Axis = (0,1,0)
  Base = (0,0,0)
  FaceMakerClass = Part::FaceMakerBullseye
  Placement = pos=(0,0,0) rot=(0,0,1;1.5708rad)
  Solid = false
  Source = -> Face147
  Symmetric = false
FEATURE [Part::Feature] Face148
  shape: bbox 9.8 x 26.5 x 2e-07 mm, 1 faces, 0 solids (baked)
FEATURE [Part::Revolution] Revolve156
  Angle = 360
  Axis = (0,1,0)
  Base = (0,0,0)
  FaceMakerClass = Part::FaceMakerBullseye
  Placement = pos=(0,0,0) rot=(0,0,1;1.5708rad)
  Solid = false
  Source = -> Face148
  Symmetric = false
FEATURE [Part::MultiFuse] Fusion116
  Placement = pos=(-18,19,36) rot=(0,0,1;0rad)
  Shapes = -> [Revolve156,Revolve155]
FEATURE [Part::Box] Box029  label="Cube016"
  AttacherType = Attacher::AttachEngine3D
  Height = 28
  Length = 3
  Placement = pos=(110.7,19,22) rot=(0,0,1;0rad)
  Width = 15.7
FEATURE [Part::Cylinder] Cylinder046
  Angle = 360
  AttacherType = Attacher::AttachEngine3D
  Height = 10
  Placement = pos=(0,0,36.15) rot=(0,0,1;0rad)
  Radius = 4
FEATURE [Part::Cylinder] Cylinder047
  Angle = 360
  AttacherType = Attacher::AttachEngine3D
  Height = 20
  Placement = pos=(0,0,36.15) rot=(0,0,1;0rad)
  Radius = 10.3
FEATURE [Part::MultiFuse] Fusion117  label="removeToCreteHoleForPlugHousing041"
  Placement = pos=(70,19,36) rot=(0,1,0;1.5708rad)
  Shapes = -> [Cylinder047,Cylinder046]
FEATURE [Part::Cut] Cut049  label="plugHousingTab004"
  Base = -> Box029
  Placement = pos=(-107.4,-14,0) rot=(0,0,1;0rad)
  Tool = -> Fusion117
FEATURE [Part::Box] Box030  label="Cube017"
  AttacherType = Attacher::AttachEngine3D
  Height = 28
  Length = 3
  Placement = pos=(110.7,19,22) rot=(0,0,1;0rad)
  Width = 15.7
FEATURE [Part::Cylinder] Cylinder048
  Angle = 360
  AttacherType = Attacher::AttachEngine3D
  Height = 10
  Placement = pos=(0,0,36.15) rot=(0,0,1;0rad)
  Radius = 4
FEATURE [Part::Cylinder] Cylinder049
  Angle = 360
  AttacherType = Attacher::AttachEngine3D
  Height = 20
  Placement = pos=(0,0,36.15) rot=(0,0,1;0rad)
  Radius = 10.3
FEATURE [Part::MultiFuse] Fusion118  label="removeToCreteHoleForPlugHousing042"
  Placement = pos=(70,19,36) rot=(0,1,0;1.5708rad)
  Shapes = -> [Cylinder049,Cylinder048]
FEATURE [Part::Cut] Cut050  label="plugHousingTab005"
  Base = -> Box030
  Placement = pos=(-107.4,-14,0) rot=(0,0,1;0rad)
  Tool = -> Fusion118
FEATURE [Part::MultiFuse] Fusion119
  Placement = pos=(9.6,23,0) rot=(0,0,1;3.14159rad)
  Shapes = -> [Cut049,Cut050]
FEATURE [Part::Box] Box031  label="Cube018"
  AttacherType = Attacher::AttachEngine3D
  Height = 10
  Length = 3
  Placement = pos=(3.3,4,12) rot=(0,0,1;0rad)
  Width = 10
FEATURE [Part::Fillet] Fillet044
  Base = -> Box031
  Edges = 1 edges r=2: [Edge11]
FEATURE [Part::Box] Box032  label="Cube019"
  AttacherType = Attacher::AttachEngine3D
  Height = 10
  Length = 3
  Placement = pos=(3.3,4,50) rot=(0,0,1;0rad)
  Width = 10
FEATURE [Part::Fillet] Fillet045
  Base = -> Box032
  Edges = 1 edges r=2: [Edge12]
FEATURE [Part::Box] Box033  label="Cube020"
  AttacherType = Attacher::AttachEngine3D
  Height = 28
  Length = 4
  Placement = pos=(5,0,22) rot=(0,0,1;0rad)
  Width = 10
FEATURE [Part::Fillet] Fillet046
  Base = -> Box033
  Edges = 1 edges r=1: [Edge7]
FEATURE [Part::Fillet] Fillet047
  Base = -> Fillet046
  Edges = 1 edges r=2: [Edge5]
FEATURE [Part::Fillet] Fillet048
  Base = -> Fillet047
  Edges = 1 edges r=2: [Edge2]
FEATURE [Part::Cylinder] Cylinder050
  Angle = 360
  AttacherType = Attacher::AttachEngine3D
  Height = 20
  Placement = pos=(0,0,36.15) rot=(0,0,1;0rad)
  Radius = 8.2
FEATURE [Part::Cylinder] Cylinder051
  Angle = 360
  AttacherType = Attacher::AttachEngine3D
  Height = 10
  Placement = pos=(0,0,36.15) rot=(0,0,1;0rad)
  Radius = 4
FEATURE [Part::MultiFuse] Fusion120  label="removeToCreteHoleForPlugHousing043"
  Placement = pos=(-42,19,36) rot=(0,1,0;1.5708rad)
  Shapes = -> [Cylinder050,Cylinder051]
FEATURE [Sketcher::SketchObject] Sketch067  label="topSketch018"
  FullyConstrained = true
  sketch-geometry (4):
    g0: LineSegment StartX=16.8446 StartY=31.512 StartZ=0 EndX=16.3251 EndY=34.4666 EndZ=0
    g1: ArcOfCircle CenterX=19 CenterY=19.2524 CenterZ=0 NormalX=0 NormalY=0 NormalZ=1 AngleXU=0 Radius=15.4476 StartAngle=1.74483 EndAngle=2.72717
    g2: ArcOfCircle CenterX=19 CenterY=19.2524 CenterZ=0 NormalX=0 NormalY=0 NormalZ=1 AngleXU=0 Radius=12.4476 StartAngle=1.74483 EndAngle=2.73189
    g3: LineSegment StartX=4.86004 StartY=25.4725 StartZ=0 EndX=7.58253 EndY=24.2107 EndZ=0
  constraints (7):
    c: Block(g0)
    c: Coincident(g1,g0)
    c: Coincident(g2,g0)
    c: Coincident(g3,g1)
    c: Coincident(g3,g2)
    c: Block(g1)
    c: Block(g2)
FEATURE [Part::Extrusion] Extrude058
  Base = -> Sketch067
  Dir = (0,0,1)
  DirMode = 2
  FaceMakerClass = Part::FaceMakerBullseye
  LengthFwd = 10
  LengthRev = 0
  Placement = pos=(0,0,31) rot=(0,0,1;0rad)
  Solid = true
  Symmetric = false
FEATURE [Part::Cut] Cut051
  Base = -> Extrude058
  Tool = -> Fusion120
FEATURE [Part::Fillet] Fillet049
  Base = -> Cut051
  Edges = 1 edges r=2: [Edge1]
FEATURE [Part::Fillet] Fillet050
  Base = -> Fillet049
  Edges = 1 edges r=2.5: [Edge1]
FEATURE [Part::Fillet] Fillet051
  Base = -> Fillet050
  Edges = 1 edges r=2.5: [Edge2]
FEATURE [Part::MultiFuse] Fusion121  label="wireHolder003"
  Shapes = -> [Fusion116,Fillet051]
FEATURE [Part::MultiFuse] Fusion122
  Shapes = -> [Fillet045,Fusion121]
FEATURE [Part::MultiFuse] Fusion123  label="wireHolder004"
  Shapes = -> [Fusion122,Fillet048]
FEATURE [Part::MultiFuse] Fusion124  label="wireHolder005"
  Shapes = -> [Fillet044,Fusion119,Fusion123]
FEATURE [Sketcher::SketchObject] Sketch068  label="topSketch019"
  FullyConstrained = true
  sketch-geometry (6):
    g0: LineSegment StartX=19 StartY=38 StartZ=0 EndX=117 EndY=38 EndZ=0
    g1: ArcOfCircle CenterX=19 CenterY=19 CenterZ=0 NormalX=0 NormalY=0 NormalZ=1 AngleXU=0 Radius=19 StartAngle=1.5708 EndAngle=3.14159
    g2: LineSegment StartX=117 StartY=38 StartZ=0 EndX=117 EndY=19 EndZ=0
    g3: LineSegment StartX=98 StartY=1.0161e-12 StartZ=0 EndX=5.22862e-06 EndY=1.0161e-12 EndZ=0
    g4: LineSegment StartX=5.22862e-06 StartY=19 StartZ=0 EndX=5.22862e-06 EndY=1.0161e-12 EndZ=0
    g5: ArcOfCircle CenterX=98 CenterY=19 CenterZ=0 NormalX=0 NormalY=0 NormalZ=1 AngleXU=0 Radius=19 StartAngle=4.71239 EndAngle=6.28319
  constraints (16):
    c: Horizontal(g0)
    c: Distance(g0) = 98
    c: Coincident(g1,g0)
    c: Block(g1)
    c: Coincident(g2,g0)
    c: Vertical(g2)
    c: Distance(g2) = 19
    c: Horizontal(g3)
    c: Coincident(g4,g1)
    c: Vertical(g4)
    c: Coincident(g3,g4)
    c: Block(g3)
    c: Coincident(g5,g2)
    c: Coincident(g5,g3)
    c: Block(g0)
    c: Block(g5)
FEATURE [Part::Extrusion] Extrude059  label="sideA002"
  Base = -> Sketch068
  Dir = (0,0,1)
  DirMode = 2
  FaceMakerClass = Part::FaceMakerBullseye
  LengthFwd = 3
  LengthRev = 0
  Placement = pos=(0,0,-2.7) rot=(0,0,1;0rad)
  Solid = true
  Symmetric = false
FEATURE [Sketcher::SketchObject] Sketch069  label="topSketch020"
  FullyConstrained = true
  sketch-geometry (6):
    g0: LineSegment StartX=19 StartY=38 StartZ=0 EndX=117 EndY=38 EndZ=0
    g1: ArcOfCircle CenterX=19 CenterY=19 CenterZ=0 NormalX=0 NormalY=0 NormalZ=1 AngleXU=0 Radius=19 StartAngle=1.5708 EndAngle=3.14159
    g2: LineSegment StartX=117 StartY=38 StartZ=0 EndX=117 EndY=19 EndZ=0
    g3: LineSegment StartX=98 StartY=1.0161e-12 StartZ=0 EndX=5.22862e-06 EndY=1.0161e-12 EndZ=0
    g4: LineSegment StartX=5.22862e-06 StartY=19 StartZ=0 EndX=5.22862e-06 EndY=1.0161e-12 EndZ=0
    g5: ArcOfCircle CenterX=98 CenterY=19 CenterZ=0 NormalX=0 NormalY=0 NormalZ=1 AngleXU=0 Radius=19 StartAngle=4.71239 EndAngle=6.28319
  constraints (16):
    c: Horizontal(g0)
    c: Distance(g0) = 98
    c: Coincident(g1,g0)
    c: Block(g1)
    c: Coincident(g2,g0)
    c: Vertical(g2)
    c: Distance(g2) = 19
    c: Horizontal(g3)
    c: Coincident(g4,g1)
    c: Vertical(g4)
    c: Coincident(g3,g4)
    c: Block(g3)
    c: Coincident(g5,g2)
    c: Coincident(g5,g3)
    c: Block(g0)
    c: Block(g5)
FEATURE [Part::Extrusion] Extrude060  label="sideB002"
  Base = -> Sketch069
  Dir = (0,0,1)
  DirMode = 2
  FaceMakerClass = Part::FaceMakerBullseye
  LengthFwd = 3
  LengthRev = 0
  Placement = pos=(0,0,71.7) rot=(0,0,1;0rad)
  Solid = true
  Symmetric = false
FEATURE [Part::MultiFuse] Fusion127  label="removeFromBottom001"
  Placement = pos=(2,0,0) rot=(0,0,1;0rad)
  Shapes = -> [Extrude059,Extrude060]
FEATURE [Part::Cylinder] Cylinder052
  Angle = 360
  AttacherType = Attacher::AttachEngine3D
  Height = 20
  Placement = pos=(0,0,36.15) rot=(0,0,1;0rad)
  Radius = 14
FEATURE [Part::Cylinder] Cylinder053
  Angle = 360
  AttacherType = Attacher::AttachEngine3D
  Height = 10
  Placement = pos=(0,0,36.15) rot=(0,0,1;0rad)
  Radius = 4
FEATURE [Part::MultiFuse] Fusion128  label="removeToCreteHoleForPlugHousing044"
  Placement = pos=(70,19,36) rot=(0,1,0;1.5708rad)
  Shapes = -> [Cylinder052,Cylinder053]
FEATURE [Part::Cut] Cut052  label="bottom011"
  Base = -> Extrude043
  Tool = -> Fusion128
FEATURE [Part::Cut] Cut054  label="bottom012"
  Base = -> Cut052
  Tool = -> Fusion115
FEATURE [Sketcher::SketchObject] Sketch070
  FullyConstrained = true
  Placement = pos=(117,19,0) rot=(0.57735,0.57735,0.57735;2.0944rad)
  sketch-geometry (48):
    g0: LineSegment StartX=-49.19 StartY=69.25 StartZ=0 EndX=-49.19 EndY=66.25 EndZ=0
    g1: LineSegment StartX=-49.19 StartY=63.5 StartZ=0 EndX=-49.19 EndY=60.5 EndZ=0
    g2: LineSegment StartX=-49.19 StartY=57.75 StartZ=0 EndX=-49.19 EndY=54.75 EndZ=0
    g3: LineSegment StartX=-49.19 StartY=52 StartZ=0 EndX=-49.19 EndY=49 EndZ=0
    g4: LineSegment StartX=-49.19 StartY=46.25 StartZ=0 EndX=-49.19 EndY=43.25 EndZ=0
    g5: LineSegment StartX=-49.19 StartY=40.5 StartZ=0 EndX=-49.19 EndY=37.5 EndZ=0
    g6: LineSegment StartX=-49.19 StartY=34.5 StartZ=0 EndX=-49.19 EndY=31.5 EndZ=0
    g7: LineSegment StartX=-49.19 StartY=28.75 StartZ=0 EndX=-49.19 EndY=25.75 EndZ=0
    g8: LineSegment StartX=-49.19 StartY=23 StartZ=0 EndX=-49.19 EndY=20 EndZ=0
    g9: LineSegment StartX=-49.19 StartY=17.25 StartZ=0 EndX=-49.19 EndY=14.25 EndZ=0
    g10: LineSegment StartX=-49.19 StartY=11.5 StartZ=0 EndX=-49.19 EndY=8.5 EndZ=0
    g11: LineSegment StartX=-49.19 StartY=5.75 StartZ=0 EndX=-49.19 EndY=2.75 EndZ=0
    g12: ArcOfCircle CenterX=-1.5 CenterY=67.75 CenterZ=0 NormalX=0 NormalY=0 NormalZ=1 AngleXU=0 Radius=1.5 StartAngle=4.71239 EndAngle=7.85398
    g13: ArcOfCircle CenterX=-1.5 CenterY=62 CenterZ=0 NormalX=0 NormalY=0 NormalZ=1 AngleXU=0 Radius=1.5 StartAngle=4.71239 EndAngle=7.85398
    g14: ArcOfCircle CenterX=-1.5 CenterY=56.25 CenterZ=0 NormalX=0 NormalY=0 NormalZ=1 AngleXU=0 Radius=1.5 StartAngle=4.71239 EndAngle=7.85398
    g15: ArcOfCircle CenterX=-11.49 CenterY=50.5 CenterZ=0 NormalX=0 NormalY=0 NormalZ=1 AngleXU=0 Radius=1.5 StartAngle=4.71239 EndAngle=7.85398
    g16: ArcOfCircle CenterX=-16.28 CenterY=44.75 CenterZ=0 NormalX=0 NormalY=0 NormalZ=1 AngleXU=0 Radius=1.5 StartAngle=4.71239 EndAngle=7.85398
    g17: ArcOfCircle CenterX=-18.2337 CenterY=39 CenterZ=0 NormalX=0 NormalY=0 NormalZ=1 AngleXU=0 Radius=1.5 StartAngle=4.71485 EndAngle=7.85398
    g18: ArcOfCircle CenterX=-16.2837 CenterY=27.25 CenterZ=0 NormalX=0 NormalY=0 NormalZ=1 AngleXU=0 Radius=1.5 StartAngle=4.71485 EndAngle=7.85398
    g19: ArcOfCircle CenterX=-18.2337 CenterY=33 CenterZ=0 NormalX=0 NormalY=0 NormalZ=1 AngleXU=0 Radius=1.5 StartAngle=4.71485 EndAngle=7.85398
    g20: ArcOfCircle CenterX=-11.49 CenterY=21.5 CenterZ=0 NormalX=0 NormalY=0 NormalZ=1 AngleXU=0 Radius=1.5 StartAngle=4.71239 EndAngle=7.85398
    g21: ArcOfCircle CenterX=-1.5 CenterY=4.25 CenterZ=0 NormalX=0 NormalY=0 NormalZ=1 AngleXU=0 Radius=1.5 StartAngle=4.71239 EndAngle=7.85398
    g22: ArcOfCircle CenterX=-1.5 CenterY=10 CenterZ=0 NormalX=0 NormalY=0 NormalZ=1 AngleXU=0 Radius=1.5 StartAngle=4.71239 EndAngle=7.85398
    g23: ArcOfCircle CenterX=-1.5 CenterY=15.75 CenterZ=0 NormalX=0 NormalY=0 NormalZ=1 AngleXU=0 Radius=1.5 StartAngle=4.71239 EndAngle=7.85398
    g24: LineSegment StartX=-49.19 StartY=69.25 StartZ=0 EndX=-1.5 EndY=69.25 EndZ=0
    g25: LineSegment StartX=-49.19 StartY=66.25 StartZ=0 EndX=-1.5 EndY=66.25 EndZ=0
    g26: LineSegment StartX=-49.19 StartY=63.5 StartZ=0 EndX=-1.5 EndY=63.5 EndZ=0
    g27: LineSegment StartX=-49.19 StartY=60.5 StartZ=0 EndX=-1.5 EndY=60.5 EndZ=0
    g28: LineSegment StartX=-49.19 StartY=57.75 StartZ=0 EndX=-1.5 EndY=57.75 EndZ=0
    g29: LineSegment StartX=-49.19 StartY=54.75 StartZ=0 EndX=-1.5 EndY=54.75 EndZ=0
    g30: LineSegment StartX=-49.19 StartY=52 StartZ=0 EndX=-11.49 EndY=52 EndZ=0
    g31: LineSegment StartX=-49.19 StartY=49 StartZ=0 EndX=-11.49 EndY=49 EndZ=0
    g32: LineSegment StartX=-49.19 StartY=46.25 StartZ=0 EndX=-16.28 EndY=46.25 EndZ=0
    g33: LineSegment StartX=-49.19 StartY=43.25 StartZ=0 EndX=-16.28 EndY=43.25 EndZ=0
    g34: LineSegment StartX=-49.19 StartY=40.5 StartZ=0 EndX=-18.2337 EndY=40.5 EndZ=0
    g35: LineSegment StartX=-49.19 StartY=37.5 StartZ=0 EndX=-18.23 EndY=37.5 EndZ=0
    g36: LineSegment StartX=-49.19 StartY=34.5 StartZ=0 EndX=-18.2337 EndY=34.5 EndZ=0
    g37: LineSegment StartX=-49.19 StartY=31.5 StartZ=0 EndX=-18.23 EndY=31.5 EndZ=0
    g38: LineSegment StartX=-49.19 StartY=28.75 StartZ=0 EndX=-16.2837 EndY=28.75 EndZ=0
    g39: LineSegment StartX=-49.19 StartY=25.75 StartZ=0 EndX=-16.28 EndY=25.75 EndZ=0
    g40: LineSegment StartX=-49.19 StartY=23 StartZ=0 EndX=-11.49 EndY=23 EndZ=0
    g41: LineSegment StartX=-49.19 StartY=20 StartZ=0 EndX=-11.49 EndY=20 EndZ=0
    g42: LineSegment StartX=-49.19 StartY=17.25 StartZ=0 EndX=-1.5 EndY=17.25 EndZ=0
    g43: LineSegment StartX=-49.19 StartY=14.25 StartZ=0 EndX=-1.5 EndY=14.25 EndZ=0
    g44: LineSegment StartX=-49.19 StartY=11.5 StartZ=0 EndX=-1.5 EndY=11.5 EndZ=0
    g45: LineSegment StartX=-49.19 StartY=8.5 StartZ=0 EndX=-1.5 EndY=8.5 EndZ=0
    g46: LineSegment StartX=-49.19 StartY=5.75 StartZ=0 EndX=-1.5 EndY=5.75 EndZ=0
    g47: LineSegment StartX=-49.19 StartY=2.75 StartZ=0 EndX=-1.5 EndY=2.75 EndZ=0
  constraints (120):
    c: Vertical(g0)
    c: Distance(g0) = 3
    c: Block(g0)
    c: Vertical(g1)
    c: Distance(g1) = 3
    c: Vertical(g2)
    c: Equal(g0,g2) = 3
    c: Block(g2)
    c: Vertical(g3)
    c: Equal(g1,g3) = 3
    c: Vertical(g4)
    c: Equal(g0,g4) = 3
    c: Block(g4)
    c: Vertical(g5)
    c: Equal(g1,g5) = 3
    c: Vertical(g6)
    c: Equal(g0,g6) = 3
    c: Block(g6)
    c: Vertical(g7)
    c: Equal(g1,g7) = 3
    c: Vertical(g8)
    c: Equal(g0,g8) = 3
    c: Block(g8)
    c: Vertical(g9)
    c: Equal(g1,g9) = 3
    c: Vertical(g10)
    c: Equal(g0,g10) = 3
    c: Block(g10)
    c: Vertical(g11)
    c: Equal(g1,g11) = 3
    c: Block(g12)
    c: Block(g13)
    c: Block(g14)
    c: Block(g15)
    c: Block(g16)
    c: Block(g17)
    c: Block(g18)
    c: Block(g19)
    c: Block(g20)
    c: Block(g21)
    c: Block(g22)
    c: Block(g23)
    c: Block(g11)
    c: Block(g9)
    c: Block(g7)
    c: Block(g5)
    c: Block(g3)
    c: Block(g1)
    c: Coincident(g24,g0)
    c: Coincident(g24,g12)
    c: Horizontal(g24)
    c: Coincident(g25,g0)
    c: Coincident(g25,g12)
    c: Horizontal(g25)
    c: Coincident(g26,g1)
    c: Coincident(g26,g13)
    c: Horizontal(g26)
    c: Coincident(g27,g1)
    c: Coincident(g27,g13)
    c: Horizontal(g27)
    c: Coincident(g28,g2)
    c: Coincident(g28,g14)
    c: Horizontal(g28)
    c: Coincident(g29,g2)
    c: Coincident(g29,g14)
    c: Horizontal(g29)
    c: Coincident(g30,g3)
    c: Coincident(g30,g15)
    c: Horizontal(g30)
    c: Coincident(g31,g3)
    c: Coincident(g31,g15)
    c: Horizontal(g31)
    c: Coincident(g32,g4)
    c: Coincident(g32,g16)
    c: Horizontal(g32)
    c: Coincident(g33,g4)
    c: Coincident(g33,g16)
    c: Horizontal(g33)
    c: Coincident(g34,g5)
    c: Coincident(g34,g17)
    c: Horizontal(g34)
    c: Coincident(g35,g5)
    c: Coincident(g35,g17)
    c: Horizontal(g35)
    c: Coincident(g36,g6)
    c: Coincident(g36,g19)
    c: Horizontal(g36)
    c: Coincident(g37,g6)
    c: Coincident(g37,g19)
    c: Horizontal(g37)
    c: Coincident(g38,g7)
    c: Coincident(g38,g18)
    c: Horizontal(g38)
    c: Coincident(g39,g7)
    c: Coincident(g39,g18)
    c: Horizontal(g39)
    c: Coincident(g40,g8)
    c: Coincident(g40,g20)
    c: Horizontal(g40)
    c: Coincident(g41,g8)
    c: Coincident(g41,g20)
    c: Horizontal(g41)
    c: Coincident(g42,g9)
    c: Coincident(g42,g23)
    c: Horizontal(g42)
    c: Coincident(g43,g9)
    c: Coincident(g43,g23)
    c: Horizontal(g43)
    c: Coincident(g44,g10)
    c: Coincident(g44,g22)
    c: Horizontal(g44)
    c: Coincident(g45,g10)
    c: Coincident(g45,g22)
    c: Horizontal(g45)
    c: Coincident(g46,g11)
    c: Coincident(g46,g21)
    c: Horizontal(g46)
    c: Coincident(g47,g11)
    c: Coincident(g47,g21)
    c: Horizontal(g47)
FEATURE [Part::Extrusion] Extrude061
  Base = -> Sketch070
  Dir = (1,0,0)
  DirMode = 2
  FaceMakerClass = Part::FaceMakerBullseye
  LengthFwd = 23
  LengthRev = 0
  Placement = pos=(-19,0,0) rot=(0,0,1;0rad)
  Solid = true
  Symmetric = false
FEATURE [Part::Fillet] Fillet052  label="removeToCreateVentalationHoles002"
  Base = -> Extrude061
  Edges = <same value as first occurrence — deduplicated (x6 in doc)>
  Placement = pos=(7,0.02,0) rot=(0,0,1;0rad)
FEATURE [Part::MultiFuse] Fusion130  label="bottom013"
  Shapes = -> [Cut054,Cut034]
FEATURE [Part::Cut] Cut055
  Base = -> Fusion130
  Tool = -> Fillet052
FEATURE [Part::Cylinder] Cylinder054
  Angle = 360
  AttacherType = Attacher::AttachEngine3D
  Height = 20
  Placement = pos=(0,0,36.15) rot=(0,0,1;0rad)
  Radius = 4
FEATURE [Sketcher::SketchObject] Sketch071  label="bottomSketch002"
  FullyConstrained = true
  sketch-geometry (32):
    g0: LineSegment StartX=3.3 StartY=-6.03275e-07 StartZ=0 EndX=98 EndY=-6.03275e-07 EndZ=0
    g1: ArcOfCircle CenterX=98 CenterY=19 CenterZ=0 NormalX=0 NormalY=0 NormalZ=1 AngleXU=0 Radius=19 StartAngle=4.71239 EndAngle=5.71103
    g2: LineSegment StartX=6.3 StartY=8 StartZ=0 EndX=3.3 EndY=8 EndZ=0
    g3: LineSegment StartX=3.3 StartY=8 StartZ=0 EndX=3.3 EndY=-6.03275e-07 EndZ=0
    g4: ArcOfCircle CenterX=8.3 CenterY=5 CenterZ=0 NormalX=0 NormalY=0 NormalZ=1 AngleXU=0 Radius=2 StartAngle=3.14159 EndAngle=4.71239
    g5: LineSegment StartX=6.3 StartY=8 StartZ=0 EndX=6.3 EndY=5 EndZ=0
    g6: ArcOfCircle CenterX=98 CenterY=19 CenterZ=0 NormalX=0 NormalY=0 NormalZ=1 AngleXU=0 Radius=12.7 StartAngle=4.71239 EndAngle=6.28319
    g7: LineSegment StartX=94.7 StartY=3 StartZ=0 EndX=8.3 EndY=3 EndZ=0
    g8-g12: Circle x5 (B-spline internal-alignment scaffolding for g13; pole/knot coordinates omitted)
    g13: BSplineCurve PolesCount=5 KnotsCount=3 Degree=3 IsPeriodic=0
    g14: GeomPoint X=98 Y=6.3 Z=0
    g15: GeomPoint X=96.3938 Y=4.71946 Z=0
    g16: GeomPoint X=94.7 Y=3 Z=0
    g17-g23: Circle x7 (B-spline internal-alignment scaffolding for g24; pole/knot coordinates omitted)
    g24: BSplineCurve PolesCount=7 KnotsCount=5 Degree=3 IsPeriodic=0
    g25-g29: GeomPoint x5 (B-spline internal-alignment scaffolding for g24; pole/knot coordinates omitted)
    g30: ArcOfCircle CenterX=98 CenterY=19 CenterZ=0 NormalX=0 NormalY=0 NormalZ=1 AngleXU=0 Radius=15.7 StartAngle=5.81226 EndAngle=6.28319
    g31: LineSegment StartX=110.7 StartY=19 StartZ=0 EndX=113.7 EndY=19 EndZ=0
  constraints (41):
    c: Horizontal(g0)
    c: Coincident(g1,g0)
    c: Block(g1)
    c: Horizontal(g2)
    c: Distance(g2) = 3
    c: Coincident(g3,g2)
    c: Vertical(g3)
    c: Coincident(g3,g0)
    c: Block(g4)
    c: Block(g2)
    c: Coincident(g5,g2)
    c: Coincident(g5,g4)
    c: Vertical(g5)
    c: Coincident(g6,g1)
    c: Block(g6)
    c: Coincident(g7,g4)
    c: Horizontal(g7)
    c: Block(g0)
    c: Block(g7)
    c: Block(g3)
    c: Coincident(g13,g6)
    c: Weight(g8) = 1
    c: Equal(g8, g9-g12) x4
    c: Coincident(g13,g7)
    c: InternalAlignment(g8-g12 -> g13) x5
    c: InternalAlignment(g14,g13)
    c: InternalAlignment(g15,g13)
    c: InternalAlignment(g16,g13)
    c: Block(g13)
    c: Weight(g17) = 1
    c: Equal(g17, g18-g23) x6
    c: Coincident(g24,g1)
    c: InternalAlignment(g17-g23 -> g24) x7
    c: InternalAlignment(g25-g29 -> g24) x5
    c: Block(g24)
    c: Coincident(g30,g24)
    c: Coincident(g31,g6)
    c: Coincident(g31,g30)
    c: Horizontal(g31)
    c: Block(g31)
    c: Block(g30)
FEATURE [Part::Extrusion] Extrude062  label="bottom014"
  Base = -> Sketch071
  Dir = (0,0,1)
  DirMode = 2
  FaceMakerClass = Part::FaceMakerBullseye
  LengthFwd = 71.4
  LengthRev = 0
  Placement = pos=(0,0,0.3) rot=(0,0,1;0rad)
  Solid = true
  Symmetric = false
FEATURE [Part::Fillet] Fillet054
  Base = -> Extrude062
  Edges = 1 edges r=2.4: [Edge17]
FEATURE [Part::Fillet] Fillet055  label="bottom015"
  Base = -> Fillet054
  Edges = 1 edges r=2.4: [Edge36]
FEATURE [Part::Cylinder] Cylinder055
  Angle = 360
  AttacherType = Attacher::AttachEngine3D
  Height = 10
  Placement = pos=(0,0,36.15) rot=(0,0,1;0rad)
  Radius = 4
FEATURE [Part::MultiFuse] Fusion131  label="removeToCreateHoleForPlugHousing002"
  Placement = pos=(70,19,36.15) rot=(0,1,0;1.5708rad)
  Shapes = -> [Cylinder054,Cylinder055]
FEATURE [Part::Cut] Cut056  label="Bottom001"
  Base = -> Fillet055
  Placement = pos=(9,0,0) rot=(0,0,1;0rad)
  Tool = -> Fusion131
FEATURE [Part::Cut] Cut057
  Base = -> Cut055
  Tool = -> Cut056
FEATURE [Sketcher::SketchObject] Sketch072  label="topSketch021"
  FullyConstrained = true
  sketch-geometry (4):
    g0: ArcOfCircle CenterX=105 CenterY=19 CenterZ=0 NormalX=0 NormalY=0 NormalZ=1 AngleXU=0 Radius=20.6155 StartAngle=5.54125 EndAngle=6.28319
    g1: ArcOfCircle CenterX=105 CenterY=19 CenterZ=0 NormalX=0 NormalY=0 NormalZ=1 AngleXU=0 Radius=13 StartAngle=5.54125 EndAngle=6.28319
    g2: LineSegment StartX=118 StartY=19 StartZ=0 EndX=125.616 EndY=19 EndZ=0
    g3: LineSegment StartX=114.583 StartY=10.2157 StartZ=0 EndX=120.197 EndY=5.06982 EndZ=0
  constraints (7):
    c: Block(g0)
    c: Block(g1)
    c: Coincident(g2,g1)
    c: Coincident(g2,g0)
    c: Horizontal(g2)
    c: Coincident(g3,g1)
    c: Coincident(g3,g0)
FEATURE [Part::Extrusion] Extrude063  label="bottomPlugHousingBit003"
  Base = -> Sketch072
  Dir = (0,0,1)
  DirMode = 2
  FaceMakerClass = Part::FaceMakerBullseye
  LengthFwd = 72
  LengthRev = 0
  Solid = true
  Symmetric = false
FEATURE [Part::Cylinder] Cylinder056
  Angle = 360
  AttacherType = Attacher::AttachEngine3D
  Height = 20
  Placement = pos=(0,0,36.15) rot=(0,0,1;0rad)
  Radius = 14.3
FEATURE [Part::Cylinder] Cylinder057
  Angle = 360
  AttacherType = Attacher::AttachEngine3D
  Height = 10
  Placement = pos=(0,0,36.15) rot=(0,0,1;0rad)
  Radius = 4
FEATURE [Part::Box] Box034  label="removeToCreteHoleForPlugHousing047"
  AttacherType = Attacher::AttachEngine3D
  Height = 28.6
  Length = 20
  Placement = pos=(106.15,0,21.7) rot=(0,0,1;0rad)
  Width = 19
FEATURE [Part::Cylinder] Cylinder058
  Angle = 360
  AttacherType = Attacher::AttachEngine3D
  Height = 20
  Placement = pos=(0,0,36.15) rot=(0,0,1;0rad)
  Radius = 14.3
FEATURE [Part::Cylinder] Cylinder059
  Angle = 360
  AttacherType = Attacher::AttachEngine3D
  Height = 10
  Placement = pos=(0,0,36.15) rot=(0,0,1;0rad)
  Radius = 4
FEATURE [Part::MultiFuse] Fusion134  label="removeToCreteHoleForPlugHousing046"
  Placement = pos=(70,19,36) rot=(0,1,0;1.5708rad)
  Shapes = -> [Cylinder058,Cylinder059]
FEATURE [Part::Cylinder] Cylinder060
  Angle = 360
  AttacherType = Attacher::AttachEngine3D
  Height = 20
  Placement = pos=(0,0,36.15) rot=(0,0,1;0rad)
  Radius = 14
FEATURE [Part::Cylinder] Cylinder061
  Angle = 360
  AttacherType = Attacher::AttachEngine3D
  Height = 10
  Placement = pos=(0,0,36.15) rot=(0,0,1;0rad)
  Radius = 4
FEATURE [Part::MultiFuse] Fusion135  label="removeToCreteHoleForPlugHousing048"
  Placement = pos=(70,19,36) rot=(0,1,0;1.5708rad)
  Shapes = -> [Cylinder060,Cylinder061]
FEATURE [Part::Box] Box035  label="removeToCreteHoleForPlugHousing049"
  AttacherType = Attacher::AttachEngine3D
  Height = 28.6
  Length = 20
  Placement = pos=(106.15,0,21.7) rot=(0,0,1;0rad)
  Width = 19
FEATURE [Part::MultiFuse] Fusion133  label="removeToCreteHoleForPlugHousing045"
  Placement = pos=(0,0,-28.3) rot=(0,0,1;0rad)
  Shapes = -> [Box035,Fusion134]
FEATURE [Part::MultiFuse] Fusion138  label="removeToCreteHoleForPlugHousing051"
  Placement = pos=(70,19,36) rot=(0,1,0;1.5708rad)
  Shapes = -> [Cylinder056,Cylinder057]
FEATURE [Part::MultiFuse] Fusion137  label="removeToCreteHoleForPlugHousing050"
  Placement = pos=(0,0,28.3) rot=(0,0,1;0rad)
  Shapes = -> [Box034,Fusion138]
FEATURE [Part::MultiFuse] Fusion132  label="removeToCreatePlugHousingBottomBit002"
  Shapes = -> [Fusion133,Fusion137]
FEATURE [Part::MultiFuse] Fusion136  label="removeToCreatePlugHousingBottomBit003"
  Shapes = -> [Fusion135,Fusion132]
FEATURE [Part::Cut] Cut058  label="bottomPlugHousingBit002"
  Base = -> Extrude063
  Placement = pos=(-0.09,0,0) rot=(0,0,1;0rad)
  Tool = -> Fusion136
FEATURE [Sketcher::SketchObject] Sketch073  label="bottomSketch003"
  FullyConstrained = true
  sketch-geometry (45):
    g0: LineSegment StartX=6.29999 StartY=8 StartZ=0 EndX=3.29999 EndY=8 EndZ=0
    g1: LineSegment StartX=3.29999 StartY=8 StartZ=0 EndX=3.29999 EndY=-6.03275e-07 EndZ=0
    g2: ArcOfCircle CenterX=8.29999 CenterY=5 CenterZ=0 NormalX=0 NormalY=0 NormalZ=1 AngleXU=0 Radius=2 StartAngle=3.14159 EndAngle=4.71239
    g3: LineSegment StartX=6.29999 StartY=8 StartZ=0 EndX=6.29999 EndY=5 EndZ=0
    g4: ArcOfCircle CenterX=105 CenterY=19 CenterZ=0 NormalX=0 NormalY=0 NormalZ=1 AngleXU=0 Radius=12.7 StartAngle=4.71239 EndAngle=5.94289
    g5-g11: Circle x7 (B-spline internal-alignment scaffolding for g12; pole/knot coordinates omitted)
    g12: BSplineCurve PolesCount=7 KnotsCount=5 Degree=3 IsPeriodic=0
    g13-g17: GeomPoint x5 (B-spline internal-alignment scaffolding for g12; pole/knot coordinates omitted)
    g18: ArcOfCircle CenterX=105 CenterY=19 CenterZ=0 NormalX=0 NormalY=0 NormalZ=1 AngleXU=0 Radius=15.7 StartAngle=5.81226 EndAngle=6.28319
    g19: BSplineCurve PolesCount=5 KnotsCount=3 Degree=3 IsPeriodic=0
    g20: LineSegment StartX=8.29999 StartY=3 StartZ=0 EndX=101.7 EndY=3 EndZ=0
    g21: LineSegment StartX=3.29999 StartY=-6.03275e-07 StartZ=0 EndX=105 EndY=-6.03275e-07 EndZ=0
    g22: LineSegment StartX=120.974 StartY=8.71251 StartZ=0 EndX=122.332 EndY=7.83778 EndZ=0
    g23: LineSegment StartX=105 StartY=-6.03274e-07 StartZ=0 EndX=113 EndY=-6.03274e-07 EndZ=0
    g24: ArcOfCircle CenterX=105 CenterY=19 CenterZ=0 NormalX=0 NormalY=0 NormalZ=1 AngleXU=0 Radius=20.6155 StartAngle=5.11091 EndAngle=5.71103
    g25: ArcOfCircle CenterX=117.7 CenterY=19 CenterZ=0 NormalX=0 NormalY=0 NormalZ=1 AngleXU=0 Radius=3 StartAngle=1.2e-15 EndAngle=2.10468
    g26: Circle CenterX=116.345 CenterY=16.3232 CenterZ=0 NormalX=0 NormalY=0 NormalZ=1 AngleXU=0 Radius=1
    g27: Circle CenterX=117.24 CenterY=15.7584 CenterZ=0 NormalX=0 NormalY=0 NormalZ=1 AngleXU=0 Radius=1
    g28: Circle CenterX=116.972 CenterY=14.7612 CenterZ=0 NormalX=0 NormalY=0 NormalZ=1 AngleXU=0 Radius=1
    g29: BSplineCurve PolesCount=3 KnotsCount=2 Degree=2 IsPeriodic=0
    g30: GeomPoint X=116.345 Y=16.3232 Z=0
    g31: GeomPoint X=116.972 Y=14.7612 Z=0
    g32: Circle CenterX=115.828 CenterY=17.157 CenterZ=0 NormalX=0 NormalY=0 NormalZ=1 AngleXU=0 Radius=1
    g33: Circle CenterX=115.841 CenterY=16.639 CenterZ=0 NormalX=0 NormalY=0 NormalZ=1 AngleXU=0 Radius=1
    g34: Circle CenterX=116.345 CenterY=16.3232 CenterZ=0 NormalX=0 NormalY=0 NormalZ=1 AngleXU=0 Radius=1
    g35: BSplineCurve PolesCount=3 KnotsCount=2 Degree=2 IsPeriodic=0
    g36: GeomPoint X=115.828 Y=17.157 Z=0
    g37: GeomPoint X=116.345 Y=16.3232 Z=0
    g38: LineSegment StartX=115.828 StartY=17.157 StartZ=0 EndX=115.828 EndY=20.8307 EndZ=0
    g39: Circle CenterX=115.828 CenterY=20.8307 CenterZ=0 NormalX=0 NormalY=0 NormalZ=1 AngleXU=0 Radius=1
    g40: Circle CenterX=115.831 CenterY=21.3396 CenterZ=0 NormalX=0 NormalY=0 NormalZ=1 AngleXU=0 Radius=1
    g41: Circle CenterX=116.173 CenterY=21.5825 CenterZ=0 NormalX=0 NormalY=0 NormalZ=1 AngleXU=0 Radius=1
    g42: BSplineCurve PolesCount=3 KnotsCount=2 Degree=2 IsPeriodic=0
    g43: GeomPoint X=115.828 Y=20.8307 Z=0
    g44: GeomPoint X=116.173 Y=21.5825 Z=0
  constraints (70):
    c: Horizontal(g0)
    c: Distance(g0) = 3
    c: Coincident(g1,g0)
    c: Vertical(g1)
    c: Block(g2)
    c: Block(g0)
    c: Coincident(g3,g0)
    c: Coincident(g3,g2)
    c: Vertical(g3)
    c: Block(g1)
    c: Block(g4)
    c: Coincident(g19,g4)
    c: Block(g19)
    c: Equal(g5, g6-g11) x6
    c: InternalAlignment(g5-g11 -> g12) x7
    c: InternalAlignment(g13-g17 -> g12) x5
    c: Block(g12)
    c: Coincident(g18,g12)
    c: Block(g18)
    c: Coincident(g20,g2)
    c: Coincident(g20,g19)
    c: Horizontal(g20)
    c: Distance(g20) = 93.4
    c: Coincident(g21,g1)
    c: Horizontal(g21)
    c: Distance(g21) = 101.7
    c: Horizontal(g23)
    c: Distance(g23) = 8
    c: Coincident(g24,g23)
    c: Block(g23)
    c: Coincident(g22,g24)
    c: Block(g24)
    c: Block(g22)
    c: Distance(g22) = 1.61553
    c: Coincident(g25,g18)
    c: Block(g25)
    c: Weight(g26) = 1
    c: Equal(g26,g27)
    c: Equal(g26,g28)
    c: Coincident(g29,g4)
    c: InternalAlignment(g26,g29)
    c: InternalAlignment(g27,g29)
    c: InternalAlignment(g28,g29)
    c: InternalAlignment(g30,g29)
    c: InternalAlignment(g31,g29)
    c: Block(g29)
    c: Weight(g32) = 1
    c: Equal(g32,g33)
    c: Equal(g32,g34)
    c: Coincident(g35,g29)
    c: InternalAlignment(g32,g35)
    c: InternalAlignment(g33,g35)
    c: InternalAlignment(g34,g35)
    c: InternalAlignment(g36,g35)
    c: InternalAlignment(g37,g35)
    c: Block(g35)
    c: Coincident(g38,g35)
    c: Vertical(g38)
    c: Block(g38)
    c: Coincident(g42,g38)
    c: Weight(g39) = 1
    c: Equal(g39,g40)
    c: Equal(g39,g41)
    c: Coincident(g42,g25)
    c: InternalAlignment(g39,g42)
    c: InternalAlignment(g40,g42)
    c: InternalAlignment(g41,g42)
    c: InternalAlignment(g43,g42)
    c: InternalAlignment(g44,g42)
    c: Block(g42)
FEATURE [Part::Extrusion] Extrude064  label="bottom016"
  Base = -> Sketch073
  Dir = (0,0,1)
  DirMode = 2
  FaceMakerClass = Part::FaceMakerBullseye
  LengthFwd = 71.4
  LengthRev = 0
  Placement = pos=(0,0,0.3) rot=(0,0,1;0rad)
  Solid = true
  Symmetric = false
FEATURE [Part::Revolution] Revolve157  label="removeToCreateScrewAndThreadedInsertHole063"
  Angle = 360
  Axis = (0,1,0)
  Base = (0,0,0)
  FaceMakerClass = Part::FaceMakerBullseye
  Placement = pos=(12.5,0,10) rot=(0,0,1;0rad)
  Solid = false
  Source = -> Face141
  Symmetric = false
FEATURE [Sketcher::SketchObject] Sketch074
  FullyConstrained = true
  Placement = pos=(117,19,0) rot=(0.57735,0.57735,0.57735;2.0944rad)
  sketch-geometry (48):
    g0: LineSegment StartX=-49.19 StartY=69.25 StartZ=0 EndX=-49.19 EndY=66.25 EndZ=0
    g1: LineSegment StartX=-49.19 StartY=63.5 StartZ=0 EndX=-49.19 EndY=60.5 EndZ=0
    g2: LineSegment StartX=-49.19 StartY=57.75 StartZ=0 EndX=-49.19 EndY=54.75 EndZ=0
    g3: LineSegment StartX=-49.19 StartY=52 StartZ=0 EndX=-49.19 EndY=49 EndZ=0
    g4: LineSegment StartX=-49.19 StartY=46.25 StartZ=0 EndX=-49.19 EndY=43.25 EndZ=0
    g5: LineSegment StartX=-49.19 StartY=40.5 StartZ=0 EndX=-49.19 EndY=37.5 EndZ=0
    g6: LineSegment StartX=-49.19 StartY=34.5 StartZ=0 EndX=-49.19 EndY=31.5 EndZ=0
    g7: LineSegment StartX=-49.19 StartY=28.75 StartZ=0 EndX=-49.19 EndY=25.75 EndZ=0
    g8: LineSegment StartX=-49.19 StartY=23 StartZ=0 EndX=-49.19 EndY=20 EndZ=0
    g9: LineSegment StartX=-49.19 StartY=17.25 StartZ=0 EndX=-49.19 EndY=14.25 EndZ=0
    g10: LineSegment StartX=-49.19 StartY=11.5 StartZ=0 EndX=-49.19 EndY=8.5 EndZ=0
    g11: LineSegment StartX=-49.19 StartY=5.75 StartZ=0 EndX=-49.19 EndY=2.75 EndZ=0
    g12: ArcOfCircle CenterX=-1.5 CenterY=67.75 CenterZ=0 NormalX=0 NormalY=0 NormalZ=1 AngleXU=0 Radius=1.5 StartAngle=4.71239 EndAngle=7.85398
    g13: ArcOfCircle CenterX=-1.5 CenterY=62 CenterZ=0 NormalX=0 NormalY=0 NormalZ=1 AngleXU=0 Radius=1.5 StartAngle=4.71239 EndAngle=7.85398
    g14: ArcOfCircle CenterX=-1.5 CenterY=56.25 CenterZ=0 NormalX=0 NormalY=0 NormalZ=1 AngleXU=0 Radius=1.5 StartAngle=4.71239 EndAngle=7.85398
    g15: ArcOfCircle CenterX=-11.49 CenterY=50.5 CenterZ=0 NormalX=0 NormalY=0 NormalZ=1 AngleXU=0 Radius=1.5 StartAngle=4.71239 EndAngle=7.85398
    g16: ArcOfCircle CenterX=-16.28 CenterY=44.75 CenterZ=0 NormalX=0 NormalY=0 NormalZ=1 AngleXU=0 Radius=1.5 StartAngle=4.71239 EndAngle=7.85398
    g17: ArcOfCircle CenterX=-18.2337 CenterY=39 CenterZ=0 NormalX=0 NormalY=0 NormalZ=1 AngleXU=0 Radius=1.5 StartAngle=4.71485 EndAngle=7.85398
    g18: ArcOfCircle CenterX=-16.2837 CenterY=27.25 CenterZ=0 NormalX=0 NormalY=0 NormalZ=1 AngleXU=0 Radius=1.5 StartAngle=4.71485 EndAngle=7.85398
    g19: ArcOfCircle CenterX=-18.2337 CenterY=33 CenterZ=0 NormalX=0 NormalY=0 NormalZ=1 AngleXU=0 Radius=1.5 StartAngle=4.71485 EndAngle=7.85398
    g20: ArcOfCircle CenterX=-11.49 CenterY=21.5 CenterZ=0 NormalX=0 NormalY=0 NormalZ=1 AngleXU=0 Radius=1.5 StartAngle=4.71239 EndAngle=7.85398
    g21: ArcOfCircle CenterX=-1.5 CenterY=4.25 CenterZ=0 NormalX=0 NormalY=0 NormalZ=1 AngleXU=0 Radius=1.5 StartAngle=4.71239 EndAngle=7.85398
    g22: ArcOfCircle CenterX=-1.5 CenterY=10 CenterZ=0 NormalX=0 NormalY=0 NormalZ=1 AngleXU=0 Radius=1.5 StartAngle=4.71239 EndAngle=7.85398
    g23: ArcOfCircle CenterX=-1.5 CenterY=15.75 CenterZ=0 NormalX=0 NormalY=0 NormalZ=1 AngleXU=0 Radius=1.5 StartAngle=4.71239 EndAngle=7.85398
    g24: LineSegment StartX=-49.19 StartY=69.25 StartZ=0 EndX=-1.5 EndY=69.25 EndZ=0
    g25: LineSegment StartX=-49.19 StartY=66.25 StartZ=0 EndX=-1.5 EndY=66.25 EndZ=0
    g26: LineSegment StartX=-49.19 StartY=63.5 StartZ=0 EndX=-1.5 EndY=63.5 EndZ=0
    g27: LineSegment StartX=-49.19 StartY=60.5 StartZ=0 EndX=-1.5 EndY=60.5 EndZ=0
    g28: LineSegment StartX=-49.19 StartY=57.75 StartZ=0 EndX=-1.5 EndY=57.75 EndZ=0
    g29: LineSegment StartX=-49.19 StartY=54.75 StartZ=0 EndX=-1.5 EndY=54.75 EndZ=0
    g30: LineSegment StartX=-49.19 StartY=52 StartZ=0 EndX=-11.49 EndY=52 EndZ=0
    g31: LineSegment StartX=-49.19 StartY=49 StartZ=0 EndX=-11.49 EndY=49 EndZ=0
    g32: LineSegment StartX=-49.19 StartY=46.25 StartZ=0 EndX=-16.28 EndY=46.25 EndZ=0
    g33: LineSegment StartX=-49.19 StartY=43.25 StartZ=0 EndX=-16.28 EndY=43.25 EndZ=0
    g34: LineSegment StartX=-49.19 StartY=40.5 StartZ=0 EndX=-18.2337 EndY=40.5 EndZ=0
    g35: LineSegment StartX=-49.19 StartY=37.5 StartZ=0 EndX=-18.23 EndY=37.5 EndZ=0
    g36: LineSegment StartX=-49.19 StartY=34.5 StartZ=0 EndX=-18.2337 EndY=34.5 EndZ=0
    g37: LineSegment StartX=-49.19 StartY=31.5 StartZ=0 EndX=-18.23 EndY=31.5 EndZ=0
    g38: LineSegment StartX=-49.19 StartY=28.75 StartZ=0 EndX=-16.2837 EndY=28.75 EndZ=0
    g39: LineSegment StartX=-49.19 StartY=25.75 StartZ=0 EndX=-16.28 EndY=25.75 EndZ=0
    g40: LineSegment StartX=-49.19 StartY=23 StartZ=0 EndX=-11.49 EndY=23 EndZ=0
    g41: LineSegment StartX=-49.19 StartY=20 StartZ=0 EndX=-11.49 EndY=20 EndZ=0
    g42: LineSegment StartX=-49.19 StartY=17.25 StartZ=0 EndX=-1.5 EndY=17.25 EndZ=0
    g43: LineSegment StartX=-49.19 StartY=14.25 StartZ=0 EndX=-1.5 EndY=14.25 EndZ=0
    g44: LineSegment StartX=-49.19 StartY=11.5 StartZ=0 EndX=-1.5 EndY=11.5 EndZ=0
    g45: LineSegment StartX=-49.19 StartY=8.5 StartZ=0 EndX=-1.5 EndY=8.5 EndZ=0
    g46: LineSegment StartX=-49.19 StartY=5.75 StartZ=0 EndX=-1.5 EndY=5.75 EndZ=0
    g47: LineSegment StartX=-49.19 StartY=2.75 StartZ=0 EndX=-1.5 EndY=2.75 EndZ=0
  constraints (120):
    c: Vertical(g0)
    c: Distance(g0) = 3
    c: Block(g0)
    c: Vertical(g1)
    c: Distance(g1) = 3
    c: Vertical(g2)
    c: Equal(g0,g2) = 3
    c: Block(g2)
    c: Vertical(g3)
    c: Equal(g1,g3) = 3
    c: Vertical(g4)
    c: Equal(g0,g4) = 3
    c: Block(g4)
    c: Vertical(g5)
    c: Equal(g1,g5) = 3
    c: Vertical(g6)
    c: Equal(g0,g6) = 3
    c: Block(g6)
    c: Vertical(g7)
    c: Equal(g1,g7) = 3
    c: Vertical(g8)
    c: Equal(g0,g8) = 3
    c: Block(g8)
    c: Vertical(g9)
    c: Equal(g1,g9) = 3
    c: Vertical(g10)
    c: Equal(g0,g10) = 3
    c: Block(g10)
    c: Vertical(g11)
    c: Equal(g1,g11) = 3
    c: Block(g12)
    c: Block(g13)
    c: Block(g14)
    c: Block(g15)
    c: Block(g16)
    c: Block(g17)
    c: Block(g18)
    c: Block(g19)
    c: Block(g20)
    c: Block(g21)
    c: Block(g22)
    c: Block(g23)
    c: Block(g11)
    c: Block(g9)
    c: Block(g7)
    c: Block(g5)
    c: Block(g3)
    c: Block(g1)
    c: Coincident(g24,g0)
    c: Coincident(g24,g12)
    c: Horizontal(g24)
    c: Coincident(g25,g0)
    c: Coincident(g25,g12)
    c: Horizontal(g25)
    c: Coincident(g26,g1)
    c: Coincident(g26,g13)
    c: Horizontal(g26)
    c: Coincident(g27,g1)
    c: Coincident(g27,g13)
    c: Horizontal(g27)
    c: Coincident(g28,g2)
    c: Coincident(g28,g14)
    c: Horizontal(g28)
    c: Coincident(g29,g2)
    c: Coincident(g29,g14)
    c: Horizontal(g29)
    c: Coincident(g30,g3)
    c: Coincident(g30,g15)
    c: Horizontal(g30)
    c: Coincident(g31,g3)
    c: Coincident(g31,g15)
    c: Horizontal(g31)
    c: Coincident(g32,g4)
    c: Coincident(g32,g16)
    c: Horizontal(g32)
    c: Coincident(g33,g4)
    c: Coincident(g33,g16)
    c: Horizontal(g33)
    c: Coincident(g34,g5)
    c: Coincident(g34,g17)
    c: Horizontal(g34)
    c: Coincident(g35,g5)
    c: Coincident(g35,g17)
    c: Horizontal(g35)
    c: Coincident(g36,g6)
    c: Coincident(g36,g19)
    c: Horizontal(g36)
    c: Coincident(g37,g6)
    c: Coincident(g37,g19)
    c: Horizontal(g37)
    c: Coincident(g38,g7)
    c: Coincident(g38,g18)
    c: Horizontal(g38)
    c: Coincident(g39,g7)
    c: Coincident(g39,g18)
    c: Horizontal(g39)
    c: Coincident(g40,g8)
    c: Coincident(g40,g20)
    c: Horizontal(g40)
    c: Coincident(g41,g8)
    c: Coincident(g41,g20)
    c: Horizontal(g41)
    c: Coincident(g42,g9)
    c: Coincident(g42,g23)
    c: Horizontal(g42)
    c: Coincident(g43,g9)
    c: Coincident(g43,g23)
    c: Horizontal(g43)
    c: Coincident(g44,g10)
    c: Coincident(g44,g22)
    c: Horizontal(g44)
    c: Coincident(g45,g10)
    c: Coincident(g45,g22)
    c: Horizontal(g45)
    c: Coincident(g46,g11)
    c: Coincident(g46,g21)
    c: Horizontal(g46)
    c: Coincident(g47,g11)
    c: Coincident(g47,g21)
    c: Horizontal(g47)
FEATURE [Part::Extrusion] Extrude065
  Base = -> Sketch074
  Dir = (1,0,0)
  DirMode = 2
  FaceMakerClass = Part::FaceMakerBullseye
  LengthFwd = 23
  LengthRev = 0
  Placement = pos=(-19,0,0) rot=(0,0,1;0rad)
  Solid = true
  Symmetric = false
FEATURE [Part::Fillet] Fillet056  label="removeToCreateVentalationHoles003"
  Base = -> Extrude065
  Edges = <same value as first occurrence — deduplicated (x6 in doc)>
  Placement = pos=(7,0.02,0) rot=(0,0,1;0rad)
FEATURE [Part::Revolution] Revolve158  label="removeToCreateScrewAndThreadedInsertHole065"
  Angle = 360
  Axis = (0,1,0)
  Base = (0,0,0)
  FaceMakerClass = Part::FaceMakerBullseye
  Placement = pos=(12.5,0,62) rot=(0,0,1;0rad)
  Solid = false
  Source = -> Face146
  Symmetric = false
FEATURE [Part::Revolution] Revolve159  label="removeToCreateScrewAndThreadedInsertHole066"
  Angle = 360
  Axis = (0,1,0)
  Base = (0,0,0)
  FaceMakerClass = Part::FaceMakerBullseye
  Placement = pos=(89.5,0,68.5) rot=(0,0,1;0rad)
  Solid = false
  Source = -> Face143
  Symmetric = false
FEATURE [Part::Revolution] Revolve160  label="removeToCreateScrewAndThreadedInsertHole067"
  Angle = 360
  Axis = (0,1,0)
  Base = (0,0,0)
  FaceMakerClass = Part::FaceMakerBullseye
  Placement = pos=(89.5,0,3.5) rot=(0,0,1;0rad)
  Solid = false
  Source = -> Face142
  Symmetric = false
FEATURE [Part::Revolution] Revolve161  label="removeToCreateScrewAndThreadedInsertHole068"
  Angle = 360
  Axis = (0,1,0)
  Base = (0,0,0)
  FaceMakerClass = Part::FaceMakerBullseye
  Placement = pos=(109.5,4.7,3.5) rot=(0,0,1;0rad)
  Solid = false
  Source = -> Face145
  Symmetric = false
FEATURE [Part::Revolution] Revolve162  label="removeToCreateScrewAndThreadedInsertHole069"
  Angle = 360
  Axis = (0,1,0)
  Base = (0,0,0)
  FaceMakerClass = Part::FaceMakerBullseye
  Placement = pos=(109.5,4.7,68.5) rot=(0,0,1;0rad)
  Solid = false
  Source = -> Face144
  Symmetric = false
FEATURE [Part::MultiFuse] Fusion141  label="removeToCreateScrewAndThreadedInsertHole064"
  Shapes = -> [Revolve162,Revolve161,Revolve160,Revolve159,Revolve158,Revolve157]
FEATURE [Part::Cylinder] Cylinder062
  Angle = 360
  AttacherType = Attacher::AttachEngine3D
  Height = 20
  Placement = pos=(0,0,36.15) rot=(0,0,1;0rad)
  Radius = 14
FEATURE [Part::Cylinder] Cylinder063
  Angle = 360
  AttacherType = Attacher::AttachEngine3D
  Height = 10
  Placement = pos=(0,0,36.15) rot=(0,0,1;0rad)
  Radius = 4
FEATURE [Part::MultiFuse] Fusion139  label="removeToCreteHoleForPlugHousing052"
  Placement = pos=(70,19,36) rot=(0,1,0;1.5708rad)
  Shapes = -> [Cylinder062,Cylinder063]
FEATURE [Part::Cut] Cut060  label="bottom017"
  Base = -> Extrude064
  Tool = -> Fusion139
FEATURE [Part::Cut] Cut061  label="bottom019"
  Base = -> Cut060
  Tool = -> Fusion141
FEATURE [Part::MultiFuse] Fusion140  label="bottom018"
  Shapes = -> [Cut061,Cut058]
FEATURE [Part::Cut] Cut059  label="bottom020"
  Base = -> Fusion140
  Tool = -> Fillet056
FEATURE [Part::Box] Box036  label="Cube021"
  AttacherType = Attacher::AttachEngine3D
  Height = 80
  Length = 26
  Placement = pos=(0,-1,-5) rot=(0,0,1;0rad)
  Width = 11
FEATURE [Part::Cut] Cut062  label="removeFromBottom002"
  Base = -> Cut057
  Tool = -> Box036
FEATURE [Part::Cut] Cut063
  Base = -> Cut059
  Tool = -> Cut062
FEATURE [Part::Cut] Cut064  label="pcbStands"
  Base = -> Fusion095
  Tool = -> Fusion127
FEATURE [Sketcher::SketchObject] Sketch075  label="topSketch022"
  FullyConstrained = true
  sketch-geometry (6):
    g0: LineSegment StartX=19 StartY=38 StartZ=0 EndX=117 EndY=38 EndZ=0
    g1: ArcOfCircle CenterX=19 CenterY=19 CenterZ=0 NormalX=0 NormalY=0 NormalZ=1 AngleXU=0 Radius=19 StartAngle=1.5708 EndAngle=3.14159
    g2: LineSegment StartX=117 StartY=38 StartZ=0 EndX=117 EndY=19 EndZ=0
    g3: LineSegment StartX=98 StartY=1.0161e-12 StartZ=0 EndX=5.22862e-06 EndY=1.0161e-12 EndZ=0
    g4: LineSegment StartX=5.22862e-06 StartY=19 StartZ=0 EndX=5.22862e-06 EndY=1.0161e-12 EndZ=0
    g5: ArcOfCircle CenterX=98 CenterY=19 CenterZ=0 NormalX=0 NormalY=0 NormalZ=1 AngleXU=0 Radius=19 StartAngle=4.71239 EndAngle=6.28319
  constraints (16):
    c: Horizontal(g0)
    c: Distance(g0) = 98
    c: Coincident(g1,g0)
    c: Block(g1)
    c: Coincident(g2,g0)
    c: Vertical(g2)
    c: Distance(g2) = 19
    c: Horizontal(g3)
    c: Coincident(g4,g1)
    c: Vertical(g4)
    c: Coincident(g3,g4)
    c: Block(g3)
    c: Coincident(g5,g2)
    c: Coincident(g5,g3)
    c: Block(g0)
    c: Block(g5)
FEATURE [Part::Extrusion] Extrude067  label="sideB003"
  Base = -> Sketch075
  Dir = (0,0,1)
  DirMode = 2
  FaceMakerClass = Part::FaceMakerBullseye
  LengthFwd = 3
  LengthRev = 0
  Placement = pos=(0,0,71.7) rot=(0,0,1;0rad)
  Solid = true
  Symmetric = false
FEATURE [Sketcher::SketchObject] Sketch076  label="topSketch023"
  FullyConstrained = true
  sketch-geometry (6):
    g0: LineSegment StartX=19 StartY=38 StartZ=0 EndX=117 EndY=38 EndZ=0
    g1: ArcOfCircle CenterX=19 CenterY=19 CenterZ=0 NormalX=0 NormalY=0 NormalZ=1 AngleXU=0 Radius=19 StartAngle=1.5708 EndAngle=3.14159
    g2: LineSegment StartX=117 StartY=38 StartZ=0 EndX=117 EndY=19 EndZ=0
    g3: LineSegment StartX=98 StartY=1.0161e-12 StartZ=0 EndX=5.22862e-06 EndY=1.0161e-12 EndZ=0
    g4: LineSegment StartX=5.22862e-06 StartY=19 StartZ=0 EndX=5.22862e-06 EndY=1.0161e-12 EndZ=0
    g5: ArcOfCircle CenterX=98 CenterY=19 CenterZ=0 NormalX=0 NormalY=0 NormalZ=1 AngleXU=0 Radius=19 StartAngle=4.71239 EndAngle=6.28319
  constraints (16):
    c: Horizontal(g0)
    c: Distance(g0) = 98
    c: Coincident(g1,g0)
    c: Block(g1)
    c: Coincident(g2,g0)
    c: Vertical(g2)
    c: Distance(g2) = 19
    c: Horizontal(g3)
    c: Coincident(g4,g1)
    c: Vertical(g4)
    c: Coincident(g3,g4)
    c: Block(g3)
    c: Coincident(g5,g2)
    c: Coincident(g5,g3)
    c: Block(g0)
    c: Block(g5)
FEATURE [Part::Extrusion] Extrude066  label="sideA003"
  Base = -> Sketch076
  Dir = (0,0,1)
  DirMode = 2
  FaceMakerClass = Part::FaceMakerBullseye
  LengthFwd = 3
  LengthRev = 0
  Placement = pos=(0,0,-2.7) rot=(0,0,1;0rad)
  Solid = true
  Symmetric = false
FEATURE [Part::MultiFuse] Fusion142  label="removeFromBottom003"
  Placement = pos=(2,0,0) rot=(0,0,1;0rad)
  Shapes = -> [Extrude066,Extrude067]
FEATURE [Part::Cut] Cut065  label="screwRetainers002"
  Base = -> Fusion096
  Tool = -> Fusion142
FEATURE [Sketcher::SketchObject] Sketch077
  FullyConstrained = true
  Placement = pos=(117,19,0) rot=(0.57735,0.57735,0.57735;2.0944rad)
  sketch-geometry (8):
    g0: LineSegment StartX=-49.19 StartY=63.5 StartZ=0 EndX=-49.19 EndY=60.5 EndZ=0
    g1: LineSegment StartX=-49.19 StartY=11.5 StartZ=0 EndX=-49.19 EndY=8.5 EndZ=0
    g2: ArcOfCircle CenterX=-1.5 CenterY=62 CenterZ=0 NormalX=0 NormalY=0 NormalZ=1 AngleXU=0 Radius=1.5 StartAngle=4.71239 EndAngle=7.85398
    g3: ArcOfCircle CenterX=-1.5 CenterY=10 CenterZ=0 NormalX=0 NormalY=0 NormalZ=1 AngleXU=0 Radius=1.5 StartAngle=4.71239 EndAngle=7.85398
    g4: LineSegment StartX=-49.19 StartY=63.5 StartZ=0 EndX=-1.5 EndY=63.5 EndZ=0
    g5: LineSegment StartX=-49.19 StartY=60.5 StartZ=0 EndX=-1.5 EndY=60.5 EndZ=0
    g6: LineSegment StartX=-49.19 StartY=11.5 StartZ=0 EndX=-1.5 EndY=11.5 EndZ=0
    g7: LineSegment StartX=-49.19 StartY=8.5 StartZ=0 EndX=-1.5 EndY=8.5 EndZ=0
  constraints (19):
    c: Vertical(g0)
    c: Distance(g0) = 3
    c: Vertical(g1)
    c: Block(g1)
    c: Block(g2)
    c: Block(g3)
    c: Block(g0)
    c: Coincident(g4,g0)
    c: Coincident(g4,g2)
    c: Horizontal(g4)
    c: Coincident(g5,g0)
    c: Coincident(g5,g2)
    c: Horizontal(g5)
    c: Coincident(g6,g1)
    c: Coincident(g6,g3)
    c: Horizontal(g6)
    c: Coincident(g7,g1)
    c: Coincident(g7,g3)
    c: Horizontal(g7)
FEATURE [Part::Extrusion] Extrude068
  Base = -> Sketch077
  Dir = (1,0,0)
  DirMode = 2
  FaceMakerClass = Part::FaceMakerBullseye
  LengthFwd = 10
  LengthRev = 0
  Solid = true
  Symmetric = false
FEATURE [Part::Fillet] Fillet057  label="removeFromtMoreFrontCaseScrewRetainers002"
  Base = -> Extrude068
  Edges = 4 edges r=1.49: [Edge6,Edge11,Edge18,Edge23]
  Placement = pos=(-12,0,0) rot=(0,0,1;0rad)
FEATURE [Sketcher::SketchObject] Sketch078
  FullyConstrained = true
  Placement = pos=(117,19,0) rot=(0.57735,0.57735,0.57735;2.0944rad)
  sketch-geometry (8):
    g0: LineSegment StartX=-49.19 StartY=69.25 StartZ=0 EndX=-49.19 EndY=66.25 EndZ=0
    g1: LineSegment StartX=-49.19 StartY=5.75 StartZ=0 EndX=-49.19 EndY=2.75 EndZ=0
    g2: ArcOfCircle CenterX=-1.5 CenterY=67.75 CenterZ=0 NormalX=0 NormalY=0 NormalZ=1 AngleXU=0 Radius=1.5 StartAngle=4.71239 EndAngle=7.85398
    g3: ArcOfCircle CenterX=-1.5 CenterY=4.25 CenterZ=0 NormalX=0 NormalY=0 NormalZ=1 AngleXU=0 Radius=1.5 StartAngle=4.71239 EndAngle=7.85398
    g4: LineSegment StartX=-49.19 StartY=69.25 StartZ=0 EndX=-1.5 EndY=69.25 EndZ=0
    g5: LineSegment StartX=-49.19 StartY=66.25 StartZ=0 EndX=-1.5 EndY=66.25 EndZ=0
    g6: LineSegment StartX=-49.19 StartY=5.75 StartZ=0 EndX=-1.5 EndY=5.75 EndZ=0
    g7: LineSegment StartX=-49.19 StartY=2.75 StartZ=0 EndX=-1.5 EndY=2.75 EndZ=0
  constraints (19):
    c: Vertical(g0)
    c: Distance(g0) = 3
    c: Block(g0)
    c: Vertical(g1)
    c: Block(g2)
    c: Block(g3)
    c: Block(g1)
    c: Coincident(g4,g0)
    c: Coincident(g4,g2)
    c: Horizontal(g4)
    c: Coincident(g5,g0)
    c: Coincident(g5,g2)
    c: Horizontal(g5)
    c: Coincident(g6,g1)
    c: Coincident(g6,g3)
    c: Horizontal(g6)
    c: Coincident(g7,g1)
    c: Coincident(g7,g3)
    c: Horizontal(g7)
FEATURE [Part::Extrusion] Extrude069
  Base = -> Sketch078
  Dir = (1,0,0)
  DirMode = 2
  FaceMakerClass = Part::FaceMakerBullseye
  LengthFwd = 10
  LengthRev = 0
  Solid = true
  Symmetric = false
FEATURE [Part::Fillet] Fillet058  label="removeFromtMoreFrontCaseScrewRetainers003"
  Base = -> Extrude069
  Edges = 4 edges r=1.49: [Edge6,Edge11,Edge18,Edge23]
  Placement = pos=(-4,0,0) rot=(0,0,1;0rad)
FEATURE [Part::Cut] Cut066
  Base = -> Cut065
  Tool = -> Fillet058
FEATURE [Part::Cut] Cut067  label="screwPillars"
  Base = -> Cut066
  Tool = -> Fillet057
FEATURE [Part::MultiFuse] Fusion143  label="bottom021"
  Shapes = -> [Cut031,Cut063]
FEATURE [Part::Cylinder] Cylinder
  Angle = 360
  AttacherType = Attacher::AttachEngine3D
  Height = 10
  Placement = pos=(20.65,12,4.68) rot=(1,0,0;1.5708rad)
  Radius = 2
FEATURE [Part::Cylinder] Cylinder064
  Angle = 360
  AttacherType = Attacher::AttachEngine3D
  Height = 10
  Placement = pos=(20.65,12,67.38) rot=(1,0,0;1.5708rad)
  Radius = 2
FEATURE [Part::Cylinder] Cylinder065
  Angle = 360
  AttacherType = Attacher::AttachEngine3D
  Height = 10
  Placement = pos=(77.15,12,67.38) rot=(1,0,0;1.5708rad)
  Radius = 2
FEATURE [Part::Cylinder] Cylinder066
  Angle = 360
  AttacherType = Attacher::AttachEngine3D
  Height = 10
  Placement = pos=(77.15,12,4.68) rot=(1,0,0;1.5708rad)
  Radius = 2
FEATURE [Part::MultiFuse] Fusion144  label="removeFromThreadedInsertHousing"
  Shapes = -> [Cylinder065,Cylinder064,Cylinder,Cylinder066]
FEATURE [Part::Cut] Cut068  label="pcbStands001"
  Base = -> Cut064
  Tool = -> Fusion144
FEATURE [Part::MultiFuse] Fusion145
  Shapes = -> [Cut068,Fusion143]
FEATURE [Part::MultiFuse] Fusion146
  Shapes = -> [Fusion145]
FEATURE [Part::MultiFuse] Fusion147  label="bottom022"
  Shapes = -> [Cut067,Fusion146]
FEATURE [Part::MultiFuse] Fusion148  label="casePillars005"
  Shapes = -> [Cut047,Fusion092]
FEATURE [Part::MultiFuse] Fusion149  label="bottom023"
  Shapes = -> [Fusion124,Fusion113,Fusion147]
FEATURE [Part::MultiFuse] Fusion150  label="topBits"
  Shapes = -> [Cut025,Fusion148,Cut030,Fillet034]
FEATURE [Part::Feature] Face149 .. Face152  x4 (patterned run collapsed; names and placements below)
  shape: bbox 3.2 x 1.5 x 2e-07 mm, 1 faces, 0 solids (baked)
FEATURE [Part::Feature] Face153
  shape: bbox 3.6 x 3.2 x 2e-07 mm, 1 faces, 0 solids (baked)
FEATURE [Part::Feature] Face154
  shape: bbox 3.6 x 3.2 x 2e-07 mm, 1 faces, 0 solids (baked)
FEATURE [Sketcher::SketchObject] Sketch079  label="topSketch024"
  FullyConstrained = true
  sketch-geometry (6):
    g0: LineSegment StartX=19 StartY=38 StartZ=0 EndX=117 EndY=38 EndZ=0
    g1: ArcOfCircle CenterX=19 CenterY=19 CenterZ=0 NormalX=0 NormalY=0 NormalZ=1 AngleXU=0 Radius=19 StartAngle=1.5708 EndAngle=3.14159
    g2: LineSegment StartX=117 StartY=38 StartZ=0 EndX=117 EndY=19 EndZ=0
    g3: LineSegment StartX=98 StartY=1.0161e-12 StartZ=0 EndX=5.22862e-06 EndY=1.0161e-12 EndZ=0
    g4: LineSegment StartX=5.22862e-06 StartY=19 StartZ=0 EndX=5.22862e-06 EndY=1.0161e-12 EndZ=0
    g5: ArcOfCircle CenterX=98 CenterY=19 CenterZ=0 NormalX=0 NormalY=0 NormalZ=1 AngleXU=0 Radius=19 StartAngle=4.71239 EndAngle=6.28319
  constraints (16):
    c: Horizontal(g0)
    c: Distance(g0) = 98
    c: Coincident(g1,g0)
    c: Block(g1)
    c: Coincident(g2,g0)
    c: Vertical(g2)
    c: Distance(g2) = 19
    c: Horizontal(g3)
    c: Coincident(g4,g1)
    c: Vertical(g4)
    c: Coincident(g3,g4)
    c: Block(g3)
    c: Coincident(g5,g2)
    c: Coincident(g5,g3)
    c: Block(g0)
    c: Block(g5)
FEATURE [Sketcher::SketchObject] Sketch080  label="topSketch025"
  FullyConstrained = true
  sketch-geometry (6):
    g0: LineSegment StartX=19 StartY=38 StartZ=0 EndX=117 EndY=38 EndZ=0
    g1: ArcOfCircle CenterX=19 CenterY=19 CenterZ=0 NormalX=0 NormalY=0 NormalZ=1 AngleXU=0 Radius=19 StartAngle=1.5708 EndAngle=3.14159
    g2: LineSegment StartX=117 StartY=38 StartZ=0 EndX=117 EndY=19 EndZ=0
    g3: LineSegment StartX=98 StartY=1.0161e-12 StartZ=0 EndX=5.22862e-06 EndY=1.0161e-12 EndZ=0
    g4: LineSegment StartX=5.22862e-06 StartY=19 StartZ=0 EndX=5.22862e-06 EndY=1.0161e-12 EndZ=0
    g5: ArcOfCircle CenterX=98 CenterY=19 CenterZ=0 NormalX=0 NormalY=0 NormalZ=1 AngleXU=0 Radius=19 StartAngle=4.71239 EndAngle=6.28319
  constraints (16):
    c: Horizontal(g0)
    c: Distance(g0) = 98
    c: Coincident(g1,g0)
    c: Block(g1)
    c: Coincident(g2,g0)
    c: Vertical(g2)
    c: Distance(g2) = 19
    c: Horizontal(g3)
    c: Coincident(g4,g1)
    c: Vertical(g4)
    c: Coincident(g3,g4)
    c: Block(g3)
    c: Coincident(g5,g2)
    c: Coincident(g5,g3)
    c: Block(g0)
    c: Block(g5)
FEATURE [Part::Extrusion] Extrude070  label="sideA004"
  Base = -> Sketch080
  Dir = (0,0,1)
  DirMode = 2
  FaceMakerClass = Part::FaceMakerBullseye
  LengthFwd = 3
  LengthRev = 0
  Placement = pos=(0,0,-2.7) rot=(0,0,1;0rad)
  Solid = true
  Symmetric = false
FEATURE [Sketcher::SketchObject] Sketch081
  FullyConstrained = true
  Placement = pos=(117,19,0) rot=(0.57735,0.57735,0.57735;2.0944rad)
  sketch-geometry (8):
    g0: LineSegment StartX=-49.19 StartY=63.5 StartZ=0 EndX=-49.19 EndY=60.5 EndZ=0
    g1: LineSegment StartX=-49.19 StartY=11.5 StartZ=0 EndX=-49.19 EndY=8.5 EndZ=0
    g2: ArcOfCircle CenterX=-1.5 CenterY=62 CenterZ=0 NormalX=0 NormalY=0 NormalZ=1 AngleXU=0 Radius=1.5 StartAngle=4.71239 EndAngle=7.85398
    g3: ArcOfCircle CenterX=-1.5 CenterY=10 CenterZ=0 NormalX=0 NormalY=0 NormalZ=1 AngleXU=0 Radius=1.5 StartAngle=4.71239 EndAngle=7.85398
    g4: LineSegment StartX=-49.19 StartY=63.5 StartZ=0 EndX=-1.5 EndY=63.5 EndZ=0
    g5: LineSegment StartX=-49.19 StartY=60.5 StartZ=0 EndX=-1.5 EndY=60.5 EndZ=0
    g6: LineSegment StartX=-49.19 StartY=11.5 StartZ=0 EndX=-1.5 EndY=11.5 EndZ=0
    g7: LineSegment StartX=-49.19 StartY=8.5 StartZ=0 EndX=-1.5 EndY=8.5 EndZ=0
  constraints (19):
    c: Vertical(g0)
    c: Distance(g0) = 3
    c: Vertical(g1)
    c: Block(g1)
    c: Block(g2)
    c: Block(g3)
    c: Block(g0)
    c: Coincident(g4,g0)
    c: Coincident(g4,g2)
    c: Horizontal(g4)
    c: Coincident(g5,g0)
    c: Coincident(g5,g2)
    c: Horizontal(g5)
    c: Coincident(g6,g1)
    c: Coincident(g6,g3)
    c: Horizontal(g6)
    c: Coincident(g7,g1)
    c: Coincident(g7,g3)
    c: Horizontal(g7)
FEATURE [Part::Extrusion] Extrude071  label="sideB004"
  Base = -> Sketch079
  Dir = (0,0,1)
  DirMode = 2
  FaceMakerClass = Part::FaceMakerBullseye
  LengthFwd = 3
  LengthRev = 0
  Placement = pos=(0,0,71.7) rot=(0,0,1;0rad)
  Solid = true
  Symmetric = false
FEATURE [Part::MultiFuse] Fusion152  label="removeFromBottom004"
  Placement = pos=(2,0,0) rot=(0,0,1;0rad)
  Shapes = -> [Extrude070,Extrude071]
FEATURE [Part::Extrusion] Extrude072
  Base = -> Sketch081
  Dir = (1,0,0)
  DirMode = 2
  FaceMakerClass = Part::FaceMakerBullseye
  LengthFwd = 10
  LengthRev = 0
  Solid = true
  Symmetric = false
FEATURE [Part::Fillet] Fillet059  label="removeFromtMoreFrontCaseScrewRetainers004"
  Base = -> Extrude072
  Edges = 4 edges r=1.49: [Edge6,Edge11,Edge18,Edge23]
  Placement = pos=(-12,0,0) rot=(0,0,1;0rad)
FEATURE [Sketcher::SketchObject] Sketch082
  FullyConstrained = true
  Placement = pos=(117,19,0) rot=(0.57735,0.57735,0.57735;2.0944rad)
  sketch-geometry (8):
    g0: LineSegment StartX=-49.19 StartY=69.25 StartZ=0 EndX=-49.19 EndY=66.25 EndZ=0
    g1: LineSegment StartX=-49.19 StartY=5.75 StartZ=0 EndX=-49.19 EndY=2.75 EndZ=0
    g2: ArcOfCircle CenterX=-1.5 CenterY=67.75 CenterZ=0 NormalX=0 NormalY=0 NormalZ=1 AngleXU=0 Radius=1.5 StartAngle=4.71239 EndAngle=7.85398
    g3: ArcOfCircle CenterX=-1.5 CenterY=4.25 CenterZ=0 NormalX=0 NormalY=0 NormalZ=1 AngleXU=0 Radius=1.5 StartAngle=4.71239 EndAngle=7.85398
    g4: LineSegment StartX=-49.19 StartY=69.25 StartZ=0 EndX=-1.5 EndY=69.25 EndZ=0
    g5: LineSegment StartX=-49.19 StartY=66.25 StartZ=0 EndX=-1.5 EndY=66.25 EndZ=0
    g6: LineSegment StartX=-49.19 StartY=5.75 StartZ=0 EndX=-1.5 EndY=5.75 EndZ=0
    g7: LineSegment StartX=-49.19 StartY=2.75 StartZ=0 EndX=-1.5 EndY=2.75 EndZ=0
  constraints (19):
    c: Vertical(g0)
    c: Distance(g0) = 3
    c: Block(g0)
    c: Vertical(g1)
    c: Block(g2)
    c: Block(g3)
    c: Block(g1)
    c: Coincident(g4,g0)
    c: Coincident(g4,g2)
    c: Horizontal(g4)
    c: Coincident(g5,g0)
    c: Coincident(g5,g2)
    c: Horizontal(g5)
    c: Coincident(g6,g1)
    c: Coincident(g6,g3)
    c: Horizontal(g6)
    c: Coincident(g7,g1)
    c: Coincident(g7,g3)
    c: Horizontal(g7)
FEATURE [Part::Extrusion] Extrude073
  Base = -> Sketch082
  Dir = (1,0,0)
  DirMode = 2
  FaceMakerClass = Part::FaceMakerBullseye
  LengthFwd = 10
  LengthRev = 0
  Solid = true
  Symmetric = false
FEATURE [Part::Fillet] Fillet060  label="removeFromtMoreFrontCaseScrewRetainers005"
  Base = -> Extrude073
  Edges = 4 edges r=1.49: [Edge6,Edge11,Edge18,Edge23]
  Placement = pos=(-4,0,0) rot=(0,0,1;0rad)
FEATURE [Part::Revolution] Revolve163  label="backCaseScrewRetainer004"
  Angle = 360
  Axis = (0,1,0)
  Base = (0,0,0)
  FaceMakerClass = Part::FaceMakerBullseye
  Placement = pos=(12.5,3,62) rot=(0,0,1;0rad)
  Solid = false
  Source = -> Face149
  Symmetric = false
FEATURE [Part::Revolution] Revolve164  label="frontCaseScrewRetainer006"
  Angle = 360
  Axis = (0,1,0)
  Base = (0,0,0)
  FaceMakerClass = Part::FaceMakerBullseye
  Placement = pos=(89.5,3,68.5) rot=(0,0,1;0rad)
  Solid = false
  Source = -> Face151
  Symmetric = false
FEATURE [Part::Revolution] Revolve165  label="frontCaseScrewRetainer007"
  Angle = 360
  Axis = (0,1,0)
  Base = (0,0,0)
  FaceMakerClass = Part::FaceMakerBullseye
  Placement = pos=(89.5,3,3.5) rot=(0,0,1;0rad)
  Solid = false
  Source = -> Face152
  Symmetric = false
FEATURE [Part::Revolution] Revolve166  label="backCaseScrewRetainer005"
  Angle = 360
  Axis = (0,1,0)
  Base = (0,0,0)
  FaceMakerClass = Part::FaceMakerBullseye
  Placement = pos=(12.5,3,10) rot=(0,0,1;0rad)
  Solid = false
  Source = -> Face150
  Symmetric = false
FEATURE [Part::Revolution] Revolve167  label="moreFrontCaseScrewRetainer006"
  Angle = 360
  Axis = (0,1,0)
  Base = (0,0,0)
  FaceMakerClass = Part::FaceMakerBullseye
  Placement = pos=(109.5,4.5,68.5) rot=(0,0,1;0rad)
  Solid = false
  Source = -> Face153
  Symmetric = false
FEATURE [Part::Revolution] Revolve168  label="moreFrontCaseScrewRetainer007"
  Angle = 360
  Axis = (0,1,0)
  Base = (0,0,0)
  FaceMakerClass = Part::FaceMakerBullseye
  Placement = pos=(109.5,4.5,3.5) rot=(0,0,1;0rad)
  Solid = false
  Source = -> Face154
  Symmetric = false
FEATURE [Part::MultiFuse] Fusion151  label="screwRetainers003"
  Shapes = -> [Revolve168,Revolve167,Revolve166,Revolve165,Revolve164,Revolve163]
FEATURE [Part::Cut] Cut069  label="screwRetainers004"
  Base = -> Fusion151
  Tool = -> Fusion152
FEATURE [Part::Cut] Cut070
  Base = -> Cut069
  Tool = -> Fillet060
FEATURE [Part::Cut] Cut071  label="screwPillars001"
  Base = -> Cut070
  Tool = -> Fillet059
FEATURE [Part::MultiFuse] Fusion153  label="bottom024"
  Shapes = -> [Fusion149,Cut071]
FEATURE [Part::Cylinder] Cylinder067
  Angle = 360
  AttacherType = Attacher::AttachEngine3D
  Height = 10
  Placement = pos=(20.65,12,4.68) rot=(1,0,0;1.5708rad)
  Radius = 2
FEATURE [Part::Cylinder] Cylinder068
  Angle = 360
  AttacherType = Attacher::AttachEngine3D
  Height = 10
  Placement = pos=(20.65,12,67.38) rot=(1,0,0;1.5708rad)
  Radius = 2
FEATURE [Part::Cylinder] Cylinder069
  Angle = 360
  AttacherType = Attacher::AttachEngine3D
  Height = 10
  Placement = pos=(77.15,12,67.38) rot=(1,0,0;1.5708rad)
  Radius = 2
FEATURE [Part::Cylinder] Cylinder070
  Angle = 360
  AttacherType = Attacher::AttachEngine3D
  Height = 10
  Placement = pos=(77.15,12,4.68) rot=(1,0,0;1.5708rad)
  Radius = 2
FEATURE [Part::MultiFuse] Fusion154  label="removeFromThreadedInsertHousing001"
  Shapes = -> [Cylinder069,Cylinder068,Cylinder067,Cylinder070]
FEATURE [Part::Cut] Cut072  label="bottom025"
  Base = -> Fusion153
  Tool = -> Fusion154
